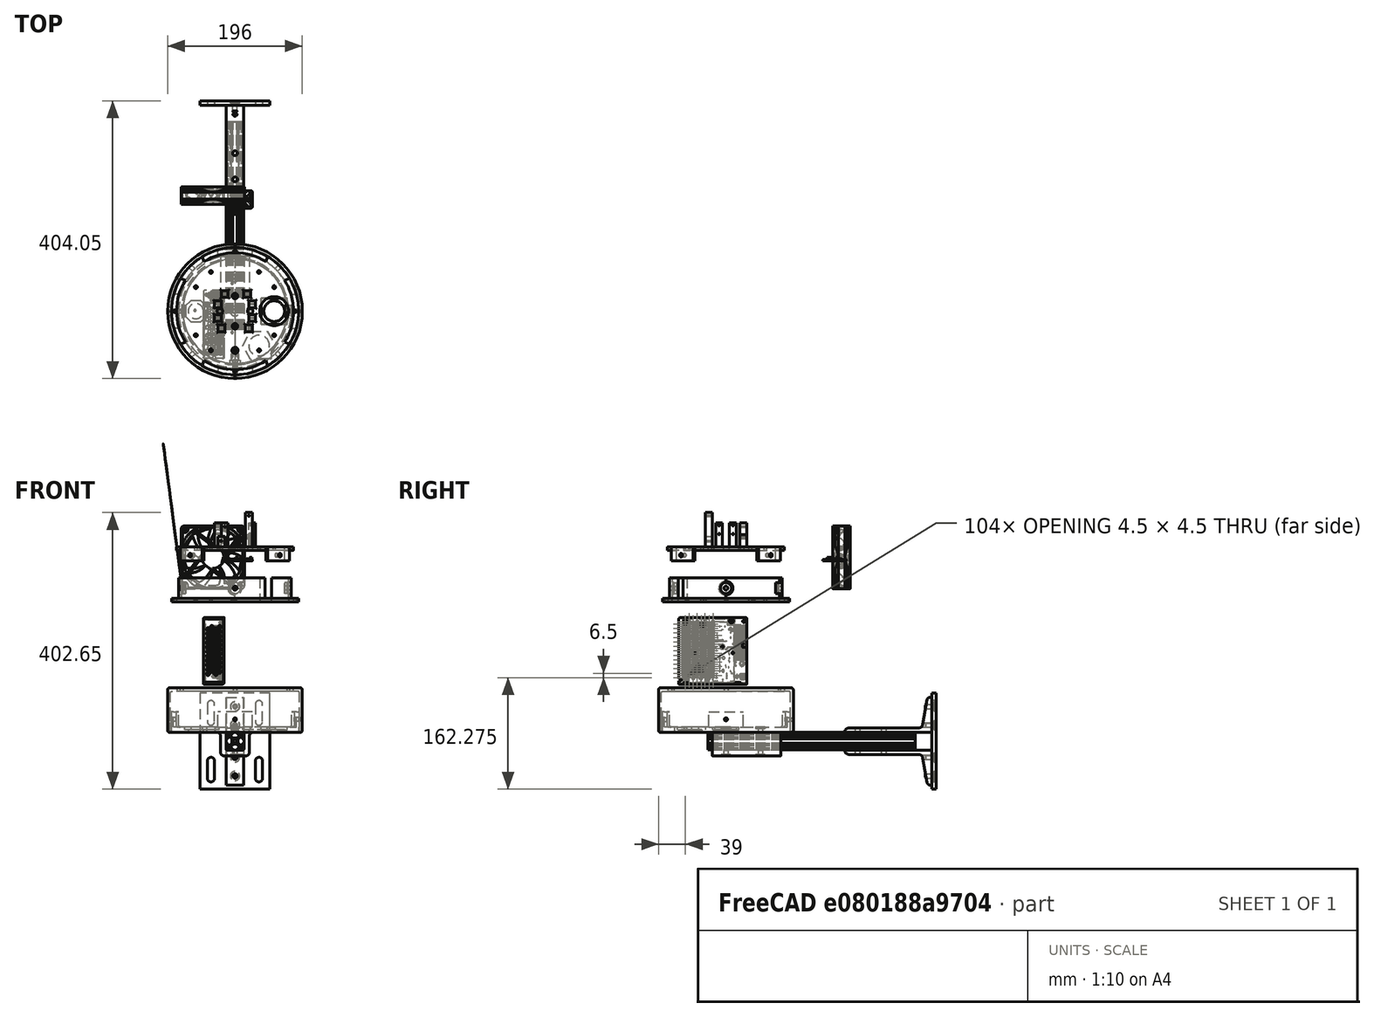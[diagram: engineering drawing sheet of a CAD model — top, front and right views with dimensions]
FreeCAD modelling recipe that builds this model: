
FCSTD DOCUMENT  (FreeCAD 0.20R29410 (Git))
Label: lightModuleV2_2023_11_27
License: All rights reserved
LicenseURL: http://en.wikipedia.org/wiki/All_rights_reserved
objects: Part::Cylinder×131, Sketcher::SketchObject×117, Part::Feature×117, Part::MultiFuse×107, Part::Cut×74, Part::Extrusion×53, Part::Loft×32, Part::Fillet×25, Part::Box×17, App::Part×14, Part::FeaturePython×10, Part::Sphere×4, Mesh::Feature×3, Part::Compound×1, Part::Cone×1, Part::Compound2×1, Part::MultiCommon×1
note: 690 computed .brp shape members not serialized (recipe doc carries the construction recipe); baked Part::Feature solids carry a one-line shape summary decoded from their .brp

FEATURE [Mesh::Feature] Odroid_H004  label="Odroid-H004"
  Placement = pos=(15,-110,-70) rot=(0.57735,-0.57735,0.57735;4.18879rad)
FEATURE [Sketcher::SketchObject] Sketch  label="top"
  FullyConstrained = true
  sketch-geometry (24):
    g0: Circle CenterX=0 CenterY=-150 CenterZ=0 NormalX=0 NormalY=0 NormalZ=1 AngleXU=0 Radius=98
    g1: Circle CenterX=-92 CenterY=-150 CenterZ=0 NormalX=0 NormalY=0 NormalZ=1 AngleXU=0 Radius=2
    g2: Circle CenterX=-57 CenterY=-115 CenterZ=0 NormalX=0 NormalY=0 NormalZ=1 AngleXU=0 Radius=2
    g3: Circle CenterX=-22 CenterY=-150 CenterZ=0 NormalX=0 NormalY=0 NormalZ=1 AngleXU=0 Radius=2
    g4: Circle CenterX=-57 CenterY=-185 CenterZ=0 NormalX=0 NormalY=0 NormalZ=1 AngleXU=0 Radius=2
    g5: Circle CenterX=0 CenterY=-172 CenterZ=0 NormalX=0 NormalY=0 NormalZ=1 AngleXU=0 Radius=2
    g6: Circle CenterX=0 CenterY=-242 CenterZ=0 NormalX=0 NormalY=0 NormalZ=1 AngleXU=0 Radius=2
    g7: Circle CenterX=-35 CenterY=-207 CenterZ=0 NormalX=0 NormalY=0 NormalZ=1 AngleXU=0 Radius=2
    g8: Circle CenterX=35 CenterY=-207 CenterZ=0 NormalX=0 NormalY=0 NormalZ=1 AngleXU=0 Radius=2
    g9: Circle CenterX=57 CenterY=-185 CenterZ=0 NormalX=0 NormalY=0 NormalZ=1 AngleXU=0 Radius=2
    g10: Circle CenterX=22 CenterY=-150 CenterZ=0 NormalX=0 NormalY=0 NormalZ=1 AngleXU=0 Radius=2
    g11: Circle CenterX=57 CenterY=-115 CenterZ=0 NormalX=0 NormalY=0 NormalZ=1 AngleXU=0 Radius=2
    g12: Circle CenterX=92 CenterY=-150 CenterZ=0 NormalX=0 NormalY=0 NormalZ=1 AngleXU=0 Radius=2
    g13: Circle CenterX=0 CenterY=-58 CenterZ=0 NormalX=0 NormalY=0 NormalZ=1 AngleXU=0 Radius=2
    g14: Circle CenterX=0 CenterY=-207 CenterZ=0 NormalX=0 NormalY=0 NormalZ=1 AngleXU=0 Radius=25
    g15: Circle CenterX=57 CenterY=-150 CenterZ=0 NormalX=0 NormalY=0 NormalZ=1 AngleXU=0 Radius=25
    g16: Circle CenterX=0 CenterY=-93 CenterZ=0 NormalX=0 NormalY=0 NormalZ=1 AngleXU=0 Radius=25
    g17: Circle CenterX=-35 CenterY=-93 CenterZ=0 NormalX=0 NormalY=0 NormalZ=1 AngleXU=0 Radius=2
    g18: Circle CenterX=35 CenterY=-93 CenterZ=0 NormalX=0 NormalY=0 NormalZ=1 AngleXU=0 Radius=2
    g19: Circle CenterX=0 CenterY=-128 CenterZ=0 NormalX=0 NormalY=0 NormalZ=1 AngleXU=0 Radius=2
    g20: LineSegment StartX=-75.25 StartY=-129.25 StartZ=0 EndX=-38.75 EndY=-129.25 EndZ=0
    g21: LineSegment StartX=-38.75 StartY=-129.25 StartZ=0 EndX=-38.75 EndY=-170.75 EndZ=0
    g22: LineSegment StartX=-38.75 StartY=-170.75 StartZ=0 EndX=-75.25 EndY=-170.75 EndZ=0
    g23: LineSegment StartX=-75.25 StartY=-170.75 StartZ=0 EndX=-75.25 EndY=-129.25 EndZ=0
  constraints (72):
    c: PointOnObject(g0,g-2)
    c: Radius(g0) = 98
    c: DistanceY(g0) = -150
    c: PointOnObject(g5,g-2)
    c: PointOnObject(g6,g-2)
    c: PointOnObject(g13,g-2)
    c: PointOnObject(g19,g-2)
    c: Equal(g6,g7)
    c: Equal(g6,g4)
    c: Equal(g6,g1)
    c: Equal(g6,g2)
    c: Equal(g6,g3)
    c: Equal(g6,g19)
    c: Equal(g6,g5)
    c: Equal(g6,g8)
    c: Equal(g6,g9)
    c: Equal(g6,g10)
    c: Equal(g6,g12)
    c: Equal(g6,g11)
    c: Equal(g6,g17)
    c: Equal(g6,g18)
    c: Equal(g6,g13)
    c: Radius(g6) = 2
    c: DistanceY(g12,g0) = 0
    c: DistanceY(g10,g0) = 0
    c: DistanceY(g0,g3) = 0
    c: DistanceY(g1,g3) = 0
    c: Equal(g15,g14)
    c: Equal(g15,g16)
    c: Radius(g15) = 25
    c: Coincident(g20,g21)
    c: Coincident(g21,g22)
    c: Coincident(g22,g23)
    c: Coincident(g23,g20)
    c: Horizontal(g20)
    c: Horizontal(g22)
    c: Vertical(g21)
    c: Vertical(g23)
    c: DistanceX(g20) = -38.75
    c: DistanceY(g0,g20) = 20.75
    c: DistanceY(g21,g0) = 20.75
    c: DistanceX(g22,g0) = 75.25
    c: DistanceX(g14,g0) = 0
    c: DistanceX(g0,g15) = 57
    c: DistanceY(g15,g0) = 0
    c: DistanceY(g0,g16) = 57
    c: DistanceX(g16,g0) = 0
    c: DistanceX(g0,g10) = 22
    c: DistanceX(g3,g0) = 22
    c: DistanceX(g1,g0) = 92
    c: DistanceX(g15,g12) = 35
    c: DistanceX(g16,g18) = 35
    c: DistanceX(g17,g16) = 35
    c: DistanceX(g7,g14) = 35
    c: DistanceX(g14,g8) = 35
    c: DistanceX(g9,g15) = 0
    c: DistanceX(g15,g11) = 0
    c: DistanceX(g2,g0) = 57
    c: DistanceY(g18,g16) = 0
    c: DistanceY(g16,g17) = 0
    c: DistanceY(g19,g16) = 35
    c: DistanceY(g16,g13) = 35
    c: DistanceY(g4,g0) = 35
    c: DistanceY(g0,g2) = 35
    c: DistanceY(g14,g5) = 35
    c: DistanceY(g6,g14) = 35
    c: DistanceY(g8,g14) = 0
    c: DistanceY(g14,g7) = 0
    c: DistanceY(g9,g15) = 35
    c: DistanceY(g15,g11) = 35
    c: DistanceX(g4,g2) = 0
    c: DistanceY(g14,g0) = 57
FEATURE [Part::Cylinder] Cylinder036
  Angle = 360
  AttacherType = Attacher::AttachEngine3D
  FirstAngle = 0
  Height = 10
  Placement = pos=(0,-21,0) rot=(0,0,1;0rad)
  Radius = 2
  SecondAngle = 0
FEATURE [Part::Cylinder] Cylinder037
  Angle = 360
  AttacherType = Attacher::AttachEngine3D
  FirstAngle = 0
  Height = 10
  Placement = pos=(20,-21,0) rot=(0,0,1;0rad)
  Radius = 2
  SecondAngle = 0
FEATURE [Part::Cylinder] Cylinder038
  Angle = 360
  AttacherType = Attacher::AttachEngine3D
  FirstAngle = 0
  Height = 10
  Placement = pos=(0,-21,0) rot=(0,0,1;0rad)
  Radius = 2
  SecondAngle = 0
FEATURE [Part::Cylinder] Cylinder039
  Angle = 360
  AttacherType = Attacher::AttachEngine3D
  FirstAngle = 0
  Height = 10
  Placement = pos=(20,-21,0) rot=(0,0,1;0rad)
  Radius = 2
  SecondAngle = 0
FEATURE [Part::Cylinder] Cylinder040  label="base002"
  Angle = 360
  AttacherType = Attacher::AttachEngine3D
  FirstAngle = 0
  Height = 5
  Placement = pos=(5,0,70) rot=(0,0,1;0rad)
  Radius = 40
  SecondAngle = 0
FEATURE [Part::Cylinder] Cylinder041  label="baseCut001"
  Angle = 360
  AttacherType = Attacher::AttachEngine3D
  FirstAngle = 0
  Height = 7
  Placement = pos=(5,0,74) rot=(0,0,1;0rad)
  Radius = 24
  SecondAngle = 0
FEATURE [Part::Cylinder] Cylinder042  label="wireCUt002"
  Angle = 360
  AttacherType = Attacher::AttachEngine3D
  FirstAngle = 0
  Height = 10
  Placement = pos=(-5,0,70) rot=(0,0,1;0rad)
  Radius = 2
  SecondAngle = 0
FEATURE [Part::Cylinder] Cylinder043  label="wireCUt003"
  Angle = 360
  AttacherType = Attacher::AttachEngine3D
  FirstAngle = 0
  Height = 10
  Placement = pos=(15,0,70) rot=(0,0,1;0rad)
  Radius = 2
  SecondAngle = 0
FEATURE [Part::Cylinder] Cylinder044  label="m3Cuts002"
  Angle = 360
  AttacherType = Attacher::AttachEngine3D
  FirstAngle = 0
  Height = 10
  Placement = pos=(5,-9,70) rot=(0,0,1;0rad)
  Radius = 1.75
  SecondAngle = 0
FEATURE [Part::Cylinder] Cylinder045  label="m3Cuts003"
  Angle = 360
  AttacherType = Attacher::AttachEngine3D
  FirstAngle = 0
  Height = 10
  Placement = pos=(5,9,70) rot=(0,0,1;0rad)
  Radius = 1.75
  SecondAngle = 0
FEATURE [Part::Cylinder] Cylinder046  label="m2HeatSetInsets004"
  Angle = 360
  AttacherType = Attacher::AttachEngine3D
  FirstAngle = 0
  Height = 10
  Placement = pos=(-30,0,65) rot=(0,0,1;0rad)
  Radius = 1.6
  SecondAngle = 0
FEATURE [Part::Cylinder] Cylinder047  label="m2HeatSetInsets005"
  Angle = 360
  AttacherType = Attacher::AttachEngine3D
  FirstAngle = 0
  Height = 10
  Placement = pos=(40,0,65) rot=(0,0,1;0rad)
  Radius = 1.6
  SecondAngle = 0
FEATURE [Part::Cylinder] Cylinder048  label="m2HeatSetInsets006"
  Angle = 360
  AttacherType = Attacher::AttachEngine3D
  FirstAngle = 0
  Height = 10
  Placement = pos=(5,35,65) rot=(0,0,1;0rad)
  Radius = 1.6
  SecondAngle = 0
FEATURE [Part::Cylinder] Cylinder049  label="m2HeatSetInsets007"
  Angle = 360
  AttacherType = Attacher::AttachEngine3D
  FirstAngle = 0
  Height = 10
  Placement = pos=(5,-35,65) rot=(0,0,1;0rad)
  Radius = 1.6
  SecondAngle = 0
FEATURE [Part::MultiFuse] Fusion014  label="m3HeatSetCuts003"
  Placement = pos=(-5,38.5,70) rot=(0,0,1;0rad)
  Shapes = -> [Cylinder037,Cylinder036]
FEATURE [Part::MultiFuse] Fusion015  label="m3HeatSetCuts004"
  Placement = pos=(-5,3.5,70) rot=(0,0,1;0rad)
  Shapes = -> [Cylinder039,Cylinder038]
FEATURE [Part::MultiFuse] Fusion016  label="m3HeatSetCuts005"
  Shapes = -> [Fusion015,Fusion014]
FEATURE [Part::MultiFuse] Fusion017  label="wireCuts001"
  Shapes = -> [Cylinder042,Cylinder043]
FEATURE [Part::MultiFuse] Fusion018  label="m3Cute001"
  Shapes = -> [Cylinder044,Cylinder045]
FEATURE [Part::MultiFuse] Fusion019  label="baseCUts001"
  Shapes = -> [Fusion016,Fusion017,Fusion018]
FEATURE [Part::MultiFuse] Fusion021
  Shapes = -> [Cylinder046,Cylinder047,Cylinder048,Cylinder049]
FEATURE [Part::Sphere] Sphere002  label="SphereBase001"
  Angle1 = 0
  Angle2 = 12
  Angle3 = 360
  AttacherType = Attacher::AttachEngine3D
  Placement = pos=(5,0,74) rot=(0,0,1;0rad)
  Radius = 29
FEATURE [Part::Cut] Cut006
  Base = -> Sphere002
  Tool = -> Cylinder041
FEATURE [Part::MultiFuse] Fusion020  label="base003"
  Shapes = -> [Cylinder040,Cut006]
FEATURE [Part::Cut] Cut007
  Base = -> Fusion020
  Tool = -> Fusion019
FEATURE [Part::Cut] Cut008  label="lightModule001"
  Base = -> Cut007
  Placement = pos=(-5,-207,0) rot=(0,1,0;0rad)
  Tool = -> Fusion021
FEATURE [Part::Box] Box005  label="as7265x"
  AttacherType = Attacher::AttachEngine3D
  Height = 2
  Length = 36
  Placement = pos=(-75,-170.5,110) rot=(0,0,1;0rad)
  Width = 41
FEATURE [Part::Cylinder] Cylinder050
  Angle = 360
  AttacherType = Attacher::AttachEngine3D
  FirstAngle = 0
  Height = 10
  Placement = pos=(0,-21,0) rot=(0,0,1;0rad)
  Radius = 2
  SecondAngle = 0
FEATURE [Part::Cylinder] Cylinder051
  Angle = 360
  AttacherType = Attacher::AttachEngine3D
  FirstAngle = 0
  Height = 10
  Placement = pos=(20,-21,0) rot=(0,0,1;0rad)
  Radius = 2
  SecondAngle = 0
FEATURE [Part::Cylinder] Cylinder052
  Angle = 360
  AttacherType = Attacher::AttachEngine3D
  FirstAngle = 0
  Height = 10
  Placement = pos=(0,-21,0) rot=(0,0,1;0rad)
  Radius = 2
  SecondAngle = 0
FEATURE [Part::Cylinder] Cylinder053
  Angle = 360
  AttacherType = Attacher::AttachEngine3D
  FirstAngle = 0
  Height = 10
  Placement = pos=(20,-21,0) rot=(0,0,1;0rad)
  Radius = 2
  SecondAngle = 0
FEATURE [Part::Cylinder] Cylinder054  label="base004"
  Angle = 360
  AttacherType = Attacher::AttachEngine3D
  FirstAngle = 0
  Height = 5
  Placement = pos=(5,0,70) rot=(0,0,1;0rad)
  Radius = 40
  SecondAngle = 0
FEATURE [Part::Cylinder] Cylinder055  label="baseCut002"
  Angle = 360
  AttacherType = Attacher::AttachEngine3D
  FirstAngle = 0
  Height = 7
  Placement = pos=(5,0,74) rot=(0,0,1;0rad)
  Radius = 24
  SecondAngle = 0
FEATURE [Part::Cylinder] Cylinder056  label="wireCUt004"
  Angle = 360
  AttacherType = Attacher::AttachEngine3D
  FirstAngle = 0
  Height = 10
  Placement = pos=(-5,0,70) rot=(0,0,1;0rad)
  Radius = 2
  SecondAngle = 0
FEATURE [Part::Cylinder] Cylinder057  label="wireCUt005"
  Angle = 360
  AttacherType = Attacher::AttachEngine3D
  FirstAngle = 0
  Height = 10
  Placement = pos=(15,0,70) rot=(0,0,1;0rad)
  Radius = 2
  SecondAngle = 0
FEATURE [Part::Cylinder] Cylinder058  label="m3Cuts004"
  Angle = 360
  AttacherType = Attacher::AttachEngine3D
  FirstAngle = 0
  Height = 10
  Placement = pos=(5,-9,70) rot=(0,0,1;0rad)
  Radius = 1.75
  SecondAngle = 0
FEATURE [Part::Cylinder] Cylinder059  label="m3Cuts005"
  Angle = 360
  AttacherType = Attacher::AttachEngine3D
  FirstAngle = 0
  Height = 10
  Placement = pos=(5,9,70) rot=(0,0,1;0rad)
  Radius = 1.75
  SecondAngle = 0
FEATURE [Part::Cylinder] Cylinder060  label="m2HeatSetInsets008"
  Angle = 360
  AttacherType = Attacher::AttachEngine3D
  FirstAngle = 0
  Height = 10
  Placement = pos=(-30,0,65) rot=(0,0,1;0rad)
  Radius = 1.6
  SecondAngle = 0
FEATURE [Part::Cylinder] Cylinder061  label="m2HeatSetInsets009"
  Angle = 360
  AttacherType = Attacher::AttachEngine3D
  FirstAngle = 0
  Height = 10
  Placement = pos=(40,0,65) rot=(0,0,1;0rad)
  Radius = 1.6
  SecondAngle = 0
FEATURE [Part::Cylinder] Cylinder062  label="m2HeatSetInsets010"
  Angle = 360
  AttacherType = Attacher::AttachEngine3D
  FirstAngle = 0
  Height = 10
  Placement = pos=(5,35,65) rot=(0,0,1;0rad)
  Radius = 1.6
  SecondAngle = 0
FEATURE [Part::Cylinder] Cylinder063  label="m2HeatSetInsets011"
  Angle = 360
  AttacherType = Attacher::AttachEngine3D
  FirstAngle = 0
  Height = 10
  Placement = pos=(5,-35,65) rot=(0,0,1;0rad)
  Radius = 1.6
  SecondAngle = 0
FEATURE [Part::MultiFuse] Fusion022  label="m3HeatSetCuts006"
  Placement = pos=(-5,38.5,70) rot=(0,0,1;0rad)
  Shapes = -> [Cylinder051,Cylinder050]
FEATURE [Part::MultiFuse] Fusion023  label="m3HeatSetCuts007"
  Placement = pos=(-5,3.5,70) rot=(0,0,1;0rad)
  Shapes = -> [Cylinder053,Cylinder052]
FEATURE [Part::MultiFuse] Fusion024  label="m3HeatSetCuts008"
  Shapes = -> [Fusion023,Fusion022]
FEATURE [Part::MultiFuse] Fusion025  label="wireCuts002"
  Shapes = -> [Cylinder056,Cylinder057]
FEATURE [Part::MultiFuse] Fusion026  label="m3Cute002"
  Shapes = -> [Cylinder058,Cylinder059]
FEATURE [Part::MultiFuse] Fusion027  label="baseCUts002"
  Shapes = -> [Fusion024,Fusion025,Fusion026]
FEATURE [Part::MultiFuse] Fusion029
  Shapes = -> [Cylinder060,Cylinder061,Cylinder062,Cylinder063]
FEATURE [Part::Sphere] Sphere003  label="SphereBase002"
  Angle1 = 0
  Angle2 = 12
  Angle3 = 360
  AttacherType = Attacher::AttachEngine3D
  Placement = pos=(5,0,74) rot=(0,0,1;0rad)
  Radius = 29
FEATURE [Part::Cut] Cut009
  Base = -> Sphere003
  Tool = -> Cylinder055
FEATURE [Part::MultiFuse] Fusion028  label="base005"
  Shapes = -> [Cylinder054,Cut009]
FEATURE [Part::Cut] Cut010
  Base = -> Fusion028
  Tool = -> Fusion027
FEATURE [Part::Cut] Cut011  label="lightModule002"
  Base = -> Cut010
  Placement = pos=(-62,-150,0) rot=(0,1,0;0rad)
  Tool = -> Fusion029
FEATURE [Part::Cylinder] Cylinder064
  Angle = 360
  AttacherType = Attacher::AttachEngine3D
  FirstAngle = 0
  Height = 10
  Placement = pos=(0,-21,0) rot=(0,0,1;0rad)
  Radius = 2
  SecondAngle = 0
FEATURE [Part::Cylinder] Cylinder065
  Angle = 360
  AttacherType = Attacher::AttachEngine3D
  FirstAngle = 0
  Height = 10
  Placement = pos=(20,-21,0) rot=(0,0,1;0rad)
  Radius = 2
  SecondAngle = 0
FEATURE [Part::Cylinder] Cylinder066
  Angle = 360
  AttacherType = Attacher::AttachEngine3D
  FirstAngle = 0
  Height = 10
  Placement = pos=(0,-21,0) rot=(0,0,1;0rad)
  Radius = 2
  SecondAngle = 0
FEATURE [Part::Cylinder] Cylinder067
  Angle = 360
  AttacherType = Attacher::AttachEngine3D
  FirstAngle = 0
  Height = 10
  Placement = pos=(20,-21,0) rot=(0,0,1;0rad)
  Radius = 2
  SecondAngle = 0
FEATURE [Part::Cylinder] Cylinder068  label="base006"
  Angle = 360
  AttacherType = Attacher::AttachEngine3D
  FirstAngle = 0
  Height = 5
  Placement = pos=(5,0,70) rot=(0,0,1;0rad)
  Radius = 40
  SecondAngle = 0
FEATURE [Part::Cylinder] Cylinder069  label="baseCut003"
  Angle = 360
  AttacherType = Attacher::AttachEngine3D
  FirstAngle = 0
  Height = 7
  Placement = pos=(5,0,74) rot=(0,0,1;0rad)
  Radius = 24
  SecondAngle = 0
FEATURE [Part::Cylinder] Cylinder070  label="wireCUt006"
  Angle = 360
  AttacherType = Attacher::AttachEngine3D
  FirstAngle = 0
  Height = 10
  Placement = pos=(-5,0,70) rot=(0,0,1;0rad)
  Radius = 2
  SecondAngle = 0
FEATURE [Part::Cylinder] Cylinder071  label="wireCUt007"
  Angle = 360
  AttacherType = Attacher::AttachEngine3D
  FirstAngle = 0
  Height = 10
  Placement = pos=(15,0,70) rot=(0,0,1;0rad)
  Radius = 2
  SecondAngle = 0
FEATURE [Part::Cylinder] Cylinder072  label="m3Cuts006"
  Angle = 360
  AttacherType = Attacher::AttachEngine3D
  FirstAngle = 0
  Height = 10
  Placement = pos=(5,-9,70) rot=(0,0,1;0rad)
  Radius = 1.75
  SecondAngle = 0
FEATURE [Part::Cylinder] Cylinder073  label="m3Cuts007"
  Angle = 360
  AttacherType = Attacher::AttachEngine3D
  FirstAngle = 0
  Height = 10
  Placement = pos=(5,9,70) rot=(0,0,1;0rad)
  Radius = 1.75
  SecondAngle = 0
FEATURE [Part::Cylinder] Cylinder074  label="m2HeatSetInsets012"
  Angle = 360
  AttacherType = Attacher::AttachEngine3D
  FirstAngle = 0
  Height = 10
  Placement = pos=(-30,0,65) rot=(0,0,1;0rad)
  Radius = 1.6
  SecondAngle = 0
FEATURE [Part::Cylinder] Cylinder075  label="m2HeatSetInsets013"
  Angle = 360
  AttacherType = Attacher::AttachEngine3D
  FirstAngle = 0
  Height = 10
  Placement = pos=(40,0,65) rot=(0,0,1;0rad)
  Radius = 1.6
  SecondAngle = 0
FEATURE [Part::Cylinder] Cylinder076  label="m2HeatSetInsets014"
  Angle = 360
  AttacherType = Attacher::AttachEngine3D
  FirstAngle = 0
  Height = 10
  Placement = pos=(5,35,65) rot=(0,0,1;0rad)
  Radius = 1.6
  SecondAngle = 0
FEATURE [Part::Cylinder] Cylinder077  label="m2HeatSetInsets015"
  Angle = 360
  AttacherType = Attacher::AttachEngine3D
  FirstAngle = 0
  Height = 10
  Placement = pos=(5,-35,65) rot=(0,0,1;0rad)
  Radius = 1.6
  SecondAngle = 0
FEATURE [Part::MultiFuse] Fusion030  label="m3HeatSetCuts009"
  Placement = pos=(-5,38.5,70) rot=(0,0,1;0rad)
  Shapes = -> [Cylinder065,Cylinder064]
FEATURE [Part::MultiFuse] Fusion031  label="m3HeatSetCuts010"
  Placement = pos=(-5,3.5,70) rot=(0,0,1;0rad)
  Shapes = -> [Cylinder067,Cylinder066]
FEATURE [Part::MultiFuse] Fusion032  label="m3HeatSetCuts011"
  Shapes = -> [Fusion031,Fusion030]
FEATURE [Part::MultiFuse] Fusion033  label="wireCuts003"
  Shapes = -> [Cylinder070,Cylinder071]
FEATURE [Part::MultiFuse] Fusion034  label="m3Cute003"
  Shapes = -> [Cylinder072,Cylinder073]
FEATURE [Part::MultiFuse] Fusion035  label="baseCUts003"
  Shapes = -> [Fusion032,Fusion033,Fusion034]
FEATURE [Part::MultiFuse] Fusion037
  Shapes = -> [Cylinder074,Cylinder075,Cylinder076,Cylinder077]
FEATURE [Part::Sphere] Sphere004  label="SphereBase003"
  Angle1 = 0
  Angle2 = 12
  Angle3 = 360
  AttacherType = Attacher::AttachEngine3D
  Placement = pos=(5,0,74) rot=(0,0,1;0rad)
  Radius = 29
FEATURE [Part::Cut] Cut012
  Base = -> Sphere004
  Tool = -> Cylinder069
FEATURE [Part::MultiFuse] Fusion036  label="base007"
  Shapes = -> [Cylinder068,Cut012]
FEATURE [Part::Cut] Cut013
  Base = -> Fusion036
  Tool = -> Fusion035
FEATURE [Part::Cut] Cut014  label="lightModule003"
  Base = -> Cut013
  Placement = pos=(52,-150,0) rot=(0,1,0;0rad)
  Tool = -> Fusion037
FEATURE [Part::Cylinder] Cylinder078
  Angle = 360
  AttacherType = Attacher::AttachEngine3D
  FirstAngle = 0
  Height = 10
  Placement = pos=(0,-21,0) rot=(0,0,1;0rad)
  Radius = 2
  SecondAngle = 0
FEATURE [Part::Cylinder] Cylinder079
  Angle = 360
  AttacherType = Attacher::AttachEngine3D
  FirstAngle = 0
  Height = 10
  Placement = pos=(20,-21,0) rot=(0,0,1;0rad)
  Radius = 2
  SecondAngle = 0
FEATURE [Part::Cylinder] Cylinder080
  Angle = 360
  AttacherType = Attacher::AttachEngine3D
  FirstAngle = 0
  Height = 10
  Placement = pos=(0,-21,0) rot=(0,0,1;0rad)
  Radius = 2
  SecondAngle = 0
FEATURE [Part::Cylinder] Cylinder081
  Angle = 360
  AttacherType = Attacher::AttachEngine3D
  FirstAngle = 0
  Height = 10
  Placement = pos=(20,-21,0) rot=(0,0,1;0rad)
  Radius = 2
  SecondAngle = 0
FEATURE [Part::Cylinder] Cylinder082  label="base008"
  Angle = 360
  AttacherType = Attacher::AttachEngine3D
  FirstAngle = 0
  Height = 5
  Placement = pos=(5,0,70) rot=(0,0,1;0rad)
  Radius = 40
  SecondAngle = 0
FEATURE [Part::Cylinder] Cylinder083  label="baseCut004"
  Angle = 360
  AttacherType = Attacher::AttachEngine3D
  FirstAngle = 0
  Height = 7
  Placement = pos=(5,0,74) rot=(0,0,1;0rad)
  Radius = 24
  SecondAngle = 0
FEATURE [Part::Cylinder] Cylinder084  label="wireCUt008"
  Angle = 360
  AttacherType = Attacher::AttachEngine3D
  FirstAngle = 0
  Height = 10
  Placement = pos=(-5,0,70) rot=(0,0,1;0rad)
  Radius = 2
  SecondAngle = 0
FEATURE [Part::Cylinder] Cylinder085  label="wireCUt009"
  Angle = 360
  AttacherType = Attacher::AttachEngine3D
  FirstAngle = 0
  Height = 10
  Placement = pos=(15,0,70) rot=(0,0,1;0rad)
  Radius = 2
  SecondAngle = 0
FEATURE [Part::Cylinder] Cylinder086  label="m3Cuts008"
  Angle = 360
  AttacherType = Attacher::AttachEngine3D
  FirstAngle = 0
  Height = 10
  Placement = pos=(5,-9,70) rot=(0,0,1;0rad)
  Radius = 1.75
  SecondAngle = 0
FEATURE [Part::Cylinder] Cylinder087  label="m3Cuts009"
  Angle = 360
  AttacherType = Attacher::AttachEngine3D
  FirstAngle = 0
  Height = 10
  Placement = pos=(5,9,70) rot=(0,0,1;0rad)
  Radius = 1.75
  SecondAngle = 0
FEATURE [Part::Cylinder] Cylinder088  label="m2HeatSetInsets016"
  Angle = 360
  AttacherType = Attacher::AttachEngine3D
  FirstAngle = 0
  Height = 10
  Placement = pos=(-30,0,65) rot=(0,0,1;0rad)
  Radius = 1.6
  SecondAngle = 0
FEATURE [Part::Cylinder] Cylinder089  label="m2HeatSetInsets017"
  Angle = 360
  AttacherType = Attacher::AttachEngine3D
  FirstAngle = 0
  Height = 10
  Placement = pos=(40,0,65) rot=(0,0,1;0rad)
  Radius = 1.6
  SecondAngle = 0
FEATURE [Part::Cylinder] Cylinder090  label="m2HeatSetInsets018"
  Angle = 360
  AttacherType = Attacher::AttachEngine3D
  FirstAngle = 0
  Height = 10
  Placement = pos=(5,35,65) rot=(0,0,1;0rad)
  Radius = 1.6
  SecondAngle = 0
FEATURE [Part::Cylinder] Cylinder091  label="m2HeatSetInsets019"
  Angle = 360
  AttacherType = Attacher::AttachEngine3D
  FirstAngle = 0
  Height = 10
  Placement = pos=(5,-35,65) rot=(0,0,1;0rad)
  Radius = 1.6
  SecondAngle = 0
FEATURE [Part::MultiFuse] Fusion038  label="m3HeatSetCuts012"
  Placement = pos=(-5,38.5,70) rot=(0,0,1;0rad)
  Shapes = -> [Cylinder079,Cylinder078]
FEATURE [Part::MultiFuse] Fusion039  label="m3HeatSetCuts013"
  Placement = pos=(-5,3.5,70) rot=(0,0,1;0rad)
  Shapes = -> [Cylinder081,Cylinder080]
FEATURE [Part::MultiFuse] Fusion040  label="m3HeatSetCuts014"
  Shapes = -> [Fusion039,Fusion038]
FEATURE [Part::MultiFuse] Fusion041  label="wireCuts004"
  Shapes = -> [Cylinder084,Cylinder085]
FEATURE [Part::MultiFuse] Fusion042  label="m3Cute004"
  Shapes = -> [Cylinder086,Cylinder087]
FEATURE [Part::MultiFuse] Fusion043  label="baseCUts004"
  Shapes = -> [Fusion040,Fusion041,Fusion042]
FEATURE [Part::MultiFuse] Fusion045
  Shapes = -> [Cylinder088,Cylinder089,Cylinder090,Cylinder091]
FEATURE [Part::Sphere] Sphere005  label="SphereBase004"
  Angle1 = 0
  Angle2 = 12
  Angle3 = 360
  AttacherType = Attacher::AttachEngine3D
  Placement = pos=(5,0,74) rot=(0,0,1;0rad)
  Radius = 29
FEATURE [Part::Cut] Cut015
  Base = -> Sphere005
  Tool = -> Cylinder083
FEATURE [Part::MultiFuse] Fusion044  label="base009"
  Shapes = -> [Cylinder082,Cut015]
FEATURE [Part::Cut] Cut016
  Base = -> Fusion044
  Tool = -> Fusion043
FEATURE [Part::Cut] Cut017  label="lightModule004"
  Base = -> Cut016
  Placement = pos=(-5,-93,0) rot=(0,1,0;0rad)
  Tool = -> Fusion045
FEATURE [Part::MultiFuse] Fusion  label="lightModules"
  Placement = pos=(0,0,30) rot=(0,0,1;0rad)
  Shapes = -> [Cut008,Cut011,Cut014,Cut017]
FEATURE [Part::Extrusion] Extrude  label="top001"
  Base = -> Sketch
  Dir = (0,0,1)
  DirMode = 2
  FaceMakerClass = Part::FaceMakerBullseye
  LengthFwd = 5
  LengthRev = 0
  Placement = pos=(0,0,100) rot=(0,0,1;0rad)
  Solid = true
  Symmetric = false
FEATURE [Part::Feature] Part__Feature  label="elpCamera"
  Placement = pos=(57,-150,90) rot=(0,0,1;0rad)
  shape: bbox 38 x 38 x 25.12 mm, 164 faces (baked)
FEATURE [Part::FeaturePython] Tube  label="tube001"  # WARN: FeaturePython — macro-defined, semantics opaque (R4)
  AttacherType = Attacher::AttachEngine3D
  Height = 20
  InnerRadius = 94
  OuterRadius = 98
  Placement = pos=(0,-150,80) rot=(0,0,1;0rad)
FEATURE [Part::Feature] Part__Feature010  label="veml6075_sensor"
  Placement = pos=(0,-92,105) rot=(0,0,1;0rad)
  shape: bbox 15.31 x 17.01 x 46.02 mm, 450 faces (baked)
FEATURE [Sketcher::SketchObject] Sketch001
  FullyConstrained = true
  Placement = pos=(0,0,105) rot=(0,0,1;0rad)
  sketch-geometry (14):
    g0: Circle CenterX=0 CenterY=-93 CenterZ=0 NormalX=0 NormalY=0 NormalZ=1 AngleXU=0 Radius=25
    g1: Circle CenterX=0 CenterY=-93 CenterZ=0 NormalX=0 NormalY=0 NormalZ=1 AngleXU=0 Radius=26.5
    g2: Circle CenterX=57 CenterY=-150 CenterZ=0 NormalX=0 NormalY=0 NormalZ=1 AngleXU=0 Radius=25
    g3: Circle CenterX=57 CenterY=-150 CenterZ=0 NormalX=0 NormalY=0 NormalZ=1 AngleXU=0 Radius=26.5
    g4: Circle CenterX=0 CenterY=-207 CenterZ=0 NormalX=0 NormalY=0 NormalZ=1 AngleXU=0 Radius=25
    g5: Circle CenterX=0 CenterY=-207 CenterZ=0 NormalX=0 NormalY=0 NormalZ=1 AngleXU=0 Radius=26.5
    g6: LineSegment StartX=-75.25 StartY=-129.25 StartZ=0 EndX=-38.75 EndY=-129.25 EndZ=0
    g7: LineSegment StartX=-38.75 StartY=-129.25 StartZ=0 EndX=-38.75 EndY=-170.75 EndZ=0
    g8: LineSegment StartX=-38.75 StartY=-170.75 StartZ=0 EndX=-75.25 EndY=-170.75 EndZ=0
    g9: LineSegment StartX=-75.25 StartY=-170.75 StartZ=0 EndX=-75.25 EndY=-129.25 EndZ=0
    g10: LineSegment StartX=-75.7 StartY=-128.8 StartZ=0 EndX=-38.3 EndY=-128.8 EndZ=0
    g11: LineSegment StartX=-38.3 StartY=-128.8 StartZ=0 EndX=-38.3 EndY=-171.2 EndZ=0
    g12: LineSegment StartX=-38.3 StartY=-171.2 StartZ=0 EndX=-75.7 EndY=-171.2 EndZ=0
    g13: LineSegment StartX=-75.7 StartY=-171.2 StartZ=0 EndX=-75.7 EndY=-128.8 EndZ=0
  constraints (39):
    c: PointOnObject(g0,g-2)
    c: Coincident(g1,g0)
    c: Coincident(g3,g2)
    c: PointOnObject(g4,g-2)
    c: Coincident(g5,g4)
    c: Coincident(g6,g7)
    c: Coincident(g7,g8)
    c: Coincident(g8,g9)
    c: Coincident(g9,g6)
    c: Horizontal(g6)
    c: Horizontal(g8)
    c: Vertical(g7)
    c: Vertical(g9)
    c: DistanceY(g0) = -93
    c: DistanceY(g2) = -150
    c: DistanceX(g2) = 57
    c: Equal(g0,g2)
    c: Equal(g0,g4)
    c: Radius(g0) = 25
    c: Equal(g3,g1)
    c: Equal(g3,g5)
    c: Radius(g3) = 26.5
    c: DistanceY(g4) = -207
    c: DistanceY(g7) = -170.75
    c: DistanceX(g7) = -38.75
    c: DistanceX(g6) = -75.25
    c: DistanceY(g6) = -129.25
    c: Coincident(g10,g11)
    c: Coincident(g11,g12)
    c: Coincident(g12,g13)
    c: Coincident(g13,g10)
    c: Horizontal(g10)
    c: Horizontal(g12)
    c: Vertical(g11)
    c: Vertical(g13)
    c: DistanceY(g11,g7) = 0.45
    c: DistanceX(g7,g11) = 0.45
    c: DistanceX(g10,g6) = 0.45
    c: DistanceY(g6,g10) = 0.45
FEATURE [Part::Extrusion] Extrude001
  Base = -> Sketch001
  Dir = (0,0,1)
  DirMode = 2
  FaceMakerClass = Part::FaceMakerBullseye
  LengthFwd = 1
  LengthRev = 0
  Solid = true
  Symmetric = false
FEATURE [Part::MultiFuse] Fusion046  label="top002"
  Shapes = -> [Extrude001,Extrude]
FEATURE [Part::Cylinder] Cylinder
  Angle = 360
  AttacherType = Attacher::AttachEngine3D
  FirstAngle = 0
  Height = 300
  Placement = pos=(0,0,90) rot=(1,0,0;1.5708rad)
  Radius = 2.2
  SecondAngle = 0
FEATURE [Part::Cylinder] Cylinder092
  Angle = 360
  AttacherType = Attacher::AttachEngine3D
  FirstAngle = 0
  Height = 300
  Placement = pos=(-150,-150,90) rot=(0.57735,0.57735,0.57735;2.0944rad)
  Radius = 2.2
  SecondAngle = 0
FEATURE [Part::MultiFuse] Fusion047  label="m4Cuts"
  Shapes = -> [Cylinder092,Cylinder]
FEATURE [Part::Fillet] Fillet  label="top003"
  Base = -> Fusion046
  Edges = 1 edges r=2: [Edge3]
FEATURE [Part::Fillet] Fillet001  label="tube"
  Base = -> Tube
  Edges = 1 edges r=2: [Edge5]
FEATURE [Part::MultiFuse] Fusion048  label="top004"
  Shapes = -> [Fillet,Fillet001]
FEATURE [Part::Cut] Cut  label="top005"
  Base = -> Fusion048
  Tool = -> Fusion047
FEATURE [Part::Cylinder] Cylinder094  label="refModules"
  Angle = 360
  AttacherType = Attacher::AttachEngine3D
  FirstAngle = 0
  Height = 75
  Placement = pos=(0,-207,37) rot=(0,0,1;0rad)
  Radius = 3.75
  SecondAngle = 0
FEATURE [Part::Cylinder] Cylinder095  label="refModulesCoverCut"
  Angle = 360
  AttacherType = Attacher::AttachEngine3D
  FirstAngle = 0
  Height = 60
  Placement = pos=(0,-207,37) rot=(0,0,1;0rad)
  Radius = 4.5
  SecondAngle = 0
FEATURE [Sketcher::SketchObject] Sketch002
  FullyConstrained = true
  sketch-geometry (16):
    g0: Circle CenterX=-67 CenterY=-167.5 CenterZ=0 NormalX=0 NormalY=0 NormalZ=1 AngleXU=0 Radius=1.625
    g1: Circle CenterX=-47 CenterY=-167.5 CenterZ=0 NormalX=0 NormalY=0 NormalZ=1 AngleXU=0 Radius=1.625
    g2: Circle CenterX=-67 CenterY=-132.5 CenterZ=0 NormalX=0 NormalY=0 NormalZ=1 AngleXU=0 Radius=1.625
    g3: Circle CenterX=-47 CenterY=-132.5 CenterZ=0 NormalX=0 NormalY=0 NormalZ=1 AngleXU=0 Radius=1.625
    g4: LineSegment StartX=-62 StartY=-129.75 StartZ=0 EndX=-72 EndY=-129.75 EndZ=0
    g5: LineSegment StartX=-52 StartY=-129.75 StartZ=0 EndX=-42 EndY=-129.75 EndZ=0
    g6: LineSegment StartX=-72 StartY=-129.75 StartZ=0 EndX=-72 EndY=-170.25 EndZ=0
    g7: LineSegment StartX=-72 StartY=-170.25 StartZ=0 EndX=-62 EndY=-170.25 EndZ=0
    g8: LineSegment StartX=-62 StartY=-170.25 StartZ=0 EndX=-62 EndY=-155 EndZ=0
    g9: LineSegment StartX=-52 StartY=-155 StartZ=0 EndX=-52 EndY=-170.25 EndZ=0
    g10: LineSegment StartX=-52 StartY=-170.25 StartZ=0 EndX=-42 EndY=-170.25 EndZ=0
    g11: LineSegment StartX=-42 StartY=-170.25 StartZ=0 EndX=-42 EndY=-129.75 EndZ=0
    g12: LineSegment StartX=-62 StartY=-155 StartZ=0 EndX=-52 EndY=-155 EndZ=0
    g13: LineSegment StartX=-62 StartY=-129.75 StartZ=0 EndX=-62 EndY=-145 EndZ=0
    g14: LineSegment StartX=-62 StartY=-145 StartZ=0 EndX=-52 EndY=-145 EndZ=0
    g15: LineSegment StartX=-52 StartY=-145 StartZ=0 EndX=-52 EndY=-129.75 EndZ=0
  constraints (48):
    c: DistanceY(g2,g3) = 0
    c: DistanceX(g0,g2) = 0
    c: DistanceX(g1,g3) = 0
    c: DistanceX(g1) = -47
    c: DistanceY(g1) = -167.5
    c: DistanceX(g0,g1) = 20
    c: Horizontal(g4)
    c: Horizontal(g5)
    c: Vertical(g6)
    c: Coincident(g7,g6)
    c: Horizontal(g7)
    c: Coincident(g8,g7)
    c: Vertical(g9)
    c: Coincident(g10,g9)
    c: Horizontal(g10)
    c: Coincident(g11,g10)
    c: Vertical(g8)
    c: DistanceX(g4,g4) = 10
    c: DistanceX(g5,g5) = 10
    c: DistanceX(g6,g7) = 10
    c: DistanceX(g9,g10) = 10
    c: Vertical(g11)
    c: DistanceY(g7,g9) = 0
    c: DistanceY(g4,g5) = 0
    c: DistanceX(g6,g0) = 5
    c: DistanceX(g9,g1) = 5
    c: DistanceY(g2,g4) = 2.75
    c: Coincident(g4,g6)
    c: Coincident(g12,g8)
    c: Horizontal(g12)
    c: Coincident(g9,g12)
    c: Coincident(g13,g4)
    c: Vertical(g13)
    c: Coincident(g14,g13)
    c: Horizontal(g14)
    c: Coincident(g15,g14)
    c: Coincident(g15,g5)
    c: Vertical(g15)
    c: Coincident(g5,g11)
    c: DistanceY(g8,g13) = 10
    c: DistanceY(g13) = -145
    c: DistanceY(g7,g0) = 2.75
    c: Equal(g1,g0)
    c: Equal(g1,g2)
    c: Equal(g1,g3)
    c: Diameter(g1) = 3.25
    c: DistanceY(g1,g0) = 0
    c: DistanceY(g2) = -132.5
FEATURE [Sketcher::SketchObject] Sketch003
  FullyConstrained = true
  sketch-geometry (6):
    g0: Circle CenterX=74 CenterY=-167 CenterZ=0 NormalX=0 NormalY=0 NormalZ=1 AngleXU=0 Radius=1.65
    g1: Circle CenterX=40 CenterY=-167 CenterZ=0 NormalX=0 NormalY=0 NormalZ=1 AngleXU=0 Radius=1.65
    g2: Circle CenterX=40 CenterY=-133 CenterZ=0 NormalX=0 NormalY=0 NormalZ=1 AngleXU=0 Radius=1.65
    g3: Circle CenterX=74 CenterY=-133 CenterZ=0 NormalX=0 NormalY=0 NormalZ=1 AngleXU=0 Radius=1.65
    g4: Circle CenterX=57 CenterY=-150 CenterZ=0 NormalX=0 NormalY=0 NormalZ=1 AngleXU=0 Radius=27.5
    g5: Circle CenterX=57 CenterY=-150 CenterZ=0 NormalX=0 NormalY=0 NormalZ=1 AngleXU=0 Radius=21
  constraints (17):
    c: Equal(g3,g0)
    c: Equal(g3,g1)
    c: Equal(g3,g2)
    c: Diameter(g3) = 3.3
    c: DistanceX(g1) = 40
    c: DistanceY(g1) = -167
    c: DistanceY(g1,g0) = 0
    c: DistanceX(g2,g1) = 0
    c: DistanceY(g1,g2) = 34
    c: DistanceY(g2,g3) = 0
    c: DistanceX(g2,g3) = 34
    c: DistanceX(g0,g3) = 0
    c: Coincident(g5,g4)
    c: DistanceX(g4) = 57
    c: DistanceY(g4) = -150
    c: Diameter(g5) = 42
    c: Diameter(g4) = 55
FEATURE [Part::Feature] Part__Feature105  label="Printed Circuit Board"
  shape: bbox 25.4 x 17.78 x 1.6 mm, 42 faces (baked)
FEATURE [Part::Feature] Part__Feature106  label="EAHC2835WD6"
  shape: bbox 3.513 x 2.813 x 0.7485 mm, 108 faces, 4 solids (baked)
FEATURE [Part::Feature] Part__Feature107  label="AS7341 v2"
  Placement = pos=(0,-0.339822,1.6) rot=(0,0,1;0rad)
  shape: bbox 2 x 3.1 x 1.1 mm, 267 faces, 26 solids (baked)
FEATURE [Part::Feature] Part__Feature108  label="CAPC-0805-T0.95-BN v1"
  Placement = pos=(-5.01759,-3.15294,1.6) rot=(0,0,1;0rad)
  shape: bbox 2.1 x 1.35 x 0.95 mm, 42 faces (baked)
FEATURE [Part::Feature] Part__Feature109  label="CAPC-0805-T0.95-BN v002"
  Placement = pos=(-5.48627,2.66154,1.6) rot=(0,0,-1;1.5708rad)
  shape: bbox 1.35 x 2.1 x 0.95 mm, 42 faces (baked)
FEATURE [Part::Feature] Part__Feature110  label="CAPC-0805-T0.95-BN v003"
  Placement = pos=(-3.43627,2.66154,1.6) rot=(0,0,-1;1.5708rad)
  shape: bbox 1.35 x 2.1 x 0.95 mm, 42 faces (baked)
FEATURE [Part::Feature] Part__Feature111  label="CAPC-0603-T0.9-BN v1"
  Placement = pos=(-1.69987,-3.28475,1.6) rot=(0,0,1;0rad)
  shape: bbox 1.7 x 0.9 x 0.9 mm, 42 faces (baked)
FEATURE [Part::Feature] Part__Feature112  label="BODY_MF06A"
  Placement = pos=(0,0,0.762) rot=(0.57735,-0.57735,-0.57735;2.0944rad)
  shape: bbox 1.601 x 2.921 x 1.016 mm, 42 faces (baked)
FEATURE [Part::Feature] Part__Feature113  label="LEAD_MF06A"
  Placement = pos=(-0.9652,-0.9525,0.1016) rot=(0.57735,-0.57735,-0.57735;2.0944rad)
  shape: bbox 0.6223 x 0.3749 x 0.8636 mm, 14 faces (baked)
FEATURE [Part::Feature] Part__Feature114  label="LEAD_MF06A001"
  Placement = pos=(-0.9652,0,0.1016) rot=(0.57735,-0.57735,-0.57735;2.0944rad)
  shape: bbox 0.6223 x 0.3749 x 0.8636 mm, 14 faces (baked)
FEATURE [Part::Feature] Part__Feature115  label="LEAD_MF06A002"
  Placement = pos=(-0.9652,0.9525,0.1016) rot=(0.57735,-0.57735,-0.57735;2.0944rad)
  shape: bbox 0.6223 x 0.3749 x 0.8636 mm, 14 faces (baked)
FEATURE [Part::Feature] Part__Feature116  label="LEAD_MF06A003"
  Placement = pos=(0.9652,-0.9525,0.1016) rot=(0.57735,0.57735,0.57735;2.0944rad)
  shape: bbox 0.6223 x 0.3749 x 0.8636 mm, 14 faces (baked)
FEATURE [Part::Feature] Part__Feature117  label="LEAD_MF06A004"
  Placement = pos=(0.9652,0,0.1016) rot=(0.57735,0.57735,0.57735;2.0944rad)
  shape: bbox 0.6223 x 0.3749 x 0.8636 mm, 14 faces (baked)
FEATURE [Part::Feature] Part__Feature118  label="LEAD_MF06A005"
  Placement = pos=(0.9652,0.9525,0.1016) rot=(0.57735,0.57735,0.57735;2.0944rad)
  shape: bbox 0.6223 x 0.3749 x 0.8636 mm, 14 faces (baked)
FEATURE [Part::Feature] Part__Feature119  label="SOT363 v2"
  Placement = pos=(4.97054,-0.645171,1.675) rot=(0,0,1;3.14159rad)
  shape: bbox 2.1 x 2 x 1.1 mm, 94 faces, 7 solids (baked)
FEATURE [Part::Feature] Part__Feature120  label="LED 0603 single color v1"
  Placement = pos=(-9.18406,3.72778,1.60762) rot=(0,0,1;1.5708rad)
  shape: bbox 1.961 x 0.7932 x 0.7145 mm, 63 faces, 5 solids (baked)
FEATURE [Part::Feature] Part__Feature121  label="RESC-0603 v1"
  Placement = pos=(4.83432,-3.67461,1.6) rot=(0,0,1;0rad)
  shape: bbox 1.7 x 0.9 x 0.55 mm, 52 faces, 3 solids (baked)
FEATURE [Part::Feature] Part__Feature122  label="RESC-0603 v002"
  Placement = pos=(-7.14949,3.61248,1.6) rot=(0,0,-1;1.5708rad)
  shape: bbox 0.9 x 1.7 x 0.55 mm, 52 faces, 3 solids (baked)
FEATURE [Part::Feature] Part__Feature123  label="YC164_RESPACK v1"
  Placement = pos=(2.99591,1.52916,1.6) rot=(0,0,1;0rad)
  shape: bbox 3.2 x 1.6 x 0.61 mm, 172 faces (baked)
FEATURE [Part::Feature] Part__Feature124  label="qwicc v2"
  Placement = pos=(-10.8364,0.0607456,1.65) rot=(0,0,-1;1.5708rad)
  shape: bbox 4.95 x 6 x 2.96 mm, 229 faces, 7 solids (baked)
FEATURE [Part::Feature] Part__Feature125  label="qwicc v003"
  Placement = pos=(10.8256,0.00556102,1.65) rot=(0,0,1;1.5708rad)
  shape: bbox 4.95 x 6 x 2.96 mm, 229 faces, 7 solids (baked)
FEATURE [App::Part] sot_23_6_v2  label="sot-23-6 v2"
  Group = -> [Part__Feature112,Part__Feature113,Part__Feature114,Part__Feature115,Part__Feature116,Part__Feature117,Part__Feature118]
  Origin = -> Origin008
  Placement = pos=(-4.47945,-0.603742,1.69152) rot=(0,0,1;0rad)
FEATURE [App::Part] Adafruit_AS7341_STEMMA_QT_v2  label="ltr390"
  Group = -> [Part__Feature105,Part__Feature106,Part__Feature107,Part__Feature108,Part__Feature109,Part__Feature110,Part__Feature111,sot_23_6_v2,Part__Feature119,Part__Feature120,Part__Feature121,Part__Feature122,Part__Feature123,Part__Feature124,Part__Feature125]
  Origin = -> Origin009
  Placement = pos=(0,-98,110) rot=(0,0,1;0rad)
FEATURE [Part::Box] Box  label="guva"
  AttacherType = Attacher::AttachEngine3D
  Height = 2
  Length = 19
  Placement = pos=(-9.5,-88,0) rot=(0,0,1;0rad)
  Width = 10
FEATURE [Part::Cylinder] Cylinder098
  Angle = 360
  AttacherType = Attacher::AttachEngine3D
  FirstAngle = 0
  Height = 10
  Placement = pos=(6.5,-83,0) rot=(0,0,1;0rad)
  Radius = 1.13
  SecondAngle = 0
FEATURE [Part::Cut] Cut018  label="guva001"
  Base = -> Box
  Placement = pos=(0,0,110) rot=(0,0,1;0rad)
  Tool = -> Cylinder098
FEATURE [Sketcher::SketchObject] Sketch004
  FullyConstrained = true
  sketch-geometry (11):
    g0: Circle CenterX=6.5 CenterY=-83 CenterZ=0 NormalX=0 NormalY=0 NormalZ=1 AngleXU=0 Radius=1.125
    g1: Circle CenterX=10.15 CenterY=-91.65 CenterZ=0 NormalX=0 NormalY=0 NormalZ=1 AngleXU=0 Radius=1.125
    g2: Circle CenterX=10.15 CenterY=-104.35 CenterZ=0 NormalX=0 NormalY=0 NormalZ=1 AngleXU=0 Radius=1.125
    g3: Circle CenterX=-10.15 CenterY=-104.35 CenterZ=0 NormalX=0 NormalY=0 NormalZ=1 AngleXU=0 Radius=1.125
    g4: Circle CenterX=-10.15 CenterY=-91.65 CenterZ=0 NormalX=0 NormalY=0 NormalZ=1 AngleXU=0 Radius=1.125
    g5: ArcOfCircle CenterX=-9.5 CenterY=-78 CenterZ=0 NormalX=0 NormalY=0 NormalZ=1 AngleXU=0 Radius=9.5 StartAngle=4.71239 EndAngle=6.28319
    g6: LineSegment StartX=-9.5 StartY=-87.5 StartZ=0 EndX=-15.15 EndY=-87.5 EndZ=0
    g7: LineSegment StartX=-15.15 StartY=-87.5 StartZ=0 EndX=-15.15 EndY=-109.35 EndZ=0
    g8: LineSegment StartX=-15.15 StartY=-109.35 StartZ=0 EndX=15.15 EndY=-109.35 EndZ=0
    g9: LineSegment StartX=15.15 StartY=-109.35 StartZ=0 EndX=15.15 EndY=-78 EndZ=0
    g10: LineSegment StartX=15.15 StartY=-78 StartZ=0 EndX=0 EndY=-78 EndZ=0
  constraints (34):
    c: DistanceX(g4,g3) = 0
    c: DistanceX(g2,g1) = 0
    c: Equal(g2,g3)
    c: Equal(g2,g4)
    c: Equal(g2,g1)
    c: Equal(g2,g0)
    c: Diameter(g2) = 2.25
    c: DistanceX(g2) = 10.15
    c: DistanceY(g2) = -104.35
    c: DistanceY(g2,g1) = 12.7
    c: DistanceY(g3,g2) = 0
    c: DistanceX(g3,g2) = 20.3
    c: DistanceY(g4,g1) = 0
    c: DistanceY(g0) = -83
    c: DistanceX(g0) = 6.5
    c: PointOnObject(g5,g-2)
    c: Coincident(g6,g5)
    c: Horizontal(g6)
    c: Coincident(g7,g6)
    c: Vertical(g7)
    c: Coincident(g8,g7)
    c: Horizontal(g8)
    c: Coincident(g9,g8)
    c: Vertical(g9)
    c: Coincident(g10,g9)
    c: Coincident(g10,g5)
    c: Horizontal(g10)
    c: DistanceY(g5) = -78
    c: DistanceY(g5,g5) = 0
    c: DistanceX(g5,g5) = 9.5
    c: DistanceX(g5,g5) = 0
    c: DistanceX(g1,g9) = 5
    c: DistanceX(g7,g3) = 5
    c: DistanceY(g7,g3) = 5
FEATURE [Part::Extrusion] Extrude002  label="as7265Holder"
  Base = -> Sketch002
  Dir = (0,0,1)
  DirMode = 2
  FaceMakerClass = Part::FaceMakerBullseye
  LengthFwd = 10
  LengthRev = 0
  Placement = pos=(0,0,100) rot=(0,0,1;0rad)
  Solid = true
  Symmetric = false
FEATURE [Part::Extrusion] Extrude003  label="cameraHolder"
  Base = -> Sketch003
  Dir = (0,0,1)
  DirMode = 2
  FaceMakerClass = Part::FaceMakerBullseye
  LengthFwd = 8.25
  LengthRev = 0
  Placement = pos=(0,0,80) rot=(0,0,1;0rad)
  Solid = true
  Symmetric = false
FEATURE [Part::Extrusion] Extrude004  label="uvHolder"
  Base = -> Sketch004
  Dir = (0,0,1)
  DirMode = 2
  FaceMakerClass = Part::FaceMakerBullseye
  LengthFwd = 10
  LengthRev = 0
  Placement = pos=(0,0,100) rot=(0,0,1;0rad)
  Solid = true
  Symmetric = false
FEATURE [Part::Feature] Part__Feature040  label="CeramicBody (1)"
  shape: bbox 1.8 x 1.23 x 1.23 mm, 10 faces (baked)
FEATURE [Part::Feature] Part__Feature104  label="ips7100"
  Placement = pos=(-24,0,222) rot=(0.999993,-0.003655,0;3.14159rad)
  shape: bbox 48.14 x 14.05 x 44.14 mm, 1935 faces (baked)
FEATURE [Part::Compound] Compound  label="ips7100s"
  Links = -> [Part__Feature104]
  Placement = pos=(24,-180,25) rot=(0,0,1;0.006109rad)
FEATURE [Part::Feature] Part__Feature126  label="scd30"
  Placement = pos=(-1e-15,-110,40) rot=(1,0,0;3.14159rad)
  shape: bbox 35.11 x 7.027 x 23.02 mm, 2292 faces, 25 solids (baked)
FEATURE [Part::Feature] Part__Feature127  label="Board"
  shape: bbox 25.4 x 25.4 x 1.57 mm, 211 faces (baked)
FEATURE [Part::Feature] Part__Feature128  label="QFN24_4MM"
  Placement = pos=(12.1412,14.4526,1.57) rot=(0,0,1;3.92699rad)
  shape: bbox 5.657 x 5.657 x 0.9 mm, 172 faces (baked)
FEATURE [Part::Feature] Part__Feature129  label="Part 5"
  shape: bbox 0.48 x 0.6603 x 0.6 mm, 14 faces (baked)
FEATURE [Part::Feature] Part__Feature130  label="Part 6"
  shape: bbox 0.48 x 0.6603 x 0.6 mm, 14 faces (baked)
FEATURE [Part::Feature] Part__Feature131  label="Part 4"
  shape: bbox 0.48 x 0.6603 x 0.6 mm, 14 faces (baked)
FEATURE [Part::Feature] Part__Feature132  label="Part 3"
  shape: bbox 0.48 x 0.6603 x 0.6 mm, 14 faces (baked)
FEATURE [Part::Feature] Part__Feature133  label="Part 010"
  shape: bbox 0.48 x 0.6603 x 0.6 mm, 14 faces (baked)
FEATURE [Part::Feature] Part__Feature134  label="Part 011"
  shape: bbox 3 x 1.4 x 1 mm, 10 faces (baked)
FEATURE [Part::Feature] Part__Feature135  label="Pin1"
  shape: bbox 0.6224 x 1.252 x 1.252 mm, 37 faces (baked)
FEATURE [Part::Feature] Part__Feature136  label="Pin2"
  shape: bbox 0.6224 x 1.252 x 1.252 mm, 37 faces (baked)
FEATURE [Part::Feature] Part__Feature137  label="CeramicBody"
  shape: bbox 1.8 x 1.23 x 1.23 mm, 10 faces (baked)
FEATURE [Part::Feature] Part__Feature138  label="0603-NO (1)"
  Placement = pos=(23.241,6.223,1.57) rot=(0,0,1;0rad)
  shape: bbox 1.7 x 0.9 x 0.55 mm, 52 faces, 3 solids (baked)
FEATURE [Part::Feature] Part__Feature139  label="0603-NO (2)"
  Placement = pos=(13.3858,8.4328,1.57) rot=(0,0,1;0rad)
  shape: bbox 1.7 x 0.9 x 0.55 mm, 52 faces, 3 solids (baked)
FEATURE [Part::Feature] Part__Feature140  label="0603-NO (3)"
  Placement = pos=(1.905,18.923,1.57) rot=(0,0,1;3.14159rad)
  shape: bbox 1.7 x 0.9 x 0.55 mm, 52 faces, 3 solids (baked)
FEATURE [Part::Feature] Part__Feature141  label="Pin1 (1)"
  shape: bbox 0.6224 x 1.252 x 1.252 mm, 37 faces (baked)
FEATURE [Part::Feature] Part__Feature142  label="Pin2 (1)"
  shape: bbox 0.6224 x 1.252 x 1.252 mm, 37 faces (baked)
FEATURE [Part::Feature] Part__Feature143  label="Pin1 (2)"
  shape: bbox 0.6224 x 1.252 x 1.252 mm, 37 faces (baked)
FEATURE [Part::Feature] Part__Feature144  label="Pin2 (2)"
  shape: bbox 0.6224 x 1.252 x 1.252 mm, 37 faces (baked)
FEATURE [Part::Feature] Part__Feature145  label="CeramicBody (2)"
  shape: bbox 1.8 x 1.23 x 1.23 mm, 10 faces (baked)
FEATURE [Part::Feature] Part__Feature146  label="CHIPLED_0603_NOOUTLINE"
  Placement = pos=(23.368,8.509,1.57) rot=(0,0,1;1.5708rad)
  shape: bbox 1.616 x 0.8 x 0.4 mm, 133 faces (baked)
FEATURE [Part::Feature] Part__Feature147  label="CHIPLED_0603_NOOUTLINE (1)"
  Placement = pos=(1.905,16.764,1.57) rot=(0,0,-1;1.5708rad)
  shape: bbox 1.616 x 0.8 x 0.4 mm, 133 faces (baked)
FEATURE [Part::Feature] Part__Feature148  label="JST_SH4"
  Placement = pos=(22.86,12.7,1.57) rot=(0,0,1;1.5708rad)
  shape: bbox 4.95 x 6 x 2.96 mm, 229 faces, 7 solids (baked)
FEATURE [Part::Feature] Part__Feature149  label="JST_SH4 (1)"
  Placement = pos=(2.54,12.7,1.57) rot=(0,0,-1;1.5708rad)
  shape: bbox 4.95 x 6 x 2.96 mm, 229 faces, 7 solids (baked)
FEATURE [Part::Feature] Part__Feature150  label="NEO3535_REVERSE"
  Placement = pos=(12.7,23.114,0) rot=(0,1,0;3.14159rad)
  shape: bbox 5.88 x 2.8 x 1.78 mm, 41 faces, 5 solids (baked)
FEATURE [Part::Feature] Part__Feature151  label="RESPACK_4X0603"
  Placement = pos=(22.86,18.415,1.57) rot=(0,0,1;3.14159rad)
  shape: bbox 3.2 x 1.6 x 0.61 mm, 172 faces (baked)
FEATURE [Part::Feature] Part__Feature152  label="SOT363"
  Placement = pos=(17.399,12.192,1.57) rot=(0,0,-1;1.5708rad)
  shape: bbox 2.208 x 2.208 x 1.121 mm, 178 faces, 4 solids (baked)
FEATURE [App::Part] _603_NO  label="0603-NO"
  Group = -> [Part__Feature135,Part__Feature136,Part__Feature137]
  Origin = -> Origin012
  Placement = pos=(16.51,8.382,1.57) rot=(0,0,1;0rad)
FEATURE [App::Part] _6700497  label="36700497"
  Group = -> [Part__Feature129,Part__Feature130,Part__Feature131,Part__Feature132,Part__Feature133,Part__Feature134]
  Origin = -> Origin010
  Placement = pos=(0,0,0) rot=(0,0,1;3.14159rad)
FEATURE [App::Part] SOT23_5  label="SOT23-5"
  Group = -> [_6700497]
  Origin = -> Origin011
  Placement = pos=(2.54,6.985,1.57) rot=(0,0,1;3.14159rad)
FEATURE [App::Part] _805_NO  label="0805-NO"
  Group = -> [Part__Feature141,Part__Feature142,Part__Feature040]
  Origin = -> Origin013
  Placement = pos=(7.874,13.589,1.57) rot=(0,0,1;1.5708rad)
FEATURE [App::Part] _805_NO__1_  label="0805-NO (1)"
  Group = -> [Part__Feature143,Part__Feature144,Part__Feature145]
  Origin = -> Origin014
  Placement = pos=(12.827,6.223,1.57) rot=(0,0,1;3.14159rad)
FEATURE [App::Part] Packages
  Group = -> [Part__Feature128,SOT23_5,_603_NO,Part__Feature138,Part__Feature139,Part__Feature140,_805_NO,_805_NO__1_,Part__Feature146,Part__Feature147,Part__Feature148,Part__Feature149,Part__Feature150,Part__Feature151,Part__Feature152]
  Origin = -> Origin015
FEATURE [App::Part] Adafruit_I2C_QT_Rotary_Encoder_v2  label="gps"
  Group = -> [Part__Feature127,Packages]
  Origin = -> Origin016
  Placement = pos=(-12.7,-163,95) rot=(0,0,1;0rad)
FEATURE [Sketcher::SketchObject] Sketch005  label="top007"
  FullyConstrained = true
  sketch-geometry (4):
    g0: Circle CenterX=0 CenterY=-150 CenterZ=0 NormalX=0 NormalY=0 NormalZ=1 AngleXU=0 Radius=85
    g1: Circle CenterX=-30 CenterY=-120 CenterZ=0 NormalX=0 NormalY=0 NormalZ=1 AngleXU=0 Radius=6.25
    g2: Circle CenterX=0 CenterY=-207 CenterZ=0 NormalX=0 NormalY=0 NormalZ=1 AngleXU=0 Radius=4.5
    g3: Circle CenterX=30 CenterY=-120 CenterZ=0 NormalX=0 NormalY=0 NormalZ=1 AngleXU=0 Radius=6.25
  constraints (12):
    c: Radius(g0) = 85
    c: DistanceY(g0) = -150
    c: DistanceY(g0,g1) = 30
    c: DistanceX(g2,g0) = 0
    c: DistanceX(g1,g0) = 30
    c: DistanceY(g2,g0) = 57
    c: Diameter(g2) = 9
    c: DistanceY(g0,g3) = 30
    c: DistanceX(g0) = 0
    c: DistanceX(g3) = 30
    c: Equal(g1,g3)
    c: Diameter(g1) = 12.5
FEATURE [Part::Extrusion] Extrude005  label="level1"
  Base = -> Sketch005
  Dir = (0,0,1)
  DirMode = 2
  FaceMakerClass = Part::FaceMakerBullseye
  LengthFwd = 5
  LengthRev = 0
  Placement = pos=(0,0,75) rot=(0,0,1;0rad)
  Solid = true
  Symmetric = false
FEATURE [Part::Box] Box007  label="Cube001"
  AttacherType = Attacher::AttachEngine3D
  Height = 20
  Length = 30
  Placement = pos=(-72,-155,80) rot=(0,0,1;0rad)
  Width = 10
FEATURE [Part::MultiFuse] Fusion049  label="as7265Holder001"
  Shapes = -> [Box007,Extrude002]
FEATURE [Sketcher::SketchObject] Sketch006
  FullyConstrained = true
  sketch-geometry (6):
    g0: Circle CenterX=0 CenterY=-150 CenterZ=0 NormalX=0 NormalY=0 NormalZ=1 AngleXU=0 Radius=17.5
    g1: Circle CenterX=-10.15 CenterY=-140.15 CenterZ=0 NormalX=0 NormalY=0 NormalZ=1 AngleXU=0 Radius=1.65
    g2: Circle CenterX=10.15 CenterY=-140.15 CenterZ=0 NormalX=0 NormalY=0 NormalZ=1 AngleXU=0 Radius=1.65
    g3: Circle CenterX=10.15 CenterY=-160.45 CenterZ=0 NormalX=0 NormalY=0 NormalZ=1 AngleXU=0 Radius=1.65
    g4: Circle CenterX=-10.15 CenterY=-160.45 CenterZ=0 NormalX=0 NormalY=0 NormalZ=1 AngleXU=0 Radius=1.65
    g5: Circle CenterX=0 CenterY=-150 CenterZ=0 NormalX=0 NormalY=0 NormalZ=1 AngleXU=0 Radius=11
  constraints (17):
    c: DistanceY(g0) = -150
    c: DistanceX(g0) = 0
    c: Radius(g0) = 17.5
    c: Equal(g4,g3)
    c: Equal(g4,g2)
    c: Equal(g4,g1)
    c: Diameter(g4) = 3.3
    c: DistanceX(g1,g4) = 0
    c: DistanceY(g2,g1) = 0
    c: DistanceY(g3,g4) = 0
    c: DistanceX(g2,g3) = 0
    c: DistanceY(g4,g0) = 10.45
    c: DistanceY(g0,g1) = 9.85
    c: DistanceX(g3) = 10.15
    c: DistanceX(g4) = -10.15
    c: Coincident(g5,g0)
    c: Diameter(g5) = 22
FEATURE [Part::Extrusion] Extrude006  label="gpsHolder"
  Base = -> Sketch006
  Dir = (0,0,1)
  DirMode = 2
  FaceMakerClass = Part::FaceMakerBullseye
  LengthFwd = 10
  LengthRev = 0
  Placement = pos=(0,0,80) rot=(0,0,1;0rad)
  Solid = true
  Symmetric = false
FEATURE [Part::Box] Box008  label="Cube"
  AttacherType = Attacher::AttachEngine3D
  Height = 25
  Length = 10
  Placement = pos=(-5,-109.35,75) rot=(0,0,1;0rad)
  Width = 20
FEATURE [Part::MultiFuse] Fusion050  label="uvHolder001"
  Shapes = -> [Box008,Extrude004]
FEATURE [Part::Cylinder] Cylinder099  label="refModuleHold001"
  Angle = 360
  AttacherType = Attacher::AttachEngine3D
  FirstAngle = 0
  Height = 32
  Placement = pos=(0,-207,80) rot=(0,0,1;0rad)
  Radius = 12
  SecondAngle = 0
FEATURE [Part::MultiFuse] Fusion051  label="refModule"
  Shapes = -> [Cylinder095,Cylinder094]
FEATURE [Part::Cylinder] Cylinder100  label="refModules001"
  Angle = 360
  AttacherType = Attacher::AttachEngine3D
  FirstAngle = 0
  Height = 75
  Placement = pos=(0,-207,37) rot=(0,0,1;0rad)
  Radius = 3.75
  SecondAngle = 0
FEATURE [Part::Cylinder] Cylinder101  label="refModulesCoverCut002"
  Angle = 360
  AttacherType = Attacher::AttachEngine3D
  FirstAngle = 0
  Height = 60
  Placement = pos=(0,-207,37) rot=(0,0,1;0rad)
  Radius = 4.5
  SecondAngle = 0
FEATURE [Part::MultiFuse] Fusion052  label="refModule001Cut"
  Shapes = -> [Cylinder101,Cylinder100]
FEATURE [Part::Cut] Cut019  label="refModuleHold002"
  Base = -> Cylinder099
  Tool = -> Fusion052
FEATURE [Sketcher::SketchObject] Sketch007
  FullyConstrained = true
  Placement = pos=(0,0,0) rot=(1,0,0;1.5708rad)
  sketch-geometry (1):
    g0: Circle CenterX=0 CenterY=102.5 CenterZ=0 NormalX=0 NormalY=0 NormalZ=1 AngleXU=0 Radius=2
  constraints (3):
    c: PointOnObject(g0,g-2)
    c: DistanceY(g0) = 102.5
    c: Diameter(g0) = 4
FEATURE [Part::Extrusion] Extrude007  label="m3HeatSetInsertCut"
  Base = -> Sketch007
  Dir = (0,-1,-3e-16)
  DirMode = 2
  FaceMakerClass = Part::FaceMakerBullseye
  LengthFwd = 50
  LengthRev = 0
  Placement = pos=(0,-183.25,0) rot=(0,0,1;0rad)
  Solid = true
  Symmetric = false
FEATURE [Part::Cut] Cut020  label="refSensorHoldLev1"
  Base = -> Cut019
  Tool = -> Extrude007
FEATURE [Part::MultiFuse] Fusion053  label="level1SensorHolds"
  Shapes = -> [Fusion050,Cut020,Extrude006,Fusion049,Extrude003]
FEATURE [Part::MultiFuse] Fusion054  label="level001x"
  Shapes = -> [Fusion053,Extrude005]
FEATURE [Part::Feature] Part__Feature153  label="Printed Circuit Board001"
  shape: bbox 25.4 x 17.78 x 1.6 mm, 42 faces (baked)
FEATURE [Part::Feature] Part__Feature154  label="EAHC2835WD007"
  shape: bbox 3.513 x 2.813 x 0.7485 mm, 108 faces, 4 solids (baked)
FEATURE [Part::Feature] Part__Feature155  label="AS7341 v003"
  Placement = pos=(0,-0.339822,1.6) rot=(0,0,1;0rad)
  shape: bbox 2 x 3.1 x 1.1 mm, 267 faces, 26 solids (baked)
FEATURE [Part::Feature] Part__Feature156  label="CAPC-0805-T0.95-BN v004"
  Placement = pos=(-5.01759,-3.15294,1.6) rot=(0,0,1;0rad)
  shape: bbox 2.1 x 1.35 x 0.95 mm, 42 faces (baked)
FEATURE [Part::Feature] Part__Feature157  label="CAPC-0805-T0.95-BN v005"
  Placement = pos=(-5.48627,2.66154,1.6) rot=(0,0,-1;1.5708rad)
  shape: bbox 1.35 x 2.1 x 0.95 mm, 42 faces (baked)
FEATURE [Part::Feature] Part__Feature158  label="CAPC-0805-T0.95-BN v006"
  Placement = pos=(-3.43627,2.66154,1.6) rot=(0,0,-1;1.5708rad)
  shape: bbox 1.35 x 2.1 x 0.95 mm, 42 faces (baked)
FEATURE [Part::Feature] Part__Feature159  label="CAPC-0603-T0.9-BN v002"
  Placement = pos=(-1.69987,-3.28475,1.6) rot=(0,0,1;0rad)
  shape: bbox 1.7 x 0.9 x 0.9 mm, 42 faces (baked)
FEATURE [Part::Feature] Part__Feature160  label="BODY_MF06A001"
  Placement = pos=(0,0,0.762) rot=(0.57735,-0.57735,-0.57735;2.0944rad)
  shape: bbox 1.601 x 2.921 x 1.016 mm, 42 faces (baked)
FEATURE [Part::Feature] Part__Feature161  label="LEAD_MF06A006"
  Placement = pos=(-0.9652,-0.9525,0.1016) rot=(0.57735,-0.57735,-0.57735;2.0944rad)
  shape: bbox 0.6223 x 0.3749 x 0.8636 mm, 14 faces (baked)
FEATURE [Part::Feature] Part__Feature162  label="LEAD_MF06A007"
  Placement = pos=(-0.9652,0,0.1016) rot=(0.57735,-0.57735,-0.57735;2.0944rad)
  shape: bbox 0.6223 x 0.3749 x 0.8636 mm, 14 faces (baked)
FEATURE [Part::Feature] Part__Feature163  label="LEAD_MF06A008"
  Placement = pos=(-0.9652,0.9525,0.1016) rot=(0.57735,-0.57735,-0.57735;2.0944rad)
  shape: bbox 0.6223 x 0.3749 x 0.8636 mm, 14 faces (baked)
FEATURE [Part::Feature] Part__Feature164  label="LEAD_MF06A009"
  Placement = pos=(0.9652,-0.9525,0.1016) rot=(0.57735,0.57735,0.57735;2.0944rad)
  shape: bbox 0.6223 x 0.3749 x 0.8636 mm, 14 faces (baked)
FEATURE [Part::Feature] Part__Feature165  label="LEAD_MF06A010"
  Placement = pos=(0.9652,0,0.1016) rot=(0.57735,0.57735,0.57735;2.0944rad)
  shape: bbox 0.6223 x 0.3749 x 0.8636 mm, 14 faces (baked)
FEATURE [Part::Feature] Part__Feature166  label="LEAD_MF06A011"
  Placement = pos=(0.9652,0.9525,0.1016) rot=(0.57735,0.57735,0.57735;2.0944rad)
  shape: bbox 0.6223 x 0.3749 x 0.8636 mm, 14 faces (baked)
FEATURE [Part::Feature] Part__Feature167  label="SOT363 v003"
  Placement = pos=(4.97054,-0.645171,1.675) rot=(0,0,1;3.14159rad)
  shape: bbox 2.1 x 2 x 1.1 mm, 94 faces, 7 solids (baked)
FEATURE [Part::Feature] Part__Feature168  label="LED 0603 single color v002"
  Placement = pos=(-9.18406,3.72778,1.60762) rot=(0,0,1;1.5708rad)
  shape: bbox 1.961 x 0.7932 x 0.7145 mm, 63 faces, 5 solids (baked)
FEATURE [Part::Feature] Part__Feature169  label="RESC-0603 v003"
  Placement = pos=(4.83432,-3.67461,1.6) rot=(0,0,1;0rad)
  shape: bbox 1.7 x 0.9 x 0.55 mm, 52 faces, 3 solids (baked)
FEATURE [Part::Feature] Part__Feature170  label="RESC-0603 v004"
  Placement = pos=(-7.14949,3.61248,1.6) rot=(0,0,-1;1.5708rad)
  shape: bbox 0.9 x 1.7 x 0.55 mm, 52 faces, 3 solids (baked)
FEATURE [Part::Feature] Part__Feature171  label="YC164_RESPACK v002"
  Placement = pos=(2.99591,1.52916,1.6) rot=(0,0,1;0rad)
  shape: bbox 3.2 x 1.6 x 0.61 mm, 172 faces (baked)
FEATURE [Part::Feature] Part__Feature172  label="qwicc v004"
  Placement = pos=(-10.8364,0.0607456,1.65) rot=(0,0,-1;1.5708rad)
  shape: bbox 4.95 x 6 x 2.96 mm, 229 faces, 7 solids (baked)
FEATURE [Part::Feature] Part__Feature173  label="qwicc v005"
  Placement = pos=(10.8256,0.00556102,1.65) rot=(0,0,1;1.5708rad)
  shape: bbox 4.95 x 6 x 2.96 mm, 229 faces, 7 solids (baked)
FEATURE [App::Part] sot_23_6_v003  label="sot-23-6 v003"
  Group = -> [Part__Feature160,Part__Feature161,Part__Feature162,Part__Feature163,Part__Feature164,Part__Feature165,Part__Feature166]
  Origin = -> Origin017
  Placement = pos=(-4.47945,-0.603742,1.69152) rot=(0,0,1;0rad)
FEATURE [App::Part] Adafruit_AS7341_STEMMA_QT_v003  label="bme280"
  Group = -> [Part__Feature153,Part__Feature154,Part__Feature155,Part__Feature156,Part__Feature157,Part__Feature158,Part__Feature159,sot_23_6_v003,Part__Feature167,Part__Feature168,Part__Feature169,Part__Feature170,Part__Feature171,Part__Feature172,Part__Feature173]
  Origin = -> Origin018
  Placement = pos=(30,-149.75,45) rot=(0.57735,-0.57735,0.57735;4.18879rad)
FEATURE [Part::Cone] Cone
  Angle = 360
  AttacherType = Attacher::AttachEngine3D
  Height = 1.5
  Placement = pos=(0,0,25.5) rot=(0,0,1;0rad)
  Radius1 = 4
  Radius2 = 3.5
FEATURE [Part::Cylinder] Cylinder020
  Angle = 360
  AttacherType = Attacher::AttachEngine3D
  FirstAngle = 0
  Height = 22
  Placement = pos=(0,0,5) rot=(0,0,1;0rad)
  Radius = 3.2
  SecondAngle = 0
FEATURE [Part::Cylinder] Cylinder021
  Angle = 360
  AttacherType = Attacher::AttachEngine3D
  FirstAngle = 0
  Height = 2
  Placement = pos=(0,0,5) rot=(0,0,1;0rad)
  Radius = 3.55
  SecondAngle = 0
FEATURE [Part::Cylinder] Cylinder022
  Angle = 360
  AttacherType = Attacher::AttachEngine3D
  FirstAngle = 0
  Height = 1
  Placement = pos=(0,0,11) rot=(0,0,1;0rad)
  Radius = 3.55
  SecondAngle = 0
FEATURE [Part::Cylinder] Cylinder023
  Angle = 360
  AttacherType = Attacher::AttachEngine3D
  FirstAngle = 0
  Height = 8
  Placement = pos=(0,0,12) rot=(0,0,1;0rad)
  Radius = 3.25
  SecondAngle = 0
FEATURE [Part::Cylinder] Cylinder024
  Angle = 360
  AttacherType = Attacher::AttachEngine3D
  FirstAngle = 0
  Height = 5.5
  Placement = pos=(0,0,20) rot=(0,0,1;0rad)
  Radius = 4
  SecondAngle = 0
FEATURE [Part::Cylinder] Cylinder025
  Angle = 360
  AttacherType = Attacher::AttachEngine3D
  FirstAngle = 0
  Height = 2
  Placement = pos=(0,0,3) rot=(0,0,1;0rad)
  Radius = 1
  SecondAngle = 0
FEATURE [Part::MultiFuse] Fusion002
  Shapes = -> [Cone,Cylinder020,Cylinder021,Cylinder022,Cylinder023,Cylinder024]
FEATURE [Part::MultiFuse] Fusion055  label="mic"
  Placement = pos=(0,-212,-239.2) rot=(0,1,0;3.14159rad)
  Shapes = -> [Cylinder025,Fusion002]
FEATURE [Part::Feature] Part__Feature174  label="Printed Circuit Board002"
  shape: bbox 25.4 x 17.78 x 1.6 mm, 42 faces (baked)
FEATURE [Part::Feature] Part__Feature175  label="EAHC2835WD008"
  shape: bbox 3.513 x 2.813 x 0.7485 mm, 108 faces, 4 solids (baked)
FEATURE [Part::Feature] Part__Feature176  label="AS7341 v004"
  Placement = pos=(0,-0.339822,1.6) rot=(0,0,1;0rad)
  shape: bbox 2 x 3.1 x 1.1 mm, 267 faces, 26 solids (baked)
FEATURE [Part::Feature] Part__Feature177  label="CAPC-0805-T0.95-BN v007"
  Placement = pos=(-5.01759,-3.15294,1.6) rot=(0,0,1;0rad)
  shape: bbox 2.1 x 1.35 x 0.95 mm, 42 faces (baked)
FEATURE [Part::Feature] Part__Feature178  label="CAPC-0805-T0.95-BN v008"
  Placement = pos=(-5.48627,2.66154,1.6) rot=(0,0,-1;1.5708rad)
  shape: bbox 1.35 x 2.1 x 0.95 mm, 42 faces (baked)
FEATURE [Part::Feature] Part__Feature179  label="CAPC-0805-T0.95-BN v009"
  Placement = pos=(-3.43627,2.66154,1.6) rot=(0,0,-1;1.5708rad)
  shape: bbox 1.35 x 2.1 x 0.95 mm, 42 faces (baked)
FEATURE [Part::Feature] Part__Feature180  label="CAPC-0603-T0.9-BN v003"
  Placement = pos=(-1.69987,-3.28475,1.6) rot=(0,0,1;0rad)
  shape: bbox 1.7 x 0.9 x 0.9 mm, 42 faces (baked)
FEATURE [Part::Feature] Part__Feature181  label="BODY_MF06A002"
  Placement = pos=(0,0,0.762) rot=(0.57735,-0.57735,-0.57735;2.0944rad)
  shape: bbox 1.601 x 2.921 x 1.016 mm, 42 faces (baked)
FEATURE [Part::Feature] Part__Feature182  label="LEAD_MF06A012"
  Placement = pos=(-0.9652,-0.9525,0.1016) rot=(0.57735,-0.57735,-0.57735;2.0944rad)
  shape: bbox 0.6223 x 0.3749 x 0.8636 mm, 14 faces (baked)
FEATURE [Part::Feature] Part__Feature183  label="LEAD_MF06A013"
  Placement = pos=(-0.9652,0,0.1016) rot=(0.57735,-0.57735,-0.57735;2.0944rad)
  shape: bbox 0.6223 x 0.3749 x 0.8636 mm, 14 faces (baked)
FEATURE [Part::Feature] Part__Feature184  label="LEAD_MF06A014"
  Placement = pos=(-0.9652,0.9525,0.1016) rot=(0.57735,-0.57735,-0.57735;2.0944rad)
  shape: bbox 0.6223 x 0.3749 x 0.8636 mm, 14 faces (baked)
FEATURE [Part::Feature] Part__Feature185  label="LEAD_MF06A015"
  Placement = pos=(0.9652,-0.9525,0.1016) rot=(0.57735,0.57735,0.57735;2.0944rad)
  shape: bbox 0.6223 x 0.3749 x 0.8636 mm, 14 faces (baked)
FEATURE [Part::Feature] Part__Feature186  label="LEAD_MF06A016"
  Placement = pos=(0.9652,0,0.1016) rot=(0.57735,0.57735,0.57735;2.0944rad)
  shape: bbox 0.6223 x 0.3749 x 0.8636 mm, 14 faces (baked)
FEATURE [Part::Feature] Part__Feature187  label="LEAD_MF06A017"
  Placement = pos=(0.9652,0.9525,0.1016) rot=(0.57735,0.57735,0.57735;2.0944rad)
  shape: bbox 0.6223 x 0.3749 x 0.8636 mm, 14 faces (baked)
FEATURE [Part::Feature] Part__Feature188  label="SOT363 v004"
  Placement = pos=(4.97054,-0.645171,1.675) rot=(0,0,1;3.14159rad)
  shape: bbox 2.1 x 2 x 1.1 mm, 94 faces, 7 solids (baked)
FEATURE [Part::Feature] Part__Feature189  label="LED 0603 single color v003"
  Placement = pos=(-9.18406,3.72778,1.60762) rot=(0,0,1;1.5708rad)
  shape: bbox 1.961 x 0.7932 x 0.7145 mm, 63 faces, 5 solids (baked)
FEATURE [Part::Feature] Part__Feature190  label="RESC-0603 v005"
  Placement = pos=(4.83432,-3.67461,1.6) rot=(0,0,1;0rad)
  shape: bbox 1.7 x 0.9 x 0.55 mm, 52 faces, 3 solids (baked)
FEATURE [Part::Feature] Part__Feature191  label="RESC-0603 v006"
  Placement = pos=(-7.14949,3.61248,1.6) rot=(0,0,-1;1.5708rad)
  shape: bbox 0.9 x 1.7 x 0.55 mm, 52 faces, 3 solids (baked)
FEATURE [Part::Feature] Part__Feature192  label="YC164_RESPACK v003"
  Placement = pos=(2.99591,1.52916,1.6) rot=(0,0,1;0rad)
  shape: bbox 3.2 x 1.6 x 0.61 mm, 172 faces (baked)
FEATURE [Part::Feature] Part__Feature193  label="qwicc v006"
  Placement = pos=(-10.8364,0.0607456,1.65) rot=(0,0,-1;1.5708rad)
  shape: bbox 4.95 x 6 x 2.96 mm, 229 faces, 7 solids (baked)
FEATURE [Part::Feature] Part__Feature194  label="qwicc v007"
  Placement = pos=(10.8256,0.00556102,1.65) rot=(0,0,1;1.5708rad)
  shape: bbox 4.95 x 6 x 2.96 mm, 229 faces, 7 solids (baked)
FEATURE [App::Part] sot_23_6_v004  label="sot-23-6 v004"
  Group = -> [Part__Feature181,Part__Feature182,Part__Feature183,Part__Feature184,Part__Feature185,Part__Feature186,Part__Feature187]
  Origin = -> Origin019
  Placement = pos=(-4.47945,-0.603742,1.69152) rot=(0,0,1;0rad)
FEATURE [App::Part] Adafruit_AS7341_STEMMA_QT_v004  label="bme281"
  Group = -> [Part__Feature174,Part__Feature175,Part__Feature176,Part__Feature177,Part__Feature178,Part__Feature179,Part__Feature180,sot_23_6_v004,Part__Feature188,Part__Feature189,Part__Feature190,Part__Feature191,Part__Feature192,Part__Feature193,Part__Feature194]
  Origin = -> Origin020
  Placement = pos=(-30,-149.75,45) rot=(-0.57735,-0.57735,0.57735;2.0944rad)
FEATURE [Sketcher::SketchObject] Sketch008  label="top008"
  FullyConstrained = true
  sketch-geometry (15):
    g0: Circle CenterX=0 CenterY=-150 CenterZ=0 NormalX=0 NormalY=0 NormalZ=1 AngleXU=0 Radius=85
    g1: Circle CenterX=-57 CenterY=-115 CenterZ=0 NormalX=0 NormalY=0 NormalZ=1 AngleXU=0 Radius=2.125
    g2: Circle CenterX=-22 CenterY=-150 CenterZ=0 NormalX=0 NormalY=0 NormalZ=1 AngleXU=0 Radius=4
    g3: Circle CenterX=-57 CenterY=-185 CenterZ=0 NormalX=0 NormalY=0 NormalZ=1 AngleXU=0 Radius=2.125
    g4: Circle CenterX=0 CenterY=-172 CenterZ=0 NormalX=0 NormalY=0 NormalZ=1 AngleXU=0 Radius=4
    g5: Circle CenterX=-35 CenterY=-207 CenterZ=0 NormalX=0 NormalY=0 NormalZ=1 AngleXU=0 Radius=2.125
    g6: Circle CenterX=35 CenterY=-207 CenterZ=0 NormalX=0 NormalY=0 NormalZ=1 AngleXU=0 Radius=2.125
    g7: Circle CenterX=57 CenterY=-185 CenterZ=0 NormalX=0 NormalY=0 NormalZ=1 AngleXU=0 Radius=2.125
    g8: Circle CenterX=22 CenterY=-150 CenterZ=0 NormalX=0 NormalY=0 NormalZ=1 AngleXU=0 Radius=4
    g9: Circle CenterX=57 CenterY=-115 CenterZ=0 NormalX=0 NormalY=0 NormalZ=1 AngleXU=0 Radius=2.125
    g10: Circle CenterX=0 CenterY=-207 CenterZ=0 NormalX=0 NormalY=0 NormalZ=1 AngleXU=0 Radius=4.5
    g11: Circle CenterX=57 CenterY=-150 CenterZ=0 NormalX=0 NormalY=0 NormalZ=1 AngleXU=0 Radius=21
    g12: Circle CenterX=-35 CenterY=-93 CenterZ=0 NormalX=0 NormalY=0 NormalZ=1 AngleXU=0 Radius=2.125
    g13: Circle CenterX=35 CenterY=-93 CenterZ=0 NormalX=0 NormalY=0 NormalZ=1 AngleXU=0 Radius=2.125
    g14: Circle CenterX=0 CenterY=-128 CenterZ=0 NormalX=0 NormalY=0 NormalZ=1 AngleXU=0 Radius=4
  constraints (45):
    c: PointOnObject(g0,g-2)
    c: Radius(g0) = 85
    c: DistanceY(g0) = -150
    c: PointOnObject(g4,g-2)
    c: PointOnObject(g14,g-2)
    c: DistanceY(g8,g0) = 0
    c: DistanceY(g0,g2) = 0
    c: Radius(g11) = 21
    c: DistanceX(g10,g0) = 0
    c: DistanceX(g0,g11) = 57
    c: DistanceY(g11,g0) = 0
    c: DistanceX(g0,g8) = 22
    c: DistanceX(g2,g0) = 22
    c: DistanceX(g5,g10) = 35
    c: DistanceX(g10,g6) = 35
    c: DistanceX(g7,g11) = 0
    c: DistanceX(g11,g9) = 0
    c: DistanceX(g1,g0) = 57
    c: DistanceY(g3,g0) = 35
    c: DistanceY(g0,g1) = 35
    c: DistanceY(g10,g4) = 35
    c: DistanceY(g6,g10) = 0
    c: DistanceY(g10,g5) = 0
    c: DistanceY(g7,g11) = 35
    c: DistanceY(g11,g9) = 35
    c: DistanceX(g3,g1) = 0
    c: DistanceY(g10,g0) = 57
    c: Diameter(g10) = 9
    c: DistanceX(g12,g0) = 35
    c: DistanceY(g0,g13) = 57
    c: DistanceX(g0,g13) = 35
    c: Equal(g1,g12)
    c: Equal(g1,g13)
    c: Equal(g1,g9)
    c: Equal(g1,g7)
    c: Equal(g1,g6)
    c: Equal(g1,g5)
    c: Equal(g1,g3)
    c: Diameter(g1) = 4.25
    c: Equal(g4,g8)
    c: Equal(g4,g14)
    c: Equal(g4,g2)
    c: Diameter(g4) = 8
    c: DistanceY(g0,g14) = 22
    c: DistanceY(g0,g12) = 57
FEATURE [Part::Extrusion] Extrude008  label="level002"
  Base = -> Sketch008
  Dir = (0,0,1)
  DirMode = 2
  FaceMakerClass = Part::FaceMakerBullseye
  LengthFwd = 5
  LengthRev = 0
  Placement = pos=(0,0,15) rot=(0,0,1;0rad)
  Solid = true
  Symmetric = false
FEATURE [Part::Box] Box009  label="Cube002"
  AttacherType = Attacher::AttachEngine3D
  Height = 15
  Length = 10
  Placement = pos=(-25,-180,20) rot=(0,0,1;0rad)
  Width = 10
FEATURE [Part::Box] Box010  label="Cube003"
  AttacherType = Attacher::AttachEngine3D
  Height = 50
  Length = 10
  Placement = pos=(15,-180,20) rot=(0,0,1;0rad)
  Width = 10
FEATURE [Part::Box] Box011  label="Cube004"
  AttacherType = Attacher::AttachEngine3D
  Height = 35
  Length = 10
  Placement = pos=(20,-165,20) rot=(0,0,1;0rad)
  Width = 10
FEATURE [Part::Box] Box012  label="Cube005"
  AttacherType = Attacher::AttachEngine3D
  Height = 35
  Length = 10
  Placement = pos=(-30,-165,20) rot=(0,0,1;0rad)
  Width = 10
FEATURE [Part::Box] Box013  label="Cube006"
  AttacherType = Attacher::AttachEngine3D
  Height = 35
  Length = 10
  Placement = pos=(-30,-145,20) rot=(0,0,1;0rad)
  Width = 10
FEATURE [Part::Box] Box014  label="Cube007"
  AttacherType = Attacher::AttachEngine3D
  Height = 35
  Length = 10
  Placement = pos=(20,-145,20) rot=(0,0,1;0rad)
  Width = 10
FEATURE [Part::Box] Box015  label="Cube008"
  AttacherType = Attacher::AttachEngine3D
  Height = 35
  Length = 10
  Placement = pos=(-20,-130,20) rot=(0,0,1;0rad)
  Width = 10
FEATURE [Part::Box] Box016  label="Cube009"
  AttacherType = Attacher::AttachEngine3D
  Height = 17.5
  Length = 10
  Placement = pos=(12.5,-130,20) rot=(0,0,1;0rad)
  Width = 10
FEATURE [Part::MultiFuse] Fusion056  label="airSensorHolds"
  Shapes = -> [Box016,Box009,Box010,Box011,Box012,Box013,Box014,Box015]
FEATURE [Part::Cylinder] Cylinder102  label="m2Cuts"
  Angle = 360
  AttacherType = Attacher::AttachEngine3D
  FirstAngle = 0
  Height = 10
  Placement = pos=(-20.4,-170,28.6) rot=(1,0,0;1.5708rad)
  Radius = 1.13
  SecondAngle = 0
FEATURE [Part::Cylinder] Cylinder103  label="m2Cuts001"
  Angle = 360
  AttacherType = Attacher::AttachEngine3D
  FirstAngle = 0
  Height = 10
  Placement = pos=(20.4,-170,65.4) rot=(1,0,0;1.5708rad)
  Radius = 1.13
  SecondAngle = 0
FEATURE [Part::Cylinder] Cylinder104  label="m2Cuts002"
  Angle = 360
  AttacherType = Attacher::AttachEngine3D
  FirstAngle = 0
  Height = 10
  Placement = pos=(17.45,-120,33.2) rot=(1,0,0;1.5708rad)
  Radius = 1.13
  SecondAngle = 0
FEATURE [Part::Cylinder] Cylinder105  label="m2Cuts003"
  Angle = 360
  AttacherType = Attacher::AttachEngine3D
  FirstAngle = 0
  Height = 10
  Placement = pos=(-14.55,-120,49.4) rot=(1,0,0;1.5708rad)
  Radius = 1.1
  SecondAngle = 0
FEATURE [Part::Cylinder] Cylinder106  label="m2Cuts004"
  Angle = 360
  AttacherType = Attacher::AttachEngine3D
  FirstAngle = 0
  Height = 60
  Placement = pos=(-30,-159.9,38.65) rot=(0.57735,0.57735,0.57735;2.0944rad)
  Radius = 1.13
  SecondAngle = 0
FEATURE [Part::Cylinder] Cylinder107  label="m2Cuts005"
  Angle = 360
  AttacherType = Attacher::AttachEngine3D
  FirstAngle = 0
  Height = 60
  Placement = pos=(-30,-139.6,38.65) rot=(0.57735,0.57735,0.57735;2.0944rad)
  Radius = 1.13
  SecondAngle = 0
FEATURE [Part::Cylinder] Cylinder108  label="m2Cuts006"
  Angle = 360
  AttacherType = Attacher::AttachEngine3D
  FirstAngle = 0
  Height = 60
  Placement = pos=(-30,-159.9,51.35) rot=(0.57735,0.57735,0.57735;2.0944rad)
  Radius = 1.13
  SecondAngle = 0
FEATURE [Part::Cylinder] Cylinder109  label="m2Cuts007"
  Angle = 360
  AttacherType = Attacher::AttachEngine3D
  FirstAngle = 0
  Height = 60
  Placement = pos=(-30,-139.6,51.35) rot=(0.57735,0.57735,0.57735;2.0944rad)
  Radius = 1.13
  SecondAngle = 0
FEATURE [Part::MultiFuse] Fusion057  label="m2Cuts008"
  Shapes = -> [Cylinder109,Cylinder102,Cylinder103,Cylinder104,Cylinder105,Cylinder106,Cylinder107,Cylinder108]
FEATURE [Part::Cut] Cut021  label="airSesnorHolds"
  Base = -> Fusion056
  Tool = -> Fusion057
FEATURE [Sketcher::SketchObject] Sketch028
  FullyConstrained = true
  sketch-geometry (2):
    g0: Circle CenterX=0 CenterY=-150 CenterZ=0 NormalX=0 NormalY=0 NormalZ=1 AngleXU=0 Radius=79
    g1: Circle CenterX=0 CenterY=-150 CenterZ=0 NormalX=0 NormalY=0 NormalZ=1 AngleXU=0 Radius=85
  constraints (5):
    c: Diameter(g0) = 158
    c: Diameter(g1) = 170
    c: DistanceX(g0) = 0
    c: DistanceY(g1) = -150
    c: Coincident(g0,g1)
FEATURE [Part::Extrusion] Extrude010  label="srsHolds"
  Base = -> Sketch028
  Dir = (0,0,1)
  DirMode = 2
  FaceMakerClass = Part::FaceMakerBullseye
  LengthFwd = 24
  LengthRev = 0
  Placement = pos=(0,0,75) rot=(0,0,1;0rad)
  Solid = true
  Symmetric = false
FEATURE [Part::MultiFuse] Fusion063  label="level2"
  Shapes = -> [Cut021,Extrude008]
FEATURE [Sketcher::SketchObject] Sketch030  label="top011"
  FullyConstrained = true
  sketch-geometry (10):
    g0: Circle CenterX=-57 CenterY=-115 CenterZ=0 NormalX=0 NormalY=0 NormalZ=1 AngleXU=0 Radius=2.125
    g1: Circle CenterX=-57 CenterY=-185 CenterZ=0 NormalX=0 NormalY=0 NormalZ=1 AngleXU=0 Radius=2.125
    g2: Circle CenterX=-35 CenterY=-207 CenterZ=0 NormalX=0 NormalY=0 NormalZ=1 AngleXU=0 Radius=2.125
    g3: Circle CenterX=-35 CenterY=-93 CenterZ=0 NormalX=0 NormalY=0 NormalZ=1 AngleXU=0 Radius=2.125
    g4: Circle CenterX=-4.2 CenterY=-109.55 CenterZ=0 NormalX=0 NormalY=0 NormalZ=1 AngleXU=0 Radius=1.5
    g5: Circle CenterX=-58.33 CenterY=-148.9 CenterZ=0 NormalX=0 NormalY=0 NormalZ=1 AngleXU=0 Radius=1.5
    g6: Circle CenterX=-4.2 CenterY=-180.9 CenterZ=0 NormalX=0 NormalY=0 NormalZ=1 AngleXU=0 Radius=1.5
    g7: Circle CenterX=0 CenterY=-150 CenterZ=0 NormalX=0 NormalY=0 NormalZ=1 AngleXU=0 Radius=92.5
    g8: ArcOfCircle CenterX=0 CenterY=-150 CenterZ=0 NormalX=0 NormalY=0 NormalZ=1 AngleXU=0 Radius=78 StartAngle=4.71239 EndAngle=7.85398
    g9: LineSegment StartX=2.39e-14 StartY=-72 StartZ=0 EndX=-1.43e-14 EndY=-228 EndZ=0
  constraints (30):
    c: DistanceX(g1,g0) = 0
    c: Equal(g0,g3)
    c: Equal(g0,g2)
    c: Equal(g0,g1)
    c: Diameter(g0) = 4.25
    c: DistanceY(g6) = -180.9
    c: DistanceX(g4,g6) = 0
    c: DistanceY(g6,g4) = 71.35
    c: DistanceX(g5,g6) = 54.13
    c: DistanceY(g6,g5) = 32
    c: Equal(g5,g6)
    c: Equal(g5,g4)
    c: Diameter(g5) = 3
    c: PointOnObject(g7,g-2)
    c: Diameter(g7) = 185
    c: DistanceY(g7) = -150
    c: DistanceX(g1,g7) = 57
    c: DistanceY(g1,g7) = 35
    c: DistanceY(g7,g0) = 35
    c: DistanceX(g3,g7) = 35
    c: DistanceY(g7,g3) = 57
    c: DistanceX(g4) = -4.2
    c: Coincident(g8,g7)
    c: PointOnObject(g8,g-2)
    c: DistanceX(g7,g8) = 0
    c: Coincident(g9,g8)
    c: Coincident(g9,g8)
    c: Diameter(g8) = 156
    c: DistanceX(g2) = -35
    c: DistanceY(g2,g7) = 57
FEATURE [Part::Extrusion] Extrude012  label="level003"
  Base = -> Sketch030
  Dir = (0,0,1)
  DirMode = 2
  FaceMakerClass = Part::FaceMakerBullseye
  LengthFwd = 5
  LengthRev = 0
  Placement = pos=(0,0,-60) rot=(0,0,1;0rad)
  Solid = true
  Symmetric = false
FEATURE [Part::Feature] Part__Feature195  label="srsRefLightModuke"
  Placement = pos=(-15,-170,-30) rot=(0.57735,-0.57735,0.57735;4.18879rad)
  shape: bbox 63.5 x 88.9 x 31.45 mm, 876 faces (baked)
FEATURE [Part::Cylinder] Cylinder114
  Angle = 270
  AttacherType = Attacher::AttachEngine3D
  FirstAngle = 0
  Height = 30
  Placement = pos=(0,-150,0) rot=(0,0,1;1.5708rad)
  Radius = 82
  SecondAngle = 0
FEATURE [Part::Cylinder] Cylinder115
  Angle = 270
  AttacherType = Attacher::AttachEngine3D
  FirstAngle = 0
  Height = 30
  Placement = pos=(0,-150,0) rot=(0,0,1;1.5708rad)
  Radius = 78
  SecondAngle = 0
FEATURE [Part::Cut] Cut028
  Base = -> Cylinder114
  Placement = pos=(0,0,-55) rot=(0,0,1;0rad)
  Tool = -> Cylinder115
FEATURE [Part::FeaturePython] Tube002  label="tube3to2"  # WARN: FeaturePython — macro-defined, semantics opaque (R4)
  AttacherType = Attacher::AttachEngine3D
  Height = 80
  InnerRadius = 94
  OuterRadius = 98
  Placement = pos=(0,-150,-60) rot=(0,0,1;0rad)
FEATURE [Part::MultiFuse] Fusion067  label="level3"
  Shapes = -> [Extrude012,Cut028]
FEATURE [Part::Cylinder] Cylinder121
  Angle = 360
  AttacherType = Attacher::AttachEngine3D
  FirstAngle = 0
  Height = 300
  Placement = pos=(0,0,90) rot=(1,0,0;1.5708rad)
  Radius = 2.8
  SecondAngle = 0
FEATURE [Part::Cylinder] Cylinder122
  Angle = 360
  AttacherType = Attacher::AttachEngine3D
  FirstAngle = 0
  Height = 300
  Placement = pos=(-150,-150,90) rot=(0.57735,0.57735,0.57735;2.0944rad)
  Radius = 2.8
  SecondAngle = 0
FEATURE [Part::MultiFuse] Fusion068  label="m4Cuts002"
  Shapes = -> [Cylinder122,Cylinder121]
FEATURE [Part::Cut] Cut032  label="srsHold"
  Base = -> Extrude010
  Tool = -> Fusion068
FEATURE [Part::MultiFuse] Fusion069  label="level001"
  Shapes = -> [Cut032,Fusion054]
FEATURE [Sketcher::SketchObject] Sketch032
  FullyConstrained = true
  sketch-geometry (16):
    g0: ArcOfCircle CenterX=0 CenterY=-150 CenterZ=0 NormalX=0 NormalY=0 NormalZ=1 AngleXU=0 Radius=92.5 StartAngle=3.68087 EndAngle=4.17311
    g1: ArcOfCircle CenterX=0 CenterY=-150 CenterZ=0 NormalX=0 NormalY=0 NormalZ=1 AngleXU=0 Radius=92.5 StartAngle=2.11007 EndAngle=2.60232
    g2: ArcOfCircle CenterX=0 CenterY=-150 CenterZ=0 NormalX=0 NormalY=0 NormalZ=1 AngleXU=0 Radius=92.5 StartAngle=0.539274 EndAngle=1.03152
    g3: ArcOfCircle CenterX=0 CenterY=-150 CenterZ=0 NormalX=0 NormalY=0 NormalZ=1 AngleXU=0 Radius=92.5 StartAngle=5.25166 EndAngle=5.74391
    g4: ArcOfCircle CenterX=0 CenterY=-150 CenterZ=0 NormalX=0 NormalY=0 NormalZ=1 AngleXU=0 Radius=85 StartAngle=2.1287 EndAngle=2.58369
    g5: ArcOfCircle CenterX=0 CenterY=-150 CenterZ=0 NormalX=0 NormalY=0 NormalZ=1 AngleXU=0 Radius=85 StartAngle=0.557907 EndAngle=1.01289
    g6: ArcOfCircle CenterX=0 CenterY=-150 CenterZ=0 NormalX=0 NormalY=0 NormalZ=1 AngleXU=0 Radius=85 StartAngle=3.6995 EndAngle=4.15448
    g7: ArcOfCircle CenterX=0 CenterY=-150 CenterZ=0 NormalX=0 NormalY=0 NormalZ=1 AngleXU=0 Radius=85 StartAngle=5.2703 EndAngle=5.72528
    g8: LineSegment StartX=-47.5 StartY=-70.6275 StartZ=0 EndX=-45 EndY=-77.889 EndZ=0
    g9: LineSegment StartX=-79.3725 StartY=-102.5 StartZ=0 EndX=-72.111 EndY=-105 EndZ=0
    g10: LineSegment StartX=-79.3725 StartY=-197.5 StartZ=0 EndX=-72.111 EndY=-195 EndZ=0
    g11: LineSegment StartX=-47.5 StartY=-229.373 StartZ=0 EndX=-45 EndY=-222.111 EndZ=0
    g12: LineSegment StartX=47.5 StartY=-229.373 StartZ=0 EndX=45 EndY=-222.111 EndZ=0
    g13: LineSegment StartX=79.3725 StartY=-102.5 StartZ=0 EndX=72.111 EndY=-105 EndZ=0
    g14: LineSegment StartX=47.5 StartY=-70.6275 StartZ=0 EndX=45 EndY=-77.889 EndZ=0
    g15: LineSegment StartX=72.111 StartY=-195 StartZ=0 EndX=79.3725 EndY=-197.5 EndZ=0
  constraints (49):
    c: Coincident(g1,g0)
    c: Coincident(g2,g0)
    c: DistanceY(g0) = -150
    c: Coincident(g4,g0)
    c: Coincident(g5,g0)
    c: Coincident(g6,g0)
    c: Coincident(g8,g1)
    c: Coincident(g8,g4)
    c: Coincident(g9,g1)
    c: Coincident(g10,g0)
    c: Coincident(g10,g6)
    c: Coincident(g11,g0)
    c: Coincident(g11,g6)
    c: Coincident(g12,g7)
    c: Coincident(g13,g2)
    c: Coincident(g13,g5)
    c: Coincident(g14,g2)
    c: Coincident(g14,g5)
    c: Coincident(g3,g12)
    c: Coincident(g9,g4)
    c: Coincident(g3,g15)
    c: Coincident(g15,g7)
    c: Coincident(g3,g0)
    c: Coincident(g7,g0)
    c: Equal(g7,g6)
    c: Equal(g7,g4)
    c: Equal(g7,g5)
    c: Diameter(g7) = 170
    c: DistanceX(g0) = 0
    c: Equal(g3,g0)
    c: Equal(g3,g2)
    c: Equal(g3,g1)
    c: Diameter(g3) = 185
    c: DistanceY(g0,g4) = 45
    c: DistanceX(g4,g0) = 45
    c: DistanceX(g4,g6) = 0
    c: DistanceX(g6,g4) = 0
    c: DistanceY(g5,g4) = 0
    c: DistanceY(g5,g4) = 0
    c: DistanceX(g7,g5) = 0
    c: DistanceY(g6,g7) = 0
    c: DistanceY(g5,g2) = 2.5
    c: DistanceX(g5,g2) = 2.5
    c: DistanceY(g1,g2) = 0
    c: DistanceY(g2,g1) = 0
    c: DistanceX(g1,g0) = 0
    c: DistanceX(g0,g1) = 0
    c: DistanceX(g2,g3) = 0
    c: DistanceY(g3,g0) = 0
FEATURE [Part::Extrusion] Extrude014
  Base = -> Sketch032
  Dir = (0,0,1)
  DirMode = 2
  FaceMakerClass = Part::FaceMakerBullseye
  LengthFwd = 20
  LengthRev = 0
  Solid = true
  Symmetric = false
FEATURE [Part::MultiFuse] Fusion070  label="level02"
  Shapes = -> [Fusion063,Extrude014]
FEATURE [Part::Cylinder] Cylinder127
  Angle = 360
  AttacherType = Attacher::AttachEngine3D
  FirstAngle = 0
  Height = 300
  Placement = pos=(0,0,90) rot=(1,0,0;1.5708rad)
  Radius = 2.8
  SecondAngle = 0
FEATURE [Part::Cylinder] Cylinder128
  Angle = 360
  AttacherType = Attacher::AttachEngine3D
  FirstAngle = 0
  Height = 300
  Placement = pos=(-150,-150,90) rot=(0.57735,0.57735,0.57735;2.0944rad)
  Radius = 2.8
  SecondAngle = 0
FEATURE [Part::Cylinder] Cylinder129
  Angle = 360
  AttacherType = Attacher::AttachEngine3D
  FirstAngle = 0
  Height = 300
  Placement = pos=(106.066,-43.934,90) rot=(0.862856,-0.357407,-0.357407;1.71777rad)
  Radius = 2.8
  SecondAngle = 0
FEATURE [Part::Cylinder] Cylinder130
  Angle = 360
  AttacherType = Attacher::AttachEngine3D
  FirstAngle = 0
  Height = 300
  Placement = pos=(-106.066,-43.934,90) rot=(0.862856,0.357407,0.357407;1.71777rad)
  Radius = 2.8
  SecondAngle = 0
FEATURE [Part::MultiFuse] Fusion074  label="m4Cuts006"
  Placement = pos=(0,0,-82) rot=(0,0,1;0rad)
  Shapes = -> [Cylinder128,Cylinder127]
FEATURE [Part::MultiFuse] Fusion075  label="m4Cuts007"
  Placement = pos=(0,0,-82) rot=(0,0,1;0rad)
  Shapes = -> [Cylinder129,Cylinder130]
FEATURE [Part::MultiFuse] Fusion076  label="m4Cuts008"
  Shapes = -> [Fusion074,Fusion075]
FEATURE [Part::Cut] Cut034  label="level002s"
  Base = -> Fusion070
  Tool = -> Fusion076
FEATURE [Part::Feature] Part__Feature197  label="CUI_VGS-75C-15"
  Placement = pos=(-32,-169,-130) rot=(0.57735,-0.57735,-0.57735;4.18879rad)
  shape: bbox 30.06 x 99.03 x 97.03 mm, 2447 faces, 17 solids (baked)
FEATURE [Part::Feature] Part__Feature198  label="F9 body"
  Placement = pos=(-78.1983,5.70939,50.7544) rot=(0,0,1;0rad)
  shape: bbox 118.8 x 26.53 x 118.8 mm, 173 faces (baked)
FEATURE [Part::Feature] Part__Feature199  label="F9 fan"
  Placement = pos=(-74.2115,10.4094,-44.9134) rot=(0,-1,0;1.65409rad)
  shape: bbox 98.04 x 20 x 97.21 mm, 60 faces (baked)
FEATURE [App::Part] F9  label="fan"
  Group = -> [Part__Feature198,Part__Feature199]
  Origin = -> Origin
  Placement = pos=(32.25,-101,-138.5) rot=(0,0,1;0rad)
FEATURE [Sketcher::SketchObject] Sketch033  label="top012"
  FullyConstrained = true
  sketch-geometry (6):
    g0: Circle CenterX=0 CenterY=-150 CenterZ=0 NormalX=0 NormalY=0 NormalZ=1 AngleXU=0 Radius=93
    g1: Circle CenterX=-57 CenterY=-150 CenterZ=0 NormalX=0 NormalY=0 NormalZ=1 AngleXU=0 Radius=21
    g2: Circle CenterX=-41.75 CenterY=-126 CenterZ=0 NormalX=0 NormalY=0 NormalZ=1 AngleXU=0 Radius=2
    g3: Circle CenterX=-30.75 CenterY=-129.1 CenterZ=0 NormalX=0 NormalY=0 NormalZ=1 AngleXU=0 Radius=1.625
    g4: Circle CenterX=-30.75 CenterY=-203.5 CenterZ=0 NormalX=0 NormalY=0 NormalZ=1 AngleXU=0 Radius=1.625
    g5: Circle CenterX=57 CenterY=-150 CenterZ=0 NormalX=0 NormalY=0 NormalZ=1 AngleXU=0 Radius=21
  constraints (18):
    c: PointOnObject(g0,g-2)
    c: Radius(g0) = 93
    c: DistanceY(g0) = -150
    c: Radius(g1) = 21
    c: DistanceX(g0,g1) = -57
    c: DistanceY(g1,g0) = 0
    c: DistanceY(g1,g5) = 0
    c: DistanceX(g0,g5) = 57
    c: Radius(g5) = 21
    c: DistanceY(g4,g0) = 53.5
    c: Equal(g3,g4)
    c: Radius(g3) = 1.625
    c: DistanceX(g2,g4) = 11
    c: DistanceY(g4,g2) = 77.5
    c: Radius(g2) = 2
    c: DistanceX(g4,g0) = 30.75
    c: DistanceX(g4,g3) = 0
    c: DistanceY(g4,g3) = 74.4
FEATURE [Sketcher::SketchObject] Sketch034
  FullyConstrained = true
  Placement = pos=(0,0,0) rot=(1,0,0;1.5708rad)
  sketch-geometry (12):
    g0: LineSegment StartX=-51 StartY=-85 StartZ=0 EndX=-31 EndY=-85 EndZ=0
    g1: LineSegment StartX=-31 StartY=-85 StartZ=0 EndX=-31 EndY=-180 EndZ=0
    g2: LineSegment StartX=-31 StartY=-180 StartZ=0 EndX=-51 EndY=-180 EndZ=0
    g3: LineSegment StartX=-51 StartY=-180 StartZ=0 EndX=-51 EndY=-85 EndZ=0
    g4: LineSegment StartX=31 StartY=-180 StartZ=0 EndX=51 EndY=-180 EndZ=0
    g5: LineSegment StartX=51 StartY=-180 StartZ=0 EndX=51 EndY=-85 EndZ=0
    g6: LineSegment StartX=51 StartY=-85 StartZ=0 EndX=31 EndY=-85 EndZ=0
    g7: LineSegment StartX=31 StartY=-85 StartZ=0 EndX=31 EndY=-180 EndZ=0
    g8: Circle CenterX=-41 CenterY=-92.75 CenterZ=0 NormalX=0 NormalY=0 NormalZ=1 AngleXU=0 Radius=2.8
    g9: Circle CenterX=41 CenterY=-92.75 CenterZ=0 NormalX=0 NormalY=0 NormalZ=1 AngleXU=0 Radius=2.8
    g10: Circle CenterX=41 CenterY=-174.75 CenterZ=0 NormalX=0 NormalY=0 NormalZ=1 AngleXU=0 Radius=2.8
    g11: Circle CenterX=-41 CenterY=-174.75 CenterZ=0 NormalX=0 NormalY=0 NormalZ=1 AngleXU=0 Radius=2.8
  constraints (36):
    c: Coincident(g0,g1)
    c: Coincident(g1,g2)
    c: Coincident(g2,g3)
    c: Coincident(g3,g0)
    c: Horizontal(g0)
    c: Horizontal(g2)
    c: Vertical(g1)
    c: Vertical(g3)
    c: DistanceX(g2,g1) = 20
    c: DistanceY(g2) = -180
    c: DistanceX(g1) = -31
    c: DistanceY(g2,g0) = 95
    c: Coincident(g4,g5)
    c: Coincident(g5,g6)
    c: Coincident(g6,g7)
    c: Coincident(g7,g4)
    c: Horizontal(g4)
    c: Horizontal(g6)
    c: Vertical(g5)
    c: Vertical(g7)
    c: DistanceY(g4,g1) = 0
    c: DistanceX(g4) = 31
    c: DistanceX(g4,g4) = 20
    c: DistanceY(g6,g0) = 0
    c: Equal(g9,g8)
    c: Equal(g9,g11)
    c: Equal(g9,g10)
    c: Radius(g9) = 2.8
    c: DistanceY(g11) = -174.75
    c: DistanceY(g10,g11) = 0
    c: DistanceX(g11) = -41
    c: DistanceX(g10) = 41
    c: DistanceX(g8,g11) = 0
    c: DistanceX(g9,g10) = 0
    c: DistanceY(g11,g8) = 82
    c: DistanceY(g9,g8) = 0
FEATURE [Part::Extrusion] Extrude015  label="level4"
  Base = -> Sketch033
  Dir = (0,0,1)
  DirMode = 2
  FaceMakerClass = Part::FaceMakerBullseye
  LengthFwd = 5
  LengthRev = 0
  Placement = pos=(0,0,-185) rot=(0,0,1;0rad)
  Solid = true
  Symmetric = false
FEATURE [Part::Extrusion] Extrude016  label="fanHolder"
  Base = -> Sketch034
  Dir = (0,-1,-3e-16)
  DirMode = 2
  FaceMakerClass = Part::FaceMakerBullseye
  LengthFwd = 10
  LengthRev = 0
  Placement = pos=(0,-98,0) rot=(0,0,1;0rad)
  Solid = true
  Symmetric = false
FEATURE [Sketcher::SketchObject] Sketch035
  FullyConstrained = true
  Placement = pos=(0,0,0) rot=(0.57735,0.57735,0.57735;2.0944rad)
  sketch-geometry (15):
    g0: LineSegment StartX=-222 StartY=-80 StartZ=0 EndX=-210 EndY=-80 EndZ=0
    g1: LineSegment StartX=-108 StartY=-180 StartZ=0 EndX=-222 EndY=-180 EndZ=0
    g2: LineSegment StartX=-222 StartY=-180 StartZ=0 EndX=-222 EndY=-80 EndZ=0
    g3: LineSegment StartX=-120 StartY=-80 StartZ=0 EndX=-108 EndY=-80 EndZ=0
    g4: LineSegment StartX=-108 StartY=-80 StartZ=0 EndX=-108 EndY=-180 EndZ=0
    g5: Circle CenterX=-216 CenterY=-94.75 CenterZ=0 NormalX=0 NormalY=0 NormalZ=1 AngleXU=0 Radius=2
    g6: Circle CenterX=-113.8 CenterY=-87.8 CenterZ=0 NormalX=0 NormalY=0 NormalZ=1 AngleXU=0 Radius=2
    g7: Circle CenterX=-113.8 CenterY=-176.2 CenterZ=0 NormalX=0 NormalY=0 NormalZ=1 AngleXU=0 Radius=2
    g8: Circle CenterX=-216 CenterY=-176.2 CenterZ=0 NormalX=0 NormalY=0 NormalZ=1 AngleXU=0 Radius=2
    g9: LineSegment StartX=-210 StartY=-80 StartZ=0 EndX=-210 EndY=-120 EndZ=0
    g10: LineSegment StartX=-210 StartY=-120 StartZ=0 EndX=-120 EndY=-120 EndZ=0
    g11: LineSegment StartX=-120 StartY=-120 StartZ=0 EndX=-120 EndY=-80 EndZ=0
    g12: Circle CenterX=-155.2 CenterY=-125.25 CenterZ=0 NormalX=0 NormalY=0 NormalZ=1 AngleXU=0 Radius=1.625
    g13: Circle CenterX=-140 CenterY=-134.25 CenterZ=0 NormalX=0 NormalY=0 NormalZ=1 AngleXU=0 Radius=1.625
    g14: Circle CenterX=-195 CenterY=-134.25 CenterZ=0 NormalX=0 NormalY=0 NormalZ=1 AngleXU=0 Radius=1.625
  constraints (45):
    c: Coincident(g1,g2)
    c: Coincident(g2,g0)
    c: Horizontal(g0)
    c: Horizontal(g1)
    c: Vertical(g2)
    c: Coincident(g3,g4)
    c: Horizontal(g3)
    c: Vertical(g4)
    c: DistanceY(g1) = -180
    c: DistanceY(g1,g0) = 100
    c: Coincident(g9,g0)
    c: Vertical(g9)
    c: Coincident(g10,g9)
    c: Horizontal(g10)
    c: Coincident(g11,g10)
    c: Coincident(g11,g3)
    c: DistanceX(g1) = -222
    c: DistanceX(g1,g4) = 114
    c: DistanceY(g1,g8) = 3.8
    c: DistanceY(g7,g8) = 0
    c: Vertical(g11)
    c: DistanceX(g0,g0) = 12
    c: DistanceX(g3,g3) = 12
    c: DistanceY(g0,g3) = 0
    c: DistanceY(g4,g10) = 60
    c: DistanceY(g1,g14) = 45.75
    c: DistanceY(g13,g14) = 0
    c: DistanceX(g14,g13) = 55
    c: DistanceY(g13,g12) = 9
    c: DistanceX(g12,g13) = 15.2
    c: Equal(g13,g12)
    c: Equal(g13,g14)
    c: Radius(g13) = 1.625
    c: DistanceX(g13) = -140
    c: Equal(g6,g7)
    c: Equal(g6,g8)
    c: Equal(g6,g5)
    c: Radius(g6) = 2
    c: DistanceX(g1,g8) = 6
    c: DistanceX(g8,g7) = 102.2
    c: DistanceX(g6,g7) = 0
    c: DistanceX(g5,g8) = 0
    c: DistanceY(g8,g5) = 81.45
    c: DistanceY(g7,g6) = 88.4
    c: Coincident(g1,g4)
FEATURE [Part::Extrusion] Extrude017  label="powerSBCHolder"
  Base = -> Sketch035
  Dir = (1,0,0)
  DirMode = 2
  FaceMakerClass = Part::FaceMakerBullseye
  LengthFwd = 10
  LengthRev = 0
  Placement = pos=(-15,0,0) rot=(0,0,1;0rad)
  Solid = true
  Symmetric = false
FEATURE [Part::MultiFuse] Fusion077  label="level004"
  Shapes = -> [Extrude015,Extrude016,Extrude017]
FEATURE [Part::Feature] Part__Feature028  label="DCP-RJ6ST-F"
  Placement = pos=(57,-150,-239.5) rot=(0,1,0;3.14159rad)
  shape: bbox 40.26 x 40.33 x 38.85 mm, 485 faces, 2 solids (baked)
FEATURE [Part::Feature] Part__Feature027  label="DCC-RJ6ST-310"
  Placement = pos=(57,-150,-259) rot=(0,0,1;0rad)
  shape: bbox 40.36 x 68.07 x 51.72 mm, 441 faces (baked)
FEATURE [Part::Feature] Part__Feature022  label="3136N138_T-Slotted Framing"
  Placement = pos=(0,200.3,0) rot=(0,0,1;0rad)
  shape: bbox 101.6 x 133.4 x 139.7 mm, 136 faces (baked)
FEATURE [Part::Feature] Part__Feature023  label="47065T801_T-Slotted Framing"
  Placement = pos=(0,300.5,0) rot=(-1,0,0;1.5708rad)
  shape: bbox 25.4 x 152.4 x 25.4 mm, 108 faces (baked)
FEATURE [Part::Feature] Part__Feature024  label="47065T801_T-Slotted Framing001"
  Placement = pos=(0,450,0) rot=(-1,0,0;1.5708rad)
  shape: bbox 25.4 x 152.4 x 25.4 mm, 108 faces (baked)
FEATURE [Part::MultiFuse] Fusion079  label="framingSupport"
  Placement = pos=(0,350,-262.8) rot=(0,0,1;3.14159rad)
  Shapes = -> [Part__Feature024,Part__Feature022,Part__Feature023]
FEATURE [Sketcher::SketchObject] Sketch037  label="top013"
  FullyConstrained = true
  sketch-geometry (9):
    g0: Circle CenterX=0 CenterY=-150 CenterZ=0 NormalX=0 NormalY=0 NormalZ=1 AngleXU=0 Radius=93
    g1: Circle CenterX=-57 CenterY=-150 CenterZ=0 NormalX=0 NormalY=0 NormalZ=1 AngleXU=0 Radius=11
    g2: Circle CenterX=57 CenterY=-150 CenterZ=0 NormalX=0 NormalY=0 NormalZ=1 AngleXU=0 Radius=15.1
    g3: Circle CenterX=35 CenterY=-200 CenterZ=0 NormalX=0 NormalY=0 NormalZ=1 AngleXU=0 Radius=15.1
    g4: Circle CenterX=-35 CenterY=-200 CenterZ=0 NormalX=0 NormalY=0 NormalZ=1 AngleXU=0 Radius=6.4
    g5: ArcOfCircle CenterX=0 CenterY=-220 CenterZ=0 NormalX=0 NormalY=0 NormalZ=1 AngleXU=0 Radius=5 StartAngle=2.26529 EndAngle=7.15948
    g6: ArcOfCircle CenterX=0 CenterY=-212.5 CenterZ=0 NormalX=0 NormalY=0 NormalZ=1 AngleXU=0 Radius=3.2 StartAngle=3e-15 EndAngle=3.14159
    g7: LineSegment StartX=-3.2 StartY=-212.5 StartZ=0 EndX=-3.2 EndY=-216.158 EndZ=0
    g8: LineSegment StartX=3.2 StartY=-216.158 StartZ=0 EndX=3.2 EndY=-212.5 EndZ=0
  constraints (29):
    c: PointOnObject(g0,g-2)
    c: Radius(g0) = 93
    c: DistanceY(g0) = -150
    c: Radius(g1) = 11
    c: DistanceX(g0,g1) = -57
    c: DistanceY(g1,g0) = 0
    c: DistanceY(g1,g2) = 0
    c: DistanceX(g0,g2) = 57
    c: DistanceX(g3) = 35
    c: DistanceY(g3,g0) = 50
    c: DistanceY(g3,g4) = 0
    c: DistanceX(g4,g0) = 35
    c: Radius(g4) = 6.4
    c: Equal(g2,g3)
    c: Radius(g2) = 15.1
    c: PointOnObject(g5,g-2)
    c: PointOnObject(g6,g-2)
    c: DistanceY(g5,g0) = 70
    c: DistanceX(g5,g6) = 0
    c: DistanceX(g6,g5) = 0
    c: Coincident(g7,g6)
    c: Coincident(g7,g5)
    c: Coincident(g8,g5)
    c: Coincident(g8,g6)
    c: DistanceX(g5,g5) = 6.4
    c: DistanceY(g5,g6) = 7.5
    c: DistanceY(g6,g6) = 0
    c: DistanceY(g6,g6) = 0
    c: Radius(g5) = 5
FEATURE [Part::Extrusion] Extrude019  label="level005"
  Base = -> Sketch037
  Dir = (0,0,1)
  DirMode = 2
  FaceMakerClass = Part::FaceMakerBullseye
  LengthFwd = 8
  LengthRev = 0
  Placement = pos=(0,0,-250) rot=(0,0,1;0rad)
  Solid = true
  Symmetric = false
FEATURE [Part::Feature] Feature001  label="PG7"
  Placement = pos=(-35,-200,-248) rot=(0,0,1;0rad)
  shape: bbox 21.32 x 20.97 x 29.79 mm, 246 faces, 3 solids (baked)
FEATURE [Part::Feature] Shell029
  shape: bbox 36.98 x 21.68 x 36.68 mm, 152 faces, 0 solids (baked)
FEATURE [Part::Feature] Shell030
  shape: bbox 22.66 x 11.43 x 22.66 mm, 6 faces, 0 solids (baked)
FEATURE [Part::Feature] Shell031
  shape: bbox 0.3612 x 0.889 x 0.6255 mm, 1 faces, 0 solids (baked)
FEATURE [Part::Feature] Shell032
  shape: bbox 35.58 x 29.16 x 35.58 mm, 49 faces, 0 solids (baked)
FEATURE [Part::Feature] Shell033
  shape: bbox 24.46 x 14.2 x 24.46 mm, 102 faces, 0 solids (baked)
FEATURE [Part::Feature] Shell034
  shape: bbox 0.3892 x 1.194 x 0.6742 mm, 1 faces, 0 solids (baked)
FEATURE [Part::Feature] Shell035
  shape: bbox 0.2703 x 0.381 x 0.4682 mm, 1 faces, 0 solids (baked)
FEATURE [Part::Feature] Shell036
  shape: bbox 0.2577 x 0.3048 x 0.4459 mm, 1 faces, 0 solids (baked)
FEATURE [Part::Feature] Shell037
  shape: bbox 36.98 x 18.12 x 36.6 mm, 205 faces, 0 solids (baked)
FEATURE [Part::Compound2] Compound003  label="M3222GBH_SW0002"
  Links = -> [Shell037,Shell029,Shell030,Shell033,Shell032,Shell036,Shell034,Shell031,Shell035]
  Placement = pos=(35,-200,-250) rot=(1,0,0;4.71239rad)
FEATURE [Part::Feature] Part__Feature200  label="powerInsert"
  Placement = pos=(-57,-150,-267) rot=(1,0,0;1.5708rad)
  shape: bbox 29.63 x 29.64 x 35.77 mm, 59 faces (baked)
FEATURE [Sketcher::SketchObject] Sketch038
  FullyConstrained = true
  sketch-geometry (4):
    g0: ArcOfCircle CenterX=0 CenterY=-220 CenterZ=0 NormalX=0 NormalY=0 NormalZ=1 AngleXU=0 Radius=5 StartAngle=3.14159 EndAngle=6.28319
    g1: ArcOfCircle CenterX=-1.2e-15 CenterY=-212.5 CenterZ=0 NormalX=0 NormalY=0 NormalZ=1 AngleXU=0 Radius=5 StartAngle=1.419e-13 EndAngle=3.14159
    g2: LineSegment StartX=5 StartY=-220 StartZ=0 EndX=5 EndY=-212.5 EndZ=0
    g3: LineSegment StartX=-5 StartY=-212.5 StartZ=0 EndX=-5 EndY=-220 EndZ=0
  constraints (10):
    c: Tangent(g0,g2) = -1.5708
    c: Tangent(g2,g1) = -1.5708
    c: Tangent(g1,g3) = -1.5708
    c: Tangent(g3,g0) = -1.5708
    c: Equal(g0,g1)
    c: Vertical(g2)
    c: DistanceX(g0) = 0
    c: DistanceY(g0) = -220
    c: Radius(g0) = 5
    c: DistanceY(g0,g1) = 7.5
FEATURE [Part::Extrusion] Extrude020  label="micCutLevel5"
  Base = -> Sketch038
  Dir = (0,0,1)
  DirMode = 2
  FaceMakerClass = Part::FaceMakerBullseye
  LengthFwd = 10
  LengthRev = 0
  Placement = pos=(0,0,-246.5) rot=(0,0,1;0rad)
  Solid = true
  Symmetric = false
FEATURE [Sketcher::SketchObject] Sketch039
  FullyConstrained = true
  sketch-geometry (16):
    g0: ArcOfCircle CenterX=0 CenterY=-150 CenterZ=0 NormalX=0 NormalY=0 NormalZ=1 AngleXU=0 Radius=93 StartAngle=2.86943 EndAngle=3.41376
    g1: ArcOfCircle CenterX=0 CenterY=-150 CenterZ=0 NormalX=0 NormalY=0 NormalZ=1 AngleXU=0 Radius=93 StartAngle=1.29863 EndAngle=1.84296
    g2: ArcOfCircle CenterX=0 CenterY=-150 CenterZ=0 NormalX=0 NormalY=0 NormalZ=1 AngleXU=0 Radius=93 StartAngle=6.01102 EndAngle=6.55535
    g3: ArcOfCircle CenterX=0 CenterY=-150 CenterZ=0 NormalX=0 NormalY=0 NormalZ=1 AngleXU=0 Radius=93 StartAngle=4.44022 EndAngle=4.98455
    g4: ArcOfCircle CenterX=0 CenterY=-150 CenterZ=0 NormalX=0 NormalY=0 NormalZ=1 AngleXU=0 Radius=86 StartAngle=1.27584 EndAngle=1.86575
    g5: ArcOfCircle CenterX=0 CenterY=-150 CenterZ=0 NormalX=0 NormalY=0 NormalZ=1 AngleXU=0 Radius=86 StartAngle=5.98823 EndAngle=6.57814
    g6: ArcOfCircle CenterX=0 CenterY=-150 CenterZ=0 NormalX=0 NormalY=0 NormalZ=1 AngleXU=0 Radius=86 StartAngle=2.84664 EndAngle=3.43655
    g7: ArcOfCircle CenterX=0 CenterY=-150 CenterZ=0 NormalX=0 NormalY=0 NormalZ=1 AngleXU=0 Radius=86 StartAngle=4.41743 EndAngle=5.00734
    g8: LineSegment StartX=25 StartY=-60.4232 StartZ=0 EndX=25 EndY=-67.7139 EndZ=0
    g9: LineSegment StartX=-25 StartY=-60.4232 StartZ=0 EndX=-25 EndY=-67.7139 EndZ=0
    g10: LineSegment StartX=-89.5768 StartY=-125 StartZ=0 EndX=-82.2861 EndY=-125 EndZ=0
    g11: LineSegment StartX=-89.5768 StartY=-175 StartZ=0 EndX=-82.2861 EndY=-175 EndZ=0
    g12: LineSegment StartX=-25 StartY=-239.577 StartZ=0 EndX=-25 EndY=-232.286 EndZ=0
    g13: LineSegment StartX=25 StartY=-239.577 StartZ=0 EndX=25 EndY=-232.286 EndZ=0
    g14: LineSegment StartX=89.5768 StartY=-175 StartZ=0 EndX=82.2861 EndY=-175 EndZ=0
    g15: LineSegment StartX=89.5768 StartY=-125 StartZ=0 EndX=82.2861 EndY=-125 EndZ=0
  constraints (49):
    c: PointOnObject(g0,g-2)
    c: Coincident(g1,g0)
    c: Coincident(g2,g0)
    c: Coincident(g3,g0)
    c: DistanceY(g0) = -150
    c: Coincident(g4,g0)
    c: Coincident(g5,g0)
    c: Coincident(g6,g0)
    c: Coincident(g7,g0)
    c: DistanceX(g4,g0) = 25
    c: DistanceX(g1,g4) = 0
    c: DistanceX(g0,g4) = 25
    c: DistanceX(g4,g1) = 0
    c: DistanceY(g0,g5) = 25
    c: DistanceY(g5,g2) = 0
    c: DistanceY(g2,g0) = 25
    c: DistanceY(g2,g5) = 0
    c: DistanceY(g6,g0) = 25
    c: DistanceY(g0,g6) = 0
    c: DistanceY(g0,g6) = 25
    c: DistanceY(g6,g0) = 0
    c: Equal(g1,g2)
    c: Equal(g1,g3)
    c: Equal(g1,g0)
    c: Radius(g1) = 93
    c: Equal(g6,g4)
    c: Equal(g6,g5)
    c: Equal(g6,g7)
    c: Radius(g6) = 86
    c: DistanceX(g0,g7) = 25
    c: DistanceX(g7,g3) = 0
    c: DistanceX(g3) = -25
    c: DistanceX(g3,g7) = 0
    c: Coincident(g8,g1)
    c: Coincident(g8,g4)
    c: Coincident(g9,g1)
    c: Coincident(g9,g4)
    c: Coincident(g10,g0)
    c: Coincident(g10,g6)
    c: Coincident(g11,g0)
    c: Coincident(g11,g6)
    c: Coincident(g12,g3)
    c: Coincident(g12,g7)
    c: Coincident(g13,g3)
    c: Coincident(g13,g7)
    c: Coincident(g14,g2)
    c: Coincident(g14,g5)
    c: Coincident(g15,g2)
    c: Coincident(g15,g5)
FEATURE [Part::Extrusion] Extrude021  label="srsHolds002"
  Base = -> Sketch039
  Dir = (0,0,1)
  DirMode = 2
  FaceMakerClass = Part::FaceMakerBullseye
  LengthFwd = 30
  LengthRev = 0
  Placement = pos=(0,0,-185) rot=(0,0,1;0rad)
  Solid = true
  Symmetric = false
FEATURE [Part::FeaturePython] Tube003  # WARN: FeaturePython — macro-defined, semantics opaque (R4)
  AttacherType = Attacher::AttachEngine3D
  Height = 125
  InnerRadius = 94
  OuterRadius = 98
  Placement = pos=(0,-150,-185) rot=(0,0,1;0rad)
FEATURE [Sketcher::SketchObject] Sketch040  label="top014"
  FullyConstrained = true
  sketch-geometry (2):
    g0: Circle CenterX=0 CenterY=-150 CenterZ=0 NormalX=0 NormalY=0 NormalZ=1 AngleXU=0 Radius=98
    g1: Circle CenterX=0 CenterY=-150 CenterZ=0 NormalX=0 NormalY=0 NormalZ=1 AngleXU=0 Radius=78
  constraints (5):
    c: PointOnObject(g0,g-2)
    c: Diameter(g0) = 196
    c: DistanceY(g0) = -150
    c: Coincident(g1,g0)
    c: Radius(g1) = 78
FEATURE [Part::Extrusion] Extrude022  label="TupeConnectLevel3"
  Base = -> Sketch040
  Dir = (0,0,1)
  DirMode = 2
  FaceMakerClass = Part::FaceMakerBullseye
  LengthFwd = 5
  LengthRev = 0
  Placement = pos=(0,0,-65) rot=(0,0,1;0rad)
  Solid = true
  Symmetric = false
FEATURE [Part::MultiFuse] Fusion080  label="tube4to3"
  Shapes = -> [Extrude022,Tube003]
FEATURE [Part::MultiFuse] Fusion081  label="level04"
  Shapes = -> [Fusion077,Extrude021]
FEATURE [Sketcher::SketchObject] Sketch041
  FullyConstrained = true
  sketch-geometry (16):
    g0: ArcOfCircle CenterX=0 CenterY=-150 CenterZ=0 NormalX=0 NormalY=0 NormalZ=1 AngleXU=0 Radius=93 StartAngle=2.86943 EndAngle=3.41376
    g1: ArcOfCircle CenterX=0 CenterY=-150 CenterZ=0 NormalX=0 NormalY=0 NormalZ=1 AngleXU=0 Radius=93 StartAngle=1.29863 EndAngle=1.84296
    g2: ArcOfCircle CenterX=0 CenterY=-150 CenterZ=0 NormalX=0 NormalY=0 NormalZ=1 AngleXU=0 Radius=93 StartAngle=6.01102 EndAngle=6.55535
    g3: ArcOfCircle CenterX=0 CenterY=-150 CenterZ=0 NormalX=0 NormalY=0 NormalZ=1 AngleXU=0 Radius=93 StartAngle=4.44022 EndAngle=4.98455
    g4: ArcOfCircle CenterX=0 CenterY=-150 CenterZ=0 NormalX=0 NormalY=0 NormalZ=1 AngleXU=0 Radius=86 StartAngle=1.27584 EndAngle=1.86575
    g5: ArcOfCircle CenterX=0 CenterY=-150 CenterZ=0 NormalX=0 NormalY=0 NormalZ=1 AngleXU=0 Radius=86 StartAngle=5.98823 EndAngle=6.57814
    g6: ArcOfCircle CenterX=0 CenterY=-150 CenterZ=0 NormalX=0 NormalY=0 NormalZ=1 AngleXU=0 Radius=86 StartAngle=2.84664 EndAngle=3.43655
    g7: ArcOfCircle CenterX=0 CenterY=-150 CenterZ=0 NormalX=0 NormalY=0 NormalZ=1 AngleXU=0 Radius=86 StartAngle=4.41743 EndAngle=5.00734
    g8: LineSegment StartX=25 StartY=-60.4232 StartZ=0 EndX=25 EndY=-67.7139 EndZ=0
    g9: LineSegment StartX=-25 StartY=-60.4232 StartZ=0 EndX=-25 EndY=-67.7139 EndZ=0
    g10: LineSegment StartX=-89.5768 StartY=-125 StartZ=0 EndX=-82.2861 EndY=-125 EndZ=0
    g11: LineSegment StartX=-89.5768 StartY=-175 StartZ=0 EndX=-82.2861 EndY=-175 EndZ=0
    g12: LineSegment StartX=-25 StartY=-239.577 StartZ=0 EndX=-25 EndY=-232.286 EndZ=0
    g13: LineSegment StartX=25 StartY=-239.577 StartZ=0 EndX=25 EndY=-232.286 EndZ=0
    g14: LineSegment StartX=89.5768 StartY=-175 StartZ=0 EndX=82.2861 EndY=-175 EndZ=0
    g15: LineSegment StartX=89.5768 StartY=-125 StartZ=0 EndX=82.2861 EndY=-125 EndZ=0
  constraints (49):
    c: PointOnObject(g0,g-2)
    c: Coincident(g1,g0)
    c: Coincident(g2,g0)
    c: Coincident(g3,g0)
    c: DistanceY(g0) = -150
    c: Coincident(g4,g0)
    c: Coincident(g5,g0)
    c: Coincident(g6,g0)
    c: Coincident(g7,g0)
    c: DistanceX(g4,g0) = 25
    c: DistanceX(g1,g4) = 0
    c: DistanceX(g0,g4) = 25
    c: DistanceX(g4,g1) = 0
    c: DistanceY(g0,g5) = 25
    c: DistanceY(g5,g2) = 0
    c: DistanceY(g2,g0) = 25
    c: DistanceY(g2,g5) = 0
    c: DistanceY(g6,g0) = 25
    c: DistanceY(g0,g6) = 0
    c: DistanceY(g0,g6) = 25
    c: DistanceY(g6,g0) = 0
    c: Equal(g1,g2)
    c: Equal(g1,g3)
    c: Equal(g1,g0)
    c: Radius(g1) = 93
    c: Equal(g6,g4)
    c: Equal(g6,g5)
    c: Equal(g6,g7)
    c: Radius(g6) = 86
    c: DistanceX(g0,g7) = 25
    c: DistanceX(g7,g3) = 0
    c: DistanceX(g3) = -25
    c: DistanceX(g3,g7) = 0
    c: Coincident(g8,g1)
    c: Coincident(g8,g4)
    c: Coincident(g9,g1)
    c: Coincident(g9,g4)
    c: Coincident(g10,g0)
    c: Coincident(g10,g6)
    c: Coincident(g11,g0)
    c: Coincident(g11,g6)
    c: Coincident(g12,g3)
    c: Coincident(g12,g7)
    c: Coincident(g13,g3)
    c: Coincident(g13,g7)
    c: Coincident(g14,g2)
    c: Coincident(g14,g5)
    c: Coincident(g15,g2)
    c: Coincident(g15,g5)
FEATURE [Part::Extrusion] Extrude023  label="srsHoldsLevel5"
  Base = -> Sketch041
  Dir = (0,0,1)
  DirMode = 2
  FaceMakerClass = Part::FaceMakerBullseye
  LengthFwd = 30
  LengthRev = 0
  Placement = pos=(0,0,-250) rot=(0,0,1;0rad)
  Solid = true
  Symmetric = false
FEATURE [Sketcher::SketchObject] Sketch042  label="top015"
  FullyConstrained = true
  sketch-geometry (2):
    g0: Circle CenterX=0 CenterY=-150 CenterZ=0 NormalX=0 NormalY=0 NormalZ=1 AngleXU=0 Radius=98
    g1: Circle CenterX=0 CenterY=-150 CenterZ=0 NormalX=0 NormalY=0 NormalZ=1 AngleXU=0 Radius=76
  constraints (5):
    c: PointOnObject(g0,g-2)
    c: Diameter(g0) = 196
    c: DistanceY(g0) = -150
    c: Coincident(g1,g0)
    c: Radius(g1) = 76
FEATURE [Part::Extrusion] Extrude024  label="TupeConnectLevel004"
  Base = -> Sketch042
  Dir = (0,0,1)
  DirMode = 2
  FaceMakerClass = Part::FaceMakerBullseye
  LengthFwd = 5
  LengthRev = 0
  Placement = pos=(0,0,-65) rot=(0,0,1;0rad)
  Solid = true
  Symmetric = false
FEATURE [Part::FeaturePython] Tube004  # WARN: FeaturePython — macro-defined, semantics opaque (R4)
  AttacherType = Attacher::AttachEngine3D
  Height = 65
  InnerRadius = 94
  OuterRadius = 98
  Placement = pos=(0,-150,-125) rot=(0,0,1;0rad)
FEATURE [Part::MultiFuse] Fusion082  label="tube5to004"
  Placement = pos=(0,0,-125) rot=(0,0,1;0rad)
  Shapes = -> [Extrude024,Tube004]
FEATURE [Part::MultiFuse] Fusion083  label="level5"
  Shapes = -> [Extrude019,Extrude023]
FEATURE [Part::Cylinder] Cylinder131
  Angle = 360
  AttacherType = Attacher::AttachEngine3D
  FirstAngle = 0
  Height = 300
  Placement = pos=(0,0,90) rot=(1,0,0;1.5708rad)
  Radius = 2.13
  SecondAngle = 0
FEATURE [Part::Cylinder] Cylinder132
  Angle = 360
  AttacherType = Attacher::AttachEngine3D
  FirstAngle = 0
  Height = 300
  Placement = pos=(-150,-150,90) rot=(0.57735,0.57735,0.57735;2.0944rad)
  Radius = 2.13
  SecondAngle = 0
FEATURE [Part::MultiFuse] Fusion084  label="m4Cuts009"
  Placement = pos=(0,0,-321) rot=(0,0,1;0rad)
  Shapes = -> [Cylinder132,Cylinder131]
FEATURE [Part::Cylinder] Cylinder133
  Angle = 360
  AttacherType = Attacher::AttachEngine3D
  FirstAngle = 0
  Height = 300
  Placement = pos=(0,0,90) rot=(1,0,0;1.5708rad)
  Radius = 2.8
  SecondAngle = 0
FEATURE [Part::Cylinder] Cylinder134
  Angle = 360
  AttacherType = Attacher::AttachEngine3D
  FirstAngle = 0
  Height = 300
  Placement = pos=(-150,-150,90) rot=(0.57735,0.57735,0.57735;2.0944rad)
  Radius = 2.8
  SecondAngle = 0
FEATURE [Part::MultiFuse] Fusion085  label="m4HeatSetCuts001"
  Placement = pos=(0,0,-321) rot=(0,0,1;0rad)
  Shapes = -> [Cylinder134,Cylinder133]
FEATURE [Sketcher::SketchObject] Sketch043
  FullyConstrained = true
  sketch-geometry (4):
    g0: Circle CenterX=0 CenterY=-68 CenterZ=0 NormalX=0 NormalY=0 NormalZ=1 AngleXU=0 Radius=2.125
    g1: Circle CenterX=82 CenterY=-150 CenterZ=0 NormalX=0 NormalY=0 NormalZ=1 AngleXU=0 Radius=2.125
    g2: Circle CenterX=0 CenterY=-232 CenterZ=0 NormalX=0 NormalY=0 NormalZ=1 AngleXU=0 Radius=2.125
    g3: Circle CenterX=-82 CenterY=-150 CenterZ=0 NormalX=0 NormalY=0 NormalZ=1 AngleXU=0 Radius=2.125
  constraints (12):
    c: PointOnObject(g0,g-2)
    c: DistanceY(g1) = -150
    c: DistanceY(g1,g3) = 0
    c: DistanceX(g2) = 0
    c: DistanceX(g1) = 82
    c: Equal(g1,g0)
    c: Equal(g1,g3)
    c: Equal(g1,g2)
    c: Diameter(g1) = 4.25
    c: DistanceX(g3) = -82
    c: DistanceY(g3,g0) = 82
    c: DistanceY(g2,g3) = 82
FEATURE [Part::Extrusion] Extrude025  label="m4VerCuts"
  Base = -> Sketch043
  Dir = (0,0,1)
  DirMode = 2
  FaceMakerClass = Part::FaceMakerBullseye
  LengthFwd = 20
  LengthRev = 0
  Placement = pos=(0,0,-194.5) rot=(0,0,1;0rad)
  Solid = true
  Symmetric = false
FEATURE [Sketcher::SketchObject] Sketch044
  FullyConstrained = true
  sketch-geometry (4):
    g0: Circle CenterX=0 CenterY=-68 CenterZ=0 NormalX=0 NormalY=0 NormalZ=1 AngleXU=0 Radius=2.8
    g1: Circle CenterX=82 CenterY=-150 CenterZ=0 NormalX=0 NormalY=0 NormalZ=1 AngleXU=0 Radius=2.8
    g2: Circle CenterX=0 CenterY=-232 CenterZ=0 NormalX=0 NormalY=0 NormalZ=1 AngleXU=0 Radius=2.8
    g3: Circle CenterX=-82 CenterY=-150 CenterZ=0 NormalX=0 NormalY=0 NormalZ=1 AngleXU=0 Radius=2.8
  constraints (12):
    c: PointOnObject(g0,g-2)
    c: DistanceY(g1) = -150
    c: DistanceY(g1,g3) = 0
    c: DistanceX(g2) = 0
    c: DistanceX(g1) = 82
    c: Equal(g1,g0)
    c: Equal(g1,g3)
    c: Equal(g1,g2)
    c: Diameter(g1) = 5.6
    c: DistanceX(g3) = -82
    c: DistanceY(g3,g0) = 82
    c: DistanceY(g2,g3) = 82
FEATURE [Part::Extrusion] Extrude026  label="m4HeatSetVerCuts001"
  Base = -> Sketch044
  Dir = (0,0,1)
  DirMode = 2
  FaceMakerClass = Part::FaceMakerBullseye
  LengthFwd = 20
  LengthRev = 0
  Placement = pos=(0,0,-193) rot=(0,0,1;0rad)
  Solid = true
  Symmetric = false
FEATURE [Part::Cut] Cut035  label="level05s"
  Base = -> Fusion083
  Tool = -> Fusion085
FEATURE [Part::Cut] Cut036  label="tube4to5"
  Base = -> Fusion082
  Tool = -> Fusion084
FEATURE [Part::Cut] Cut037  label="level4s"
  Base = -> Fusion081
  Tool = -> Extrude025
FEATURE [Part::Cut] Cut038  label="tube4to5s"
  Base = -> Cut036
  Tool = -> Extrude026
FEATURE [Part::Cylinder] Cylinder135
  Angle = 360
  AttacherType = Attacher::AttachEngine3D
  FirstAngle = 0
  Height = 300
  Placement = pos=(0,0,90) rot=(1,0,0;1.5708rad)
  Radius = 2.8
  SecondAngle = 0
FEATURE [Part::Cylinder] Cylinder136
  Angle = 360
  AttacherType = Attacher::AttachEngine3D
  FirstAngle = 0
  Height = 300
  Placement = pos=(-150,-150,90) rot=(0.57735,0.57735,0.57735;2.0944rad)
  Radius = 2.8
  SecondAngle = 0
FEATURE [Part::MultiFuse] Fusion086  label="m4HeatSetCuts002"
  Placement = pos=(0,0,-257) rot=(0,0,1;0rad)
  Shapes = -> [Cylinder136,Cylinder135]
FEATURE [Part::Cut] Cut039  label="level4s001"
  Base = -> Cut037
  Tool = -> Fusion086
FEATURE [Part::Cylinder] Cylinder137
  Angle = 360
  AttacherType = Attacher::AttachEngine3D
  FirstAngle = 0
  Height = 300
  Placement = pos=(0,0,90) rot=(1,0,0;1.5708rad)
  Radius = 2.13
  SecondAngle = 0
FEATURE [Part::Cylinder] Cylinder138
  Angle = 360
  AttacherType = Attacher::AttachEngine3D
  FirstAngle = 0
  Height = 300
  Placement = pos=(-150,-150,90) rot=(0.57735,0.57735,0.57735;2.0944rad)
  Radius = 2.13
  SecondAngle = 0
FEATURE [Part::MultiFuse] Fusion087  label="m4Cuts010"
  Placement = pos=(0,0,-257) rot=(0,0,1;0rad)
  Shapes = -> [Cylinder138,Cylinder137]
FEATURE [Part::Cut] Cut040  label="level3to4Tube"
  Base = -> Fusion080
  Tool = -> Fusion087
FEATURE [Part::Cut] Cut041  label="level5s"
  Base = -> Cut035
  Tool = -> Extrude020
FEATURE [Sketcher::SketchObject] Sketch046
  FullyConstrained = true
  sketch-geometry (4):
    g0: Circle CenterX=0 CenterY=-63 CenterZ=0 NormalX=0 NormalY=0 NormalZ=1 AngleXU=0 Radius=2.8
    g1: Circle CenterX=87 CenterY=-150 CenterZ=0 NormalX=0 NormalY=0 NormalZ=1 AngleXU=0 Radius=2.8
    g2: Circle CenterX=0 CenterY=-237 CenterZ=0 NormalX=0 NormalY=0 NormalZ=1 AngleXU=0 Radius=2.8
    g3: Circle CenterX=-87 CenterY=-150 CenterZ=0 NormalX=0 NormalY=0 NormalZ=1 AngleXU=0 Radius=2.8
  constraints (12):
    c: PointOnObject(g0,g-2)
    c: DistanceY(g1) = -150
    c: DistanceY(g1,g3) = 0
    c: DistanceX(g2) = 0
    c: DistanceX(g1) = 87
    c: Equal(g1,g0)
    c: Equal(g1,g3)
    c: Equal(g1,g2)
    c: Diameter(g1) = 5.6
    c: DistanceX(g3) = -87
    c: DistanceY(g3,g0) = 87
    c: DistanceY(g2,g3) = 87
FEATURE [Part::Extrusion] Extrude028  label="m4HeatSetVerCuts003"
  Base = -> Sketch046
  Dir = (0,0,1)
  DirMode = 2
  FaceMakerClass = Part::FaceMakerBullseye
  LengthFwd = 20
  LengthRev = 0
  Placement = pos=(0,0,-69.5) rot=(0,0,1;0rad)
  Solid = true
  Symmetric = false
FEATURE [Sketcher::SketchObject] Sketch047
  FullyConstrained = true
  sketch-geometry (4):
    g0: Circle CenterX=0 CenterY=-63 CenterZ=0 NormalX=0 NormalY=0 NormalZ=1 AngleXU=0 Radius=2.125
    g1: Circle CenterX=87 CenterY=-150 CenterZ=0 NormalX=0 NormalY=0 NormalZ=1 AngleXU=0 Radius=2.125
    g2: Circle CenterX=0 CenterY=-237 CenterZ=0 NormalX=0 NormalY=0 NormalZ=1 AngleXU=0 Radius=2.125
    g3: Circle CenterX=-87 CenterY=-150 CenterZ=0 NormalX=0 NormalY=0 NormalZ=1 AngleXU=0 Radius=2.125
  constraints (12):
    c: PointOnObject(g0,g-2)
    c: DistanceY(g1) = -150
    c: DistanceY(g1,g3) = 0
    c: DistanceX(g2) = 0
    c: DistanceX(g1) = 87
    c: Equal(g1,g0)
    c: Equal(g1,g3)
    c: Equal(g1,g2)
    c: Diameter(g1) = 4.25
    c: DistanceX(g3) = -87
    c: DistanceY(g3,g0) = 87
    c: DistanceY(g2,g3) = 87
FEATURE [Part::Extrusion] Extrude029  label="m4VerCuts001"
  Base = -> Sketch047
  Dir = (0,0,1)
  DirMode = 2
  FaceMakerClass = Part::FaceMakerBullseye
  LengthFwd = 20
  LengthRev = 0
  Placement = pos=(0,0,-65.5) rot=(0,0,1;0rad)
  Solid = true
  Symmetric = false
FEATURE [Part::Cut] Cut042  label="tube3to4s"
  Base = -> Cut040
  Tool = -> Extrude028
FEATURE [Part::Cut] Cut043  label="level03"
  Base = -> Fusion067
  Tool = -> Extrude029
FEATURE [Part::Cylinder] Cylinder139
  Angle = 360
  AttacherType = Attacher::AttachEngine3D
  FirstAngle = 0
  Height = 300
  Placement = pos=(0,0,90) rot=(1,0,0;1.5708rad)
  Radius = 2.13
  SecondAngle = 0
FEATURE [Part::Cylinder] Cylinder140
  Angle = 360
  AttacherType = Attacher::AttachEngine3D
  FirstAngle = 0
  Height = 300
  Placement = pos=(-150,-150,90) rot=(0.57735,0.57735,0.57735;2.0944rad)
  Radius = 2.13
  SecondAngle = 0
FEATURE [Part::MultiFuse] Fusion088  label="m4Cuts011"
  Placement = pos=(0,0,-130) rot=(0,0,1;0rad)
  Shapes = -> [Cylinder140,Cylinder139]
FEATURE [Part::Cut] Cut044  label="tube3to2s"
  Base = -> Tube002
  Tool = -> Fusion088
FEATURE [Part::Cylinder] Cylinder141
  Angle = 360
  AttacherType = Attacher::AttachEngine3D
  FirstAngle = 0
  Height = 300
  Placement = pos=(0,0,90) rot=(1,0,0;1.5708rad)
  Radius = 2.8
  SecondAngle = 0
FEATURE [Part::Cylinder] Cylinder142
  Angle = 360
  AttacherType = Attacher::AttachEngine3D
  FirstAngle = 0
  Height = 300
  Placement = pos=(-150,-150,90) rot=(0.57735,0.57735,0.57735;2.0944rad)
  Radius = 2.8
  SecondAngle = 0
FEATURE [Part::MultiFuse] Fusion089  label="m4HeatSetCuts003"
  Placement = pos=(0,0,-130) rot=(0,0,1;0rad)
  Shapes = -> [Cylinder142,Cylinder141]
FEATURE [Part::Cylinder] Cylinder143  label="heatSetHolds"
  Angle = 360
  AttacherType = Attacher::AttachEngine3D
  FirstAngle = 0
  Height = 10
  Placement = pos=(0,-78,-40) rot=(-1,0,0;1.5708rad)
  Radius = 8
  SecondAngle = 0
FEATURE [Part::Cylinder] Cylinder144  label="heatSetHolds001"
  Angle = 360
  AttacherType = Attacher::AttachEngine3D
  FirstAngle = 0
  Height = 10
  Placement = pos=(0,-221,-40) rot=(0,0.707107,-0.707107;3.14159rad)
  Radius = 8
  SecondAngle = 0
FEATURE [Part::Cylinder] Cylinder145  label="heatSetHolds002"
  Angle = 360
  AttacherType = Attacher::AttachEngine3D
  FirstAngle = 0
  Height = 10
  Placement = pos=(72,-150,-40) rot=(0.57735,-0.57735,0.57735;4.18879rad)
  Radius = 8
  SecondAngle = 0
FEATURE [Part::Cylinder] Cylinder146  label="heatSetHolds003"
  Angle = 360
  AttacherType = Attacher::AttachEngine3D
  FirstAngle = 0
  Height = 10
  Placement = pos=(-72,-150,-40) rot=(0.57735,0.57735,-0.57735;4.18879rad)
  Radius = 8
  SecondAngle = 0
FEATURE [Part::MultiFuse] Fusion090  label="m4HeatSetHolds"
  Shapes = -> [Cylinder143,Cylinder144,Cylinder145,Cylinder146]
FEATURE [Part::MultiFuse] Fusion091  label="level003s"
  Shapes = -> [Cut043,Fusion090]
FEATURE [Part::Cut] Cut045  label="level3s"
  Base = -> Fusion091
  Tool = -> Fusion089
FEATURE [Part::Cylinder] Cylinder147
  Angle = 360
  AttacherType = Attacher::AttachEngine3D
  FirstAngle = 0
  Height = 300
  Placement = pos=(0,0,90) rot=(1,0,0;1.5708rad)
  Radius = 2.13
  SecondAngle = 0
FEATURE [Part::Cylinder] Cylinder148
  Angle = 360
  AttacherType = Attacher::AttachEngine3D
  FirstAngle = 0
  Height = 300
  Placement = pos=(-150,-150,90) rot=(0.57735,0.57735,0.57735;2.0944rad)
  Radius = 2.13
  SecondAngle = 0
FEATURE [Part::Cylinder] Cylinder149
  Angle = 360
  AttacherType = Attacher::AttachEngine3D
  FirstAngle = 0
  Height = 300
  Placement = pos=(106.066,-43.934,90) rot=(0.862856,-0.357407,-0.357407;1.71777rad)
  Radius = 2.13
  SecondAngle = 0
FEATURE [Part::Cylinder] Cylinder150
  Angle = 360
  AttacherType = Attacher::AttachEngine3D
  FirstAngle = 0
  Height = 300
  Placement = pos=(-106.066,-43.934,90) rot=(0.862856,0.357407,0.357407;1.71777rad)
  Radius = 2.13
  SecondAngle = 0
FEATURE [Part::MultiFuse] Fusion092  label="m4Cuts012"
  Placement = pos=(0,0,-82) rot=(0,0,1;0rad)
  Shapes = -> [Cylinder148,Cylinder147]
FEATURE [Part::MultiFuse] Fusion093  label="m4Cuts013"
  Placement = pos=(0,0,-82) rot=(0,0,1;0rad)
  Shapes = -> [Cylinder149,Cylinder150]
FEATURE [Part::MultiFuse] Fusion094  label="m4Cuts014"
  Shapes = -> [Fusion092,Fusion093]
FEATURE [Part::Cut] Cut046  label="tubeLevel3to2s"
  Base = -> Cut044
  Tool = -> Fusion094
FEATURE [Part::Fillet] Fillet002  label="level4to5s"
  Base = -> Cut038
  Edges = 3 edges r=3: [Edge3,Edge7,Edge32]
FEATURE [Part::FeaturePython] Tube005  # WARN: FeaturePython — macro-defined, semantics opaque (R4)
  AttacherType = Attacher::AttachEngine3D
  Height = 3
  InnerRadius = 95
  OuterRadius = 98
  Placement = pos=(0,-150,-188) rot=(0,0,1;0rad)
FEATURE [Part::Cylinder] Cylinder151
  Angle = 360
  AttacherType = Attacher::AttachEngine3D
  FirstAngle = 0
  Height = 300
  Placement = pos=(0,0,90) rot=(1,0,0;1.5708rad)
  Radius = 2.13
  SecondAngle = 0
FEATURE [Part::Cylinder] Cylinder152
  Angle = 360
  AttacherType = Attacher::AttachEngine3D
  FirstAngle = 0
  Height = 300
  Placement = pos=(-150,-150,90) rot=(0.57735,0.57735,0.57735;2.0944rad)
  Radius = 2.13
  SecondAngle = 0
FEATURE [Part::MultiFuse] Fusion096  label="m4Cuts015"
  Placement = pos=(0,0,-321) rot=(0,0,1;0rad)
  Shapes = -> [Cylinder152,Cylinder151]
FEATURE [Sketcher::SketchObject] Sketch048  label="top016"
  FullyConstrained = true
  sketch-geometry (2):
    g0: Circle CenterX=0 CenterY=-150 CenterZ=0 NormalX=0 NormalY=0 NormalZ=1 AngleXU=0 Radius=98
    g1: Circle CenterX=0 CenterY=-150 CenterZ=0 NormalX=0 NormalY=0 NormalZ=1 AngleXU=0 Radius=76
  constraints (5):
    c: PointOnObject(g0,g-2)
    c: Diameter(g0) = 196
    c: DistanceY(g0) = -150
    c: Coincident(g1,g0)
    c: Radius(g1) = 76
FEATURE [Part::Extrusion] Extrude030  label="TupeConnectLevel005"
  Base = -> Sketch048
  Dir = (0,0,1)
  DirMode = 2
  FaceMakerClass = Part::FaceMakerBullseye
  LengthFwd = 5
  LengthRev = 0
  Placement = pos=(0,0,-65) rot=(0,0,1;0rad)
  Solid = true
  Symmetric = false
FEATURE [Sketcher::SketchObject] Sketch049
  FullyConstrained = true
  sketch-geometry (4):
    g0: Circle CenterX=0 CenterY=-68 CenterZ=0 NormalX=0 NormalY=0 NormalZ=1 AngleXU=0 Radius=2.8
    g1: Circle CenterX=82 CenterY=-150 CenterZ=0 NormalX=0 NormalY=0 NormalZ=1 AngleXU=0 Radius=2.8
    g2: Circle CenterX=0 CenterY=-232 CenterZ=0 NormalX=0 NormalY=0 NormalZ=1 AngleXU=0 Radius=2.8
    g3: Circle CenterX=-82 CenterY=-150 CenterZ=0 NormalX=0 NormalY=0 NormalZ=1 AngleXU=0 Radius=2.8
  constraints (12):
    c: PointOnObject(g0,g-2)
    c: DistanceY(g1) = -150
    c: DistanceY(g1,g3) = 0
    c: DistanceX(g2) = 0
    c: DistanceX(g1) = 82
    c: Equal(g1,g0)
    c: Equal(g1,g3)
    c: Equal(g1,g2)
    c: Diameter(g1) = 5.6
    c: DistanceX(g3) = -82
    c: DistanceY(g3,g0) = 82
    c: DistanceY(g2,g3) = 82
FEATURE [Part::Extrusion] Extrude031  label="m4HeatSetVerCuts004"
  Base = -> Sketch049
  Dir = (0,0,1)
  DirMode = 2
  FaceMakerClass = Part::FaceMakerBullseye
  LengthFwd = 20
  LengthRev = 0
  Placement = pos=(0,0,-193) rot=(0,0,1;0rad)
  Solid = true
  Symmetric = false
FEATURE [Part::FeaturePython] Tube006  # WARN: FeaturePython — macro-defined, semantics opaque (R4)
  AttacherType = Attacher::AttachEngine3D
  Height = 65
  InnerRadius = 94
  OuterRadius = 98
  Placement = pos=(0,-150,-125) rot=(0,0,1;0rad)
FEATURE [Part::MultiFuse] Fusion095  label="tube5to005"
  Placement = pos=(0,0,-125) rot=(0,0,1;0rad)
  Shapes = -> [Extrude030,Tube006]
FEATURE [Part::Cut] Cut047  label="tube4to006"
  Base = -> Fusion095
  Tool = -> Fusion096
FEATURE [Part::Cut] Cut048  label="tube4to5s001"
  Base = -> Cut047
  Tool = -> Extrude031
FEATURE [Part::Fillet] Fillet003  label="level5s002"
  Base = -> Cut048
  Edges = 3 edges r=3: [Edge3,Edge7,Edge32]
FEATURE [Part::Cut] Cut049  label="cutAddOn"
  Base = -> Tube005
  Placement = pos=(0,0,0.25) rot=(0,0,1;0rad)
  Tool = -> Fillet003
FEATURE [Part::MultiFuse] Fusion097  label="tube4to3S"
  Shapes = -> [Cut042,Cut049]
FEATURE [Part::Fillet] Fillet004  label="tube4to3s"
  Base = -> Fusion097
  Edges = 1 edges r=3: [Edge3]
FEATURE [Part::Cylinder] Cylinder153
  Angle = 360
  AttacherType = Attacher::AttachEngine3D
  FirstAngle = 0
  Height = 300
  Placement = pos=(0,0,90) rot=(1,0,0;1.5708rad)
  Radius = 2.13
  SecondAngle = 0
FEATURE [Part::Cylinder] Cylinder154
  Angle = 360
  AttacherType = Attacher::AttachEngine3D
  FirstAngle = 0
  Height = 300
  Placement = pos=(-150,-150,90) rot=(0.57735,0.57735,0.57735;2.0944rad)
  Radius = 2.13
  SecondAngle = 0
FEATURE [Part::MultiFuse] Fusion099  label="m4Cuts016"
  Placement = pos=(0,0,-321) rot=(0,0,1;0rad)
  Shapes = -> [Cylinder154,Cylinder153]
FEATURE [Sketcher::SketchObject] Sketch050  label="top017"
  FullyConstrained = true
  sketch-geometry (2):
    g0: Circle CenterX=0 CenterY=-150 CenterZ=0 NormalX=0 NormalY=0 NormalZ=1 AngleXU=0 Radius=98
    g1: Circle CenterX=0 CenterY=-150 CenterZ=0 NormalX=0 NormalY=0 NormalZ=1 AngleXU=0 Radius=76
  constraints (5):
    c: PointOnObject(g0,g-2)
    c: Diameter(g0) = 196
    c: DistanceY(g0) = -150
    c: Coincident(g1,g0)
    c: Radius(g1) = 76
FEATURE [Part::Extrusion] Extrude032  label="TupeConnectLevel006"
  Base = -> Sketch050
  Dir = (0,0,1)
  DirMode = 2
  FaceMakerClass = Part::FaceMakerBullseye
  LengthFwd = 5
  LengthRev = 0
  Placement = pos=(0,0,-65) rot=(0,0,1;0rad)
  Solid = true
  Symmetric = false
FEATURE [Sketcher::SketchObject] Sketch051
  FullyConstrained = true
  sketch-geometry (4):
    g0: Circle CenterX=0 CenterY=-68 CenterZ=0 NormalX=0 NormalY=0 NormalZ=1 AngleXU=0 Radius=2.8
    g1: Circle CenterX=82 CenterY=-150 CenterZ=0 NormalX=0 NormalY=0 NormalZ=1 AngleXU=0 Radius=2.8
    g2: Circle CenterX=0 CenterY=-232 CenterZ=0 NormalX=0 NormalY=0 NormalZ=1 AngleXU=0 Radius=2.8
    g3: Circle CenterX=-82 CenterY=-150 CenterZ=0 NormalX=0 NormalY=0 NormalZ=1 AngleXU=0 Radius=2.8
  constraints (12):
    c: PointOnObject(g0,g-2)
    c: DistanceY(g1) = -150
    c: DistanceY(g1,g3) = 0
    c: DistanceX(g2) = 0
    c: DistanceX(g1) = 82
    c: Equal(g1,g0)
    c: Equal(g1,g3)
    c: Equal(g1,g2)
    c: Diameter(g1) = 5.6
    c: DistanceX(g3) = -82
    c: DistanceY(g3,g0) = 82
    c: DistanceY(g2,g3) = 82
FEATURE [Part::Extrusion] Extrude033  label="m4HeatSetVerCuts005"
  Base = -> Sketch051
  Dir = (0,0,1)
  DirMode = 2
  FaceMakerClass = Part::FaceMakerBullseye
  LengthFwd = 20
  LengthRev = 0
  Placement = pos=(0,0,-193) rot=(0,0,1;0rad)
  Solid = true
  Symmetric = false
FEATURE [Part::FeaturePython] Tube007  # WARN: FeaturePython — macro-defined, semantics opaque (R4)
  AttacherType = Attacher::AttachEngine3D
  Height = 3
  InnerRadius = 95
  OuterRadius = 98
  Placement = pos=(0,-150,-188) rot=(0,0,1;0rad)
FEATURE [Part::FeaturePython] Tube008  # WARN: FeaturePython — macro-defined, semantics opaque (R4)
  AttacherType = Attacher::AttachEngine3D
  Height = 65
  InnerRadius = 94
  OuterRadius = 98
  Placement = pos=(0,-150,-125) rot=(0,0,1;0rad)
FEATURE [Part::MultiFuse] Fusion098  label="tube5to006"
  Placement = pos=(0,0,-125) rot=(0,0,1;0rad)
  Shapes = -> [Extrude032,Tube008]
FEATURE [Part::Cut] Cut050  label="tube4to007"
  Base = -> Fusion098
  Tool = -> Fusion099
FEATURE [Part::Cut] Cut051  label="tube4to5s002"
  Base = -> Cut050
  Tool = -> Extrude033
FEATURE [Part::Fillet] Fillet005  label="level5s003"
  Base = -> Cut051
  Edges = 3 edges r=3: [Edge3,Edge7,Edge32]
FEATURE [Part::Cut] Cut052  label="cutAddOn001"
  Base = -> Tube007
  Placement = pos=(0,0,125.25) rot=(0,0,1;0rad)
  Tool = -> Fillet005
FEATURE [Part::MultiFuse] Fusion100  label="level3to2"
  Shapes = -> [Cut046,Cut052]
FEATURE [Part::Fillet] Fillet006  label="level003to2s"
  Base = -> Fusion100
  Edges = 1 edges r=3: [Edge5]
FEATURE [Sketcher::SketchObject] Sketch054
  FullyConstrained = true
  Placement = pos=(0,0,0) rot=(1,0,0;1.5708rad)
  expr: Constraints[16] = -13
  sketch-geometry (8):
    g0: LineSegment StartX=-21 StartY=-250 StartZ=0 EndX=-13 EndY=-250 EndZ=0
    g1: LineSegment StartX=-13 StartY=-250 StartZ=0 EndX=-13 EndY=-276 EndZ=0
    g2: LineSegment StartX=-13 StartY=-276 StartZ=0 EndX=13 EndY=-276 EndZ=0
    g3: LineSegment StartX=13 StartY=-276 StartZ=0 EndX=13 EndY=-250 EndZ=0
    g4: LineSegment StartX=13 StartY=-250 StartZ=0 EndX=21 EndY=-250 EndZ=0
    g5: LineSegment StartX=21 StartY=-250 StartZ=0 EndX=21 EndY=-284 EndZ=0
    g6: LineSegment StartX=21 StartY=-284 StartZ=0 EndX=-21 EndY=-284 EndZ=0
    g7: LineSegment StartX=-21 StartY=-284 StartZ=0 EndX=-21 EndY=-250 EndZ=0
  constraints (24):
    c: Horizontal(g0)
    c: Vertical(g1)
    c: Coincident(g2,g1)
    c: Horizontal(g2)
    c: Vertical(g3)
    c: Coincident(g4,g3)
    c: Horizontal(g4)
    c: Coincident(g5,g4)
    c: Vertical(g5)
    c: Coincident(g6,g5)
    c: Horizontal(g6)
    c: Coincident(g7,g6)
    c: Coincident(g7,g0)
    c: Vertical(g7)
    c: Coincident(g0,g1)
    c: DistanceY(g0) = -250
    c: DistanceX(g0) = -13
    c: DistanceX(g3) = 13
    c: Coincident(g3,g2)
    c: DistanceY(g3,g0) = 0
    c: DistanceX(g0,g0) = 8
    c: DistanceX(g3,g4) = 8
    c: DistanceY(g5,g2) = 8
    c: DistanceY(g2,g3) = 26
FEATURE [Part::Extrusion] Extrude036  label="level5s012"
  Base = -> Sketch054
  Dir = (0,-1,2e-16)
  DirMode = 2
  FaceMakerClass = Part::FaceMakerBullseye
  LengthFwd = 100
  LengthRev = 0
  Placement = pos=(0,-70,0) rot=(0,0,1;0rad)
  Solid = true
  Symmetric = false
FEATURE [Mesh::Feature] tinker
  Placement = pos=(3,-245,-135) rot=(1,0,0;1.5708rad)
FEATURE [Sketcher::SketchObject] Sketch055
  FullyConstrained = false
  Placement = pos=(0,0,0) rot=(1,0,0;1.5708rad)
  sketch-geometry (884):
    g0: LineSegment StartX=35.7189 StartY=14.4677 StartZ=0 EndX=35.5415 EndY=14.2824 EndZ=0
    g1: LineSegment StartX=35.5415 StartY=14.2079 StartZ=0 EndX=35.4533 EndY=14.1342 EndZ=0
    g2: LineSegment StartX=35.4533 StartY=14.1342 StartZ=0 EndX=35.4583 EndY=14.0618 EndZ=0
    g3: LineSegment StartX=35.4583 StartY=14.0618 StartZ=0 EndX=35.3195 EndY=13.9216 EndZ=0
    g4: LineSegment StartX=35.3195 StartY=13.9216 StartZ=0 EndX=35.3195 EndY=13.853 EndZ=0
    g5: LineSegment StartX=35.3195 StartY=13.853 StartZ=0 EndX=35.248 EndY=13.7975 EndZ=0
    g6: LineSegment StartX=35.248 StartY=13.7975 StartZ=0 EndX=35.248 EndY=13.6573 EndZ=0
    g7: LineSegment StartX=35.248 StartY=13.6573 StartZ=0 EndX=35.1825 EndY=13.5912 EndZ=0
    g8: LineSegment StartX=35.1825 StartY=13.5912 StartZ=0 EndX=35.1825 EndY=13.2647 EndZ=0
    g9: LineSegment StartX=35.1825 StartY=13.2647 StartZ=0 EndX=35.0994 EndY=13.159 EndZ=0
    g10: LineSegment StartX=35.0994 StartY=13.159 StartZ=0 EndX=35.0994 EndY=13.0459 EndZ=0
    g11: LineSegment StartX=35.0994 StartY=13.0459 StartZ=0 EndX=35.0336 EndY=12.9565 EndZ=0
    g12: LineSegment StartX=35.0336 StartY=12.9565 StartZ=0 EndX=35.0336 EndY=12.3489 EndZ=0
    g13: LineSegment StartX=35.0336 StartY=12.3489 StartZ=0 EndX=35.1008 EndY=12.3489 EndZ=0
    g14: LineSegment StartX=35.1008 StartY=12.3489 StartZ=0 EndX=35.1008 EndY=12.2102 EndZ=0
    g15: LineSegment StartX=35.1008 StartY=12.2102 StartZ=0 EndX=35.1709 EndY=12.2072 EndZ=0
    g16: LineSegment StartX=35.1709 StartY=12.2072 StartZ=0 EndX=35.1709 EndY=11.9948 EndZ=0
    g17: LineSegment StartX=35.1709 StartY=11.9948 StartZ=0 EndX=35.2359 EndY=11.9948 EndZ=0
    g18: LineSegment StartX=35.2359 StartY=11.9948 StartZ=0 EndX=35.2359 EndY=11.9181 EndZ=0
    g19: LineSegment StartX=35.2359 StartY=11.9181 StartZ=0 EndX=35.3001 EndY=11.9181 EndZ=0
    g20: LineSegment StartX=35.3001 StartY=11.9181 StartZ=0 EndX=35.3001 EndY=11.8402 EndZ=0
    g21: LineSegment StartX=35.3001 StartY=11.8402 StartZ=0 EndX=35.3675 EndY=11.8402 EndZ=0
    g22: LineSegment StartX=35.3675 StartY=11.8402 StartZ=0 EndX=35.3675 EndY=11.2433 EndZ=0
    g23: LineSegment StartX=35.3675 StartY=11.2433 StartZ=0 EndX=35.435 EndY=11.2433 EndZ=0
    g24: LineSegment StartX=35.435 StartY=11.2433 StartZ=0 EndX=35.435 EndY=11.1727 EndZ=0
    g25: LineSegment StartX=35.435 StartY=11.1727 StartZ=0 EndX=35.5098 EndY=11.1727 EndZ=0
    g26: LineSegment StartX=35.5098 StartY=11.1727 StartZ=0 EndX=35.5098 EndY=11.1026 EndZ=0
    g27: LineSegment StartX=35.5098 StartY=11.1026 StartZ=0 EndX=35.6558 EndY=11.1026 EndZ=0
    g28: LineSegment StartX=35.6558 StartY=11.1026 StartZ=0 EndX=35.6558 EndY=11.0252 EndZ=0
    g29: LineSegment StartX=35.6558 StartY=11.0252 StartZ=0 EndX=35.7128 EndY=11.0252 EndZ=0
    g30: LineSegment StartX=35.7128 StartY=11.0252 StartZ=0 EndX=35.7128 EndY=10.7682 EndZ=0
    g31: LineSegment StartX=35.7128 StartY=10.7682 StartZ=0 EndX=35.7756 EndY=10.7681 EndZ=0
    g32: LineSegment StartX=35.7756 StartY=10.7681 StartZ=0 EndX=35.7756 EndY=10.5644 EndZ=0
    g33: LineSegment StartX=35.7756 StartY=10.5644 StartZ=0 EndX=35.846 EndY=10.5644 EndZ=0
    g34: LineSegment StartX=35.846 StartY=10.5644 StartZ=0 EndX=35.846 EndY=10.4767 EndZ=0
    g35: LineSegment StartX=35.846 StartY=10.4767 StartZ=0 EndX=35.988 EndY=10.4767 EndZ=0
    g36: LineSegment StartX=35.988 StartY=10.4767 StartZ=0 EndX=35.988 EndY=10.4228 EndZ=0
    g37: LineSegment StartX=35.988 StartY=10.4228 StartZ=0 EndX=36.1201 EndY=10.4228 EndZ=0
    g38: LineSegment StartX=36.1201 StartY=10.4228 StartZ=0 EndX=36.1201 EndY=10.2907 EndZ=0
    g39: LineSegment StartX=36.1201 StartY=10.2907 StartZ=0 EndX=36.1926 EndY=10.2907 EndZ=0
    g40: LineSegment StartX=36.1926 StartY=10.2907 StartZ=0 EndX=36.1926 EndY=10.1585 EndZ=0
    g41: LineSegment StartX=36.1926 StartY=10.1585 StartZ=0 EndX=36.2533 EndY=10.1585 EndZ=0
    g42: LineSegment StartX=36.2533 StartY=10.1585 StartZ=0 EndX=36.2533 EndY=10.0897 EndZ=0
    g43: LineSegment StartX=36.2533 StartY=10.0897 StartZ=0 EndX=36.3179 EndY=10.0897 EndZ=0
    g44: LineSegment StartX=36.3179 StartY=10.0897 StartZ=0 EndX=36.3179 EndY=9.8871 EndZ=0
    g45: LineSegment StartX=36.3179 StartY=9.8871 StartZ=0 EndX=36.3888 EndY=9.8871 EndZ=0
    g46: LineSegment StartX=36.3888 StartY=9.8871 StartZ=0 EndX=36.3888 EndY=9.73503 EndZ=0
    g47: LineSegment StartX=36.3888 StartY=9.73503 StartZ=0 EndX=36.4516 EndY=9.73503 EndZ=0
    g48: LineSegment StartX=36.4516 StartY=9.73503 StartZ=0 EndX=36.4516 EndY=9.65617 EndZ=0
    g49: LineSegment StartX=36.4516 StartY=9.65617 StartZ=0 EndX=36.6707 EndY=9.65617 EndZ=0
    g50: LineSegment StartX=36.6707 StartY=9.65617 StartZ=0 EndX=36.6707 EndY=9.58899 EndZ=0
    g51: LineSegment StartX=36.6707 StartY=9.58899 StartZ=0 EndX=36.7335 EndY=9.58899 EndZ=0
    g52: LineSegment StartX=36.7335 StartY=9.58899 StartZ=0 EndX=36.7335 EndY=9.51158 EndZ=0
    g53: LineSegment StartX=36.7335 StartY=9.51158 StartZ=0 EndX=36.7948 EndY=9.51158 EndZ=0
    g54: LineSegment StartX=36.7948 StartY=9.51158 StartZ=0 EndX=36.7948 EndY=9.40351 EndZ=0
    g55: LineSegment StartX=36.7948 StartY=9.40351 StartZ=0 EndX=36.8664 EndY=9.40351 EndZ=0
    g56: LineSegment StartX=36.8664 StartY=9.40351 StartZ=0 EndX=36.8664 EndY=9.2487 EndZ=0
    g57: LineSegment StartX=36.8664 StartY=9.2487 StartZ=0 EndX=36.9292 EndY=9.2487 EndZ=0
    g58: LineSegment StartX=36.9292 StartY=9.2487 StartZ=0 EndX=36.9292 EndY=9.18298 EndZ=0
    g59: LineSegment StartX=36.9292 StartY=9.18298 StartZ=0 EndX=37.0036 EndY=9.18298 EndZ=0
    g60: LineSegment StartX=37.0036 StartY=9.18298 StartZ=0 EndX=37.0036 EndY=9.12121 EndZ=0
    g61: LineSegment StartX=37.0036 StartY=9.12121 StartZ=0 EndX=37.066 EndY=9.12121 EndZ=0
    g62: LineSegment StartX=37.066 StartY=9.12121 StartZ=0 EndX=37.066 EndY=8.98122 EndZ=0
    g63: LineSegment StartX=37.066 StartY=8.98122 StartZ=0 EndX=37.1365 EndY=8.98122 EndZ=0
    g64: LineSegment StartX=37.1365 StartY=8.98122 StartZ=0 EndX=37.1365 EndY=8.85617 EndZ=0
    g65: LineSegment StartX=37.1365 StartY=8.85617 StartZ=0 EndX=37.2117 EndY=8.85617 EndZ=0
    g66: LineSegment StartX=37.2117 StartY=8.85617 StartZ=0 EndX=37.2117 EndY=8.77808 EndZ=0
    g67: LineSegment StartX=37.2117 StartY=8.77808 StartZ=0 EndX=37.276 EndY=8.7779 EndZ=0
    g68: LineSegment StartX=37.276 StartY=8.7779 StartZ=0 EndX=37.276 EndY=8.70839 EndZ=0
    g69: LineSegment StartX=37.276 StartY=8.70839 StartZ=0 EndX=37.3475 EndY=8.70839 EndZ=0
    g70: LineSegment StartX=37.3475 StartY=8.70839 StartZ=0 EndX=37.3475 EndY=8.58602 EndZ=0
    g71: LineSegment StartX=37.3475 StartY=8.58602 StartZ=0 EndX=37.4111 EndY=8.58602 EndZ=0
    g72: LineSegment StartX=37.4111 StartY=8.58602 StartZ=0 EndX=37.4111 EndY=8.50272 EndZ=0
    g73: LineSegment StartX=37.4111 StartY=8.50272 StartZ=0 EndX=37.4778 EndY=8.50272 EndZ=0
    g74: LineSegment StartX=37.4778 StartY=8.50272 StartZ=0 EndX=37.4778 EndY=8.37852 EndZ=0
    g75: LineSegment StartX=37.4778 StartY=8.37852 StartZ=0 EndX=37.55 EndY=8.37852 EndZ=0
    g76: LineSegment StartX=37.55 StartY=8.37852 StartZ=0 EndX=37.55 EndY=8.29594 EndZ=0
    g77: LineSegment StartX=37.55 StartY=8.29594 StartZ=0 EndX=37.6238 EndY=8.29594 EndZ=0
    g78: LineSegment StartX=37.6238 StartY=8.29594 StartZ=0 EndX=37.6238 EndY=8.20831 EndZ=0
    g79: LineSegment StartX=37.6238 StartY=8.20831 StartZ=0 EndX=37.6953 EndY=8.21123 EndZ=0
    g80: LineSegment StartX=37.6953 StartY=8.21123 StartZ=0 EndX=37.6953 EndY=8.14022 EndZ=0
    g81: LineSegment StartX=37.6953 StartY=8.14022 StartZ=0 EndX=37.7536 EndY=8.14414 EndZ=0
    g82: LineSegment StartX=37.7536 StartY=8.14414 StartZ=0 EndX=37.7574 EndY=8.06459 EndZ=0
    g83: LineSegment StartX=37.7574 StartY=8.06459 StartZ=0 EndX=37.8181 EndY=8.06459 EndZ=0
    g84: LineSegment StartX=37.8181 StartY=8.06459 StartZ=0 EndX=37.8216 EndY=7.98967 EndZ=0
    g85: LineSegment StartX=37.8216 StartY=7.98967 StartZ=0 EndX=38.1025 EndY=7.98967 EndZ=0
    g86: LineSegment StartX=38.1025 StartY=7.98967 StartZ=0 EndX=38.1917 EndY=8.08042 EndZ=0
    g87: LineSegment StartX=38.1917 StartY=8.08042 StartZ=0 EndX=38.2417 EndY=8.08577 EndZ=0
    g88: LineSegment StartX=38.2417 StartY=8.08577 StartZ=0 EndX=38.4557 EndY=8.32302 EndZ=0
    g89: LineSegment StartX=38.4557 StartY=8.32302 StartZ=0 EndX=38.5235 EndY=8.32302 EndZ=0
    g90: LineSegment StartX=38.5235 StartY=8.32302 StartZ=0 EndX=38.5887 EndY=8.40314 EndZ=0
    g91: LineSegment StartX=38.5887 StartY=8.40314 StartZ=0 EndX=38.6773 EndY=8.40314 EndZ=0
    g92: LineSegment StartX=38.6773 StartY=8.40314 StartZ=0 EndX=39.0643 EndY=8.80818 EndZ=0
    g93: LineSegment StartX=39.0643 StartY=8.80818 StartZ=0 EndX=39.152 EndY=8.80818 EndZ=0
    g94: LineSegment StartX=39.152 StartY=8.80818 StartZ=0 EndX=39.5355 EndY=9.19803 EndZ=0
    g95: LineSegment StartX=39.5355 StartY=9.19803 StartZ=0 EndX=39.6318 EndY=9.19803 EndZ=0
    g96: LineSegment StartX=39.6318 StartY=9.19803 StartZ=0 EndX=39.792 EndY=9.38195 EndZ=0
    g97: LineSegment StartX=39.792 StartY=9.38195 StartZ=0 EndX=39.7884 EndY=9.45608 EndZ=0
    g98: LineSegment StartX=39.7884 StartY=9.45608 StartZ=0 EndX=39.9772 EndY=9.63446 EndZ=0
    g99: LineSegment StartX=39.9772 StartY=9.63446 StartZ=0 EndX=39.9772 EndY=9.72533 EndZ=0
    g100: LineSegment StartX=39.9772 StartY=9.72533 StartZ=0 EndX=40.1697 EndY=9.91904 EndZ=0
    g101: LineSegment StartX=40.1697 StartY=9.91904 StartZ=0 EndX=40.1746 EndY=9.99558 EndZ=0
    g102: LineSegment StartX=40.1746 StartY=9.99558 StartZ=0 EndX=40.2388 EndY=10.0603 EndZ=0
    g103: LineSegment StartX=40.2388 StartY=10.0603 StartZ=0 EndX=40.2423 EndY=10.1261 EndZ=0
    g104: LineSegment StartX=40.2423 StartY=10.1261 StartZ=0 EndX=40.5948 EndY=10.4793 EndZ=0
    g105: LineSegment StartX=40.5948 StartY=10.4793 StartZ=0 EndX=40.5948 EndY=10.5499 EndZ=0
    g106: LineSegment StartX=40.5948 StartY=10.5499 StartZ=0 EndX=40.6701 EndY=10.618 EndZ=0
    g107: LineSegment StartX=40.6701 StartY=10.618 StartZ=0 EndX=40.6581 EndY=10.6527 EndZ=0
    g108: LineSegment StartX=40.6581 StartY=10.6527 StartZ=0 EndX=40.6988 EndY=10.6527 EndZ=0
    g109: LineSegment StartX=40.6988 StartY=10.6527 StartZ=0 EndX=40.9317 EndY=10.8877 EndZ=0
    g110: LineSegment StartX=40.9317 StartY=10.8877 StartZ=0 EndX=40.9317 EndY=10.9592 EndZ=0
    g111: LineSegment StartX=40.9317 StartY=10.9592 StartZ=0 EndX=41.0136 EndY=11.0405 EndZ=0
    g112: LineSegment StartX=41.0136 StartY=11.0405 StartZ=0 EndX=41.0068 EndY=11.1648 EndZ=0
    g113: LineSegment StartX=41.0068 StartY=11.1648 StartZ=0 EndX=41.0763 EndY=11.2275 EndZ=0
    g114: LineSegment StartX=41.0763 StartY=11.2275 StartZ=0 EndX=41.0723 EndY=11.2979 EndZ=0
    g115: LineSegment StartX=41.0723 StartY=11.2979 StartZ=0 EndX=41.15 EndY=11.3821 EndZ=0
    g116: LineSegment StartX=41.15 StartY=11.3821 StartZ=0 EndX=41.15 EndY=11.5724 EndZ=0
    g117: LineSegment StartX=41.15 StartY=11.5724 StartZ=0 EndX=41.2317 EndY=11.6351 EndZ=0
    g118: LineSegment StartX=41.2317 StartY=11.6351 StartZ=0 EndX=41.2155 EndY=11.7717 EndZ=0
    g119: LineSegment StartX=41.2155 StartY=11.7717 StartZ=0 EndX=41.2837 EndY=11.8432 EndZ=0
    g120: LineSegment StartX=41.2837 StartY=11.8432 StartZ=0 EndX=41.2786 EndY=11.8698 EndZ=0
    g121: LineSegment StartX=41.2786 StartY=11.8698 StartZ=0 EndX=41.3138 EndY=11.8698 EndZ=0
    g122: LineSegment StartX=41.3138 StartY=11.8698 StartZ=0 EndX=41.5455 EndY=12.1045 EndZ=0
    g123: LineSegment StartX=41.5455 StartY=12.1045 StartZ=0 EndX=41.5618 EndY=12.4305 EndZ=0
    g124: LineSegment StartX=41.5618 StartY=12.4305 StartZ=0 EndX=41.6277 EndY=12.505 EndZ=0
    g125: LineSegment StartX=41.6277 StartY=12.505 StartZ=0 EndX=41.6277 EndY=12.6108 EndZ=0
    g126: LineSegment StartX=41.6277 StartY=12.6108 StartZ=0 EndX=41.692 EndY=12.5393 EndZ=0
    g127: LineSegment StartX=41.692 StartY=12.5393 StartZ=0 EndX=41.7679 EndY=12.5393 EndZ=0
    g128: LineSegment StartX=41.7679 StartY=12.5393 StartZ=0 EndX=41.7679 EndY=12.4516 EndZ=0
    g129: LineSegment StartX=41.7679 StartY=12.4516 StartZ=0 EndX=41.8336 EndY=12.4546 EndZ=0
    g130: LineSegment StartX=41.8336 StartY=12.4546 StartZ=0 EndX=41.8336 EndY=12.3903 EndZ=0
    g131: LineSegment StartX=41.8336 StartY=12.3903 StartZ=0 EndX=41.8935 EndY=12.3903 EndZ=0
    g132: LineSegment StartX=41.8935 StartY=12.3903 StartZ=0 EndX=41.8935 EndY=12.3173 EndZ=0
    g133: LineSegment StartX=41.8935 StartY=12.3173 StartZ=0 EndX=41.9592 EndY=12.3217 EndZ=0
    g134: LineSegment StartX=41.9592 StartY=12.3217 StartZ=0 EndX=41.9651 EndY=12.2501 EndZ=0
    g135: LineSegment StartX=41.9651 StartY=12.2501 StartZ=0 EndX=42.0235 EndY=12.2559 EndZ=0
    g136: LineSegment StartX=42.0235 StartY=12.2559 StartZ=0 EndX=42.0264 EndY=12.1829 EndZ=0
    g137: LineSegment StartX=42.0264 StartY=12.1829 StartZ=0 EndX=42.1067 EndY=12.1888 EndZ=0
    g138: LineSegment StartX=42.1067 StartY=12.1888 StartZ=0 EndX=42.1067 EndY=12.1143 EndZ=0
    g139: LineSegment StartX=42.1067 StartY=12.1143 StartZ=0 EndX=42.2426 EndY=12.1216 EndZ=0
    g140: LineSegment StartX=42.2426 StartY=12.1216 StartZ=0 EndX=42.2426 EndY=12.0413 EndZ=0
    g141: LineSegment StartX=42.2426 StartY=12.0413 StartZ=0 EndX=42.4427 EndY=12.0413 EndZ=0
    g142: LineSegment StartX=42.4427 StartY=12.0413 StartZ=0 EndX=42.45 EndY=11.9566 EndZ=0
    g143: LineSegment StartX=42.45 StartY=11.9566 StartZ=0 EndX=42.523 EndY=11.9639 EndZ=0
    g144: LineSegment StartX=42.523 StartY=11.9639 StartZ=0 EndX=42.5274 EndY=11.8952 EndZ=0
    g145: LineSegment StartX=42.5274 StartY=11.8952 StartZ=0 EndX=42.5931 EndY=11.9011 EndZ=0
    g146: LineSegment StartX=42.5931 StartY=11.9011 StartZ=0 EndX=42.5931 EndY=11.847 EndZ=0
    g147: LineSegment StartX=42.5931 StartY=11.847 StartZ=0 EndX=42.6457 EndY=11.8499 EndZ=0
    g148: LineSegment StartX=42.6457 StartY=11.8499 StartZ=0 EndX=42.6457 EndY=11.7886 EndZ=0
    g149: LineSegment StartX=42.6457 StartY=11.7886 StartZ=0 EndX=42.7844 EndY=11.7886 EndZ=0
    g150: LineSegment StartX=42.7844 StartY=11.7886 StartZ=0 EndX=42.7844 EndY=11.7131 EndZ=0
    g151: LineSegment StartX=42.7844 StartY=11.7131 StartZ=0 EndX=43.0642 EndY=11.7131 EndZ=0
    g152: LineSegment StartX=43.0642 StartY=11.7131 StartZ=0 EndX=43.0642 EndY=11.6357 EndZ=0
    g153: LineSegment StartX=43.0642 StartY=11.6357 StartZ=0 EndX=43.1985 EndY=11.6357 EndZ=0
    g154: LineSegment StartX=43.1985 StartY=11.6357 StartZ=0 EndX=43.1985 EndY=11.5714 EndZ=0
    g155: LineSegment StartX=43.1985 StartY=11.5714 StartZ=0 EndX=43.2613 EndY=11.5714 EndZ=0
    g156: LineSegment StartX=43.2613 StartY=11.5714 StartZ=0 EndX=43.2613 EndY=11.5086 EndZ=0
    g157: LineSegment StartX=43.2613 StartY=11.5086 StartZ=0 EndX=43.3285 EndY=11.5086 EndZ=0
    g158: LineSegment StartX=43.3285 StartY=11.5086 StartZ=0 EndX=43.3285 EndY=11.4327 EndZ=0
    g159: LineSegment StartX=43.3285 StartY=11.4327 StartZ=0 EndX=43.3913 EndY=11.4371 EndZ=0
    g160: LineSegment StartX=43.3913 StartY=11.4371 StartZ=0 EndX=43.3932 EndY=11.3717 EndZ=0
    g161: LineSegment StartX=43.3932 StartY=11.3717 StartZ=0 EndX=43.7436 EndY=11.3717 EndZ=0
    g162: LineSegment StartX=43.7436 StartY=11.3717 StartZ=0 EndX=43.7436 EndY=11.3021 EndZ=0
    g163: LineSegment StartX=43.7436 StartY=11.3021 StartZ=0 EndX=43.8098 EndY=11.3021 EndZ=0
    g164: LineSegment StartX=43.8098 StartY=11.3021 StartZ=0 EndX=43.8134 EndY=11.2285 EndZ=0
    g165: LineSegment StartX=43.8134 StartY=11.2285 StartZ=0 EndX=44.0238 EndY=11.2285 EndZ=0
    g166: LineSegment StartX=44.0238 StartY=11.2285 StartZ=0 EndX=44.0238 EndY=11.1603 EndZ=0
    g167: LineSegment StartX=44.0238 StartY=11.1603 StartZ=0 EndX=44.1542 EndY=11.1603 EndZ=0
    g168: LineSegment StartX=44.1542 StartY=11.1603 StartZ=0 EndX=44.1506 EndY=11.0922 EndZ=0
    g169: LineSegment StartX=44.1506 StartY=11.0922 StartZ=0 EndX=44.2845 EndY=11.1005 EndZ=0
    g170: LineSegment StartX=44.2845 StartY=11.1005 StartZ=0 EndX=44.2845 EndY=11.0276 EndZ=0
    g171: LineSegment StartX=44.2845 StartY=11.0276 StartZ=0 EndX=44.3538 EndY=11.0312 EndZ=0
    g172: LineSegment StartX=44.3538 StartY=11.0312 StartZ=0 EndX=44.3538 EndY=10.9534 EndZ=0
    g173: LineSegment StartX=44.3538 StartY=10.9534 StartZ=0 EndX=44.4925 EndY=10.9534 EndZ=0
    g174: LineSegment StartX=44.4925 StartY=10.9534 StartZ=0 EndX=44.4925 EndY=10.9066 EndZ=0
    g175: LineSegment StartX=44.4925 StartY=10.9066 StartZ=0 EndX=44.8405 EndY=10.9066 EndZ=0
    g176: LineSegment StartX=44.8405 StartY=10.9066 StartZ=0 EndX=44.8405 EndY=10.8227 EndZ=0
    g177: LineSegment StartX=44.8405 StartY=10.8227 StartZ=0 EndX=44.9671 EndY=10.8245 EndZ=0
    g178: LineSegment StartX=44.9671 StartY=10.8245 StartZ=0 EndX=44.9671 EndY=10.7496 EndZ=0
    g179: LineSegment StartX=44.9671 StartY=10.7496 StartZ=0 EndX=45.2382 EndY=10.7496 EndZ=0
    g180: LineSegment StartX=45.2382 StartY=10.7496 StartZ=0 EndX=45.2382 EndY=10.6783 EndZ=0
    g181: LineSegment StartX=45.2382 StartY=10.6783 StartZ=0 EndX=45.438 EndY=10.6783 EndZ=0
    g182: LineSegment StartX=45.438 StartY=10.6783 StartZ=0 EndX=45.438 EndY=10.6176 EndZ=0
    g183: LineSegment StartX=45.438 StartY=10.6176 StartZ=0 EndX=45.8572 EndY=10.6176 EndZ=0
    g184: LineSegment StartX=45.8572 StartY=10.6176 StartZ=0 EndX=45.8572 EndY=10.548 EndZ=0
    g185: LineSegment StartX=45.8572 StartY=10.548 StartZ=0 EndX=46.2711 EndY=10.548 EndZ=0
    g186: LineSegment StartX=46.2711 StartY=10.548 StartZ=0 EndX=46.5712 EndY=10.876 EndZ=0
    g187: LineSegment StartX=46.5712 StartY=10.876 StartZ=0 EndX=46.568 EndY=10.9537 EndZ=0
    g188: LineSegment StartX=46.568 StartY=10.9537 StartZ=0 EndX=46.6513 EndY=11.0387 EndZ=0
    g189: LineSegment StartX=46.6513 StartY=11.0387 StartZ=0 EndX=46.6513 EndY=11.2162 EndZ=0
    g190: LineSegment StartX=46.6513 StartY=11.2162 StartZ=0 EndX=46.7535 EndY=11.317 EndZ=0
    g191: LineSegment StartX=46.7535 StartY=11.317 StartZ=0 EndX=46.7462 EndY=11.4353 EndZ=0
    g192: LineSegment StartX=46.7462 StartY=11.4353 StartZ=0 EndX=46.8178 EndY=11.5141 EndZ=0
    g193: LineSegment StartX=46.8178 StartY=11.5141 StartZ=0 EndX=46.8081 EndY=11.636 EndZ=0
    g194: LineSegment StartX=46.8081 StartY=11.636 StartZ=0 EndX=46.8919 EndY=11.7287 EndZ=0
    g195: LineSegment StartX=46.8919 StartY=11.7287 StartZ=0 EndX=46.8919 EndY=11.9142 EndZ=0
    g196: LineSegment StartX=46.8919 StartY=11.9142 StartZ=0 EndX=46.9704 EndY=12.0106 EndZ=0
    g197: LineSegment StartX=46.9704 StartY=12.0106 StartZ=0 EndX=46.9704 EndY=13.0147 EndZ=0
    g198: LineSegment StartX=46.9704 StartY=13.0147 StartZ=0 EndX=47.1435 EndY=13.1957 EndZ=0
    g199: LineSegment StartX=47.1435 StartY=13.1957 StartZ=0 EndX=47.1435 EndY=13.5812 EndZ=0
    g200: LineSegment StartX=47.1435 StartY=13.5812 StartZ=0 EndX=47.0232 EndY=13.5812 EndZ=0
    g201: LineSegment StartX=47.0232 StartY=13.5812 StartZ=0 EndX=47.0232 EndY=13.968 EndZ=0
    g202: LineSegment StartX=47.0232 StartY=13.968 StartZ=0 EndX=46.9387 EndY=13.981 EndZ=0
    g203: LineSegment StartX=46.9387 StartY=13.981 StartZ=0 EndX=46.9387 EndY=14.1923 EndZ=0
    g204: LineSegment StartX=46.9387 StartY=14.1923 StartZ=0 EndX=46.8607 EndY=14.189 EndZ=0
    g205: LineSegment StartX=46.8607 StartY=14.189 StartZ=0 EndX=46.8607 EndY=14.2768 EndZ=0
    g206: LineSegment StartX=46.8607 StartY=14.2768 StartZ=0 EndX=46.9745 EndY=14.4003 EndZ=0
    g207: LineSegment StartX=46.9745 StartY=14.4003 StartZ=0 EndX=46.9842 EndY=14.6473 EndZ=0
    g208: LineSegment StartX=46.9842 StartY=14.6473 StartZ=0 EndX=46.8672 EndY=14.6603 EndZ=0
    g209: LineSegment StartX=46.8672 StartY=14.6603 StartZ=0 EndX=46.8672 EndY=14.8066 EndZ=0
    g210: LineSegment StartX=46.8672 StartY=14.8066 StartZ=0 EndX=46.799 EndY=14.8131 EndZ=0
    g211: LineSegment StartX=46.799 StartY=14.8131 StartZ=0 EndX=46.7957 EndY=14.8846 EndZ=0
    g212: LineSegment StartX=46.7957 StartY=14.8846 StartZ=0 EndX=46.7372 EndY=14.8911 EndZ=0
    g213: LineSegment StartX=46.7372 StartY=14.8911 StartZ=0 EndX=46.7502 EndY=15.0699 EndZ=0
    g214: LineSegment StartX=46.7502 StartY=15.0699 StartZ=0 EndX=46.6592 EndY=15.0764 EndZ=0
    g215: LineSegment StartX=46.6592 StartY=15.0764 StartZ=0 EndX=46.6592 EndY=15.2096 EndZ=0
    g216: LineSegment StartX=46.6592 StartY=15.2096 StartZ=0 EndX=46.7535 EndY=15.2811 EndZ=0
    g217: LineSegment StartX=46.7535 StartY=15.2811 StartZ=0 EndX=47.5498 EndY=15.2811 EndZ=0
    g218: LineSegment StartX=47.5498 StartY=15.2811 StartZ=0 EndX=47.5498 EndY=15.2015 EndZ=0
    g219: LineSegment StartX=47.5498 StartY=15.2015 StartZ=0 EndX=48.1326 EndY=15.2015 EndZ=0
    g220: LineSegment StartX=48.1326 StartY=15.2015 StartZ=0 EndX=48.1915 EndY=15.2887 EndZ=0
    g221: LineSegment StartX=48.1915 StartY=15.2887 StartZ=0 EndX=48.2811 EndY=15.2887 EndZ=0
    g222: LineSegment StartX=48.2811 StartY=15.2887 StartZ=0 EndX=48.4046 EndY=15.4194 EndZ=0
    g223: LineSegment StartX=48.4046 StartY=15.4194 StartZ=0 EndX=48.6512 EndY=15.4194 EndZ=0
    g224: LineSegment StartX=48.6512 StartY=15.4194 StartZ=0 EndX=48.6512 EndY=15.3322 EndZ=0
    g225: LineSegment StartX=48.6512 StartY=15.3322 StartZ=0 EndX=48.9084 EndY=15.3322 EndZ=0
    g226: LineSegment StartX=48.9084 StartY=15.3322 StartZ=0 EndX=48.9084 EndY=15.2647 EndZ=0
    g227: LineSegment StartX=48.9084 StartY=15.2647 StartZ=0 EndX=49.1131 EndY=15.2647 EndZ=0
    g228: LineSegment StartX=49.1131 StartY=15.2647 StartZ=0 EndX=49.1131 EndY=15.171 EndZ=0
    g229: LineSegment StartX=49.1131 StartY=15.171 StartZ=0 EndX=49.344 EndY=15.171 EndZ=0
    g230: LineSegment StartX=49.344 StartY=15.171 StartZ=0 EndX=49.4317 EndY=15.2779 EndZ=0
    g231: LineSegment StartX=49.4317 StartY=15.2779 StartZ=0 EndX=49.513 EndY=15.2714 EndZ=0
    g232: LineSegment StartX=49.513 StartY=15.2714 StartZ=0 EndX=49.6365 EndY=15.4177 EndZ=0
    g233: LineSegment StartX=49.6365 StartY=15.4177 StartZ=0 EndX=51.1609 EndY=15.4177 EndZ=0
    g234: LineSegment StartX=51.1609 StartY=15.4177 StartZ=0 EndX=51.2713 EndY=15.4747 EndZ=0
    g235: LineSegment StartX=51.2713 StartY=15.4747 StartZ=0 EndX=51.8707 EndY=15.4747 EndZ=0
    g236: LineSegment StartX=51.8707 StartY=15.4747 StartZ=0 EndX=51.9501 EndY=15.5501 EndZ=0
    g237: LineSegment StartX=51.9501 StartY=15.5501 StartZ=0 EndX=52.0613 EndY=15.5501 EndZ=0
    g238: LineSegment StartX=52.0613 StartY=15.5501 StartZ=0 EndX=52.1566 EndY=15.6335 EndZ=0
    g239: LineSegment StartX=52.1566 StartY=15.6335 StartZ=0 EndX=53.0776 EndY=15.6335 EndZ=0
    g240: LineSegment StartX=53.0776 StartY=15.6335 StartZ=0 EndX=53.2557 EndY=15.8082 EndZ=0
    g241: LineSegment StartX=53.2557 StartY=15.8082 StartZ=0 EndX=53.2557 EndY=16.103 EndZ=0
    g242: LineSegment StartX=53.2557 StartY=16.103 StartZ=0 EndX=53.1958 EndY=16.103 EndZ=0
    g243: LineSegment StartX=53.1958 StartY=16.103 StartZ=0 EndX=53.1958 EndY=16.3046 EndZ=0
    g244: LineSegment StartX=53.1958 StartY=16.3046 StartZ=0 EndX=53.1301 EndY=16.3017 EndZ=0
    g245: LineSegment StartX=53.1301 StartY=16.3017 StartZ=0 EndX=53.1301 EndY=16.4404 EndZ=0
    g246: LineSegment StartX=53.1301 StartY=16.4404 StartZ=0 EndX=53.0594 EndY=16.4404 EndZ=0
    g247: LineSegment StartX=53.0594 StartY=16.4404 StartZ=0 EndX=53.0558 EndY=16.5171 EndZ=0
    g248: LineSegment StartX=53.0558 StartY=16.5171 StartZ=0 EndX=52.9773 EndY=16.5171 EndZ=0
    g249: LineSegment StartX=52.9773 StartY=16.5171 StartZ=0 EndX=52.9773 EndY=16.6455 EndZ=0
    g250: LineSegment StartX=52.9773 StartY=16.6455 StartZ=0 EndX=52.9219 EndY=16.6452 EndZ=0
    g251: LineSegment StartX=52.9219 StartY=16.6452 StartZ=0 EndX=52.9219 EndY=16.7146 EndZ=0
    g252: LineSegment StartX=52.9219 StartY=16.7146 StartZ=0 EndX=52.8549 EndY=16.7146 EndZ=0
    g253: LineSegment StartX=52.8549 StartY=16.7146 StartZ=0 EndX=52.8535 EndY=16.7863 EndZ=0
    g254: LineSegment StartX=52.8535 StartY=16.7863 StartZ=0 EndX=52.7868 EndY=16.7863 EndZ=0
    g255: LineSegment StartX=52.7868 StartY=16.7863 StartZ=0 EndX=52.7868 EndY=16.9211 EndZ=0
    g256: LineSegment StartX=52.7868 StartY=16.9211 StartZ=0 EndX=52.715 EndY=16.9211 EndZ=0
    g257: LineSegment StartX=52.715 StartY=16.9211 StartZ=0 EndX=52.715 EndY=16.98 EndZ=0
    g258: LineSegment StartX=52.715 StartY=16.98 StartZ=0 EndX=52.6457 EndY=16.98 EndZ=0
    g259: LineSegment StartX=52.6457 StartY=16.98 StartZ=0 EndX=52.6457 EndY=17.0366 EndZ=0
    g260: LineSegment StartX=52.6457 StartY=17.0366 StartZ=0 EndX=52.5763 EndY=17.0366 EndZ=0
    g261: LineSegment StartX=52.5763 StartY=17.0366 StartZ=0 EndX=52.5763 EndY=17.128 EndZ=0
    g262: LineSegment StartX=52.5763 StartY=17.128 StartZ=0 EndX=52.5147 EndY=17.128 EndZ=0
    g263: LineSegment StartX=52.5147 StartY=17.128 StartZ=0 EndX=52.5147 EndY=17.2695 EndZ=0
    g264: LineSegment StartX=52.5147 StartY=17.2695 StartZ=0 EndX=52.4502 EndY=17.2647 EndZ=0
    g265: LineSegment StartX=52.4502 StartY=17.2647 StartZ=0 EndX=52.4454 EndY=17.336 EndZ=0
    g266: LineSegment StartX=52.4454 StartY=17.336 StartZ=0 EndX=52.3797 EndY=17.3384 EndZ=0
    g267: LineSegment StartX=52.3797 StartY=17.3384 StartZ=0 EndX=52.3829 EndY=17.4058 EndZ=0
    g268: LineSegment StartX=52.3829 StartY=17.4058 StartZ=0 EndX=52.318 EndY=17.4026 EndZ=0
    g269: LineSegment StartX=52.318 StartY=17.4026 StartZ=0 EndX=52.318 EndY=17.4715 EndZ=0
    g270: LineSegment StartX=52.318 StartY=17.4715 StartZ=0 EndX=52.2451 EndY=17.4715 EndZ=0
    g271: LineSegment StartX=52.2451 StartY=17.4715 StartZ=0 EndX=52.2451 EndY=17.5364 EndZ=0
    g272: LineSegment StartX=52.2451 StartY=17.5364 StartZ=0 EndX=52.1833 EndY=17.5388 EndZ=0
    g273: LineSegment StartX=52.1833 StartY=17.5388 StartZ=0 EndX=52.1833 EndY=17.6077 EndZ=0
    g274: LineSegment StartX=52.1833 StartY=17.6077 StartZ=0 EndX=52.1144 EndY=17.6077 EndZ=0
    g275: LineSegment StartX=52.1144 StartY=17.6077 StartZ=0 EndX=52.1144 EndY=17.6741 EndZ=0
    g276: LineSegment StartX=52.1144 StartY=17.6741 StartZ=0 EndX=52.0495 EndY=17.6741 EndZ=0
    g277: LineSegment StartX=52.0495 StartY=17.6741 StartZ=0 EndX=52.0495 EndY=17.7495 EndZ=0
    g278: LineSegment StartX=52.0495 StartY=17.7495 StartZ=0 EndX=51.9017 EndY=17.7495 EndZ=0
    g279: LineSegment StartX=51.9017 StartY=17.7495 StartZ=0 EndX=51.9017 EndY=17.8092 EndZ=0
    g280: LineSegment StartX=51.9017 StartY=17.8092 StartZ=0 EndX=51.8351 EndY=17.8092 EndZ=0
    g281: LineSegment StartX=51.8351 StartY=17.8092 StartZ=0 EndX=51.8351 EndY=17.8911 EndZ=0
    g282: LineSegment StartX=51.8351 StartY=17.8911 StartZ=0 EndX=51.7639 EndY=17.8911 EndZ=0
    g283: LineSegment StartX=51.7639 StartY=17.8911 StartZ=0 EndX=51.7639 EndY=17.9626 EndZ=0
    g284: LineSegment StartX=51.7639 StartY=17.9626 StartZ=0 EndX=51.6325 EndY=17.9626 EndZ=0
    g285: LineSegment StartX=51.6325 StartY=17.9626 StartZ=0 EndX=51.6325 EndY=18.0284 EndZ=0
    g286: LineSegment StartX=51.6325 StartY=18.0284 StartZ=0 EndX=51.485 EndY=18.0284 EndZ=0
    g287: LineSegment StartX=51.485 StartY=18.0284 StartZ=0 EndX=51.485 EndY=18.0711 EndZ=0
    g288: LineSegment StartX=51.485 StartY=18.0711 StartZ=0 EndX=51.4163 EndY=18.0711 EndZ=0
    g289: LineSegment StartX=51.4163 StartY=18.0711 StartZ=0 EndX=51.4163 EndY=18.1587 EndZ=0
    g290: LineSegment StartX=51.4163 StartY=18.1587 StartZ=0 EndX=51.2878 EndY=18.1587 EndZ=0
    g291: LineSegment StartX=51.2878 StartY=18.1587 StartZ=0 EndX=51.2878 EndY=18.2275 EndZ=0
    g292: LineSegment StartX=51.2878 StartY=18.2275 StartZ=0 EndX=51.2232 EndY=18.2275 EndZ=0
    g293: LineSegment StartX=51.2232 StartY=18.2275 StartZ=0 EndX=51.2267 EndY=18.2921 EndZ=0
    g294: LineSegment StartX=51.2267 StartY=18.2921 StartZ=0 EndX=51.1526 EndY=18.2921 EndZ=0
    g295: LineSegment StartX=51.1526 StartY=18.2921 StartZ=0 EndX=51.1526 EndY=18.3662 EndZ=0
    g296: LineSegment StartX=51.1526 StartY=18.3662 StartZ=0 EndX=51.0845 EndY=18.3602 EndZ=0
    g297: LineSegment StartX=51.0845 StartY=18.3602 StartZ=0 EndX=51.0845 EndY=18.4424 EndZ=0
    g298: LineSegment StartX=51.0845 StartY=18.4424 StartZ=0 EndX=51.0222 EndY=18.4424 EndZ=0
    g299: LineSegment StartX=51.0222 StartY=18.4424 StartZ=0 EndX=51.0222 EndY=18.5138 EndZ=0
    g300: LineSegment StartX=51.0222 StartY=18.5138 StartZ=0 EndX=50.8169 EndY=18.5138 EndZ=0
    g301: LineSegment StartX=50.8169 StartY=18.5138 StartZ=0 EndX=50.7878 EndY=18.6026 EndZ=0
    g302: LineSegment StartX=50.7878 StartY=18.6026 StartZ=0 EndX=50.7494 EndY=18.6113 EndZ=0
    g303: LineSegment StartX=50.7494 StartY=18.6113 StartZ=0 EndX=50.7397 EndY=18.6731 EndZ=0
    g304: LineSegment StartX=50.7397 StartY=18.6731 StartZ=0 EndX=50.5414 EndY=18.6536 EndZ=0
    g305: LineSegment StartX=50.5414 StartY=18.6536 StartZ=0 EndX=50.5381 EndY=18.7381 EndZ=0
    g306: LineSegment StartX=50.5381 StartY=18.7381 StartZ=0 EndX=50.4114 EndY=18.7218 EndZ=0
    g307: LineSegment StartX=50.4114 StartY=18.7218 StartZ=0 EndX=50.3951 EndY=18.7934 EndZ=0
    g308: LineSegment StartX=50.3951 StartY=18.7934 StartZ=0 EndX=50.3334 EndY=18.7934 EndZ=0
    g309: LineSegment StartX=50.3334 StartY=18.7934 StartZ=0 EndX=50.3366 EndY=18.8389 EndZ=0
    g310: LineSegment StartX=50.3366 StartY=18.8389 StartZ=0 EndX=50.2066 EndY=18.8389 EndZ=0
    g311: LineSegment StartX=50.2066 StartY=18.8389 StartZ=0 EndX=50.2099 EndY=18.9201 EndZ=0
    g312: LineSegment StartX=50.2099 StartY=18.9201 StartZ=0 EndX=50.1254 EndY=18.9266 EndZ=0
    g313: LineSegment StartX=50.1254 StartY=18.9266 StartZ=0 EndX=50.1156 EndY=19.0046 EndZ=0
    g314: LineSegment StartX=50.1156 StartY=19.0046 StartZ=0 EndX=49.9986 EndY=18.9949 EndZ=0
    g315: LineSegment StartX=49.9986 StartY=18.9949 StartZ=0 EndX=49.9921 EndY=19.0859 EndZ=0
    g316: LineSegment StartX=49.9921 StartY=19.0859 StartZ=0 EndX=49.9368 EndY=19.0501 EndZ=0
    g317: LineSegment StartX=49.9368 StartY=19.0501 StartZ=0 EndX=49.9206 EndY=19.1509 EndZ=0
    g318: LineSegment StartX=49.9206 StartY=19.1509 StartZ=0 EndX=49.7971 EndY=19.1281 EndZ=0
    g319: LineSegment StartX=49.7971 StartY=19.1281 StartZ=0 EndX=49.8068 EndY=19.2029 EndZ=0
    g320: LineSegment StartX=49.8068 StartY=19.2029 StartZ=0 EndX=49.7288 EndY=19.1899 EndZ=0
    g321: LineSegment StartX=49.7288 StartY=19.1899 StartZ=0 EndX=49.7191 EndY=19.2582 EndZ=0
    g322: LineSegment StartX=49.7191 StartY=19.2582 StartZ=0 EndX=49.6606 EndY=19.2647 EndZ=0
    g323: LineSegment StartX=49.6606 StartY=19.2647 StartZ=0 EndX=49.6541 EndY=19.3329 EndZ=0
    g324: LineSegment StartX=49.6541 StartY=19.3329 StartZ=0 EndX=49.6021 EndY=19.3329 EndZ=0
    g325: LineSegment StartX=49.6021 StartY=19.3329 StartZ=0 EndX=49.5988 EndY=19.4077 EndZ=0
    g326: LineSegment StartX=49.5988 StartY=19.4077 StartZ=0 EndX=49.4623 EndY=19.3947 EndZ=0
    g327: LineSegment StartX=49.4623 StartY=19.3947 StartZ=0 EndX=49.4623 EndY=19.4727 EndZ=0
    g328: LineSegment StartX=49.4623 StartY=19.4727 StartZ=0 EndX=49.2543 EndY=19.4532 EndZ=0
    g329: LineSegment StartX=49.2543 StartY=19.4532 StartZ=0 EndX=49.2543 EndY=19.5279 EndZ=0
    g330: LineSegment StartX=49.2543 StartY=19.5279 StartZ=0 EndX=49.199 EndY=19.5279 EndZ=0
    g331: LineSegment StartX=49.199 StartY=19.5279 StartZ=0 EndX=49.199 EndY=19.6189 EndZ=0
    g332: LineSegment StartX=49.199 StartY=19.6189 StartZ=0 EndX=49.0658 EndY=19.6059 EndZ=0
    g333: LineSegment StartX=49.0658 StartY=19.6059 StartZ=0 EndX=49.0495 EndY=19.6612 EndZ=0
    g334: LineSegment StartX=49.0495 StartY=19.6612 StartZ=0 EndX=48.991 EndY=19.6547 EndZ=0
    g335: LineSegment StartX=48.991 StartY=19.6547 StartZ=0 EndX=48.9845 EndY=19.7359 EndZ=0
    g336: LineSegment StartX=48.9845 StartY=19.7359 StartZ=0 EndX=48.8577 EndY=19.7262 EndZ=0
    g337: LineSegment StartX=48.8577 StartY=19.7262 StartZ=0 EndX=48.8577 EndY=19.8149 EndZ=0
    g338: LineSegment StartX=48.8577 StartY=19.8149 StartZ=0 EndX=48.7743 EndY=19.8069 EndZ=0
    g339: LineSegment StartX=48.7743 StartY=19.8069 StartZ=0 EndX=48.7743 EndY=19.8894 EndZ=0
    g340: LineSegment StartX=48.7743 StartY=19.8894 StartZ=0 EndX=48.5854 EndY=19.8894 EndZ=0
    g341: LineSegment StartX=48.5854 StartY=19.8894 StartZ=0 EndX=48.5854 EndY=19.9533 EndZ=0
    g342: LineSegment StartX=48.5854 StartY=19.9533 StartZ=0 EndX=48.4417 EndY=19.9533 EndZ=0
    g343: LineSegment StartX=48.4417 StartY=19.9533 StartZ=0 EndX=48.4417 EndY=20.0118 EndZ=0
    g344: LineSegment StartX=48.4417 StartY=20.0118 StartZ=0 EndX=48.3751 EndY=20.0118 EndZ=0
    g345: LineSegment StartX=48.3751 StartY=20.0118 StartZ=0 EndX=48.3751 EndY=20.089 EndZ=0
    g346: LineSegment StartX=48.3751 StartY=20.089 StartZ=0 EndX=48.3033 EndY=20.089 EndZ=0
    g347: LineSegment StartX=48.3033 StartY=20.089 StartZ=0 EndX=48.3033 EndY=20.1524 EndZ=0
    g348: LineSegment StartX=48.3033 StartY=20.1524 StartZ=0 EndX=48.0916 EndY=20.1524 EndZ=0
    g349: LineSegment StartX=48.0916 StartY=20.1524 StartZ=0 EndX=48.0916 EndY=20.2331 EndZ=0
    g350: LineSegment StartX=48.0916 StartY=20.2331 StartZ=0 EndX=47.8912 EndY=20.2331 EndZ=0
    g351: LineSegment StartX=47.8912 StartY=20.2331 StartZ=0 EndX=47.8912 EndY=20.2962 EndZ=0
    g352: LineSegment StartX=47.8912 StartY=20.2962 StartZ=0 EndX=47.6864 EndY=20.2962 EndZ=0
    g353: LineSegment StartX=47.6864 StartY=20.2962 StartZ=0 EndX=47.6864 EndY=20.3681 EndZ=0
    g354: LineSegment StartX=47.6864 StartY=20.3681 StartZ=0 EndX=47.2898 EndY=20.3681 EndZ=0
    g355: LineSegment StartX=47.2898 StartY=20.3681 StartZ=0 EndX=47.2898 EndY=20.4313 EndZ=0
    g356: LineSegment StartX=47.2898 StartY=20.4313 StartZ=0 EndX=47.0094 EndY=20.4313 EndZ=0
    g357: LineSegment StartX=47.0094 StartY=20.4313 StartZ=0 EndX=47.0094 EndY=20.5033 EndZ=0
    g358: LineSegment StartX=47.0094 StartY=20.5033 StartZ=0 EndX=46.7265 EndY=20.5033 EndZ=0
    g359: LineSegment StartX=46.7265 StartY=20.5033 StartZ=0 EndX=46.7265 EndY=20.5623 EndZ=0
    g360: LineSegment StartX=46.7265 StartY=20.5623 StartZ=0 EndX=46.3195 EndY=20.5623 EndZ=0
    g361: LineSegment StartX=46.3195 StartY=20.5623 StartZ=0 EndX=46.2304 EndY=20.478 EndZ=0
    g362: LineSegment StartX=46.2304 StartY=20.478 StartZ=0 EndX=45.8403 EndY=20.478 EndZ=0
    g363: LineSegment StartX=45.8403 StartY=20.478 StartZ=0 EndX=45.7581 EndY=20.3987 EndZ=0
    g364: LineSegment StartX=45.7581 StartY=20.3987 StartZ=0 EndX=45.6847 EndY=20.3987 EndZ=0
    g365: LineSegment StartX=45.6847 StartY=20.3987 StartZ=0 EndX=45.6847 EndY=20.4757 EndZ=0
    g366: LineSegment StartX=45.6847 StartY=20.4757 StartZ=0 EndX=45.2353 EndY=20.4757 EndZ=0
    g367: LineSegment StartX=45.2353 StartY=20.4757 StartZ=0 EndX=45.1511 EndY=20.3964 EndZ=0
    g368: LineSegment StartX=45.1511 StartY=20.3964 StartZ=0 EndX=45.039 EndY=20.3905 EndZ=0
    g369: LineSegment StartX=45.1271 StartY=20.498 StartZ=0 EndX=45.039 EndY=20.3905 EndZ=0
    g370: LineSegment StartX=45.1271 StartY=20.498 StartZ=0 EndX=45.1672 EndY=20.498 EndZ=0
    g371: LineSegment StartX=45.1672 StartY=20.498 StartZ=0 EndX=45.2586 EndY=20.5605 EndZ=0
    g372: LineSegment StartX=45.2586 StartY=20.5605 StartZ=0 EndX=45.3242 EndY=20.5605 EndZ=0
    g373: LineSegment StartX=45.3242 StartY=20.5605 StartZ=0 EndX=45.4009 EndY=20.6461 EndZ=0
    g374: LineSegment StartX=45.4009 StartY=20.6461 StartZ=0 EndX=45.5221 EndY=20.6461 EndZ=0
    g375: LineSegment StartX=45.5221 StartY=20.6461 StartZ=0 EndX=45.6149 EndY=20.705 EndZ=0
    g376: LineSegment StartX=45.6149 StartY=20.705 StartZ=0 EndX=45.8042 EndY=20.705 EndZ=0
    g377: LineSegment StartX=45.8042 StartY=20.705 StartZ=0 EndX=45.9915 EndY=20.8898 EndZ=0
    g378: LineSegment StartX=45.9915 StartY=20.8898 StartZ=0 EndX=45.9915 EndY=20.959 EndZ=0
    g379: LineSegment StartX=45.9915 StartY=20.959 StartZ=0 EndX=46.0581 EndY=21.0202 EndZ=0
    g380: LineSegment StartX=46.0581 StartY=21.0202 StartZ=0 EndX=46.0527 EndY=21.0894 EndZ=0
    g381: LineSegment StartX=46.0527 StartY=21.0894 StartZ=0 EndX=46.2124 EndY=21.2464 EndZ=0
    g382: LineSegment StartX=46.2124 StartY=21.2464 StartZ=0 EndX=46.2763 EndY=21.2277 EndZ=0
    g383: LineSegment StartX=46.2763 StartY=21.2277 StartZ=0 EndX=46.5051 EndY=21.4486 EndZ=0
    g384: LineSegment StartX=46.5051 StartY=21.4486 StartZ=0 EndX=46.585 EndY=21.4539 EndZ=0
    g385: LineSegment StartX=46.585 StartY=21.4539 StartZ=0 EndX=46.6994 EndY=21.603 EndZ=0
    g386: LineSegment StartX=46.6994 StartY=21.603 StartZ=0 EndX=46.8245 EndY=21.5843 EndZ=0
    g387: LineSegment StartX=46.8245 StartY=21.5843 StartZ=0 EndX=46.9016 EndY=21.6855 EndZ=0
    g388: LineSegment StartX=46.9016 StartY=21.6855 StartZ=0 EndX=46.9655 EndY=21.6562 EndZ=0
    g389: LineSegment StartX=46.9655 StartY=21.6562 StartZ=0 EndX=47.205 EndY=21.8754 EndZ=0
    g390: LineSegment StartX=47.205 StartY=21.8754 StartZ=0 EndX=47.205 EndY=22.0711 EndZ=0
    g391: LineSegment StartX=47.205 StartY=22.0711 StartZ=0 EndX=47.2634 EndY=22.0711 EndZ=0
    g392: LineSegment StartX=47.2634 StartY=22.0711 StartZ=0 EndX=47.6208 EndY=22.4458 EndZ=0
    g393: LineSegment StartX=47.6208 StartY=22.4458 StartZ=0 EndX=47.6208 EndY=22.5177 EndZ=0
    g394: LineSegment StartX=47.6208 StartY=22.5177 StartZ=0 EndX=47.8212 EndY=22.7182 EndZ=0
    g395: LineSegment StartX=47.8212 StartY=22.7182 StartZ=0 EndX=47.8343 EndY=22.7944 EndZ=0
    g396: LineSegment StartX=47.8343 StartY=22.7944 StartZ=0 EndX=48.0478 EndY=22.997 EndZ=0
    g397: LineSegment StartX=48.0478 StartY=22.997 StartZ=0 EndX=48.0478 EndY=23.1365 EndZ=0
    g398: LineSegment StartX=48.0478 StartY=23.1365 StartZ=0 EndX=48.0998 EndY=23.2173 EndZ=0
    g399: LineSegment StartX=48.0998 StartY=23.2173 StartZ=0 EndX=48.0998 EndY=23.2802 EndZ=0
    ... +484 more geometry lines
  constraints (1492):
    c: Coincident(g3,g2)
    c: Vertical(g4)
    c: Vertical(g6)
    c: Coincident(g8,g7)
    c: Vertical(g8)
    c: Coincident(g8,g9)
    c: Coincident(g9,g10)
    c: Vertical(g10)
    c: Coincident(g10,g11)
    c: Coincident(g11,g12)
    c: Vertical(g12)
    c: Coincident(g13,g12)
    c: Horizontal(g13)
    c: Vertical(g14)
    c: Coincident(g16,g15)
    c: Vertical(g16)
    c: Horizontal(g17)
    c: Coincident(g18,g17)
    c: Vertical(g18)
    c: Horizontal(g19)
    c: Coincident(g20,g19)
    c: Vertical(g20)
    c: Horizontal(g21)
    c: Vertical(g22)
    c: Horizontal(g23)
    c: Coincident(g24,g23)
    c: Vertical(g24)
    c: Horizontal(g25)
    c: Coincident(g27,g26)
    c: Horizontal(g27)
    c: Vertical(g28)
    c: Coincident(g30,g29)
    c: Vertical(g30)
    c: Coincident(g31,g32)
    c: Vertical(g32)
    c: Coincident(g32,g33)
    c: Horizontal(g33)
    c: Coincident(g34,g33)
    c: Vertical(g34)
    c: Coincident(g35,g34)
    c: Horizontal(g35)
    c: Coincident(g36,g35)
    c: Vertical(g36)
    c: Coincident(g37,g36)
    c: Horizontal(g37)
    c: Vertical(g38)
    c: Horizontal(g39)
    c: Vertical(g40)
    c: Horizontal(g41)
    c: Coincident(g42,g41)
    c: Vertical(g42)
    c: Horizontal(g43)
    c: Coincident(g44,g43)
    c: Vertical(g44)
    c: Coincident(g45,g44)
    c: Horizontal(g45)
    c: Coincident(g46,g45)
    c: Vertical(g46)
    c: Coincident(g47,g46)
    c: Horizontal(g47)
    c: Coincident(g48,g47)
    c: Vertical(g48)
    c: Horizontal(g49)
    c: Vertical(g50)
    c: Coincident(g51,g50)
    c: Horizontal(g51)
    c: Vertical(g52)
    c: Coincident(g53,g52)
    c: Horizontal(g53)
    c: Coincident(g54,g53)
    c: Vertical(g54)
    c: Coincident(g55,g54)
    c: Horizontal(g55)
    c: Coincident(g56,g55)
    c: Vertical(g56)
    c: Coincident(g57,g56)
    c: Horizontal(g57)
    c: Coincident(g58,g57)
    c: Vertical(g58)
    c: Coincident(g60,g59)
    c: Vertical(g60)
    c: Coincident(g61,g60)
    c: Horizontal(g61)
    c: Vertical(g62)
    c: Horizontal(g63)
    c: Coincident(g64,g63)
    c: Vertical(g64)
    c: Horizontal(g65)
    c: Vertical(g66)
    c: Coincident(g68,g67)
    c: Vertical(g68)
    c: Horizontal(g69)
    c: Coincident(g70,g69)
    c: Vertical(g70)
    c: Horizontal(g71)
    c: Coincident(g72,g71)
    c: Vertical(g72)
    c: Horizontal(g73)
    c: Coincident(g74,g73)
    c: Vertical(g74)
    c: Horizontal(g75)
    c: Coincident(g76,g75)
    c: Vertical(g76)
    c: Horizontal(g77)
    c: Vertical(g78)
    c: Coincident(g79,g78)
    c: Coincident(g80,g79)
    c: Vertical(g80)
    c: Coincident(g81,g80)
    c: Coincident(g82,g81)
    c: Horizontal(g83)
    c: Coincident(g85,g84)
    c: Horizontal(g85)
    c: Coincident(g86,g85)
    c: Coincident(g89,g88)
    c: Horizontal(g89)
    c: Coincident(g90,g89)
    c: Coincident(g91,g90)
    c: Horizontal(g91)
    c: Coincident(g92,g91)
    c: Horizontal(g93)
    c: Coincident(g94,g93)
    c: Horizontal(g95)
    c: Coincident(g96,g95)
    c: Coincident(g97,g98)
    c: Coincident(g98,g99)
    c: Vertical(g99)
    c: Coincident(g99,g100)
    c: Coincident(g100,g101)
    c: Coincident(g101,g102)
    c: Coincident(g102,g103)
    c: Coincident(g103,g104)
    c: Coincident(g104,g105)
    c: Vertical(g105)
    c: Coincident(g105,g106)
    c: Coincident(g106,g107)
    c: Coincident(g107,g108)
    c: Horizontal(g108)
    c: Coincident(g108,g109)
    c: Coincident(g109,g110)
    c: Vertical(g110)
    c: Coincident(g110,g111)
    c: Coincident(g111,g112)
    c: Coincident(g112,g113)
    c: Coincident(g113,g114)
    c: Coincident(g114,g115)
    c: Coincident(g115,g116)
    c: Vertical(g116)
    c: Coincident(g116,g117)
    c: Coincident(g117,g118)
    c: Coincident(g118,g119)
    c: Coincident(g119,g120)
    c: Coincident(g120,g121)
    c: Horizontal(g121)
    c: Coincident(g121,g122)
    c: Coincident(g122,g123)
    c: Coincident(g123,g124)
    c: Coincident(g124,g125)
    c: Vertical(g125)
    c: Coincident(g125,g126)
    c: Coincident(g126,g127)
    c: Horizontal(g127)
    c: Coincident(g127,g128)
    c: Vertical(g128)
    c: Coincident(g128,g129)
    c: Coincident(g129,g130)
    c: Vertical(g130)
    c: Coincident(g130,g131)
    c: Horizontal(g131)
    c: Coincident(g131,g132)
    c: Vertical(g132)
    c: Coincident(g132,g133)
    c: Coincident(g133,g134)
    c: Coincident(g134,g135)
    c: Coincident(g135,g136)
    c: Coincident(g136,g137)
    c: Coincident(g137,g138)
    c: Vertical(g138)
    c: Coincident(g138,g139)
    c: Coincident(g139,g140)
    c: Vertical(g140)
    c: Coincident(g140,g141)
    c: Horizontal(g141)
    c: Coincident(g141,g142)
    c: Coincident(g142,g143)
    c: Coincident(g143,g144)
    c: Coincident(g144,g145)
    c: Coincident(g145,g146)
    c: Vertical(g146)
    c: Coincident(g146,g147)
    c: Coincident(g147,g148)
    c: Vertical(g148)
    c: Coincident(g148,g149)
    c: Horizontal(g149)
    c: Coincident(g149,g150)
    c: Vertical(g150)
    c: Coincident(g150,g151)
    c: Horizontal(g151)
    c: Coincident(g151,g152)
    c: Vertical(g152)
    c: Coincident(g152,g153)
    c: Horizontal(g153)
    c: Coincident(g153,g154)
    c: Vertical(g154)
    c: Coincident(g154,g155)
    c: Horizontal(g155)
    c: Coincident(g155,g156)
    c: Vertical(g156)
    c: Coincident(g156,g157)
    c: Horizontal(g157)
    c: Coincident(g157,g158)
    c: Vertical(g158)
    c: Coincident(g158,g159)
    c: Coincident(g159,g160)
    c: Coincident(g160,g161)
    c: Horizontal(g161)
    c: Coincident(g161,g162)
    c: Vertical(g162)
    c: Coincident(g162,g163)
    c: Horizontal(g163)
    c: Coincident(g163,g164)
    c: Coincident(g164,g165)
    c: Horizontal(g165)
    c: Coincident(g165,g166)
    c: Vertical(g166)
    c: Coincident(g166,g167)
    c: Horizontal(g167)
    c: Coincident(g167,g168)
    c: Coincident(g168,g169)
    c: Coincident(g169,g170)
    c: Vertical(g170)
    c: Coincident(g170,g171)
    c: Coincident(g171,g172)
    c: Vertical(g172)
    c: Coincident(g172,g173)
    c: Horizontal(g173)
    c: Coincident(g173,g174)
    c: Vertical(g174)
    c: Coincident(g174,g175)
    c: Horizontal(g175)
    c: Coincident(g175,g176)
    c: Vertical(g176)
    c: Coincident(g176,g177)
    c: Coincident(g177,g178)
    c: Vertical(g178)
    c: Coincident(g178,g179)
    c: Horizontal(g179)
    c: Coincident(g179,g180)
    c: Vertical(g180)
    c: Coincident(g180,g181)
    c: Horizontal(g181)
    c: Coincident(g181,g182)
    c: Vertical(g182)
    c: Coincident(g182,g183)
    c: Horizontal(g183)
    c: Coincident(g183,g184)
    c: Vertical(g184)
    c: Coincident(g184,g185)
    c: Horizontal(g185)
    c: Coincident(g185,g186)
    c: Coincident(g186,g187)
    c: Coincident(g187,g188)
    c: Coincident(g188,g189)
    c: Vertical(g189)
    c: Coincident(g189,g190)
    c: Coincident(g190,g191)
    c: Coincident(g191,g192)
    c: Coincident(g192,g193)
    c: Coincident(g193,g194)
    c: Coincident(g194,g195)
    c: Vertical(g195)
    c: Coincident(g195,g196)
    c: Coincident(g196,g197)
    c: Vertical(g197)
    c: Coincident(g197,g198)
    c: Coincident(g198,g199)
    c: Vertical(g199)
    c: Coincident(g199,g200)
    c: Coincident(g200,g201)
    c: Vertical(g201)
    c: Coincident(g201,g202)
    c: Coincident(g202,g203)
    c: Vertical(g203)
    c: Coincident(g203,g204)
    c: Coincident(g204,g205)
    c: Vertical(g205)
    c: Coincident(g205,g206)
    c: Coincident(g206,g207)
    c: Coincident(g207,g208)
    c: Coincident(g208,g209)
    c: Vertical(g209)
    c: Coincident(g209,g210)
    c: Coincident(g210,g211)
    c: Coincident(g211,g212)
    c: Coincident(g212,g213)
    c: Coincident(g213,g214)
    c: Coincident(g214,g215)
    c: Vertical(g215)
    c: Coincident(g215,g216)
    c: Coincident(g216,g217)
    c: Horizontal(g217)
    c: Coincident(g217,g218)
    c: Vertical(g218)
    c: Coincident(g218,g219)
    c: Horizontal(g219)
    c: Coincident(g219,g220)
    c: Coincident(g220,g221)
    c: Horizontal(g221)
    c: Coincident(g221,g222)
    c: Coincident(g222,g223)
    c: Horizontal(g223)
    c: Coincident(g223,g224)
    c: Coincident(g224,g225)
    c: Horizontal(g225)
    c: Coincident(g225,g226)
    c: Vertical(g226)
    c: Coincident(g226,g227)
    c: Horizontal(g227)
    c: Coincident(g227,g228)
    c: Vertical(g228)
    c: Coincident(g228,g229)
    c: Horizontal(g229)
    c: Coincident(g229,g230)
    c: Coincident(g230,g231)
    c: Coincident(g231,g232)
    c: Coincident(g232,g233)
    c: Horizontal(g233)
    c: Coincident(g233,g234)
    c: Coincident(g234,g235)
    c: Horizontal(g235)
    c: Coincident(g235,g236)
    c: Coincident(g236,g237)
    c: Horizontal(g237)
    c: Coincident(g237,g238)
    c: Coincident(g238,g239)
    c: Horizontal(g239)
    c: Coincident(g239,g240)
    c: Coincident(g240,g241)
    c: Vertical(g241)
    c: Coincident(g241,g242)
    c: Horizontal(g242)
    c: Coincident(g242,g243)
    c: Vertical(g243)
    c: Coincident(g243,g244)
    c: Coincident(g244,g245)
    c: Vertical(g245)
    c: Coincident(g245,g246)
    c: Horizontal(g246)
    c: Coincident(g246,g247)
    c: Coincident(g247,g248)
    c: Horizontal(g248)
    c: Coincident(g248,g249)
    c: Vertical(g249)
    c: Coincident(g249,g250)
    c: Coincident(g250,g251)
    c: Coincident(g251,g252)
    c: Horizontal(g252)
    c: Coincident(g252,g253)
    c: Coincident(g253,g254)
    c: Horizontal(g254)
    c: Coincident(g254,g255)
    c: Vertical(g255)
    c: Coincident(g255,g256)
    c: Coincident(g256,g257)
    c: Coincident(g257,g258)
    c: Coincident(g258,g259)
    c: Coincident(g259,g260)
    c: Coincident(g260,g261)
    c: Vertical(g257)
    c: Horizontal(g258)
    c: Horizontal(g256)
    c: Vertical(g259)
    c: Horizontal(g260)
    c: Vertical(g261)
    c: Coincident(g261,g262)
    c: Horizontal(g262)
    c: Coincident(g262,g263)
    c: Vertical(g263)
    c: Coincident(g263,g264)
    c: Coincident(g264,g265)
    c: Coincident(g265,g266)
    c: Coincident(g266,g267)
    c: Coincident(g267,g268)
    c: Coincident(g268,g269)
    c: Vertical(g269)
    c: Coincident(g269,g270)
    c: Horizontal(g270)
    c: Coincident(g270,g271)
    c: Vertical(g271)
    c: Coincident(g271,g272)
    c: Coincident(g272,g273)
    c: Vertical(g273)
    c: Coincident(g273,g274)
    c: Horizontal(g274)
    c: Coincident(g274,g275)
    c: Vertical(g275)
    c: Coincident(g275,g276)
    c: Horizontal(g276)
    c: Coincident(g276,g277)
    c: Coincident(g277,g278)
    c: Horizontal(g278)
    c: Coincident(g278,g279)
    c: Coincident(g279,g280)
    c: Coincident(g280,g281)
    c: Vertical(g281)
    c: Coincident(g281,g282)
    c: Coincident(g282,g283)
    c: Coincident(g283,g284)
    c: Horizontal(g284)
    c: Coincident(g284,g285)
    c: Coincident(g285,g286)
    c: Coincident(g286,g287)
    c: Coincident(g287,g288)
    c: Coincident(g288,g289)
    c: Coincident(g289,g290)
    c: Coincident(g290,g291)
    c: Vertical(g291)
    c: Coincident(g291,g292)
    c: Horizontal(g292)
    c: Coincident(g292,g293)
    c: Coincident(g293,g294)
    c: Horizontal(g294)
    c: Coincident(g294,g295)
    c: Vertical(g295)
    c: Coincident(g295,g296)
    c: Coincident(g296,g297)
    c: Vertical(g297)
    c: Coincident(g297,g298)
    c: Horizontal(g298)
    c: Coincident(g298,g299)
    c: Vertical(g299)
    c: Coincident(g299,g300)
    c: Horizontal(g300)
    c: Coincident(g300,g301)
    c: Coincident(g301,g302)
    c: Coincident(g302,g303)
    c: Coincident(g303,g304)
    c: Coincident(g304,g305)
    c: Coincident(g305,g306)
    c: Coincident(g306,g307)
    c: Coincident(g307,g308)
    c: Horizontal(g308)
    c: Coincident(g308,g309)
    c: Coincident(g309,g310)
    c: Horizontal(g310)
    c: Coincident(g310,g311)
    c: Coincident(g311,g312)
    c: Coincident(g312,g313)
    c: Coincident(g313,g314)
    c: Coincident(g314,g315)
    c: Coincident(g315,g316)
    c: Coincident(g316,g317)
    c: Coincident(g317,g318)
    c: Coincident(g318,g319)
    c: Coincident(g319,g320)
    c: Coincident(g320,g321)
    c: Coincident(g321,g322)
    c: Coincident(g322,g323)
    c: Coincident(g323,g324)
    c: Horizontal(g324)
    c: Coincident(g324,g325)
    c: Coincident(g325,g326)
    c: Coincident(g326,g327)
    c: Vertical(g327)
    c: Coincident(g327,g328)
    c: Coincident(g328,g329)
    c: Coincident(g329,g330)
    c: Coincident(g330,g331)
    c: Vertical(g331)
    c: Coincident(g331,g332)
    c: Coincident(g332,g333)
    c: Coincident(g333,g334)
    c: Coincident(g334,g335)
    c: Coincident(g335,g336)
    c: Coincident(g336,g337)
    c: Vertical(g337)
    c: Coincident(g337,g338)
    c: Coincident(g338,g339)
    c: Coincident(g339,g340)
    c: Coincident(g340,g341)
    c: Coincident(g341,g342)
    c: Coincident(g342,g343)
    c: Coincident(g343,g344)
    c: Coincident(g344,g345)
    c: Coincident(g345,g346)
    c: Coincident(g346,g347)
    c: Coincident(g347,g348)
    c: Coincident(g348,g349)
    c: Coincident(g349,g350)
    c: Coincident(g350,g351)
    c: Coincident(g351,g352)
    c: Coincident(g352,g353)
    c: Coincident(g353,g354)
    c: Coincident(g354,g355)
    c: Coincident(g355,g356)
    c: Coincident(g356,g357)
    c: Vertical(g357)
    c: Coincident(g357,g358)
    c: Horizontal(g358)
    c: Coincident(g358,g359)
    c: Coincident(g359,g360)
    c: Coincident(g360,g361)
    c: Coincident(g361,g362)
    c: Horizontal(g362)
    c: Coincident(g362,g363)
    c: Coincident(g363,g364)
    c: Coincident(g364,g365)
    c: Coincident(g365,g366)
    c: Coincident(g366,g367)
    c: Horizontal(g290)
    c: Vertical(g287)
    c: Vertical(g285)
    c: Vertical(g283)
    c: Vertical(g279)
    c: Vertical(g277)
    c: Horizontal(g286)
    c: Horizontal(g288)
    c: Vertical(g289)
    c: Horizontal(g280)
    c: Horizontal(g282)
    c: Vertical(g329)
    c: Horizontal(g330)
    c: Horizontal(g340)
    c: Horizontal(g342)
    c: Horizontal(g344)
    c: Horizontal(g346)
    c: Horizontal(g348)
    c: Horizontal(g350)
    c: Vertical(g339)
    c: Vertical(g341)
    c: Vertical(g343)
    c: Vertical(g345)
    c: Vertical(g347)
    c: Vertical(g349)
    c: Vertical(g351)
    c: Vertical(g353)
    c: Vertical(g355)
    c: Horizontal(g352)
    c: Horizontal(g354)
    c: Horizontal(g356)
    c: Vertical(g359)
    c: Horizontal(g360)
    c: Horizontal(g364)
    c: Vertical(g365)
    c: Horizontal(g366)
    c: Coincident(g368,g367)
    c: Coincident(g369,g368)
    c: Coincident(g369,g370)
    c: Coincident(g370,g371)
    c: Coincident(g371,g372)
    c: Horizontal(g372)
    c: Coincident(g372,g373)
    c: Coincident(g373,g374)
    c: Coincident(g374,g375)
    c: Coincident(g375,g376)
    c: Coincident(g376,g377)
    c: Coincident(g377,g378)
    c: Vertical(g378)
    c: Coincident(g378,g379)
    c: Coincident(g379,g380)
    c: Coincident(g380,g381)
    c: Coincident(g381,g382)
    c: Coincident(g382,g383)
    c: Coincident(g383,g384)
    c: Coincident(g384,g385)
    c: Coincident(g385,g386)
    c: Coincident(g386,g387)
    c: Coincident(g387,g388)
    c: Coincident(g388,g389)
    c: Coincident(g389,g390)
    c: Coincident(g390,g391)
    c: Horizontal(g391)
    c: Coincident(g391,g392)
    c: Coincident(g392,g393)
    c: Coincident(g393,g394)
    c: Coincident(g394,g395)
    c: Coincident(g395,g396)
    c: Coincident(g396,g397)
    c: Coincident(g397,g398)
    c: Coincident(g398,g399)
    c: Coincident(g399,g400)
    c: Coincident(g400,g401)
    c: Coincident(g401,g402)
    c: Coincident(g402,g403)
    c: Coincident(g403,g404)
    c: Coincident(g404,g405)
    c: Coincident(g405,g406)
    c: Coincident(g406,g407)
    c: Coincident(g407,g408)
    c: Coincident(g408,g409)
    c: Vertical(g409)
    c: Coincident(g409,g410)
    c: Coincident(g410,g411)
    c: Vertical(g411)
    c: Coincident(g411,g412)
    c: Horizontal(g412)
    c: Coincident(g412,g413)
    c: Coincident(g413,g414)
    c: Horizontal(g414)
    c: Coincident(g414,g415)
    c: Coincident(g415,g416)
    c: Coincident(g416,g417)
    c: Coincident(g417,g418)
    c: Coincident(g418,g419)
    c: Coincident(g419,g420)
    c: Coincident(g420,g421)
    c: Coincident(g421,g422)
    c: Coincident(g422,g423)
    c: Coincident(g423,g424)
    c: Coincident(g424,g425)
    c: Coincident(g425,g426)
    c: Horizontal(g426)
    c: Coincident(g426,g427)
    c: Coincident(g427,g428)
    c: Horizontal(g428)
    c: Coincident(g428,g429)
    c: Coincident(g429,g430)
    c: Coincident(g430,g431)
    c: Coincident(g431,g432)
    c: Horizontal(g432)
    c: Coincident(g432,g433)
    c: Coincident(g433,g434)
    c: Horizontal(g434)
    c: Coincident(g434,g435)
    c: Coincident(g435,g436)
    c: Coincident(g436,g437)
    c: Coincident(g437,g438)
    c: Coincident(g439,g440)
    c: Coincident(g440,g441)
    c: Coincident(g441,g442)
    c: Coincident(g442,g443)
    c: Coincident(g443,g444)
    c: Coincident(g444,g445)
    c: Coincident(g445,g446)
    c: Coincident(g446,g447)
    c: Coincident(g447,g448)
    c: Coincident(g448,g449)
    c: Coincident(g449,g450)
    c: Coincident(g450,g451)
    c: Coincident(g451,g452)
    c: Coincident(g452,g453)
    c: Coincident(g453,g454)
    c: Coincident(g454,g455)
    c: Coincident(g455,g456)
    c: Coincident(g456,g457)
    c: Coincident(g457,g458)
    c: Coincident(g458,g459)
    c: Coincident(g459,g460)
    c: Coincident(g460,g461)
    c: Coincident(g461,g462)
    c: Coincident(g462,g463)
    c: Coincident(g463,g464)
    c: Coincident(g464,g465)
    c: Coincident(g465,g466)
    c: Coincident(g466,g467)
    c: Coincident(g467,g468)
    c: Coincident(g468,g469)
    c: Coincident(g469,g470)
    c: Coincident(g470,g471)
    c: Coincident(g471,g472)
    c: Horizontal(g472)
    c: Coincident(g472,g473)
    c: Coincident(g473,g474)
    c: Coincident(g474,g475)
    c: Coincident(g475,g476)
    c: Coincident(g476,g477)
    c: Coincident(g477,g478)
    c: Coincident(g478,g479)
    c: Coincident(g479,g480)
    c: Coincident(g480,g481)
    c: Coincident(g481,g482)
    c: Coincident(g482,g483)
    c: Coincident(g483,g484)
    c: Coincident(g484,g485)
    c: Coincident(g485,g486)
    c: Coincident(g486,g487)
    c: Coincident(g487,g488)
    c: Vertical(g488)
    c: Coincident(g488,g489)
    c: Coincident(g489,g490)
    c: Vertical(g490)
    c: Coincident(g490,g491)
    c: Coincident(g491,g492)
    c: Coincident(g492,g493)
    c: Coincident(g493,g494)
    c: Coincident(g494,g495)
    c: Coincident(g495,g496)
    c: Coincident(g496,g497)
    c: Coincident(g497,g498)
    c: Coincident(g498,g499)
    c: Coincident(g499,g500)
    c: Coincident(g500,g501)
    c: Coincident(g501,g502)
    c: Coincident(g502,g503)
    c: Coincident(g503,g504)
    c: Horizontal(g370)
    c: Horizontal(g374)
    c: Horizontal(g376)
    c: Vertical(g390)
    c: Vertical(g397)
    c: Vertical(g399)
    c: Vertical(g401)
    c: Vertical(g403)
    c: Vertical(g407)
    c: Horizontal(g410)
    c: Vertical(g413)
    c: Vertical(g415)
    c: Horizontal(g416)
    c: Vertical(g417)
    c: Horizontal(g418)
    c: Vertical(g419)
    c: Vertical(g421)
    c: Vertical(g423)
    c: Vertical(g425)
    c: Vertical(g427)
    c: Vertical(g429)
    c: Horizontal(g420)
    c: Horizontal(g422)
    c: Horizontal(g424)
    c: Vertical(g431)
    c: Vertical(g433)
    c: Vertical(g435)
    c: Horizontal(g436)
    c: Horizontal(g438)
    c: Vertical(g437)
    c: Coincident(g439,g505)
    c: Horizontal(g505)
    c: Coincident(g505,g506)
    c: Coincident(g506,g438)
    c: Vertical(g506)
    c: Horizontal(g464)
    c: Horizontal(g462)
    c: Horizontal(g460)
    c: Horizontal(g458)
    c: Horizontal(g456)
    c: Horizontal(g454)
    c: Horizontal(g452)
    c: Horizontal(g450)
    c: Horizontal(g448)
    c: Horizontal(g446)
    c: Horizontal(g444)
    c: Horizontal(g442)
    c: Horizontal(g440)
    c: Horizontal(g468)
    c: Horizontal(g470)
    c: Horizontal(g474)
    c: Horizontal(g476)
    c: Horizontal(g478)
    c: Vertical(g465)
    c: Horizontal(g466)
    c: Vertical(g475)
    c: Vertical(g477)
    c: Horizontal(g491)
    c: Horizontal(g496)
    c: Horizontal(g494)
    c: Horizontal(g498)
    c: Vertical(g499)
    c: Vertical(g497)
    c: Vertical(g495)
    c: Vertical(g493)
    c: Horizontal(g500)
    c: Horizontal(g502)
    c: Horizontal(g504)
    c: Vertical(g501)
    c: Vertical(g503)
    c: Coincident(g504,g507)
    c: Vertical(g507)
    c: Coincident(g507,g508)
    c: Coincident(g508,g509)
    c: Coincident(g509,g510)
    c: Coincident(g510,g511)
    c: Vertical(g511)
    c: Coincident(g511,g512)
    c: Horizontal(g512)
    c: Coincident(g512,g513)
    c: Vertical(g513)
    c: Coincident(g513,g514)
    c: Coincident(g514,g515)
    c: Vertical(g515)
    c: Coincident(g515,g516)
    c: Horizontal(g516)
    c: Coincident(g516,g517)
    c: Coincident(g517,g518)
    c: Horizontal(g518)
    c: Coincident(g518,g519)
    c: Coincident(g519,g520)
    c: Coincident(g521,g522)
    c: Coincident(g522,g523)
    c: Coincident(g523,g524)
    c: Coincident(g524,g525)
    c: Coincident(g525,g526)
    c: Coincident(g526,g527)
    c: Coincident(g527,g528)
    c: Coincident(g528,g529)
    c: Coincident(g529,g530)
    c: Coincident(g531,g532)
    c: Coincident(g532,g533)
    c: Coincident(g533,g534)
    c: Coincident(g534,g535)
    c: Coincident(g535,g536)
    c: Coincident(g536,g537)
    c: Coincident(g537,g538)
    c: Coincident(g538,g539)
    c: Coincident(g539,g540)
    c: Coincident(g540,g541)
    c: Coincident(g541,g542)
    c: Coincident(g542,g543)
    c: Coincident(g543,g544)
    c: Coincident(g544,g545)
    c: Coincident(g545,g546)
    c: Coincident(g546,g547)
    c: Coincident(g547,g548)
    c: Coincident(g548,g549)
    c: Coincident(g549,g550)
    c: Horizontal(g550)
    c: Coincident(g550,g551)
    c: Coincident(g551,g552)
    c: Coincident(g552,g553)
    c: Coincident(g553,g554)
    c: Horizontal(g554)
    c: Coincident(g554,g555)
    c: Coincident(g555,g556)
    c: Coincident(g556,g557)
    c: Coincident(g557,g558)
    c: Horizontal(g558)
    c: Coincident(g558,g559)
    c: Coincident(g559,g560)
    c: Coincident(g560,g561)
    c: Coincident(g562,g563)
    c: Horizontal(g563)
    c: Coincident(g563,g564)
    c: Coincident(g564,g565)
    c: Coincident(g565,g566)
    c: Coincident(g566,g567)
    c: Horizontal(g567)
    c: Coincident(g567,g568)
    c: Coincident(g568,g569)
    c: Coincident(g569,g570)
    c: Coincident(g570,g571)
    c: Coincident(g571,g572)
    c: Coincident(g572,g573)
    c: Coincident(g573,g574)
    c: Coincident(g574,g575)
    c: Coincident(g575,g576)
    c: Coincident(g576,g577)
    c: Coincident(g577,g578)
    c: Coincident(g578,g579)
    c: Coincident(g579,g580)
    c: Vertical(g580)
    c: Coincident(g580,g581)
    c: Coincident(g581,g582)
    c: Coincident(g582,g583)
    c: Coincident(g583,g584)
    c: Coincident(g584,g585)
    c: Horizontal(g585)
    c: Coincident(g585,g586)
    c: Coincident(g586,g587)
    c: Coincident(g587,g588)
    c: Vertical(g588)
    c: Coincident(g588,g589)
    c: Coincident(g589,g590)
    c: Coincident(g590,g591)
    c: Coincident(g592,g593)
    c: Horizontal(g593)
    c: Coincident(g593,g594)
    c: Coincident(g594,g595)
    c: Coincident(g595,g596)
    c: Vertical(g596)
    c: Coincident(g596,g597)
    c: Horizontal(g597)
    c: Coincident(g597,g598)
    c: Vertical(g598)
    c: Coincident(g598,g599)
    c: Coincident(g599,g600)
    c: Coincident(g600,g601)
    c: Horizontal(g601)
    c: Coincident(g601,g602)
    c: Coincident(g602,g603)
    c: Coincident(g603,g604)
    c: Coincident(g604,g605)
    c: Coincident(g605,g606)
    c: Coincident(g606,g607)
    c: Coincident(g607,g608)
    c: Coincident(g608,g609)
    c: Horizontal(g609)
    c: Coincident(g609,g610)
    c: Coincident(g610,g611)
    c: Coincident(g611,g612)
    c: Coincident(g612,g613)
    c: Vertical(g613)
    c: Coincident(g613,g614)
    c: Coincident(g614,g615)
    c: Vertical(g615)
    c: Coincident(g615,g616)
    c: Coincident(g616,g617)
    c: Vertical(g617)
    c: Coincident(g618,g619)
    c: Vertical(g619)
    c: Coincident(g619,g620)
    c: Coincident(g620,g621)
    c: Coincident(g621,g622)
    c: Coincident(g622,g623)
    c: Coincident(g623,g624)
    c: Coincident(g624,g625)
    c: Coincident(g625,g626)
    c: Coincident(g626,g627)
    c: Vertical(g627)
    c: Coincident(g627,g628)
    c: Coincident(g628,g629)
    c: Coincident(g629,g630)
    c: Coincident(g630,g631)
    c: Coincident(g631,g632)
    c: Coincident(g632,g633)
    c: Vertical(g633)
    c: Coincident(g633,g634)
    c: Coincident(g634,g635)
    c: Vertical(g635)
    c: Coincident(g635,g636)
    c: Coincident(g636,g637)
    c: Coincident(g637,g638)
    c: Coincident(g638,g639)
    c: Coincident(g639,g640)
    c: Horizontal(g640)
    c: Coincident(g640,g641)
    c: Coincident(g641,g642)
    c: Vertical(g642)
    c: Coincident(g642,g643)
    c: Coincident(g643,g644)
    c: Vertical(g644)
    c: Coincident(g644,g645)
    c: Coincident(g645,g646)
    c: Coincident(g646,g647)
    c: Coincident(g647,g648)
    c: Coincident(g648,g649)
    c: Coincident(g649,g650)
    c: Coincident(g650,g651)
    c: Coincident(g651,g652)
    c: Vertical(g652)
    c: Coincident(g652,g653)
    c: Coincident(g653,g654)
    c: Coincident(g654,g655)
    c: Coincident(g655,g656)
    c: Coincident(g656,g657)
    c: Coincident(g657,g658)
    c: Vertical(g658)
    c: Coincident(g658,g659)
    c: Coincident(g659,g660)
    c: Vertical(g660)
    c: Coincident(g660,g661)
    c: Coincident(g661,g662)
    c: Coincident(g662,g663)
    c: Coincident(g663,g664)
    c: Coincident(g664,g665)
    c: Coincident(g665,g666)
    c: Coincident(g666,g667)
    c: Coincident(g667,g668)
    c: Coincident(g668,g669)
    c: Coincident(g669,g670)
    c: Coincident(g670,g671)
    c: Coincident(g671,g672)
    c: Coincident(g672,g673)
    c: Horizontal(g673)
    c: Coincident(g673,g674)
    c: Coincident(g674,g675)
    c: Coincident(g675,g676)
    c: Coincident(g676,g677)
    c: Coincident(g677,g678)
    c: Vertical(g678)
    c: Coincident(g678,g679)
    c: Coincident(g680,g681)
    c: Vertical(g681)
    c: Coincident(g681,g682)
    c: Horizontal(g682)
    c: Coincident(g682,g683)
    c: Coincident(g683,g684)
    c: Coincident(g684,g685)
    c: Coincident(g685,g686)
    c: Coincident(g686,g687)
    c: Vertical(g687)
    c: Coincident(g687,g688)
    c: Coincident(g688,g689)
    c: Coincident(g689,g690)
    c: Coincident(g690,g691)
    c: Coincident(g691,g692)
    c: Coincident(g692,g693)
    c: Coincident(g693,g694)
    c: Horizontal(g694)
    c: Coincident(g694,g695)
    c: Horizontal(g508)
    c: Vertical(g509)
    c: Horizontal(g510)
    c: Vertical(g519)
    c: Vertical(g517)
    c: Horizontal(g520)
    c: Coincident(g520,g696)
    c: Coincident(g696,g697)
    c: Horizontal(g697)
    c: Coincident(g697,g698)
    c: Coincident(g698,g521)
    c: Vertical(g698)
    c: Vertical(g522)
    c: Vertical(g524)
    c: Vertical(g526)
    c: Horizontal(g523)
    c: Horizontal(g525)
    c: Horizontal(g527)
    c: Horizontal(g529)
    c: Horizontal(g532)
    c: Horizontal(g521)
    c: Vertical(g528)
    c: Vertical(g530)
    c: Coincident(g530,g699)
    c: Coincident(g699,g700)
    c: Coincident(g700,g701)
    c: Coincident(g701,g531)
    c: Vertical(g700)
    c: Vertical(g531)
    c: Vertical(g533)
    c: Vertical(g535)
    c: Vertical(g537)
    c: Vertical(g539)
    c: Vertical(g541)
    c: Horizontal(g534)
    c: Horizontal(g536)
    c: Horizontal(g538)
    c: Horizontal(g540)
    c: Horizontal(g542)
    c: Horizontal(g544)
    c: Horizontal(g546)
    c: Horizontal(g699)
    c: Horizontal(g701)
    c: Vertical(g543)
    c: Vertical(g545)
    c: Vertical(g547)
    c: Vertical(g549)
    c: Horizontal(g548)
    c: Vertical(g555)
    c: Vertical(g553)
    c: Vertical(g551)
    c: Horizontal(g552)
    c: Horizontal(g556)
    c: Horizontal(g560)
    c: Vertical(g557)
    c: Vertical(g559)
    c: Vertical(g561)
    c: Coincident(g702,g562)
    c: Coincident(g702,g561)
    c: Horizontal(g565)
    c: Horizontal(g569)
    c: Horizontal(g571)
    c: Horizontal(g573)
    c: Horizontal(g575)
    c: Horizontal(g702)
    c: Vertical(g566)
    c: Vertical(g568)
    c: Vertical(g570)
    c: Vertical(g572)
    c: Vertical(g574)
    c: Vertical(g576)
    c: Vertical(g578)
    c: Vertical(g582)
    c: Vertical(g584)
    c: Horizontal(g577)
    c: Horizontal(g579)
    c: Horizontal(g581)
    c: Horizontal(g583)
    c: Horizontal(g587)
    c: Horizontal(g589)
    c: Horizontal(g591)
    c: Coincident(g591,g592)
    c: Vertical(g590)
    c: Vertical(g592)
    c: Vertical(g594)
    c: Vertical(g602)
    c: Vertical(g604)
    c: Horizontal(g595)
    c: Horizontal(g599)
    c: Horizontal(g605)
    c: Horizontal(g607)
    c: Vertical(g608)
    c: Vertical(g611)
    c: Horizontal(g612)
    c: Horizontal(g614)
    c: Horizontal(g620)
    c: Horizontal(g622)
    c: Vertical(g621)
    c: Vertical(g623)
    c: Coincident(g618,g703)
    c: Vertical(g703)
    c: Coincident(g703,g704)
    c: Horizontal(g704)
    c: Coincident(g704,g617)
    c: Horizontal(g624)
    c: Vertical(g625)
    c: Horizontal(g643)
    c: Horizontal(g645)
    c: Horizontal(g647)
    c: Horizontal(g649)
    c: Horizontal(g651)
    c: Horizontal(g653)
    c: Horizontal(g655)
    c: Horizontal(g657)
    c: Horizontal(g659)
    c: Vertical(g656)
    c: Vertical(g654)
    c: Vertical(g650)
    c: Vertical(g648)
    c: Vertical(g646)
    c: Vertical(g637)
    c: Vertical(g639)
    c: Horizontal(g661)
    c: Horizontal(g663)
    c: Horizontal(g665)
    c: Horizontal(g667)
    c: Horizontal(g669)
    c: Horizontal(g671)
    c: Horizontal(g675)
    c: Vertical(g662)
    c: Vertical(g664)
    c: Vertical(g666)
    c: Vertical(g668)
    c: Vertical(g670)
    c: Vertical(g672)
    c: Vertical(g674)
    c: Vertical(g676)
    c: Horizontal(g677)
    c: Horizontal(g679)
    c: Coincident(g679,g705)
    c: Vertical(g705)
    c: Coincident(g705,g706)
    c: Horizontal(g706)
    c: Coincident(g706,g707)
    c: Coincident(g680,g707)
    c: Horizontal(g680)
    c: Vertical(g707)
    c: Vertical(g691)
    c: Vertical(g693)
    c: Vertical(g689)
    c: Vertical(g685)
    c: Vertical(g683)
    c: Horizontal(g686)
    c: Horizontal(g688)
    c: Horizontal(g690)
    c: Horizontal(g692)
    c: Horizontal(g684)
    c: Vertical(g695)
    c: Coincident(g695,g708)
    c: Coincident(g708,g709)
    c: Coincident(g709,g710)
    c: Coincident(g710,g711)
    c: Coincident(g711,g712)
    c: Coincident(g712,g713)
    c: Horizontal(g713)
    c: Coincident(g713,g714)
    c: Coincident(g714,g715)
    c: Coincident(g715,g716)
    c: Coincident(g716,g717)
    c: Coincident(g718,g719)
    c: Horizontal(g720)
    c: Coincident(g721,g722)
    c: Coincident(g722,g723)
    c: Coincident(g723,g724)
    c: Horizontal(g724)
    c: Coincident(g724,g725)
    c: Horizontal(g726)
    c: Coincident(g726,g727)
    c: Coincident(g727,g728)
    c: Horizontal(g728)
    c: Coincident(g728,g729)
    c: Coincident(g729,g730)
    c: Coincident(g730,g731)
    c: Coincident(g731,g732)
    c: Coincident(g732,g733)
    c: Coincident(g733,g734)
    c: Coincident(g734,g735)
    c: Coincident(g735,g736)
    c: Coincident(g736,g737)
    c: Coincident(g737,g738)
    c: Coincident(g738,g739)
    c: Coincident(g739,g740)
    c: Coincident(g740,g741)
    c: Coincident(g741,g742)
    c: Coincident(g742,g743)
    c: Coincident(g743,g744)
    c: Coincident(g744,g745)
    c: Coincident(g745,g746)
    c: Coincident(g746,g747)
    c: Coincident(g747,g748)
    c: Coincident(g748,g749)
    c: Coincident(g749,g750)
    c: Coincident(g750,g751)
    c: Coincident(g751,g752)
    c: Coincident(g752,g753)
    c: Coincident(g753,g754)
    c: Coincident(g754,g755)
    c: Coincident(g755,g756)
    c: Coincident(g756,g757)
    c: Coincident(g757,g758)
    c: Coincident(g760,g761)
    c: Coincident(g761,g762)
    c: Coincident(g762,g763)
    c: Coincident(g763,g764)
    c: Coincident(g765,g766)
    c: Coincident(g766,g767)
    c: Coincident(g767,g768)
    c: Coincident(g769,g770)
    c: Coincident(g770,g771)
    c: Coincident(g772,g773)
    c: Coincident(g773,g774)
    c: Coincident(g774,g775)
    c: Coincident(g775,g776)
    c: Coincident(g776,g777)
    c: Coincident(g777,g778)
    c: Coincident(g778,g779)
    c: Coincident(g779,g780)
    c: Coincident(g780,g781)
    c: Coincident(g781,g782)
    c: Coincident(g782,g783)
    c: Coincident(g783,g784)
    c: Coincident(g784,g785)
    c: Coincident(g785,g786)
    c: Horizontal(g787)
    c: Coincident(g787,g788)
    c: Coincident(g788,g789)
    c: Coincident(g789,g790)
    c: Coincident(g790,g791)
    c: Horizontal(g791)
    c: Coincident(g791,g792)
    c: Coincident(g792,g793)
    c: Horizontal(g793)
    c: Coincident(g793,g794)
    c: Coincident(g794,g795)
    c: Coincident(g795,g796)
    c: Vertical(g796)
    c: Coincident(g796,g797)
    c: Horizontal(g797)
    c: Coincident(g797,g798)
    c: Coincident(g798,g799)
    c: Horizontal(g799)
    c: Coincident(g799,g800)
    c: Coincident(g800,g801)
    c: Coincident(g801,g802)
    c: Coincident(g802,g803)
    c: Horizontal(g803)
    c: Vertical(g804)
    c: Coincident(g804,g805)
    c: Coincident(g805,g806)
    c: Coincident(g806,g807)
    c: Coincident(g807,g808)
    c: Coincident(g808,g809)
    c: Coincident(g809,g810)
    c: Vertical(g810)
    c: Coincident(g810,g811)
    c: Coincident(g811,g812)
    c: Coincident(g812,g813)
    c: Coincident(g813,g814)
    c: Coincident(g814,g815)
    c: Horizontal(g815)
    c: Coincident(g815,g816)
    c: Coincident(g816,g817)
    c: Coincident(g817,g818)
    c: Coincident(g818,g819)
    c: Coincident(g819,g820)
    c: Coincident(g820,g821)
    c: Horizontal(g821)
    c: Coincident(g821,g822)
    c: Vertical(g822)
    c: Coincident(g822,g823)
    c: Coincident(g823,g824)
    c: Coincident(g824,g825)
    c: Horizontal(g825)
    c: Coincident(g825,g826)
    c: Coincident(g826,g827)
    c: Coincident(g827,g828)
    c: Coincident(g828,g829)
    c: Horizontal(g829)
    c: Coincident(g829,g830)
    c: Coincident(g830,g831)
    c: Coincident(g831,g832)
    c: Coincident(g832,g833)
    c: Horizontal(g834)
    c: Coincident(g834,g835)
    c: Coincident(g835,g836)
    c: Horizontal(g836)
    c: Coincident(g836,g837)
    c: Coincident(g837,g838)
    c: Horizontal(g838)
    c: Coincident(g838,g839)
    c: Coincident(g839,g840)
    c: Coincident(g840,g841)
    c: Coincident(g841,g842)
    c: Coincident(g842,g843)
    c: Coincident(g843,g844)
    c: Coincident(g844,g845)
    c: Coincident(g845,g846)
    c: Coincident(g846,g847)
    c: Coincident(g847,g848)
    c: Horizontal(g848)
    c: Coincident(g848,g849)
    c: Coincident(g849,g850)
    c: Coincident(g850,g851)
    c: Coincident(g851,g852)
    c: Coincident(g852,g853)
    c: Coincident(g853,g854)
    c: Coincident(g854,g855)
    c: Coincident(g855,g856)
    c: Coincident(g856,g857)
    c: Coincident(g857,g858)
    c: Horizontal(g858)
    c: Coincident(g858,g859)
    c: Coincident(g859,g860)
    c: Coincident(g860,g861)
    c: Coincident(g861,g862)
    c: Coincident(g862,g863)
    c: Coincident(g863,g864)
    c: Coincident(g786,g865)
    c: Coincident(g865,g866)
    c: Coincident(g866,g787)
    c: Vertical(g866)
    c: Horizontal(g709)
    c: Horizontal(g711)
    c: Horizontal(g715)
    c: Horizontal(g717)
    c: Horizontal(g719)
    c: Horizontal(g722)
    c: Coincident(g718,g867)
    c: Horizontal(g867)
    c: Coincident(g867,g868)
    c: Coincident(g868,g717)
    c: Coincident(g721,g869)
    c: Coincident(g869,g870)
    c: Coincident(g720,g870)
    c: Coincident(g871,g720)
    c: Coincident(g871,g719)
    c: Vertical(g871)
    c: Vertical(g870)
    c: Vertical(g723)
    c: Horizontal(g869)
    c: Coincident(g872,g726)
    c: Coincident(g873,g872)
    c: Coincident(g725,g873)
    c: Horizontal(g873)
    c: Horizontal(g736)
    c: Horizontal(g734)
    c: Horizontal(g732)
    c: Horizontal(g730)
    c: Horizontal(g738)
    c: Horizontal(g740)
    c: Horizontal(g742)
    c: Horizontal(g744)
    c: Horizontal(g746)
    c: Horizontal(g748)
    c: Horizontal(g750)
    c: Horizontal(g752)
    c: Horizontal(g754)
    c: Coincident(g758,g759)
    c: Horizontal(g756)
    c: Horizontal(g758)
    c: Coincident(g874,g759)
    c: Horizontal(g874)
    c: Coincident(g875,g760)
    c: Coincident(g875,g874)
    c: Horizontal(g760)
    c: Vertical(g762)
    c: Coincident(g765,g764)
    c: Vertical(g764)
    c: Vertical(g766)
    c: Vertical(g768)
    c: Coincident(g769,g768)
    c: Vertical(g770)
    c: Coincident(g876,g771)
    c: Coincident(g877,g772)
    c: Coincident(g877,g876)
    c: Vertical(g772)
    c: Vertical(g774)
    c: Vertical(g776)
    c: Vertical(g778)
    c: Vertical(g780)
    c: Vertical(g782)
    c: Vertical(g876)
    c: Horizontal(g773)
    c: Horizontal(g775)
    c: Horizontal(g777)
    c: Horizontal(g779)
    c: Horizontal(g781)
    c: Horizontal(g783)
    c: Horizontal(g785)
    c: Horizontal(g865)
    c: Vertical(g784)
    c: Vertical(g786)
    c: Vertical(g788)
    c: Vertical(g790)
    c: Horizontal(g789)
    c: Vertical(g792)
    c: Vertical(g794)
    c: Horizontal(g795)
    c: Vertical(g798)
    c: Vertical(g800)
    c: Vertical(g802)
    c: Horizontal(g801)
    c: Coincident(g804,g803)
    c: Horizontal(g805)
    c: Horizontal(g807)
    c: Horizontal(g809)
    c: Vertical(g806)
    c: Vertical(g808)
    c: Vertical(g812)
    c: Vertical(g816)
    c: Vertical(g814)
    c: Vertical(g818)
    c: Vertical(g820)
    c: Vertical(g824)
    c: Vertical(g826)
    c: Vertical(g828)
    c: Vertical(g830)
    c: Vertical(g832)
    c: Horizontal(g827)
    c: Horizontal(g823)
    c: Horizontal(g819)
    c: Horizontal(g817)
    c: Horizontal(g831)
    c: Horizontal(g833)
    c: Coincident(g878,g833)
    c: Coincident(g878,g834)
    c: Vertical(g837)
    c: Horizontal(g840)
    c: Horizontal(g842)
    c: Horizontal(g846)
    c: Horizontal(g850)
    c: Horizontal(g852)
    c: Horizontal(g854)
    c: Horizontal(g856)
    c: Horizontal(g860)
    c: Horizontal(g862)
    c: Horizontal(g864)
    c: Horizontal(g844)
    c: Coincident(g864,g879)
    c: Coincident(g879,g880)
    c: Coincident(g880,g881)
    c: Coincident(g881,g882)
    c: Horizontal(g882)
    c: Coincident(g883,g1)
    c: Coincident(g883,g0)
    c: Vertical(g883)
    c: Coincident(g0,g882)
    c: Coincident(g1,g2)
    c: Coincident(g3,g4)
    c: Coincident(g4,g5)
    c: Coincident(g5,g6)
    c: Coincident(g6,g7)
    c: Coincident(g13,g14)
    c: Coincident(g14,g15)
    c: Coincident(g16,g17)
    c: Coincident(g18,g19)
    c: Coincident(g22,g23)
    c: Coincident(g24,g25)
    c: Coincident(g27,g28)
    c: Vertical(g26)
    c: Coincident(g28,g29)
    c: Coincident(g30,g31)
    c: Horizontal(g29)
    c: Coincident(g37,g38)
    c: Coincident(g38,g39)
    c: Coincident(g39,g40)
    c: Coincident(g40,g41)
    c: Coincident(g42,g43)
    c: Coincident(g20,g21)
    c: Coincident(g21,g22)
    c: Coincident(g25,g26)
    c: Coincident(g48,g49)
    c: Coincident(g49,g50)
    c: Coincident(g58,g59)
    c: Horizontal(g59)
    c: Coincident(g61,g62)
    c: Coincident(g64,g65)
    c: Coincident(g65,g66)
    c: Coincident(g66,g67)
    c: Coincident(g68,g69)
    c: Coincident(g70,g71)
    c: Coincident(g72,g73)
    c: Coincident(g74,g75)
    c: Coincident(g86,g87)
    c: Coincident(g87,g88)
    c: Coincident(g92,g93)
    c: Coincident(g94,g95)
    c: Coincident(g96,g97)
    c: Coincident(g51,g52)
    c: Coincident(g62,g63)
    c: Coincident(g76,g77)
    c: Coincident(g77,g78)
    c: Coincident(g82,g83)
    c: Coincident(g83,g84)
FEATURE [Part::Extrusion] Extrude037  label="logoCut"
  Base = -> Sketch055
  Dir = (0,1,0)
  DirMode = 0
  FaceMakerClass = Part::FaceMakerBullseye
  LengthFwd = 10
  LengthRev = 0
  Placement = pos=(-39,-248,-155) rot=(0,0,1;0rad)
  Solid = true
  Symmetric = false
FEATURE [Part::Cut] Cut056  label="level4to3"
  Base = -> Fillet004
  Tool = -> Extrude037
FEATURE [Sketcher::SketchObject] Sketch056
  FullyConstrained = true
  sketch-geometry (4):
    g0: ArcOfCircle CenterX=0 CenterY=-150 CenterZ=0 NormalX=0 NormalY=0 NormalZ=1 AngleXU=0 Radius=93.5 StartAngle=4.49682 EndAngle=4.92796
    g1: LineSegment StartX=-20 StartY=-241.336 StartZ=0 EndX=-20 EndY=-237.336 EndZ=0
    g2: LineSegment StartX=-20 StartY=-237.336 StartZ=0 EndX=20 EndY=-237.336 EndZ=0
    g3: LineSegment StartX=20 StartY=-237.336 StartZ=0 EndX=20 EndY=-241.336 EndZ=0
  constraints (13):
    c: PointOnObject(g0,g-2)
    c: DistanceY(g0) = -150
    c: DistanceX(g0,g0) = 20
    c: DistanceX(g0,g0) = 20
    c: Diameter(g0) = 187
    c: Coincident(g1,g0)
    c: Horizontal(g2)
    c: Coincident(g3,g2)
    c: Coincident(g3,g0)
    c: Vertical(g3)
    c: Vertical(g1)
    c: Coincident(g1,g2)
    c: DistanceY(g0,g2) = 4
FEATURE [Part::Extrusion] Extrude038  label="logoAttach"
  Base = -> Sketch056
  Dir = (0,0,1)
  DirMode = 2
  FaceMakerClass = Part::FaceMakerBullseye
  LengthFwd = 28
  LengthRev = 0
  Placement = pos=(0,0,-160) rot=(0,0,1;0rad)
  Solid = true
  Symmetric = false
FEATURE [Part::Cylinder] Cylinder157
  Angle = 360
  AttacherType = Attacher::AttachEngine3D
  FirstAngle = 0
  Height = 10
  Placement = pos=(0,-238,-147.25) rot=(1,0,0;1.5708rad)
  Radius = 2
  SecondAngle = 0
FEATURE [Part::MultiFuse] Fusion105  label="logoAttach001"
  Placement = pos=(0,0,10) rot=(0,0,1;0rad)
  Shapes = -> [Extrude038,Cylinder157]
FEATURE [Part::Cylinder] Cylinder160
  Angle = 360
  AttacherType = Attacher::AttachEngine3D
  FirstAngle = 0
  Height = 10
  Placement = pos=(0,-150,75) rot=(0,0,1;0rad)
  Radius = 98
  SecondAngle = 0
FEATURE [Part::Cylinder] Cylinder161
  Angle = 360
  AttacherType = Attacher::AttachEngine3D
  FirstAngle = 0
  Height = 5
  Placement = pos=(0,-150,70) rot=(0,0,1;0rad)
  Radius = 86
  SecondAngle = 0
FEATURE [Part::Cylinder] Cylinder162
  Angle = 360
  AttacherType = Attacher::AttachEngine3D
  FirstAngle = 0
  Height = 300
  Placement = pos=(0,0,90) rot=(1,0,0;1.5708rad)
  Radius = 2.8
  SecondAngle = 0
FEATURE [Part::Cylinder] Cylinder163
  Angle = 360
  AttacherType = Attacher::AttachEngine3D
  FirstAngle = 0
  Height = 300
  Placement = pos=(-150,-150,90) rot=(0.57735,0.57735,0.57735;2.0944rad)
  Radius = 2.8
  SecondAngle = 0
FEATURE [Part::Cylinder] Cylinder164  label="srsCut002"
  Angle = 360
  AttacherType = Attacher::AttachEngine3D
  FirstAngle = 0
  Height = 100
  Placement = pos=(0,-150,0) rot=(0,0,1;0rad)
  Radius = 80
  SecondAngle = 0
FEATURE [Part::Cylinder] Cylinder165
  Angle = 360
  AttacherType = Attacher::AttachEngine3D
  FirstAngle = 0
  Height = 300
  Placement = pos=(0,0,90) rot=(1,0,0;1.5708rad)
  Radius = 2.8
  SecondAngle = 0
FEATURE [Part::Cylinder] Cylinder166
  Angle = 360
  AttacherType = Attacher::AttachEngine3D
  FirstAngle = 0
  Height = 300
  Placement = pos=(-150,-150,90) rot=(0.57735,0.57735,0.57735;2.0944rad)
  Radius = 2.8
  SecondAngle = 0
FEATURE [Part::Cylinder] Cylinder167
  Angle = 360
  AttacherType = Attacher::AttachEngine3D
  FirstAngle = 0
  Height = 300
  Placement = pos=(106.066,-43.934,90) rot=(0.862856,-0.357407,-0.357407;1.71777rad)
  Radius = 2.8
  SecondAngle = 0
FEATURE [Part::Cylinder] Cylinder168
  Angle = 360
  AttacherType = Attacher::AttachEngine3D
  FirstAngle = 0
  Height = 300
  Placement = pos=(-106.066,-43.934,90) rot=(0.862856,0.357407,0.357407;1.71777rad)
  Radius = 2.8
  SecondAngle = 0
FEATURE [Part::Cylinder] Cylinder169
  Angle = 360
  AttacherType = Attacher::AttachEngine3D
  FirstAngle = 0
  Height = 300
  Placement = pos=(0,0,90) rot=(1,0,0;1.5708rad)
  Radius = 2.13
  SecondAngle = 0
FEATURE [Part::Cylinder] Cylinder170
  Angle = 360
  AttacherType = Attacher::AttachEngine3D
  FirstAngle = 0
  Height = 300
  Placement = pos=(-150,-150,90) rot=(0.57735,0.57735,0.57735;2.0944rad)
  Radius = 2.13
  SecondAngle = 0
FEATURE [Part::MultiFuse] Fusion110  label="m4Cuts018"
  Shapes = -> [Cylinder163,Cylinder162]
FEATURE [Part::MultiFuse] Fusion112  label="srsCut003"
  Shapes = -> [Cylinder164,Fusion110]
FEATURE [Part::MultiFuse] Fusion113  label="m4Cuts019"
  Placement = pos=(0,0,-82) rot=(0,0,1;0rad)
  Shapes = -> [Cylinder166,Cylinder165]
FEATURE [Part::MultiFuse] Fusion114  label="m4Cuts020"
  Placement = pos=(0,0,-82) rot=(0,0,1;0rad)
  Shapes = -> [Cylinder167,Cylinder168]
FEATURE [Part::MultiFuse] Fusion115  label="m4Cuts021"
  Shapes = -> [Fusion113,Fusion114]
FEATURE [Part::MultiFuse] Fusion117  label="m4Cuts022"
  Placement = pos=(0,0,-321) rot=(0,0,1;0rad)
  Shapes = -> [Cylinder170,Cylinder169]
FEATURE [Sketcher::SketchObject] Sketch075
  FullyConstrained = true
  Placement = pos=(0,0,65) rot=(0,0,1;0rad)
  sketch-geometry (1):
    g0: Circle CenterX=0 CenterY=-150 CenterZ=0 NormalX=0 NormalY=0 NormalZ=1 AngleXU=0 Radius=98
  constraints (3):
    c: PointOnObject(g0,g-2)
    c: DistanceY(g0) = -150
    c: Radius(g0) = 98
FEATURE [Sketcher::SketchObject] Sketch076
  FullyConstrained = true
  Placement = pos=(0,0,80) rot=(0,0,1;0rad)
  sketch-geometry (1):
    g0: Circle CenterX=0 CenterY=-150 CenterZ=0 NormalX=0 NormalY=0 NormalZ=1 AngleXU=0 Radius=80
  constraints (3):
    c: PointOnObject(g0,g-2)
    c: DistanceY(g0) = -150
    c: Radius(g0) = 80
FEATURE [Part::Loft] Loft017  label="Loft029"
  Closed = false
  MaxDegree = 5
  Placement = pos=(0,0,-15) rot=(0,0,1;0rad)
  Ruled = false
  Sections = -> [Sketch076,Sketch075]
  Solid = true
FEATURE [Sketcher::SketchObject] Sketch077
  FullyConstrained = true
  Placement = pos=(0,0,65) rot=(0,0,1;0rad)
  sketch-geometry (1):
    g0: Circle CenterX=0 CenterY=-150 CenterZ=0 NormalX=0 NormalY=0 NormalZ=1 AngleXU=0 Radius=98
  constraints (3):
    c: PointOnObject(g0,g-2)
    c: DistanceY(g0) = -150
    c: Radius(g0) = 98
FEATURE [Sketcher::SketchObject] Sketch078
  FullyConstrained = true
  Placement = pos=(0,0,80) rot=(0,0,1;0rad)
  sketch-geometry (1):
    g0: Circle CenterX=0 CenterY=-150 CenterZ=0 NormalX=0 NormalY=0 NormalZ=1 AngleXU=0 Radius=80
  constraints (3):
    c: PointOnObject(g0,g-2)
    c: DistanceY(g0) = -150
    c: Radius(g0) = 80
FEATURE [Part::Loft] Loft018  label="Loft030"
  Closed = false
  MaxDegree = 5
  Placement = pos=(0,0,-20) rot=(0,0,1;0rad)
  Ruled = false
  Sections = -> [Sketch078,Sketch077]
  Solid = true
FEATURE [Part::Cut] Cut062  label="Loft025"
  Base = -> Loft017
  Tool = -> Loft018
FEATURE [Sketcher::SketchObject] Sketch079
  FullyConstrained = true
  Placement = pos=(0,0,65) rot=(0,0,1;0rad)
  sketch-geometry (1):
    g0: Circle CenterX=0 CenterY=-150 CenterZ=0 NormalX=0 NormalY=0 NormalZ=1 AngleXU=0 Radius=98
  constraints (3):
    c: PointOnObject(g0,g-2)
    c: DistanceY(g0) = -150
    c: Radius(g0) = 98
FEATURE [Sketcher::SketchObject] Sketch080
  FullyConstrained = true
  Placement = pos=(0,0,80) rot=(0,0,1;0rad)
  sketch-geometry (1):
    g0: Circle CenterX=0 CenterY=-150 CenterZ=0 NormalX=0 NormalY=0 NormalZ=1 AngleXU=0 Radius=80
  constraints (3):
    c: PointOnObject(g0,g-2)
    c: DistanceY(g0) = -150
    c: Radius(g0) = 80
FEATURE [Part::Loft] Loft019  label="Loft031"
  Closed = false
  MaxDegree = 5
  Placement = pos=(0,0,-15) rot=(0,0,1;0rad)
  Ruled = false
  Sections = -> [Sketch080,Sketch079]
  Solid = true
FEATURE [Sketcher::SketchObject] Sketch081
  FullyConstrained = true
  Placement = pos=(0,0,65) rot=(0,0,1;0rad)
  sketch-geometry (1):
    g0: Circle CenterX=0 CenterY=-150 CenterZ=0 NormalX=0 NormalY=0 NormalZ=1 AngleXU=0 Radius=98
  constraints (3):
    c: PointOnObject(g0,g-2)
    c: DistanceY(g0) = -150
    c: Radius(g0) = 98
FEATURE [Sketcher::SketchObject] Sketch082
  FullyConstrained = true
  Placement = pos=(0,0,80) rot=(0,0,1;0rad)
  sketch-geometry (1):
    g0: Circle CenterX=0 CenterY=-150 CenterZ=0 NormalX=0 NormalY=0 NormalZ=1 AngleXU=0 Radius=80
  constraints (3):
    c: PointOnObject(g0,g-2)
    c: DistanceY(g0) = -150
    c: Radius(g0) = 80
FEATURE [Part::Loft] Loft020  label="Loft032"
  Closed = false
  MaxDegree = 5
  Placement = pos=(0,0,-20) rot=(0,0,1;0rad)
  Ruled = false
  Sections = -> [Sketch082,Sketch081]
  Solid = true
FEATURE [Part::Cut] Cut063  label="Loft026"
  Base = -> Loft019
  Placement = pos=(0,0,-15) rot=(0,0,1;0rad)
  Tool = -> Loft020
FEATURE [Sketcher::SketchObject] Sketch083
  FullyConstrained = true
  Placement = pos=(0,0,65) rot=(0,0,1;0rad)
  sketch-geometry (1):
    g0: Circle CenterX=0 CenterY=-150 CenterZ=0 NormalX=0 NormalY=0 NormalZ=1 AngleXU=0 Radius=98
  constraints (3):
    c: PointOnObject(g0,g-2)
    c: DistanceY(g0) = -150
    c: Radius(g0) = 98
FEATURE [Sketcher::SketchObject] Sketch084
  FullyConstrained = true
  Placement = pos=(0,0,80) rot=(0,0,1;0rad)
  sketch-geometry (1):
    g0: Circle CenterX=0 CenterY=-150 CenterZ=0 NormalX=0 NormalY=0 NormalZ=1 AngleXU=0 Radius=80
  constraints (3):
    c: PointOnObject(g0,g-2)
    c: DistanceY(g0) = -150
    c: Radius(g0) = 80
FEATURE [Part::Loft] Loft021  label="Loft033"
  Closed = false
  MaxDegree = 5
  Placement = pos=(0,0,-15) rot=(0,0,1;0rad)
  Ruled = false
  Sections = -> [Sketch084,Sketch083]
  Solid = true
FEATURE [Sketcher::SketchObject] Sketch085
  FullyConstrained = true
  Placement = pos=(0,0,65) rot=(0,0,1;0rad)
  sketch-geometry (1):
    g0: Circle CenterX=0 CenterY=-150 CenterZ=0 NormalX=0 NormalY=0 NormalZ=1 AngleXU=0 Radius=98
  constraints (3):
    c: PointOnObject(g0,g-2)
    c: DistanceY(g0) = -150
    c: Radius(g0) = 98
FEATURE [Sketcher::SketchObject] Sketch086
  FullyConstrained = true
  Placement = pos=(0,0,80) rot=(0,0,1;0rad)
  sketch-geometry (1):
    g0: Circle CenterX=0 CenterY=-150 CenterZ=0 NormalX=0 NormalY=0 NormalZ=1 AngleXU=0 Radius=80
  constraints (3):
    c: PointOnObject(g0,g-2)
    c: DistanceY(g0) = -150
    c: Radius(g0) = 80
FEATURE [Part::Loft] Loft022  label="Loft034"
  Closed = false
  MaxDegree = 5
  Placement = pos=(0,0,-20) rot=(0,0,1;0rad)
  Ruled = false
  Sections = -> [Sketch086,Sketch085]
  Solid = true
FEATURE [Part::Cut] Cut064  label="Loft027"
  Base = -> Loft021
  Placement = pos=(0,0,-30) rot=(0,0,1;0rad)
  Tool = -> Loft022
FEATURE [Sketcher::SketchObject] Sketch087
  FullyConstrained = true
  Placement = pos=(0,0,65) rot=(0,0,1;0rad)
  sketch-geometry (1):
    g0: Circle CenterX=0 CenterY=-150 CenterZ=0 NormalX=0 NormalY=0 NormalZ=1 AngleXU=0 Radius=98
  constraints (3):
    c: PointOnObject(g0,g-2)
    c: DistanceY(g0) = -150
    c: Radius(g0) = 98
FEATURE [Sketcher::SketchObject] Sketch088
  FullyConstrained = true
  Placement = pos=(0,0,80) rot=(0,0,1;0rad)
  sketch-geometry (1):
    g0: Circle CenterX=0 CenterY=-150 CenterZ=0 NormalX=0 NormalY=0 NormalZ=1 AngleXU=0 Radius=80
  constraints (3):
    c: PointOnObject(g0,g-2)
    c: DistanceY(g0) = -150
    c: Radius(g0) = 80
FEATURE [Part::Loft] Loft023  label="Loft035"
  Closed = false
  MaxDegree = 5
  Placement = pos=(0,0,-15) rot=(0,0,1;0rad)
  Ruled = false
  Sections = -> [Sketch088,Sketch087]
  Solid = true
FEATURE [Sketcher::SketchObject] Sketch089
  FullyConstrained = true
  Placement = pos=(0,0,65) rot=(0,0,1;0rad)
  sketch-geometry (1):
    g0: Circle CenterX=0 CenterY=-150 CenterZ=0 NormalX=0 NormalY=0 NormalZ=1 AngleXU=0 Radius=98
  constraints (3):
    c: PointOnObject(g0,g-2)
    c: DistanceY(g0) = -150
    c: Radius(g0) = 98
FEATURE [Sketcher::SketchObject] Sketch090
  FullyConstrained = true
  Placement = pos=(0,0,80) rot=(0,0,1;0rad)
  sketch-geometry (1):
    g0: Circle CenterX=0 CenterY=-150 CenterZ=0 NormalX=0 NormalY=0 NormalZ=1 AngleXU=0 Radius=80
  constraints (3):
    c: PointOnObject(g0,g-2)
    c: DistanceY(g0) = -150
    c: Radius(g0) = 80
FEATURE [Part::Loft] Loft024  label="Loft036"
  Closed = false
  MaxDegree = 5
  Placement = pos=(0,0,-20) rot=(0,0,1;0rad)
  Ruled = false
  Sections = -> [Sketch090,Sketch089]
  Solid = true
FEATURE [Part::Cut] Cut065  label="Loft028"
  Base = -> Loft023
  Placement = pos=(0,0,15) rot=(0,0,1;0rad)
  Tool = -> Loft024
FEATURE [Part::Cut] Cut066  label="top021"
  Base = -> Cut065
  Tool = -> Cylinder160
FEATURE [Part::MultiFuse] Fusion108  label="top022"
  Shapes = -> [Cut066,Cylinder161]
FEATURE [Part::MultiFuse] Fusion109  label="solarRadiationShield002"
  Shapes = -> [Fusion108,Cut062,Cut063,Cut064]
FEATURE [Sketcher::SketchObject] Sketch091
  FullyConstrained = true
  sketch-geometry (16):
    g0: ArcOfCircle CenterX=0 CenterY=-150 CenterZ=0 NormalX=0 NormalY=0 NormalZ=1 AngleXU=0 Radius=93 StartAngle=2.86943 EndAngle=3.41376
    g1: ArcOfCircle CenterX=0 CenterY=-150 CenterZ=0 NormalX=0 NormalY=0 NormalZ=1 AngleXU=0 Radius=93 StartAngle=1.29863 EndAngle=1.84296
    g2: ArcOfCircle CenterX=0 CenterY=-150 CenterZ=0 NormalX=0 NormalY=0 NormalZ=1 AngleXU=0 Radius=93 StartAngle=6.01102 EndAngle=6.55535
    g3: ArcOfCircle CenterX=0 CenterY=-150 CenterZ=0 NormalX=0 NormalY=0 NormalZ=1 AngleXU=0 Radius=93 StartAngle=4.44022 EndAngle=4.98455
    g4: ArcOfCircle CenterX=0 CenterY=-150 CenterZ=0 NormalX=0 NormalY=0 NormalZ=1 AngleXU=0 Radius=86 StartAngle=1.27584 EndAngle=1.86575
    g5: ArcOfCircle CenterX=0 CenterY=-150 CenterZ=0 NormalX=0 NormalY=0 NormalZ=1 AngleXU=0 Radius=86 StartAngle=5.98823 EndAngle=6.57814
    g6: ArcOfCircle CenterX=0 CenterY=-150 CenterZ=0 NormalX=0 NormalY=0 NormalZ=1 AngleXU=0 Radius=86 StartAngle=2.84664 EndAngle=3.43655
    g7: ArcOfCircle CenterX=0 CenterY=-150 CenterZ=0 NormalX=0 NormalY=0 NormalZ=1 AngleXU=0 Radius=86 StartAngle=4.41743 EndAngle=5.00734
    g8: LineSegment StartX=25 StartY=-60.4232 StartZ=0 EndX=25 EndY=-67.7139 EndZ=0
    g9: LineSegment StartX=-25 StartY=-60.4232 StartZ=0 EndX=-25 EndY=-67.7139 EndZ=0
    g10: LineSegment StartX=-89.5768 StartY=-125 StartZ=0 EndX=-82.2861 EndY=-125 EndZ=0
    g11: LineSegment StartX=-89.5768 StartY=-175 StartZ=0 EndX=-82.2861 EndY=-175 EndZ=0
    g12: LineSegment StartX=-25 StartY=-239.577 StartZ=0 EndX=-25 EndY=-232.286 EndZ=0
    g13: LineSegment StartX=25 StartY=-239.577 StartZ=0 EndX=25 EndY=-232.286 EndZ=0
    g14: LineSegment StartX=89.5768 StartY=-175 StartZ=0 EndX=82.2861 EndY=-175 EndZ=0
    g15: LineSegment StartX=89.5768 StartY=-125 StartZ=0 EndX=82.2861 EndY=-125 EndZ=0
  constraints (49):
    c: PointOnObject(g0,g-2)
    c: Coincident(g1,g0)
    c: Coincident(g2,g0)
    c: Coincident(g3,g0)
    c: DistanceY(g0) = -150
    c: Coincident(g4,g0)
    c: Coincident(g5,g0)
    c: Coincident(g6,g0)
    c: Coincident(g7,g0)
    c: DistanceX(g4,g0) = 25
    c: DistanceX(g1,g4) = 0
    c: DistanceX(g0,g4) = 25
    c: DistanceX(g4,g1) = 0
    c: DistanceY(g0,g5) = 25
    c: DistanceY(g5,g2) = 0
    c: DistanceY(g2,g0) = 25
    c: DistanceY(g2,g5) = 0
    c: DistanceY(g6,g0) = 25
    c: DistanceY(g0,g6) = 0
    c: DistanceY(g0,g6) = 25
    c: DistanceY(g6,g0) = 0
    c: Equal(g1,g2)
    c: Equal(g1,g3)
    c: Equal(g1,g0)
    c: Radius(g1) = 93
    c: Equal(g6,g4)
    c: Equal(g6,g5)
    c: Equal(g6,g7)
    c: Radius(g6) = 86
    c: DistanceX(g0,g7) = 25
    c: DistanceX(g7,g3) = 0
    c: DistanceX(g3) = -25
    c: DistanceX(g3,g7) = 0
    c: Coincident(g8,g1)
    c: Coincident(g8,g4)
    c: Coincident(g9,g1)
    c: Coincident(g9,g4)
    c: Coincident(g10,g0)
    c: Coincident(g10,g6)
    c: Coincident(g11,g0)
    c: Coincident(g11,g6)
    c: Coincident(g12,g3)
    c: Coincident(g12,g7)
    c: Coincident(g13,g3)
    c: Coincident(g13,g7)
    c: Coincident(g14,g2)
    c: Coincident(g14,g5)
    c: Coincident(g15,g2)
    c: Coincident(g15,g5)
FEATURE [Part::Extrusion] Extrude040  label="srsHolds003"
  Base = -> Sketch091
  Dir = (0,0,1)
  DirMode = 2
  FaceMakerClass = Part::FaceMakerBullseye
  LengthFwd = 95.5
  LengthRev = 0
  Solid = true
  Symmetric = false
FEATURE [Part::MultiFuse] Fusion111  label="srs006"
  Shapes = -> [Fusion109,Extrude040]
FEATURE [Part::Cut] Cut067  label="srs004"
  Base = -> Fusion111
  Tool = -> Fusion112
FEATURE [Part::Cut] Cut068  label="srs005"
  Base = -> Cut067
  Tool = -> Fusion115
FEATURE [Sketcher::SketchObject] Sketch092  label="top023"
  FullyConstrained = true
  sketch-geometry (2):
    g0: Circle CenterX=0 CenterY=-150 CenterZ=0 NormalX=0 NormalY=0 NormalZ=1 AngleXU=0 Radius=98
    g1: Circle CenterX=0 CenterY=-150 CenterZ=0 NormalX=0 NormalY=0 NormalZ=1 AngleXU=0 Radius=76
  constraints (5):
    c: PointOnObject(g0,g-2)
    c: Diameter(g0) = 196
    c: DistanceY(g0) = -150
    c: Coincident(g1,g0)
    c: Radius(g1) = 76
FEATURE [Part::Extrusion] Extrude041  label="TupeConnectLevel008"
  Base = -> Sketch092
  Dir = (0,0,1)
  DirMode = 2
  FaceMakerClass = Part::FaceMakerBullseye
  LengthFwd = 5
  LengthRev = 0
  Placement = pos=(0,0,-65) rot=(0,0,1;0rad)
  Solid = true
  Symmetric = false
FEATURE [Sketcher::SketchObject] Sketch093
  FullyConstrained = true
  sketch-geometry (4):
    g0: Circle CenterX=0 CenterY=-68 CenterZ=0 NormalX=0 NormalY=0 NormalZ=1 AngleXU=0 Radius=2.8
    g1: Circle CenterX=82 CenterY=-150 CenterZ=0 NormalX=0 NormalY=0 NormalZ=1 AngleXU=0 Radius=2.8
    g2: Circle CenterX=0 CenterY=-232 CenterZ=0 NormalX=0 NormalY=0 NormalZ=1 AngleXU=0 Radius=2.8
    g3: Circle CenterX=-82 CenterY=-150 CenterZ=0 NormalX=0 NormalY=0 NormalZ=1 AngleXU=0 Radius=2.8
  constraints (12):
    c: PointOnObject(g0,g-2)
    c: DistanceY(g1) = -150
    c: DistanceY(g1,g3) = 0
    c: DistanceX(g2) = 0
    c: DistanceX(g1) = 82
    c: Equal(g1,g0)
    c: Equal(g1,g3)
    c: Equal(g1,g2)
    c: Diameter(g1) = 5.6
    c: DistanceX(g3) = -82
    c: DistanceY(g3,g0) = 82
    c: DistanceY(g2,g3) = 82
FEATURE [Part::Extrusion] Extrude042  label="m4HeatSetVerCuts007"
  Base = -> Sketch093
  Dir = (0,0,1)
  DirMode = 2
  FaceMakerClass = Part::FaceMakerBullseye
  LengthFwd = 20
  LengthRev = 0
  Placement = pos=(0,0,-193) rot=(0,0,1;0rad)
  Solid = true
  Symmetric = false
FEATURE [Part::FeaturePython] Tube011  # WARN: FeaturePython — macro-defined, semantics opaque (R4)
  AttacherType = Attacher::AttachEngine3D
  Height = 3
  InnerRadius = 95
  OuterRadius = 98
  Placement = pos=(0,-150,-188) rot=(0,0,1;0rad)
FEATURE [Part::FeaturePython] Tube012  # WARN: FeaturePython — macro-defined, semantics opaque (R4)
  AttacherType = Attacher::AttachEngine3D
  Height = 65
  InnerRadius = 94
  OuterRadius = 98
  Placement = pos=(0,-150,-125) rot=(0,0,1;0rad)
FEATURE [Part::MultiFuse] Fusion116  label="tube5to008"
  Placement = pos=(0,0,-125) rot=(0,0,1;0rad)
  Shapes = -> [Extrude041,Tube012]
FEATURE [Part::Cut] Cut069  label="tube4to009"
  Base = -> Fusion116
  Tool = -> Fusion117
FEATURE [Part::Cut] Cut070  label="tube4to5s004"
  Base = -> Cut069
  Tool = -> Extrude042
FEATURE [Part::Fillet] Fillet011  label="level5s006"
  Base = -> Cut070
  Edges = 3 edges r=3: [Edge3,Edge7,Edge32]
FEATURE [Part::Cut] Cut071  label="cutAddOn003"
  Base = -> Tube011
  Placement = pos=(0,0,205.25) rot=(0,0,1;0rad)
  Tool = -> Fillet011
FEATURE [Part::MultiFuse] Fusion118  label="srs007"
  Shapes = -> [Cut071,Cut068]
FEATURE [Sketcher::SketchObject] Sketch094
  FullyConstrained = true
  Placement = pos=(0,0,65) rot=(0,0,1;0rad)
  sketch-geometry (1):
    g0: Circle CenterX=0 CenterY=-150 CenterZ=0 NormalX=0 NormalY=0 NormalZ=1 AngleXU=0 Radius=100
  constraints (3):
    c: PointOnObject(g0,g-2)
    c: DistanceY(g0) = -150
    c: Radius(g0) = 100
FEATURE [Sketcher::SketchObject] Sketch095
  FullyConstrained = true
  Placement = pos=(0,0,80) rot=(0,0,1;0rad)
  sketch-geometry (1):
    g0: Circle CenterX=0 CenterY=-150 CenterZ=0 NormalX=0 NormalY=0 NormalZ=1 AngleXU=0 Radius=92
  constraints (3):
    c: PointOnObject(g0,g-2)
    c: DistanceY(g0) = -150
    c: Radius(g0) = 92
FEATURE [Part::Loft] Loft025  label="Loft037"
  Closed = false
  MaxDegree = 5
  Placement = pos=(0,0,-193.5) rot=(0,0,1;0rad)
  Ruled = false
  Sections = -> [Sketch095,Sketch094]
  Solid = true
FEATURE [Sketcher::SketchObject] Sketch096
  FullyConstrained = true
  Placement = pos=(0,0,65) rot=(0,0,1;0rad)
  sketch-geometry (1):
    g0: Circle CenterX=0 CenterY=-150 CenterZ=0 NormalX=0 NormalY=0 NormalZ=1 AngleXU=0 Radius=100
  constraints (3):
    c: PointOnObject(g0,g-2)
    c: DistanceY(g0) = -150
    c: Radius(g0) = 100
FEATURE [Sketcher::SketchObject] Sketch097
  FullyConstrained = true
  Placement = pos=(0,0,80) rot=(0,0,1;0rad)
  sketch-geometry (1):
    g0: Circle CenterX=0 CenterY=-150 CenterZ=0 NormalX=0 NormalY=0 NormalZ=1 AngleXU=0 Radius=92
  constraints (3):
    c: PointOnObject(g0,g-2)
    c: DistanceY(g0) = -150
    c: Radius(g0) = 92
FEATURE [Part::Loft] Loft026  label="Loft038"
  Closed = false
  MaxDegree = 5
  Placement = pos=(0,0,-191.5) rot=(0,0,1;0rad)
  Ruled = false
  Sections = -> [Sketch097,Sketch096]
  Solid = true
FEATURE [Part::Cut] Cut072
  Base = -> Loft026
  Tool = -> Loft025
FEATURE [Sketcher::SketchObject] Sketch098
  FullyConstrained = true
  Placement = pos=(0,0,65) rot=(0,0,1;0rad)
  sketch-geometry (1):
    g0: Circle CenterX=0 CenterY=-150 CenterZ=0 NormalX=0 NormalY=0 NormalZ=1 AngleXU=0 Radius=100
  constraints (3):
    c: PointOnObject(g0,g-2)
    c: DistanceY(g0) = -150
    c: Radius(g0) = 100
FEATURE [Sketcher::SketchObject] Sketch099
  FullyConstrained = true
  Placement = pos=(0,0,80) rot=(0,0,1;0rad)
  sketch-geometry (1):
    g0: Circle CenterX=0 CenterY=-150 CenterZ=0 NormalX=0 NormalY=0 NormalZ=1 AngleXU=0 Radius=92
  constraints (3):
    c: PointOnObject(g0,g-2)
    c: DistanceY(g0) = -150
    c: Radius(g0) = 92
FEATURE [Part::Loft] Loft027  label="Loft039"
  Closed = false
  MaxDegree = 5
  Placement = pos=(0,0,-193.5) rot=(0,0,1;0rad)
  Ruled = false
  Sections = -> [Sketch099,Sketch098]
  Solid = true
FEATURE [Sketcher::SketchObject] Sketch100
  FullyConstrained = true
  Placement = pos=(0,0,65) rot=(0,0,1;0rad)
  sketch-geometry (1):
    g0: Circle CenterX=0 CenterY=-150 CenterZ=0 NormalX=0 NormalY=0 NormalZ=1 AngleXU=0 Radius=100
  constraints (3):
    c: PointOnObject(g0,g-2)
    c: DistanceY(g0) = -150
    c: Radius(g0) = 100
FEATURE [Sketcher::SketchObject] Sketch101
  FullyConstrained = true
  Placement = pos=(0,0,80) rot=(0,0,1;0rad)
  sketch-geometry (1):
    g0: Circle CenterX=0 CenterY=-150 CenterZ=0 NormalX=0 NormalY=0 NormalZ=1 AngleXU=0 Radius=92
  constraints (3):
    c: PointOnObject(g0,g-2)
    c: DistanceY(g0) = -150
    c: Radius(g0) = 92
FEATURE [Part::Loft] Loft028  label="Loft040"
  Closed = false
  MaxDegree = 5
  Placement = pos=(0,0,-191.5) rot=(0,0,1;0rad)
  Ruled = false
  Sections = -> [Sketch101,Sketch100]
  Solid = true
FEATURE [Part::Cut] Cut073
  Base = -> Loft028
  Placement = pos=(0,0,8) rot=(0,0,1;0rad)
  Tool = -> Loft027
FEATURE [Sketcher::SketchObject] Sketch102
  FullyConstrained = true
  Placement = pos=(0,0,65) rot=(0,0,1;0rad)
  sketch-geometry (1):
    g0: Circle CenterX=0 CenterY=-150 CenterZ=0 NormalX=0 NormalY=0 NormalZ=1 AngleXU=0 Radius=100
  constraints (3):
    c: PointOnObject(g0,g-2)
    c: DistanceY(g0) = -150
    c: Radius(g0) = 100
FEATURE [Sketcher::SketchObject] Sketch103
  FullyConstrained = true
  Placement = pos=(0,0,80) rot=(0,0,1;0rad)
  sketch-geometry (1):
    g0: Circle CenterX=0 CenterY=-150 CenterZ=0 NormalX=0 NormalY=0 NormalZ=1 AngleXU=0 Radius=92
  constraints (3):
    c: PointOnObject(g0,g-2)
    c: DistanceY(g0) = -150
    c: Radius(g0) = 92
FEATURE [Part::Loft] Loft029  label="Loft041"
  Closed = false
  MaxDegree = 5
  Placement = pos=(0,0,-193.5) rot=(0,0,1;0rad)
  Ruled = false
  Sections = -> [Sketch103,Sketch102]
  Solid = true
FEATURE [Sketcher::SketchObject] Sketch104
  FullyConstrained = true
  Placement = pos=(0,0,65) rot=(0,0,1;0rad)
  sketch-geometry (1):
    g0: Circle CenterX=0 CenterY=-150 CenterZ=0 NormalX=0 NormalY=0 NormalZ=1 AngleXU=0 Radius=100
  constraints (3):
    c: PointOnObject(g0,g-2)
    c: DistanceY(g0) = -150
    c: Radius(g0) = 100
FEATURE [Sketcher::SketchObject] Sketch105
  FullyConstrained = true
  Placement = pos=(0,0,80) rot=(0,0,1;0rad)
  sketch-geometry (1):
    g0: Circle CenterX=0 CenterY=-150 CenterZ=0 NormalX=0 NormalY=0 NormalZ=1 AngleXU=0 Radius=92
  constraints (3):
    c: PointOnObject(g0,g-2)
    c: DistanceY(g0) = -150
    c: Radius(g0) = 92
FEATURE [Part::Loft] Loft030  label="Loft042"
  Closed = false
  MaxDegree = 5
  Placement = pos=(0,0,-191.5) rot=(0,0,1;0rad)
  Ruled = false
  Sections = -> [Sketch105,Sketch104]
  Solid = true
FEATURE [Part::Cut] Cut074
  Base = -> Loft030
  Placement = pos=(0,0,16) rot=(0,0,1;0rad)
  Tool = -> Loft029
FEATURE [Sketcher::SketchObject] Sketch106
  FullyConstrained = true
  Placement = pos=(0,0,65) rot=(0,0,1;0rad)
  sketch-geometry (1):
    g0: Circle CenterX=0 CenterY=-150 CenterZ=0 NormalX=0 NormalY=0 NormalZ=1 AngleXU=0 Radius=100
  constraints (3):
    c: PointOnObject(g0,g-2)
    c: DistanceY(g0) = -150
    c: Radius(g0) = 100
FEATURE [Sketcher::SketchObject] Sketch107
  FullyConstrained = true
  Placement = pos=(0,0,80) rot=(0,0,1;0rad)
  sketch-geometry (1):
    g0: Circle CenterX=0 CenterY=-150 CenterZ=0 NormalX=0 NormalY=0 NormalZ=1 AngleXU=0 Radius=92
  constraints (3):
    c: PointOnObject(g0,g-2)
    c: DistanceY(g0) = -150
    c: Radius(g0) = 92
FEATURE [Part::Loft] Loft031  label="Loft043"
  Closed = false
  MaxDegree = 5
  Placement = pos=(0,0,-193.5) rot=(0,0,1;0rad)
  Ruled = false
  Sections = -> [Sketch107,Sketch106]
  Solid = true
FEATURE [Sketcher::SketchObject] Sketch108
  FullyConstrained = true
  Placement = pos=(0,0,65) rot=(0,0,1;0rad)
  sketch-geometry (1):
    g0: Circle CenterX=0 CenterY=-150 CenterZ=0 NormalX=0 NormalY=0 NormalZ=1 AngleXU=0 Radius=100
  constraints (3):
    c: PointOnObject(g0,g-2)
    c: DistanceY(g0) = -150
    c: Radius(g0) = 100
FEATURE [Sketcher::SketchObject] Sketch109
  FullyConstrained = true
  Placement = pos=(0,0,80) rot=(0,0,1;0rad)
  sketch-geometry (1):
    g0: Circle CenterX=0 CenterY=-150 CenterZ=0 NormalX=0 NormalY=0 NormalZ=1 AngleXU=0 Radius=92
  constraints (3):
    c: PointOnObject(g0,g-2)
    c: DistanceY(g0) = -150
    c: Radius(g0) = 92
FEATURE [Part::Loft] Loft032  label="Loft044"
  Closed = false
  MaxDegree = 5
  Placement = pos=(0,0,-191.5) rot=(0,0,1;0rad)
  Ruled = false
  Sections = -> [Sketch109,Sketch108]
  Solid = true
FEATURE [Part::Cut] Cut075
  Base = -> Loft032
  Placement = pos=(0,0,24) rot=(0,0,1;0rad)
  Tool = -> Loft031
FEATURE [Sketcher::SketchObject] Sketch110
  FullyConstrained = true
  Placement = pos=(0,0,65) rot=(0,0,1;0rad)
  sketch-geometry (1):
    g0: Circle CenterX=0 CenterY=-150 CenterZ=0 NormalX=0 NormalY=0 NormalZ=1 AngleXU=0 Radius=100
  constraints (3):
    c: PointOnObject(g0,g-2)
    c: DistanceY(g0) = -150
    c: Radius(g0) = 100
FEATURE [Sketcher::SketchObject] Sketch111
  FullyConstrained = true
  Placement = pos=(0,0,80) rot=(0,0,1;0rad)
  sketch-geometry (1):
    g0: Circle CenterX=0 CenterY=-150 CenterZ=0 NormalX=0 NormalY=0 NormalZ=1 AngleXU=0 Radius=92
  constraints (3):
    c: PointOnObject(g0,g-2)
    c: DistanceY(g0) = -150
    c: Radius(g0) = 92
FEATURE [Part::Loft] Loft033  label="Loft045"
  Closed = false
  MaxDegree = 5
  Placement = pos=(0,0,-193.5) rot=(0,0,1;0rad)
  Ruled = false
  Sections = -> [Sketch111,Sketch110]
  Solid = true
FEATURE [Sketcher::SketchObject] Sketch112
  FullyConstrained = true
  Placement = pos=(0,0,65) rot=(0,0,1;0rad)
  sketch-geometry (1):
    g0: Circle CenterX=0 CenterY=-150 CenterZ=0 NormalX=0 NormalY=0 NormalZ=1 AngleXU=0 Radius=100
  constraints (3):
    c: PointOnObject(g0,g-2)
    c: DistanceY(g0) = -150
    c: Radius(g0) = 100
FEATURE [Sketcher::SketchObject] Sketch113
  FullyConstrained = true
  Placement = pos=(0,0,80) rot=(0,0,1;0rad)
  sketch-geometry (1):
    g0: Circle CenterX=0 CenterY=-150 CenterZ=0 NormalX=0 NormalY=0 NormalZ=1 AngleXU=0 Radius=92
  constraints (3):
    c: PointOnObject(g0,g-2)
    c: DistanceY(g0) = -150
    c: Radius(g0) = 92
FEATURE [Part::Loft] Loft034  label="Loft046"
  Closed = false
  MaxDegree = 5
  Placement = pos=(0,0,-191.5) rot=(0,0,1;0rad)
  Ruled = false
  Sections = -> [Sketch113,Sketch112]
  Solid = true
FEATURE [Part::Cut] Cut076
  Base = -> Loft034
  Placement = pos=(0,0,32) rot=(0,0,1;0rad)
  Tool = -> Loft033
FEATURE [Sketcher::SketchObject] Sketch114
  FullyConstrained = true
  Placement = pos=(0,0,65) rot=(0,0,1;0rad)
  sketch-geometry (1):
    g0: Circle CenterX=0 CenterY=-150 CenterZ=0 NormalX=0 NormalY=0 NormalZ=1 AngleXU=0 Radius=100
  constraints (3):
    c: PointOnObject(g0,g-2)
    c: DistanceY(g0) = -150
    c: Radius(g0) = 100
FEATURE [Sketcher::SketchObject] Sketch115
  FullyConstrained = true
  Placement = pos=(0,0,80) rot=(0,0,1;0rad)
  sketch-geometry (1):
    g0: Circle CenterX=0 CenterY=-150 CenterZ=0 NormalX=0 NormalY=0 NormalZ=1 AngleXU=0 Radius=92
  constraints (3):
    c: PointOnObject(g0,g-2)
    c: DistanceY(g0) = -150
    c: Radius(g0) = 92
FEATURE [Part::Loft] Loft035  label="Loft047"
  Closed = false
  MaxDegree = 5
  Placement = pos=(0,0,-193.5) rot=(0,0,1;0rad)
  Ruled = false
  Sections = -> [Sketch115,Sketch114]
  Solid = true
FEATURE [Sketcher::SketchObject] Sketch116
  FullyConstrained = true
  Placement = pos=(0,0,65) rot=(0,0,1;0rad)
  sketch-geometry (1):
    g0: Circle CenterX=0 CenterY=-150 CenterZ=0 NormalX=0 NormalY=0 NormalZ=1 AngleXU=0 Radius=100
  constraints (3):
    c: PointOnObject(g0,g-2)
    c: DistanceY(g0) = -150
    c: Radius(g0) = 100
FEATURE [Sketcher::SketchObject] Sketch117
  FullyConstrained = true
  Placement = pos=(0,0,80) rot=(0,0,1;0rad)
  sketch-geometry (1):
    g0: Circle CenterX=0 CenterY=-150 CenterZ=0 NormalX=0 NormalY=0 NormalZ=1 AngleXU=0 Radius=92
  constraints (3):
    c: PointOnObject(g0,g-2)
    c: DistanceY(g0) = -150
    c: Radius(g0) = 92
FEATURE [Part::Loft] Loft036  label="Loft048"
  Closed = false
  MaxDegree = 5
  Placement = pos=(0,0,-191.5) rot=(0,0,1;0rad)
  Ruled = false
  Sections = -> [Sketch117,Sketch116]
  Solid = true
FEATURE [Part::Cut] Cut077
  Base = -> Loft036
  Placement = pos=(0,0,40) rot=(0,0,1;0rad)
  Tool = -> Loft035
FEATURE [Part::MultiFuse] Fusion119  label="fanCuts"
  Shapes = -> [Cut072,Cut073,Cut074,Cut075,Cut076,Cut077]
FEATURE [Sketcher::SketchObject] Sketch118
  FullyConstrained = true
  sketch-geometry (4):
    g0: LineSegment StartX=35 StartY=-45 StartZ=0 EndX=-35 EndY=-45 EndZ=0
    g1: LineSegment StartX=-35 StartY=-45 StartZ=0 EndX=-35 EndY=-265 EndZ=0
    g2: LineSegment StartX=-35 StartY=-265 StartZ=0 EndX=35 EndY=-265 EndZ=0
    g3: LineSegment StartX=35 StartY=-265 StartZ=0 EndX=35 EndY=-45 EndZ=0
  constraints (12):
    c: Coincident(g0,g1)
    c: Coincident(g1,g2)
    c: Coincident(g2,g3)
    c: Coincident(g3,g0)
    c: Horizontal(g0)
    c: Horizontal(g2)
    c: Vertical(g1)
    c: Vertical(g3)
    c: DistanceX(g2) = 35
    c: DistanceX(g1) = -35
    c: DistanceY(g1,g1) = 220
    c: DistanceY(g0) = -45
FEATURE [Part::Extrusion] Extrude043
  Base = -> Sketch118
  Dir = (0,0,1)
  DirMode = 2
  FaceMakerClass = Part::FaceMakerBullseye
  LengthFwd = 90
  LengthRev = 0
  Placement = pos=(0,0,-160) rot=(0,0,1;0rad)
  Solid = true
  Symmetric = false
FEATURE [Sketcher::SketchObject] Sketch119
  FullyConstrained = true
  Placement = pos=(0,0,65) rot=(0,0,1;0rad)
  sketch-geometry (1):
    g0: Circle CenterX=0 CenterY=-150 CenterZ=0 NormalX=0 NormalY=0 NormalZ=1 AngleXU=0 Radius=100
  constraints (3):
    c: PointOnObject(g0,g-2)
    c: DistanceY(g0) = -150
    c: Radius(g0) = 100
FEATURE [Sketcher::SketchObject] Sketch120
  FullyConstrained = true
  Placement = pos=(0,0,80) rot=(0,0,1;0rad)
  sketch-geometry (1):
    g0: Circle CenterX=0 CenterY=-150 CenterZ=0 NormalX=0 NormalY=0 NormalZ=1 AngleXU=0 Radius=92
  constraints (3):
    c: PointOnObject(g0,g-2)
    c: DistanceY(g0) = -150
    c: Radius(g0) = 92
FEATURE [Part::Loft] Loft037  label="Loft049"
  Closed = false
  MaxDegree = 5
  Placement = pos=(0,0,-193.5) rot=(0,0,1;0rad)
  Ruled = false
  Sections = -> [Sketch120,Sketch119]
  Solid = true
FEATURE [Sketcher::SketchObject] Sketch121
  FullyConstrained = true
  Placement = pos=(0,0,65) rot=(0,0,1;0rad)
  sketch-geometry (1):
    g0: Circle CenterX=0 CenterY=-150 CenterZ=0 NormalX=0 NormalY=0 NormalZ=1 AngleXU=0 Radius=100
  constraints (3):
    c: PointOnObject(g0,g-2)
    c: DistanceY(g0) = -150
    c: Radius(g0) = 100
FEATURE [Sketcher::SketchObject] Sketch122
  FullyConstrained = true
  Placement = pos=(0,0,80) rot=(0,0,1;0rad)
  sketch-geometry (1):
    g0: Circle CenterX=0 CenterY=-150 CenterZ=0 NormalX=0 NormalY=0 NormalZ=1 AngleXU=0 Radius=92
  constraints (3):
    c: PointOnObject(g0,g-2)
    c: DistanceY(g0) = -150
    c: Radius(g0) = 92
FEATURE [Part::Loft] Loft038  label="Loft050"
  Closed = false
  MaxDegree = 5
  Placement = pos=(0,0,-191.5) rot=(0,0,1;0rad)
  Ruled = false
  Sections = -> [Sketch122,Sketch121]
  Solid = true
FEATURE [Part::Cut] Cut078
  Base = -> Loft038
  Tool = -> Loft037
FEATURE [Sketcher::SketchObject] Sketch123
  FullyConstrained = true
  Placement = pos=(0,0,65) rot=(0,0,1;0rad)
  sketch-geometry (1):
    g0: Circle CenterX=0 CenterY=-150 CenterZ=0 NormalX=0 NormalY=0 NormalZ=1 AngleXU=0 Radius=100
  constraints (3):
    c: PointOnObject(g0,g-2)
    c: DistanceY(g0) = -150
    c: Radius(g0) = 100
FEATURE [Sketcher::SketchObject] Sketch124
  FullyConstrained = true
  Placement = pos=(0,0,80) rot=(0,0,1;0rad)
  sketch-geometry (1):
    g0: Circle CenterX=0 CenterY=-150 CenterZ=0 NormalX=0 NormalY=0 NormalZ=1 AngleXU=0 Radius=92
  constraints (3):
    c: PointOnObject(g0,g-2)
    c: DistanceY(g0) = -150
    c: Radius(g0) = 92
FEATURE [Part::Loft] Loft039  label="Loft051"
  Closed = false
  MaxDegree = 5
  Placement = pos=(0,0,-193.5) rot=(0,0,1;0rad)
  Ruled = false
  Sections = -> [Sketch124,Sketch123]
  Solid = true
FEATURE [Sketcher::SketchObject] Sketch125
  FullyConstrained = true
  Placement = pos=(0,0,65) rot=(0,0,1;0rad)
  sketch-geometry (1):
    g0: Circle CenterX=0 CenterY=-150 CenterZ=0 NormalX=0 NormalY=0 NormalZ=1 AngleXU=0 Radius=100
  constraints (3):
    c: PointOnObject(g0,g-2)
    c: DistanceY(g0) = -150
    c: Radius(g0) = 100
FEATURE [Sketcher::SketchObject] Sketch126
  FullyConstrained = true
  Placement = pos=(0,0,80) rot=(0,0,1;0rad)
  sketch-geometry (1):
    g0: Circle CenterX=0 CenterY=-150 CenterZ=0 NormalX=0 NormalY=0 NormalZ=1 AngleXU=0 Radius=92
  constraints (3):
    c: PointOnObject(g0,g-2)
    c: DistanceY(g0) = -150
    c: Radius(g0) = 92
FEATURE [Part::Loft] Loft040  label="Loft052"
  Closed = false
  MaxDegree = 5
  Placement = pos=(0,0,-191.5) rot=(0,0,1;0rad)
  Ruled = false
  Sections = -> [Sketch126,Sketch125]
  Solid = true
FEATURE [Part::Cut] Cut079
  Base = -> Loft040
  Placement = pos=(0,0,8) rot=(0,0,1;0rad)
  Tool = -> Loft039
FEATURE [Sketcher::SketchObject] Sketch127
  FullyConstrained = true
  Placement = pos=(0,0,65) rot=(0,0,1;0rad)
  sketch-geometry (1):
    g0: Circle CenterX=0 CenterY=-150 CenterZ=0 NormalX=0 NormalY=0 NormalZ=1 AngleXU=0 Radius=100
  constraints (3):
    c: PointOnObject(g0,g-2)
    c: DistanceY(g0) = -150
    c: Radius(g0) = 100
FEATURE [Sketcher::SketchObject] Sketch128
  FullyConstrained = true
  Placement = pos=(0,0,80) rot=(0,0,1;0rad)
  sketch-geometry (1):
    g0: Circle CenterX=0 CenterY=-150 CenterZ=0 NormalX=0 NormalY=0 NormalZ=1 AngleXU=0 Radius=92
  constraints (3):
    c: PointOnObject(g0,g-2)
    c: DistanceY(g0) = -150
    c: Radius(g0) = 92
FEATURE [Part::Loft] Loft041  label="Loft053"
  Closed = false
  MaxDegree = 5
  Placement = pos=(0,0,-193.5) rot=(0,0,1;0rad)
  Ruled = false
  Sections = -> [Sketch128,Sketch127]
  Solid = true
FEATURE [Sketcher::SketchObject] Sketch129
  FullyConstrained = true
  Placement = pos=(0,0,65) rot=(0,0,1;0rad)
  sketch-geometry (1):
    g0: Circle CenterX=0 CenterY=-150 CenterZ=0 NormalX=0 NormalY=0 NormalZ=1 AngleXU=0 Radius=100
  constraints (3):
    c: PointOnObject(g0,g-2)
    c: DistanceY(g0) = -150
    c: Radius(g0) = 100
FEATURE [Sketcher::SketchObject] Sketch130
  FullyConstrained = true
  Placement = pos=(0,0,80) rot=(0,0,1;0rad)
  sketch-geometry (1):
    g0: Circle CenterX=0 CenterY=-150 CenterZ=0 NormalX=0 NormalY=0 NormalZ=1 AngleXU=0 Radius=92
  constraints (3):
    c: PointOnObject(g0,g-2)
    c: DistanceY(g0) = -150
    c: Radius(g0) = 92
FEATURE [Part::Loft] Loft042  label="Loft054"
  Closed = false
  MaxDegree = 5
  Placement = pos=(0,0,-191.5) rot=(0,0,1;0rad)
  Ruled = false
  Sections = -> [Sketch130,Sketch129]
  Solid = true
FEATURE [Part::Cut] Cut080
  Base = -> Loft042
  Placement = pos=(0,0,16) rot=(0,0,1;0rad)
  Tool = -> Loft041
FEATURE [Sketcher::SketchObject] Sketch131
  FullyConstrained = true
  Placement = pos=(0,0,65) rot=(0,0,1;0rad)
  sketch-geometry (1):
    g0: Circle CenterX=0 CenterY=-150 CenterZ=0 NormalX=0 NormalY=0 NormalZ=1 AngleXU=0 Radius=100
  constraints (3):
    c: PointOnObject(g0,g-2)
    c: DistanceY(g0) = -150
    c: Radius(g0) = 100
FEATURE [Sketcher::SketchObject] Sketch132
  FullyConstrained = true
  Placement = pos=(0,0,80) rot=(0,0,1;0rad)
  sketch-geometry (1):
    g0: Circle CenterX=0 CenterY=-150 CenterZ=0 NormalX=0 NormalY=0 NormalZ=1 AngleXU=0 Radius=92
  constraints (3):
    c: PointOnObject(g0,g-2)
    c: DistanceY(g0) = -150
    c: Radius(g0) = 92
FEATURE [Part::Loft] Loft043  label="Loft055"
  Closed = false
  MaxDegree = 5
  Placement = pos=(0,0,-193.5) rot=(0,0,1;0rad)
  Ruled = false
  Sections = -> [Sketch132,Sketch131]
  Solid = true
FEATURE [Sketcher::SketchObject] Sketch133
  FullyConstrained = true
  Placement = pos=(0,0,65) rot=(0,0,1;0rad)
  sketch-geometry (1):
    g0: Circle CenterX=0 CenterY=-150 CenterZ=0 NormalX=0 NormalY=0 NormalZ=1 AngleXU=0 Radius=100
  constraints (3):
    c: PointOnObject(g0,g-2)
    c: DistanceY(g0) = -150
    c: Radius(g0) = 100
FEATURE [Sketcher::SketchObject] Sketch134
  FullyConstrained = true
  Placement = pos=(0,0,80) rot=(0,0,1;0rad)
  sketch-geometry (1):
    g0: Circle CenterX=0 CenterY=-150 CenterZ=0 NormalX=0 NormalY=0 NormalZ=1 AngleXU=0 Radius=92
  constraints (3):
    c: PointOnObject(g0,g-2)
    c: DistanceY(g0) = -150
    c: Radius(g0) = 92
FEATURE [Part::Loft] Loft044  label="Loft056"
  Closed = false
  MaxDegree = 5
  Placement = pos=(0,0,-191.5) rot=(0,0,1;0rad)
  Ruled = false
  Sections = -> [Sketch134,Sketch133]
  Solid = true
FEATURE [Part::Cut] Cut081
  Base = -> Loft044
  Placement = pos=(0,0,24) rot=(0,0,1;0rad)
  Tool = -> Loft043
FEATURE [Sketcher::SketchObject] Sketch135
  FullyConstrained = true
  Placement = pos=(0,0,65) rot=(0,0,1;0rad)
  sketch-geometry (1):
    g0: Circle CenterX=0 CenterY=-150 CenterZ=0 NormalX=0 NormalY=0 NormalZ=1 AngleXU=0 Radius=100
  constraints (3):
    c: PointOnObject(g0,g-2)
    c: DistanceY(g0) = -150
    c: Radius(g0) = 100
FEATURE [Sketcher::SketchObject] Sketch136
  FullyConstrained = true
  Placement = pos=(0,0,80) rot=(0,0,1;0rad)
  sketch-geometry (1):
    g0: Circle CenterX=0 CenterY=-150 CenterZ=0 NormalX=0 NormalY=0 NormalZ=1 AngleXU=0 Radius=92
  constraints (3):
    c: PointOnObject(g0,g-2)
    c: DistanceY(g0) = -150
    c: Radius(g0) = 92
FEATURE [Part::Loft] Loft045  label="Loft057"
  Closed = false
  MaxDegree = 5
  Placement = pos=(0,0,-193.5) rot=(0,0,1;0rad)
  Ruled = false
  Sections = -> [Sketch136,Sketch135]
  Solid = true
FEATURE [Sketcher::SketchObject] Sketch137
  FullyConstrained = true
  Placement = pos=(0,0,65) rot=(0,0,1;0rad)
  sketch-geometry (1):
    g0: Circle CenterX=0 CenterY=-150 CenterZ=0 NormalX=0 NormalY=0 NormalZ=1 AngleXU=0 Radius=100
  constraints (3):
    c: PointOnObject(g0,g-2)
    c: DistanceY(g0) = -150
    c: Radius(g0) = 100
FEATURE [Sketcher::SketchObject] Sketch138
  FullyConstrained = true
  Placement = pos=(0,0,80) rot=(0,0,1;0rad)
  sketch-geometry (1):
    g0: Circle CenterX=0 CenterY=-150 CenterZ=0 NormalX=0 NormalY=0 NormalZ=1 AngleXU=0 Radius=92
  constraints (3):
    c: PointOnObject(g0,g-2)
    c: DistanceY(g0) = -150
    c: Radius(g0) = 92
FEATURE [Part::Loft] Loft046  label="Loft058"
  Closed = false
  MaxDegree = 5
  Placement = pos=(0,0,-191.5) rot=(0,0,1;0rad)
  Ruled = false
  Sections = -> [Sketch138,Sketch137]
  Solid = true
FEATURE [Part::Cut] Cut082
  Base = -> Loft046
  Placement = pos=(0,0,32) rot=(0,0,1;0rad)
  Tool = -> Loft045
FEATURE [Sketcher::SketchObject] Sketch139
  FullyConstrained = true
  Placement = pos=(0,0,65) rot=(0,0,1;0rad)
  sketch-geometry (1):
    g0: Circle CenterX=0 CenterY=-150 CenterZ=0 NormalX=0 NormalY=0 NormalZ=1 AngleXU=0 Radius=100
  constraints (3):
    c: PointOnObject(g0,g-2)
    c: DistanceY(g0) = -150
    c: Radius(g0) = 100
FEATURE [Sketcher::SketchObject] Sketch140
  FullyConstrained = true
  Placement = pos=(0,0,80) rot=(0,0,1;0rad)
  sketch-geometry (1):
    g0: Circle CenterX=0 CenterY=-150 CenterZ=0 NormalX=0 NormalY=0 NormalZ=1 AngleXU=0 Radius=92
  constraints (3):
    c: PointOnObject(g0,g-2)
    c: DistanceY(g0) = -150
    c: Radius(g0) = 92
FEATURE [Part::Loft] Loft047  label="Loft059"
  Closed = false
  MaxDegree = 5
  Placement = pos=(0,0,-193.5) rot=(0,0,1;0rad)
  Ruled = false
  Sections = -> [Sketch140,Sketch139]
  Solid = true
FEATURE [Sketcher::SketchObject] Sketch141
  FullyConstrained = true
  Placement = pos=(0,0,65) rot=(0,0,1;0rad)
  sketch-geometry (1):
    g0: Circle CenterX=0 CenterY=-150 CenterZ=0 NormalX=0 NormalY=0 NormalZ=1 AngleXU=0 Radius=100
  constraints (3):
    c: PointOnObject(g0,g-2)
    c: DistanceY(g0) = -150
    c: Radius(g0) = 100
FEATURE [Sketcher::SketchObject] Sketch142
  FullyConstrained = true
  Placement = pos=(0,0,80) rot=(0,0,1;0rad)
  sketch-geometry (1):
    g0: Circle CenterX=0 CenterY=-150 CenterZ=0 NormalX=0 NormalY=0 NormalZ=1 AngleXU=0 Radius=92
  constraints (3):
    c: PointOnObject(g0,g-2)
    c: DistanceY(g0) = -150
    c: Radius(g0) = 92
FEATURE [Part::Loft] Loft048  label="Loft060"
  Closed = false
  MaxDegree = 5
  Placement = pos=(0,0,-191.5) rot=(0,0,1;0rad)
  Ruled = false
  Sections = -> [Sketch142,Sketch141]
  Solid = true
FEATURE [Part::Cut] Cut083
  Base = -> Loft048
  Placement = pos=(0,0,40) rot=(0,0,1;0rad)
  Tool = -> Loft047
FEATURE [Part::MultiFuse] Fusion120  label="fanCuts001"
  Placement = pos=(0,0,-32) rot=(0,0,1;0rad)
  Shapes = -> [Cut078,Cut079,Cut080,Cut081,Cut082,Cut083]
FEATURE [Part::MultiFuse] Fusion121
  Shapes = -> [Fusion120,Fusion119]
FEATURE [Part::Box] Box017  label="Cube010"
  AttacherType = Attacher::AttachEngine3D
  Height = 30
  Length = 42
  Placement = pos=(-21,-265,-152) rot=(0,0,1;0rad)
  Width = 100
FEATURE [Mesh::Feature] logoLightModule
  Placement = pos=(0.15,-236.25,-151) rot=(0,0,1;0rad)
FEATURE [Part::Cut] Cut084  label="fanCut"
  Base = -> Extrude043
  Tool = -> Box017
FEATURE [Part::MultiCommon] Common
  Shapes = -> [Fusion121,Cut084]
FEATURE [Part::Cut] Cut085  label="level3to4"
  Base = -> Cut056
  Tool = -> Common
FEATURE [Sketcher::SketchObject] Sketch143
  FullyConstrained = true
  sketch-geometry (2):
    g0: Circle CenterX=0 CenterY=-150 CenterZ=0 NormalX=0 NormalY=0 NormalZ=1 AngleXU=0 Radius=3.2
    g1: Circle CenterX=0 CenterY=-100 CenterZ=0 NormalX=0 NormalY=0 NormalZ=1 AngleXU=0 Radius=3.2
  constraints (6):
    c: PointOnObject(g0,g-2)
    c: PointOnObject(g1,g-2)
    c: DistanceY(g0) = -150
    c: DistanceY(g1) = -100
    c: Equal(g1,g0)
    c: Diameter(g1) = 6.4
FEATURE [Part::Extrusion] Extrude044
  Base = -> Sketch143
  Dir = (0,0,1)
  DirMode = 2
  FaceMakerClass = Part::FaceMakerBullseye
  LengthFwd = 50
  LengthRev = 0
  Placement = pos=(0,0,-290) rot=(0,0,1;0rad)
  Solid = true
  Symmetric = false
FEATURE [Part::Fillet] Fillet013  label="level4s002"
  Base = -> Cut039
  Edges = 10 edges r=2: [Edge45,Edge49,Edge52,Edge57,Edge60,Edge63,Edge69,Edge72,Edge77,Edge196]
FEATURE [Part::Box] Box018  label="tubeCut"
  AttacherType = Attacher::AttachEngine3D
  Height = 10
  Length = 108
  Placement = pos=(-54,-222,-65) rot=(0,0,1;0rad)
  Width = 145
FEATURE [Part::Cut] Cut087  label="level3to4s"
  Base = -> Cut085
  Tool = -> Box018
FEATURE [Part::Fillet] Fillet014
  Base = -> Cut045
  Edges = 1 edges r=2: [Edge22]
FEATURE [Part::Fillet] Fillet015  label="level3s001"
  Base = -> Fillet014
  Edges = 4 edges r=2: [Edge49,Edge55,Edge57,Edge58]
FEATURE [Part::Box] Box019  label="Cube011"
  AttacherType = Attacher::AttachEngine3D
  Height = 40
  Length = 40
  Placement = pos=(13.25,-219.25,-65) rot=(0,0,1;0rad)
  Width = 21
FEATURE [Part::Cut] Cut088  label="level3s002"
  Base = -> Fillet015
  Tool = -> Box019
FEATURE [Part::Fillet] Fillet016  label="level3s003"
  Base = -> Cut088
  Edges = 1 edges r=2: [Edge47]
FEATURE [Part::Fillet] Fillet017  label="level2s"
  Base = -> Cut034
  Edges = 32 edges r=1.5: [Edge42,Edge43,Edge44,Edge45,Edge46,Edge47,Edge48,Edge49,Edge53,Edge54,Edge55,Edge56,Edge57,Edge58,Edge59,Edge60,Edge61,Edge62,Edge63,Edge64,Edge66,Edge67,Edge68,Edge69,Edge74,Edge75,Edge76,Edge77,Edge78,Edge79,Edge80,Edge81]
FEATURE [Part::Box] Box020  label="Cube012"
  AttacherType = Attacher::AttachEngine3D
  Height = 20
  Length = 30
  Placement = pos=(-72,-155,80) rot=(0,0,1;0rad)
  Width = 10
FEATURE [Part::Box] Box021  label="Cube013"
  AttacherType = Attacher::AttachEngine3D
  Height = 25
  Length = 10
  Placement = pos=(-5,-109.35,75) rot=(0,0,1;0rad)
  Width = 20
FEATURE [Part::Cylinder] Cylinder172  label="refModuleHold004"
  Angle = 360
  AttacherType = Attacher::AttachEngine3D
  FirstAngle = 0
  Height = 32
  Placement = pos=(0,-207,80) rot=(0,0,1;0rad)
  Radius = 12
  SecondAngle = 0
FEATURE [Part::Cylinder] Cylinder173  label="refModules002"
  Angle = 360
  AttacherType = Attacher::AttachEngine3D
  FirstAngle = 0
  Height = 75
  Placement = pos=(0,-207,37) rot=(0,0,1;0rad)
  Radius = 3.75
  SecondAngle = 0
FEATURE [Part::Cylinder] Cylinder174  label="refModulesCoverCut003"
  Angle = 360
  AttacherType = Attacher::AttachEngine3D
  FirstAngle = 0
  Height = 60
  Placement = pos=(0,-207,37) rot=(0,0,1;0rad)
  Radius = 4.5
  SecondAngle = 0
FEATURE [Part::Cylinder] Cylinder175
  Angle = 360
  AttacherType = Attacher::AttachEngine3D
  FirstAngle = 0
  Height = 300
  Placement = pos=(0,0,90) rot=(1,0,0;1.5708rad)
  Radius = 2.8
  SecondAngle = 0
FEATURE [Part::Cylinder] Cylinder176
  Angle = 360
  AttacherType = Attacher::AttachEngine3D
  FirstAngle = 0
  Height = 300
  Placement = pos=(-150,-150,90) rot=(0.57735,0.57735,0.57735;2.0944rad)
  Radius = 2.8
  SecondAngle = 0
FEATURE [Part::Cylinder] Cylinder177
  Angle = 360
  AttacherType = Attacher::AttachEngine3D
  FirstAngle = 0
  Height = 10
  Placement = pos=(77.75,-150,90) rot=(0,1,0;1.5708rad)
  Radius = 2.8
  SecondAngle = 0
FEATURE [Part::MultiFuse] Fusion124  label="refModule001Cut001"
  Shapes = -> [Cylinder174,Cylinder173]
FEATURE [Part::Cut] Cut090  label="refModuleHold003"
  Base = -> Cylinder172
  Tool = -> Fusion124
FEATURE [Part::MultiFuse] Fusion127  label="m4Cuts023"
  Shapes = -> [Cylinder176,Cylinder175]
FEATURE [Sketcher::SketchObject] Sketch144
  FullyConstrained = true
  sketch-geometry (16):
    g0: Circle CenterX=-67 CenterY=-167.5 CenterZ=0 NormalX=0 NormalY=0 NormalZ=1 AngleXU=0 Radius=1.625
    g1: Circle CenterX=-47 CenterY=-167.5 CenterZ=0 NormalX=0 NormalY=0 NormalZ=1 AngleXU=0 Radius=1.625
    g2: Circle CenterX=-67 CenterY=-132.5 CenterZ=0 NormalX=0 NormalY=0 NormalZ=1 AngleXU=0 Radius=1.625
    g3: Circle CenterX=-47 CenterY=-132.5 CenterZ=0 NormalX=0 NormalY=0 NormalZ=1 AngleXU=0 Radius=1.625
    g4: LineSegment StartX=-62 StartY=-129.75 StartZ=0 EndX=-72 EndY=-129.75 EndZ=0
    g5: LineSegment StartX=-52 StartY=-129.75 StartZ=0 EndX=-42 EndY=-129.75 EndZ=0
    g6: LineSegment StartX=-72 StartY=-129.75 StartZ=0 EndX=-72 EndY=-170.25 EndZ=0
    g7: LineSegment StartX=-72 StartY=-170.25 StartZ=0 EndX=-62 EndY=-170.25 EndZ=0
    g8: LineSegment StartX=-62 StartY=-170.25 StartZ=0 EndX=-62 EndY=-155 EndZ=0
    g9: LineSegment StartX=-52 StartY=-155 StartZ=0 EndX=-52 EndY=-170.25 EndZ=0
    g10: LineSegment StartX=-52 StartY=-170.25 StartZ=0 EndX=-42 EndY=-170.25 EndZ=0
    g11: LineSegment StartX=-42 StartY=-170.25 StartZ=0 EndX=-42 EndY=-129.75 EndZ=0
    g12: LineSegment StartX=-62 StartY=-155 StartZ=0 EndX=-52 EndY=-155 EndZ=0
    g13: LineSegment StartX=-62 StartY=-129.75 StartZ=0 EndX=-62 EndY=-145 EndZ=0
    g14: LineSegment StartX=-62 StartY=-145 StartZ=0 EndX=-52 EndY=-145 EndZ=0
    g15: LineSegment StartX=-52 StartY=-145 StartZ=0 EndX=-52 EndY=-129.75 EndZ=0
  constraints (48):
    c: DistanceY(g2,g3) = 0
    c: DistanceX(g0,g2) = 0
    c: DistanceX(g1,g3) = 0
    c: DistanceX(g1) = -47
    c: DistanceY(g1) = -167.5
    c: DistanceX(g0,g1) = 20
    c: Horizontal(g4)
    c: Horizontal(g5)
    c: Vertical(g6)
    c: Coincident(g7,g6)
    c: Horizontal(g7)
    c: Coincident(g8,g7)
    c: Vertical(g9)
    c: Coincident(g10,g9)
    c: Horizontal(g10)
    c: Coincident(g11,g10)
    c: Vertical(g8)
    c: DistanceX(g4,g4) = 10
    c: DistanceX(g5,g5) = 10
    c: DistanceX(g6,g7) = 10
    c: DistanceX(g9,g10) = 10
    c: Vertical(g11)
    c: DistanceY(g7,g9) = 0
    c: DistanceY(g4,g5) = 0
    c: DistanceX(g6,g0) = 5
    c: DistanceX(g9,g1) = 5
    c: DistanceY(g2,g4) = 2.75
    c: Coincident(g4,g6)
    c: Coincident(g12,g8)
    c: Horizontal(g12)
    c: Coincident(g9,g12)
    c: Coincident(g13,g4)
    c: Vertical(g13)
    c: Coincident(g14,g13)
    c: Horizontal(g14)
    c: Coincident(g15,g14)
    c: Coincident(g15,g5)
    c: Vertical(g15)
    c: Coincident(g5,g11)
    c: DistanceY(g8,g13) = 10
    c: DistanceY(g13) = -145
    c: DistanceY(g7,g0) = 2.75
    c: Equal(g1,g0)
    c: Equal(g1,g2)
    c: Equal(g1,g3)
    c: Diameter(g1) = 3.25
    c: DistanceY(g1,g0) = 0
    c: DistanceY(g2) = -132.5
FEATURE [Part::Extrusion] Extrude045  label="as7265Holder002"
  Base = -> Sketch144
  Dir = (0,0,1)
  DirMode = 2
  FaceMakerClass = Part::FaceMakerBullseye
  LengthFwd = 10
  LengthRev = 0
  Placement = pos=(0,0,100) rot=(0,0,1;0rad)
  Solid = true
  Symmetric = false
FEATURE [Part::MultiFuse] Fusion122  label="as7265Holder003"
  Shapes = -> [Box020,Extrude045]
FEATURE [Sketcher::SketchObject] Sketch145
  FullyConstrained = true
  sketch-geometry (6):
    g0: Circle CenterX=74 CenterY=-167 CenterZ=0 NormalX=0 NormalY=0 NormalZ=1 AngleXU=0 Radius=1.65
    g1: Circle CenterX=40 CenterY=-167 CenterZ=0 NormalX=0 NormalY=0 NormalZ=1 AngleXU=0 Radius=1.65
    g2: Circle CenterX=40 CenterY=-133 CenterZ=0 NormalX=0 NormalY=0 NormalZ=1 AngleXU=0 Radius=1.65
    g3: Circle CenterX=74 CenterY=-133 CenterZ=0 NormalX=0 NormalY=0 NormalZ=1 AngleXU=0 Radius=1.65
    g4: Circle CenterX=57 CenterY=-150 CenterZ=0 NormalX=0 NormalY=0 NormalZ=1 AngleXU=0 Radius=27.5
    g5: Circle CenterX=57 CenterY=-150 CenterZ=0 NormalX=0 NormalY=0 NormalZ=1 AngleXU=0 Radius=21
  constraints (17):
    c: Equal(g3,g0)
    c: Equal(g3,g1)
    c: Equal(g3,g2)
    c: Diameter(g3) = 3.3
    c: DistanceX(g1) = 40
    c: DistanceY(g1) = -167
    c: DistanceY(g1,g0) = 0
    c: DistanceX(g2,g1) = 0
    c: DistanceY(g1,g2) = 34
    c: DistanceY(g2,g3) = 0
    c: DistanceX(g2,g3) = 34
    c: DistanceX(g0,g3) = 0
    c: Coincident(g5,g4)
    c: DistanceX(g4) = 57
    c: DistanceY(g4) = -150
    c: Diameter(g5) = 42
    c: Diameter(g4) = 55
FEATURE [Part::Extrusion] Extrude046  label="cameraHolder001"
  Base = -> Sketch145
  Dir = (0,0,1)
  DirMode = 2
  FaceMakerClass = Part::FaceMakerBullseye
  LengthFwd = 8.25
  LengthRev = 0
  Placement = pos=(0,0,80) rot=(0,0,1;0rad)
  Solid = true
  Symmetric = false
FEATURE [Sketcher::SketchObject] Sketch146
  FullyConstrained = true
  sketch-geometry (11):
    g0: Circle CenterX=6.5 CenterY=-83 CenterZ=0 NormalX=0 NormalY=0 NormalZ=1 AngleXU=0 Radius=1.125
    g1: Circle CenterX=10.15 CenterY=-91.65 CenterZ=0 NormalX=0 NormalY=0 NormalZ=1 AngleXU=0 Radius=1.125
    g2: Circle CenterX=10.15 CenterY=-104.35 CenterZ=0 NormalX=0 NormalY=0 NormalZ=1 AngleXU=0 Radius=1.125
    g3: Circle CenterX=-10.15 CenterY=-104.35 CenterZ=0 NormalX=0 NormalY=0 NormalZ=1 AngleXU=0 Radius=1.125
    g4: Circle CenterX=-10.15 CenterY=-91.65 CenterZ=0 NormalX=0 NormalY=0 NormalZ=1 AngleXU=0 Radius=1.125
    g5: ArcOfCircle CenterX=-9.5 CenterY=-78 CenterZ=0 NormalX=0 NormalY=0 NormalZ=1 AngleXU=0 Radius=9.5 StartAngle=4.71239 EndAngle=6.28319
    g6: LineSegment StartX=-9.5 StartY=-87.5 StartZ=0 EndX=-15.15 EndY=-87.5 EndZ=0
    g7: LineSegment StartX=-15.15 StartY=-87.5 StartZ=0 EndX=-15.15 EndY=-109.35 EndZ=0
    g8: LineSegment StartX=-15.15 StartY=-109.35 StartZ=0 EndX=15.15 EndY=-109.35 EndZ=0
    g9: LineSegment StartX=15.15 StartY=-109.35 StartZ=0 EndX=15.15 EndY=-78 EndZ=0
    g10: LineSegment StartX=15.15 StartY=-78 StartZ=0 EndX=0 EndY=-78 EndZ=0
  constraints (34):
    c: DistanceX(g4,g3) = 0
    c: DistanceX(g2,g1) = 0
    c: Equal(g2,g3)
    c: Equal(g2,g4)
    c: Equal(g2,g1)
    c: Equal(g2,g0)
    c: Diameter(g2) = 2.25
    c: DistanceX(g2) = 10.15
    c: DistanceY(g2) = -104.35
    c: DistanceY(g2,g1) = 12.7
    c: DistanceY(g3,g2) = 0
    c: DistanceX(g3,g2) = 20.3
    c: DistanceY(g4,g1) = 0
    c: DistanceY(g0) = -83
    c: DistanceX(g0) = 6.5
    c: PointOnObject(g5,g-2)
    c: Coincident(g6,g5)
    c: Horizontal(g6)
    c: Coincident(g7,g6)
    c: Vertical(g7)
    c: Coincident(g8,g7)
    c: Horizontal(g8)
    c: Coincident(g9,g8)
    c: Vertical(g9)
    c: Coincident(g10,g9)
    c: Coincident(g10,g5)
    c: Horizontal(g10)
    c: DistanceY(g5) = -78
    c: DistanceY(g5,g5) = 0
    c: DistanceX(g5,g5) = 9.5
    c: DistanceX(g5,g5) = 0
    c: DistanceX(g1,g9) = 5
    c: DistanceX(g7,g3) = 5
    c: DistanceY(g7,g3) = 5
FEATURE [Part::Extrusion] Extrude047  label="uvHolder002"
  Base = -> Sketch146
  Dir = (0,0,1)
  DirMode = 2
  FaceMakerClass = Part::FaceMakerBullseye
  LengthFwd = 10
  LengthRev = 0
  Placement = pos=(0,0,100) rot=(0,0,1;0rad)
  Solid = true
  Symmetric = false
FEATURE [Part::MultiFuse] Fusion123  label="uvHolder003"
  Shapes = -> [Box021,Extrude047]
FEATURE [Sketcher::SketchObject] Sketch147  label="top024"
  FullyConstrained = true
  sketch-geometry (15):
    g0: Circle CenterX=0 CenterY=-150 CenterZ=0 NormalX=0 NormalY=0 NormalZ=1 AngleXU=0 Radius=85
    g1: Circle CenterX=-57 CenterY=-115 CenterZ=0 NormalX=0 NormalY=0 NormalZ=1 AngleXU=0 Radius=2.13
    g2: Circle CenterX=-22 CenterY=-150 CenterZ=0 NormalX=0 NormalY=0 NormalZ=1 AngleXU=0 Radius=4
    g3: Circle CenterX=-57 CenterY=-185 CenterZ=0 NormalX=0 NormalY=0 NormalZ=1 AngleXU=0 Radius=2.13
    g4: Circle CenterX=0 CenterY=-172 CenterZ=0 NormalX=0 NormalY=0 NormalZ=1 AngleXU=0 Radius=4
    g5: Circle CenterX=-35 CenterY=-207 CenterZ=0 NormalX=0 NormalY=0 NormalZ=1 AngleXU=0 Radius=2.13
    g6: Circle CenterX=35 CenterY=-207 CenterZ=0 NormalX=0 NormalY=0 NormalZ=1 AngleXU=0 Radius=2.13
    g7: Circle CenterX=57 CenterY=-185 CenterZ=0 NormalX=0 NormalY=0 NormalZ=1 AngleXU=0 Radius=2.13
    g8: Circle CenterX=22 CenterY=-150 CenterZ=0 NormalX=0 NormalY=0 NormalZ=1 AngleXU=0 Radius=4
    g9: Circle CenterX=57 CenterY=-115 CenterZ=0 NormalX=0 NormalY=0 NormalZ=1 AngleXU=0 Radius=2.13
    g10: Circle CenterX=0 CenterY=-207 CenterZ=0 NormalX=0 NormalY=0 NormalZ=1 AngleXU=0 Radius=4.5
    g11: Circle CenterX=57 CenterY=-150 CenterZ=0 NormalX=0 NormalY=0 NormalZ=1 AngleXU=0 Radius=21
    g12: Circle CenterX=-35 CenterY=-93 CenterZ=0 NormalX=0 NormalY=0 NormalZ=1 AngleXU=0 Radius=2.13
    g13: Circle CenterX=35 CenterY=-93 CenterZ=0 NormalX=0 NormalY=0 NormalZ=1 AngleXU=0 Radius=2.13
    g14: Circle CenterX=0 CenterY=-128 CenterZ=0 NormalX=0 NormalY=0 NormalZ=1 AngleXU=0 Radius=4
  constraints (45):
    c: Radius(g0) = 85
    c: DistanceY(g0) = -150
    c: DistanceY(g8,g0) = 0
    c: DistanceY(g0,g2) = 0
    c: Radius(g11) = 21
    c: DistanceX(g10,g0) = 0
    c: DistanceX(g0,g11) = 57
    c: DistanceY(g11,g0) = 0
    c: DistanceX(g0,g8) = 22
    c: DistanceX(g2,g0) = 22
    c: DistanceX(g5,g10) = 35
    c: DistanceX(g10,g6) = 35
    c: DistanceX(g7,g11) = 0
    c: DistanceX(g11,g9) = 0
    c: DistanceX(g1,g0) = 57
    c: DistanceY(g3,g0) = 35
    c: DistanceY(g0,g1) = 35
    c: DistanceY(g10,g4) = 35
    c: DistanceY(g6,g10) = 0
    c: DistanceY(g10,g5) = 0
    c: DistanceY(g7,g11) = 35
    c: DistanceY(g11,g9) = 35
    c: DistanceX(g3,g1) = 0
    c: DistanceY(g10,g0) = 57
    c: Diameter(g10) = 9
    c: DistanceX(g12) = -35
    c: DistanceX(g13) = 35
    c: DistanceY(g0,g14) = 22
    c: DistanceX(g0) = 0
    c: DistanceX(g4) = 0
    c: DistanceX(g14) = 0
    c: DistanceY(g0,g13) = 57
    c: DistanceY(g0,g12) = 57
    c: Equal(g5,g6)
    c: Equal(g5,g7)
    c: Equal(g5,g9)
    c: Equal(g5,g13)
    c: Equal(g5,g12)
    c: Equal(g5,g1)
    c: Equal(g5,g3)
    c: Radius(g5) = 2.13
    c: Equal(g4,g8)
    c: Equal(g4,g14)
    c: Equal(g4,g2)
    c: Diameter(g4) = 8
FEATURE [Part::Extrusion] Extrude048  label="level006"
  Base = -> Sketch147
  Dir = (0,0,1)
  DirMode = 2
  FaceMakerClass = Part::FaceMakerBullseye
  LengthFwd = 5
  LengthRev = 0
  Placement = pos=(0,0,75) rot=(0,0,1;0rad)
  Solid = true
  Symmetric = false
FEATURE [Sketcher::SketchObject] Sketch148
  FullyConstrained = true
  sketch-geometry (6):
    g0: Circle CenterX=0 CenterY=-150 CenterZ=0 NormalX=0 NormalY=0 NormalZ=1 AngleXU=0 Radius=17.5
    g1: Circle CenterX=-10.15 CenterY=-140.15 CenterZ=0 NormalX=0 NormalY=0 NormalZ=1 AngleXU=0 Radius=1.65
    g2: Circle CenterX=10.15 CenterY=-140.15 CenterZ=0 NormalX=0 NormalY=0 NormalZ=1 AngleXU=0 Radius=1.65
    g3: Circle CenterX=10.15 CenterY=-160.45 CenterZ=0 NormalX=0 NormalY=0 NormalZ=1 AngleXU=0 Radius=1.65
    g4: Circle CenterX=-10.15 CenterY=-160.45 CenterZ=0 NormalX=0 NormalY=0 NormalZ=1 AngleXU=0 Radius=1.65
    g5: Circle CenterX=0 CenterY=-150 CenterZ=0 NormalX=0 NormalY=0 NormalZ=1 AngleXU=0 Radius=11
  constraints (17):
    c: DistanceY(g0) = -150
    c: DistanceX(g0) = 0
    c: Radius(g0) = 17.5
    c: Equal(g4,g3)
    c: Equal(g4,g2)
    c: Equal(g4,g1)
    c: Diameter(g4) = 3.3
    c: DistanceX(g1,g4) = 0
    c: DistanceY(g2,g1) = 0
    c: DistanceY(g3,g4) = 0
    c: DistanceX(g2,g3) = 0
    c: DistanceY(g4,g0) = 10.45
    c: DistanceY(g0,g1) = 9.85
    c: DistanceX(g3) = 10.15
    c: DistanceX(g4) = -10.15
    c: Coincident(g5,g0)
    c: Diameter(g5) = 22
FEATURE [Part::Extrusion] Extrude049  label="gpsHolder001"
  Base = -> Sketch148
  Dir = (0,0,1)
  DirMode = 2
  FaceMakerClass = Part::FaceMakerBullseye
  LengthFwd = 15
  LengthRev = 0
  Placement = pos=(0,0,80) rot=(0,0,1;0rad)
  Solid = true
  Symmetric = false
FEATURE [Sketcher::SketchObject] Sketch149
  FullyConstrained = true
  Placement = pos=(0,0,0) rot=(1,0,0;1.5708rad)
  sketch-geometry (1):
    g0: Circle CenterX=0 CenterY=102.5 CenterZ=0 NormalX=0 NormalY=0 NormalZ=1 AngleXU=0 Radius=2
  constraints (3):
    c: PointOnObject(g0,g-2)
    c: DistanceY(g0) = 102.5
    c: Diameter(g0) = 4
FEATURE [Part::Extrusion] Extrude050  label="m3HeatSetInsertCut001"
  Base = -> Sketch149
  Dir = (0,-1,-3e-16)
  DirMode = 2
  FaceMakerClass = Part::FaceMakerBullseye
  LengthFwd = 50
  LengthRev = 0
  Placement = pos=(0,-183.25,0) rot=(0,0,1;0rad)
  Solid = true
  Symmetric = false
FEATURE [Part::Cut] Cut091  label="refSensorHoldLev002"
  Base = -> Cut090
  Tool = -> Extrude050
FEATURE [Part::MultiFuse] Fusion125  label="level1SensorHolds001"
  Shapes = -> [Fusion123,Cut091,Extrude049,Fusion122,Extrude046]
FEATURE [Part::MultiFuse] Fusion126  label="level001x001"
  Shapes = -> [Fusion125,Extrude048]
FEATURE [Sketcher::SketchObject] Sketch150
  FullyConstrained = true
  sketch-geometry (16):
    g0: ArcOfCircle CenterX=0 CenterY=-150 CenterZ=0 NormalX=0 NormalY=0 NormalZ=1 AngleXU=0 Radius=85 StartAngle=2.84306 EndAngle=3.44012
    g1: ArcOfCircle CenterX=0 CenterY=-150 CenterZ=0 NormalX=0 NormalY=0 NormalZ=1 AngleXU=0 Radius=85 StartAngle=1.27226 EndAngle=1.86933
    g2: ArcOfCircle CenterX=0 CenterY=-150 CenterZ=0 NormalX=0 NormalY=0 NormalZ=1 AngleXU=0 Radius=85 StartAngle=5.98465 EndAngle=6.58172
    g3: ArcOfCircle CenterX=0 CenterY=-150 CenterZ=0 NormalX=0 NormalY=0 NormalZ=1 AngleXU=0 Radius=85 StartAngle=4.41386 EndAngle=5.01092
    g4: ArcOfCircle CenterX=0 CenterY=-150 CenterZ=0 NormalX=0 NormalY=0 NormalZ=1 AngleXU=0 Radius=79 StartAngle=1.24881 EndAngle=1.89279
    g5: ArcOfCircle CenterX=0 CenterY=-150 CenterZ=0 NormalX=0 NormalY=0 NormalZ=1 AngleXU=0 Radius=79 StartAngle=5.96119 EndAngle=6.60518
    g6: ArcOfCircle CenterX=0 CenterY=-150 CenterZ=0 NormalX=0 NormalY=0 NormalZ=1 AngleXU=0 Radius=79 StartAngle=2.8196 EndAngle=3.46358
    g7: ArcOfCircle CenterX=0 CenterY=-150 CenterZ=0 NormalX=0 NormalY=0 NormalZ=1 AngleXU=0 Radius=79 StartAngle=4.3904 EndAngle=5.03438
    g8: LineSegment StartX=25 StartY=-68.7596 StartZ=0 EndX=25 EndY=-75.06 EndZ=0
    g9: LineSegment StartX=-25 StartY=-68.7596 StartZ=0 EndX=-25 EndY=-75.06 EndZ=0
    g10: LineSegment StartX=-81.2404 StartY=-125 StartZ=0 EndX=-74.94 EndY=-125 EndZ=0
    g11: LineSegment StartX=-81.2404 StartY=-175 StartZ=0 EndX=-74.94 EndY=-175 EndZ=0
    g12: LineSegment StartX=-25 StartY=-231.24 StartZ=0 EndX=-25 EndY=-224.94 EndZ=0
    g13: LineSegment StartX=25 StartY=-231.24 StartZ=0 EndX=25 EndY=-224.94 EndZ=0
    g14: LineSegment StartX=81.2404 StartY=-175 StartZ=0 EndX=74.94 EndY=-175 EndZ=0
    g15: LineSegment StartX=81.2404 StartY=-125 StartZ=0 EndX=74.94 EndY=-125 EndZ=0
  constraints (49):
    c: PointOnObject(g0,g-2)
    c: Coincident(g1,g0)
    c: Coincident(g2,g0)
    c: Coincident(g3,g0)
    c: DistanceY(g0) = -150
    c: Coincident(g4,g0)
    c: Coincident(g5,g0)
    c: Coincident(g6,g0)
    c: Coincident(g7,g0)
    c: DistanceX(g4,g0) = 25
    c: DistanceX(g1,g4) = 0
    c: DistanceX(g0,g4) = 25
    c: DistanceX(g4,g1) = 0
    c: DistanceY(g0,g5) = 25
    c: DistanceY(g5,g2) = 0
    c: DistanceY(g2,g0) = 25
    c: DistanceY(g2,g5) = 0
    c: DistanceY(g6,g0) = 25
    c: DistanceY(g0,g6) = 0
    c: DistanceY(g0,g6) = 25
    c: DistanceY(g6,g0) = 0
    c: Equal(g1,g2)
    c: Equal(g1,g3)
    c: Equal(g1,g0)
    c: Radius(g1) = 85  'outer'
    c: Equal(g6,g4)
    c: Equal(g6,g5)
    c: Equal(g6,g7)
    c: Radius(g6) = 79
    c: DistanceX(g0,g7) = 25
    c: DistanceX(g7,g3) = 0
    c: DistanceX(g3) = -25
    c: DistanceX(g3,g7) = 0
    c: Coincident(g8,g1)
    c: Coincident(g8,g4)
    c: Coincident(g9,g1)
    c: Coincident(g9,g4)
    c: Coincident(g10,g0)
    c: Coincident(g10,g6)
    c: Coincident(g11,g0)
    c: Coincident(g11,g6)
    c: Coincident(g12,g3)
    c: Coincident(g12,g7)
    c: Coincident(g13,g3)
    c: Coincident(g13,g7)
    c: Coincident(g14,g2)
    c: Coincident(g14,g5)
    c: Coincident(g15,g2)
    c: Coincident(g15,g5)
FEATURE [Part::Extrusion] Extrude051  label="srsHolds004"
  Base = -> Sketch150
  Dir = (0,0,1)
  DirMode = 2
  FaceMakerClass = Part::FaceMakerBullseye
  LengthFwd = 20
  LengthRev = 0
  Placement = pos=(0,0,75) rot=(0,0,1;0rad)
  Solid = true
  Symmetric = false
FEATURE [Part::Cut] Cut092  label="srsHold001"
  Base = -> Extrude051
  Tool = -> Fusion127
FEATURE [Part::MultiFuse] Fusion128  label="level007"
  Shapes = -> [Cut092,Fusion126]
FEATURE [Part::Fillet] Fillet019
  Base = -> Fusion128
  Edges = 7 edges r=2: [Edge91,Edge95,Edge103,Edge105,Edge106,Edge110,Edge111]
FEATURE [Part::Cut] Cut093  label="level1sOriginal"
  Base = -> Fillet019
  Tool = -> Cylinder177
FEATURE [Part::Cylinder] Cylinder178  label="levelOneCut"
  Angle = 360
  AttacherType = Attacher::AttachEngine3D
  FirstAngle = 0
  Height = 10
  Placement = pos=(77.75,-150,90) rot=(0,1,0;1.5708rad)
  Radius = 2.8
  SecondAngle = 0
FEATURE [Part::Feature] Feature002  label="PG7s"
  Placement = pos=(30,-120,70) rot=(0,0,1;0rad)
  shape: bbox 21.32 x 20.97 x 29.79 mm, 246 faces, 3 solids (baked)
FEATURE [Part::Feature] Feature003  label="PG7s001"
  Placement = pos=(-30,-120,70) rot=(0,0,1;0rad)
  shape: bbox 21.32 x 20.97 x 29.79 mm, 246 faces, 3 solids (baked)
FEATURE [Sketcher::SketchObject] Sketch151
  FullyConstrained = true
  Placement = pos=(0,0,78) rot=(0,0,1;0rad)
  sketch-geometry (14):
    g0: LineSegment StartX=-24.2265 StartY=-130 StartZ=0 EndX=-18.453 EndY=-120 EndZ=0
    g1: LineSegment StartX=-18.453 StartY=-120 StartZ=0 EndX=-24.2265 EndY=-110 EndZ=0
    g2: LineSegment StartX=-24.2265 StartY=-110 StartZ=0 EndX=-35.7735 EndY=-110 EndZ=0
    g3: LineSegment StartX=-35.7735 StartY=-110 StartZ=0 EndX=-41.547 EndY=-120 EndZ=0
    g4: LineSegment StartX=-41.547 StartY=-120 StartZ=0 EndX=-35.7735 EndY=-130 EndZ=0
    g5: LineSegment StartX=-35.7735 StartY=-130 StartZ=0 EndX=-24.2265 EndY=-130 EndZ=0
    g6: Circle CenterX=-30 CenterY=-120 CenterZ=0 NormalX=0 NormalY=0 NormalZ=1 AngleXU=0 Radius=11.547
    g7: LineSegment StartX=41.547 StartY=-120 StartZ=0 EndX=35.7735 EndY=-110 EndZ=0
    g8: LineSegment StartX=35.7735 StartY=-110 StartZ=0 EndX=24.2265 EndY=-110 EndZ=0
    g9: LineSegment StartX=24.2265 StartY=-110 StartZ=0 EndX=18.453 EndY=-120 EndZ=0
    g10: LineSegment StartX=18.453 StartY=-120 StartZ=0 EndX=24.2265 EndY=-130 EndZ=0
    g11: LineSegment StartX=24.2265 StartY=-130 StartZ=0 EndX=35.7735 EndY=-130 EndZ=0
    g12: LineSegment StartX=35.7735 StartY=-130 StartZ=0 EndX=41.547 EndY=-120 EndZ=0
    g13: Circle CenterX=30 CenterY=-120 CenterZ=0 NormalX=0 NormalY=0 NormalZ=1 AngleXU=0 Radius=11.547
  constraints (34):
    c: Coincident(g0,g1)
    c: Coincident(g1,g2)
    c: Coincident(g2,g3)
    c: Coincident(g3,g4)
    c: Coincident(g4,g5)
    c: Coincident(g5,g0)
    c: Equal(g0, g1-g5) x5
    c: PointOnObject(g0,g6)
    c: PointOnObject(g1,g6)
    c: PointOnObject(g2,g6)
    c: PointOnObject(g3,g6)
    c: PointOnObject(g4,g6)
    c: PointOnObject(g5,g6)
    c: Coincident(g7,g8)
    c: Coincident(g8,g9)
    c: Coincident(g9,g10)
    c: Coincident(g10,g11)
    c: Coincident(g11,g12)
    c: Coincident(g12,g7)
    c: Equal(g7, g8-g12) x5
    c: PointOnObject(g7,g13)
    c: PointOnObject(g8,g13)
    c: PointOnObject(g9,g13)
    c: PointOnObject(g10,g13)
    c: PointOnObject(g11,g13)
    c: PointOnObject(g12,g13)
    c: DistanceY(g6) = -120
    c: DistanceX(g6) = -30
    c: DistanceY(g4,g6) = 10
    c: DistanceX(g4,g2) = 0
    c: DistanceY(g13,g6) = 0
    c: DistanceX(g13) = 30
    c: DistanceX(g10,g8) = 0
    c: DistanceY(g10,g13) = 10
FEATURE [Part::Extrusion] Extrude052  label="pg7Cuts"
  Base = -> Sketch151
  Dir = (0,0,1)
  DirMode = 2
  FaceMakerClass = Part::FaceMakerBullseye
  LengthFwd = 3
  LengthRev = 0
  Solid = true
  Symmetric = false
FEATURE [Part::MultiFuse] Fusion129  label="level1Cuts"
  Shapes = -> [Extrude052,Cylinder178]
FEATURE [Part::Cut] Cut094  label="level01"
  Base = -> Fusion069
  Tool = -> Fusion129
FEATURE [Part::Fillet] Fillet020
  Base = -> Cut094
  Edges = 1 edges r=2: [Edge40]
FEATURE [Part::Fillet] Fillet021
  Base = -> Fillet020
  Edges = 10 edges r=2: [Edge42,Edge43,Edge44,Edge45,Edge46,Edge53,Edge54,Edge55,Edge56,Edge57]
FEATURE [Part::Fillet] Fillet022
  Base = -> Fillet021
  Edges = 11 edges: [Edge203 r=1,Edge204 r=2,Edge205 r=1,Edge248 r=2,Edge249 r=1,Edge250 r=2,Edge251 r=1,Edge252 r=2,Edge253 r=2,Edge254 r=1,Edge255 r=2]
FEATURE [Part::Fillet] Fillet023  label="level01s"
  Base = -> Fillet022
  Edges = 25 edges: [Edge155 r=2,Edge229 r=1,Edge230 r=1,Edge231 r=1,Edge237 r=1,Edge238 r=1,Edge239 r=1,Edge244 r=1,Edge245 r=1,Edge246 r=1,Edge251 r=1,Edge252 r=1,Edge253 r=1,Edge273 r=1,Edge274 r=1,Edge275 r=1,Edge276 r=1,Edge277 r=1,Edge278 r=1,Edge279 r=1,Edge280 r=1,Edge281 r=1,Edge286 r=1,Edge288 r=1,Edge290 r=1]
FEATURE [Part::Cylinder] Cylinder179
  Angle = 360
  AttacherType = Attacher::AttachEngine3D
  FirstAngle = 0
  Height = 300
  Placement = pos=(0,0,90) rot=(1,0,0;1.5708rad)
  Radius = 2.8
  SecondAngle = 0
FEATURE [Part::Cylinder] Cylinder180
  Angle = 360
  AttacherType = Attacher::AttachEngine3D
  FirstAngle = 0
  Height = 300
  Placement = pos=(-150,-150,90) rot=(0.57735,0.57735,0.57735;2.0944rad)
  Radius = 2.8
  SecondAngle = 0
FEATURE [Part::MultiFuse] Fusion131  label="m4HeatSetCuts004"
  Placement = pos=(0,0,-321) rot=(0,0,1;0rad)
  Shapes = -> [Cylinder180,Cylinder179]
FEATURE [Sketcher::SketchObject] Sketch152  label="top025"
  FullyConstrained = true
  sketch-geometry (9):
    g0: Circle CenterX=0 CenterY=-150 CenterZ=0 NormalX=0 NormalY=0 NormalZ=1 AngleXU=0 Radius=93
    g1: Circle CenterX=-57 CenterY=-150 CenterZ=0 NormalX=0 NormalY=0 NormalZ=1 AngleXU=0 Radius=11
    g2: Circle CenterX=57 CenterY=-150 CenterZ=0 NormalX=0 NormalY=0 NormalZ=1 AngleXU=0 Radius=15.1
    g3: Circle CenterX=35 CenterY=-200 CenterZ=0 NormalX=0 NormalY=0 NormalZ=1 AngleXU=0 Radius=15.1
    g4: Circle CenterX=-35 CenterY=-200 CenterZ=0 NormalX=0 NormalY=0 NormalZ=1 AngleXU=0 Radius=6.4
    g5: ArcOfCircle CenterX=0 CenterY=-220 CenterZ=0 NormalX=0 NormalY=0 NormalZ=1 AngleXU=0 Radius=5 StartAngle=2.26529 EndAngle=7.15948
    g6: ArcOfCircle CenterX=0 CenterY=-212.5 CenterZ=0 NormalX=0 NormalY=0 NormalZ=1 AngleXU=0 Radius=3.2 StartAngle=3e-15 EndAngle=3.14159
    g7: LineSegment StartX=-3.2 StartY=-212.5 StartZ=0 EndX=-3.2 EndY=-216.158 EndZ=0
    g8: LineSegment StartX=3.2 StartY=-216.158 StartZ=0 EndX=3.2 EndY=-212.5 EndZ=0
  constraints (29):
    c: PointOnObject(g0,g-2)
    c: Radius(g0) = 93
    c: DistanceY(g0) = -150
    c: Radius(g1) = 11
    c: DistanceX(g0,g1) = -57
    c: DistanceY(g1,g0) = 0
    c: DistanceY(g1,g2) = 0
    c: DistanceX(g0,g2) = 57
    c: DistanceX(g3) = 35
    c: DistanceY(g3,g0) = 50
    c: DistanceY(g3,g4) = 0
    c: DistanceX(g4,g0) = 35
    c: Radius(g4) = 6.4
    c: Equal(g2,g3)
    c: Radius(g2) = 15.1
    c: PointOnObject(g5,g-2)
    c: PointOnObject(g6,g-2)
    c: DistanceY(g5,g0) = 70
    c: DistanceX(g5,g6) = 0
    c: DistanceX(g6,g5) = 0
    c: Coincident(g7,g6)
    c: Coincident(g7,g5)
    c: Coincident(g8,g5)
    c: Coincident(g8,g6)
    c: DistanceX(g5,g5) = 6.4
    c: DistanceY(g5,g6) = 7.5
    c: DistanceY(g6,g6) = 0
    c: DistanceY(g6,g6) = 0
    c: Radius(g5) = 5
FEATURE [Part::Extrusion] Extrude053  label="level008"
  Base = -> Sketch152
  Dir = (0,0,1)
  DirMode = 2
  FaceMakerClass = Part::FaceMakerBullseye
  LengthFwd = 8
  LengthRev = 0
  Placement = pos=(0,0,-250) rot=(0,0,1;0rad)
  Solid = true
  Symmetric = false
FEATURE [Sketcher::SketchObject] Sketch153
  FullyConstrained = true
  sketch-geometry (4):
    g0: ArcOfCircle CenterX=0 CenterY=-220 CenterZ=0 NormalX=0 NormalY=0 NormalZ=1 AngleXU=0 Radius=5 StartAngle=3.14159 EndAngle=6.28319
    g1: ArcOfCircle CenterX=-1.2e-15 CenterY=-212.5 CenterZ=0 NormalX=0 NormalY=0 NormalZ=1 AngleXU=0 Radius=5 StartAngle=1.419e-13 EndAngle=3.14159
    g2: LineSegment StartX=5 StartY=-220 StartZ=0 EndX=5 EndY=-212.5 EndZ=0
    g3: LineSegment StartX=-5 StartY=-212.5 StartZ=0 EndX=-5 EndY=-220 EndZ=0
  constraints (10):
    c: Tangent(g0,g2) = -1.5708
    c: Tangent(g2,g1) = -1.5708
    c: Tangent(g1,g3) = -1.5708
    c: Tangent(g3,g0) = -1.5708
    c: Equal(g0,g1)
    c: Vertical(g2)
    c: DistanceX(g0) = 0
    c: DistanceY(g0) = -220
    c: Radius(g0) = 5
    c: DistanceY(g0,g1) = 7.5
FEATURE [Part::Extrusion] Extrude054  label="micCutLevel006"
  Base = -> Sketch153
  Dir = (0,0,1)
  DirMode = 2
  FaceMakerClass = Part::FaceMakerBullseye
  LengthFwd = 10
  LengthRev = 0
  Placement = pos=(0,0,-246.5) rot=(0,0,1;0rad)
  Solid = true
  Symmetric = false
FEATURE [Sketcher::SketchObject] Sketch154
  FullyConstrained = true
  sketch-geometry (16):
    g0: ArcOfCircle CenterX=0 CenterY=-150 CenterZ=0 NormalX=0 NormalY=0 NormalZ=1 AngleXU=0 Radius=93 StartAngle=2.86943 EndAngle=3.41376
    g1: ArcOfCircle CenterX=0 CenterY=-150 CenterZ=0 NormalX=0 NormalY=0 NormalZ=1 AngleXU=0 Radius=93 StartAngle=1.29863 EndAngle=1.84296
    g2: ArcOfCircle CenterX=0 CenterY=-150 CenterZ=0 NormalX=0 NormalY=0 NormalZ=1 AngleXU=0 Radius=93 StartAngle=6.01102 EndAngle=6.55535
    g3: ArcOfCircle CenterX=0 CenterY=-150 CenterZ=0 NormalX=0 NormalY=0 NormalZ=1 AngleXU=0 Radius=93 StartAngle=4.44022 EndAngle=4.98455
    g4: ArcOfCircle CenterX=0 CenterY=-150 CenterZ=0 NormalX=0 NormalY=0 NormalZ=1 AngleXU=0 Radius=86 StartAngle=1.27584 EndAngle=1.86575
    g5: ArcOfCircle CenterX=0 CenterY=-150 CenterZ=0 NormalX=0 NormalY=0 NormalZ=1 AngleXU=0 Radius=86 StartAngle=5.98823 EndAngle=6.57814
    g6: ArcOfCircle CenterX=0 CenterY=-150 CenterZ=0 NormalX=0 NormalY=0 NormalZ=1 AngleXU=0 Radius=86 StartAngle=2.84664 EndAngle=3.43655
    g7: ArcOfCircle CenterX=0 CenterY=-150 CenterZ=0 NormalX=0 NormalY=0 NormalZ=1 AngleXU=0 Radius=86 StartAngle=4.41743 EndAngle=5.00734
    g8: LineSegment StartX=25 StartY=-60.4232 StartZ=0 EndX=25 EndY=-67.7139 EndZ=0
    g9: LineSegment StartX=-25 StartY=-60.4232 StartZ=0 EndX=-25 EndY=-67.7139 EndZ=0
    g10: LineSegment StartX=-89.5768 StartY=-125 StartZ=0 EndX=-82.2861 EndY=-125 EndZ=0
    g11: LineSegment StartX=-89.5768 StartY=-175 StartZ=0 EndX=-82.2861 EndY=-175 EndZ=0
    g12: LineSegment StartX=-25 StartY=-239.577 StartZ=0 EndX=-25 EndY=-232.286 EndZ=0
    g13: LineSegment StartX=25 StartY=-239.577 StartZ=0 EndX=25 EndY=-232.286 EndZ=0
    g14: LineSegment StartX=89.5768 StartY=-175 StartZ=0 EndX=82.2861 EndY=-175 EndZ=0
    g15: LineSegment StartX=89.5768 StartY=-125 StartZ=0 EndX=82.2861 EndY=-125 EndZ=0
  constraints (49):
    c: PointOnObject(g0,g-2)
    c: Coincident(g1,g0)
    c: Coincident(g2,g0)
    c: Coincident(g3,g0)
    c: DistanceY(g0) = -150
    c: Coincident(g4,g0)
    c: Coincident(g5,g0)
    c: Coincident(g6,g0)
    c: Coincident(g7,g0)
    c: DistanceX(g4,g0) = 25
    c: DistanceX(g1,g4) = 0
    c: DistanceX(g0,g4) = 25
    c: DistanceX(g4,g1) = 0
    c: DistanceY(g0,g5) = 25
    c: DistanceY(g5,g2) = 0
    c: DistanceY(g2,g0) = 25
    c: DistanceY(g2,g5) = 0
    c: DistanceY(g6,g0) = 25
    c: DistanceY(g0,g6) = 0
    c: DistanceY(g0,g6) = 25
    c: DistanceY(g6,g0) = 0
    c: Equal(g1,g2)
    c: Equal(g1,g3)
    c: Equal(g1,g0)
    c: Radius(g1) = 93
    c: Equal(g6,g4)
    c: Equal(g6,g5)
    c: Equal(g6,g7)
    c: Radius(g6) = 86
    c: DistanceX(g0,g7) = 25
    c: DistanceX(g7,g3) = 0
    c: DistanceX(g3) = -25
    c: DistanceX(g3,g7) = 0
    c: Coincident(g8,g1)
    c: Coincident(g8,g4)
    c: Coincident(g9,g1)
    c: Coincident(g9,g4)
    c: Coincident(g10,g0)
    c: Coincident(g10,g6)
    c: Coincident(g11,g0)
    c: Coincident(g11,g6)
    c: Coincident(g12,g3)
    c: Coincident(g12,g7)
    c: Coincident(g13,g3)
    c: Coincident(g13,g7)
    c: Coincident(g14,g2)
    c: Coincident(g14,g5)
    c: Coincident(g15,g2)
    c: Coincident(g15,g5)
FEATURE [Part::Extrusion] Extrude055  label="srsHoldsLevel006"
  Base = -> Sketch154
  Dir = (0,0,1)
  DirMode = 2
  FaceMakerClass = Part::FaceMakerBullseye
  LengthFwd = 30
  LengthRev = 0
  Placement = pos=(0,0,-250) rot=(0,0,1;0rad)
  Solid = true
  Symmetric = false
FEATURE [Part::MultiFuse] Fusion130  label="level009"
  Shapes = -> [Extrude053,Extrude055]
FEATURE [Part::Cut] Cut095  label="level05s001"
  Base = -> Fusion130
  Tool = -> Fusion131
FEATURE [Part::Cut] Cut096  label="level5s009"
  Base = -> Cut095
  Tool = -> Extrude054
FEATURE [Sketcher::SketchObject] Sketch155
  FullyConstrained = true
  Placement = pos=(0,0,0) rot=(1,0,0;1.5708rad)
  sketch-geometry (8):
    g0: LineSegment StartX=-20.75 StartY=-250 StartZ=0 EndX=-12.75 EndY=-250 EndZ=0
    g1: LineSegment StartX=-12.75 StartY=-250 StartZ=0 EndX=-12.75 EndY=-275.75 EndZ=0
    g2: LineSegment StartX=-12.75 StartY=-275.75 StartZ=0 EndX=12.75 EndY=-275.75 EndZ=0
    g3: LineSegment StartX=12.75 StartY=-275.75 StartZ=0 EndX=12.75 EndY=-250 EndZ=0
    g4: LineSegment StartX=12.75 StartY=-250 StartZ=0 EndX=20.75 EndY=-250 EndZ=0
    g5: LineSegment StartX=20.75 StartY=-250 StartZ=0 EndX=20.75 EndY=-283.75 EndZ=0
    g6: LineSegment StartX=20.75 StartY=-283.75 StartZ=0 EndX=-20.75 EndY=-283.75 EndZ=0
    g7: LineSegment StartX=-20.75 StartY=-283.75 StartZ=0 EndX=-20.75 EndY=-250 EndZ=0
  constraints (24):
    c: Horizontal(g0)
    c: Vertical(g1)
    c: Coincident(g2,g1)
    c: Horizontal(g2)
    c: Vertical(g3)
    c: Coincident(g4,g3)
    c: Horizontal(g4)
    c: Coincident(g5,g4)
    c: Vertical(g5)
    c: Coincident(g6,g5)
    c: Horizontal(g6)
    c: Coincident(g7,g6)
    c: Coincident(g7,g0)
    c: Vertical(g7)
    c: Coincident(g0,g1)
    c: DistanceY(g0) = -250
    c: DistanceX(g0) = -12.75
    c: DistanceX(g3) = 12.75
    c: DistanceY(g1) = -275.75
    c: Coincident(g3,g2)
    c: DistanceY(g3,g0) = 0
    c: DistanceX(g0,g0) = 8
    c: DistanceX(g3,g4) = 8
    c: DistanceY(g5,g2) = 8
FEATURE [Part::Extrusion] Extrude056
  Base = -> Sketch155
  Dir = (0,-1,-3e-16)
  DirMode = 2
  FaceMakerClass = Part::FaceMakerBullseye
  LengthFwd = 100
  LengthRev = 0
  Placement = pos=(0,-70,0) rot=(0,0,1;0rad)
  Solid = true
  Symmetric = false
FEATURE [Part::Fillet] Fillet024
  Base = -> Extrude056
  Edges = 2 edges r=5: [Edge17,Edge20]
FEATURE [Part::Fillet] Fillet025  label="framingSupportsHolders001"
  Base = -> Fillet024
  Edges = 2 edges r=2: [Edge26,Edge28]
FEATURE [Part::MultiFuse] Fusion132
  Shapes = -> [Fillet025,Cut096]
FEATURE [Part::Fillet] Fillet026  label="level5s011"
  Base = -> Fusion132
  Edges = 2 edges r=5: [Edge40,Edge46]
FEATURE [Sketcher::SketchObject] Sketch156
  FullyConstrained = true
  sketch-geometry (2):
    g0: Circle CenterX=0 CenterY=-150 CenterZ=0 NormalX=0 NormalY=0 NormalZ=1 AngleXU=0 Radius=3.2
    g1: Circle CenterX=0 CenterY=-100 CenterZ=0 NormalX=0 NormalY=0 NormalZ=1 AngleXU=0 Radius=3.2
  constraints (6):
    c: PointOnObject(g0,g-2)
    c: PointOnObject(g1,g-2)
    c: DistanceY(g0) = -150
    c: DistanceY(g1) = -100
    c: Equal(g1,g0)
    c: Diameter(g1) = 6.4
FEATURE [Part::Extrusion] Extrude057
  Base = -> Sketch156
  Dir = (0,0,1)
  DirMode = 2
  FaceMakerClass = Part::FaceMakerBullseye
  LengthFwd = 50
  LengthRev = 0
  Placement = pos=(0,0,-290) rot=(0,0,1;0rad)
  Solid = true
  Symmetric = false
FEATURE [Part::Cut] Cut097  label="level5s010"
  Base = -> Fillet026
  Tool = -> Extrude057
FEATURE [Part::Fillet] Fillet027  label="level5sOriginal"
  Base = -> Cut097
  Edges = 4 edges r=2.5: [Edge111,Edge114,Edge117,Edge120]
FEATURE [Sketcher::SketchObject] Sketch157
  FullyConstrained = true
  sketch-geometry (27):
    g0: LineSegment StartX=38 StartY=-131 StartZ=0 EndX=76 EndY=-131 EndZ=0
    g1: LineSegment StartX=76 StartY=-131 StartZ=0 EndX=76 EndY=-169 EndZ=0
    g2: LineSegment StartX=76 StartY=-169 StartZ=0 EndX=38 EndY=-169 EndZ=0
    g3: LineSegment StartX=38 StartY=-169 StartZ=0 EndX=38 EndY=-131 EndZ=0
    g4: LineSegment StartX=-29 StartY=-210.392 StartZ=0 EndX=-23 EndY=-200 EndZ=0
    g5: LineSegment StartX=-23 StartY=-200 StartZ=0 EndX=-29 EndY=-189.608 EndZ=0
    g6: LineSegment StartX=-29 StartY=-189.608 StartZ=0 EndX=-41 EndY=-189.608 EndZ=0
    g7: LineSegment StartX=-41 StartY=-189.608 StartZ=0 EndX=-47 EndY=-200 EndZ=0
    g8: LineSegment StartX=-47 StartY=-200 StartZ=0 EndX=-41 EndY=-210.392 EndZ=0
    g9: LineSegment StartX=-41 StartY=-210.392 StartZ=0 EndX=-29 EndY=-210.392 EndZ=0
    g10: Circle CenterX=-35 CenterY=-200 CenterZ=0 NormalX=0 NormalY=0 NormalZ=1 AngleXU=0 Radius=12
    g11: LineSegment StartX=47 StartY=-220.785 StartZ=0 EndX=59 EndY=-200 EndZ=0
    g12: LineSegment StartX=59 StartY=-200 StartZ=0 EndX=47 EndY=-179.215 EndZ=0
    g13: LineSegment StartX=47 StartY=-179.215 StartZ=0 EndX=23 EndY=-179.215 EndZ=0
    g14: LineSegment StartX=23 StartY=-179.215 StartZ=0 EndX=11 EndY=-200 EndZ=0
    g15: LineSegment StartX=11 StartY=-200 StartZ=0 EndX=23 EndY=-220.785 EndZ=0
    g16: LineSegment StartX=23 StartY=-220.785 StartZ=0 EndX=47 EndY=-220.785 EndZ=0
    g17: Circle CenterX=35 CenterY=-200 CenterZ=0 NormalX=0 NormalY=0 NormalZ=1 AngleXU=0 Radius=24
    g18: LineSegment StartX=-50.3726 StartY=-166 StartZ=0 EndX=-41 EndY=-156.627 EndZ=0
    g19: LineSegment StartX=-41 StartY=-156.627 StartZ=0 EndX=-41 EndY=-143.373 EndZ=0
    g20: LineSegment StartX=-41 StartY=-143.373 StartZ=0 EndX=-50.3726 EndY=-134 EndZ=0
    g21: LineSegment StartX=-50.3726 StartY=-134 StartZ=0 EndX=-63.6274 EndY=-134 EndZ=0
    g22: LineSegment StartX=-63.6274 StartY=-134 StartZ=0 EndX=-73 EndY=-143.373 EndZ=0
    g23: LineSegment StartX=-73 StartY=-143.373 StartZ=0 EndX=-73 EndY=-156.627 EndZ=0
    g24: LineSegment StartX=-73 StartY=-156.627 StartZ=0 EndX=-63.6274 EndY=-166 EndZ=0
    g25: LineSegment StartX=-63.6274 StartY=-166 StartZ=0 EndX=-50.3726 EndY=-166 EndZ=0
    g26: Circle CenterX=-57 CenterY=-150 CenterZ=0 NormalX=0 NormalY=0 NormalZ=1 AngleXU=0 Radius=17.3183
  constraints (67):
    c: Coincident(g0,g1)
    c: Coincident(g1,g2)
    c: Coincident(g2,g3)
    c: Coincident(g3,g0)
    c: Horizontal(g0)
    c: Horizontal(g2)
    c: Vertical(g1)
    c: Vertical(g3)
    c: DistanceX(g2) = 38
    c: DistanceX(g2,g2) = 38
    c: DistanceY(g2,g0) = 38
    c: DistanceY(g2) = -169
    c: Coincident(g4,g5)
    c: Coincident(g5,g6)
    c: Coincident(g6,g7)
    c: Coincident(g7,g8)
    c: Coincident(g8,g9)
    c: Coincident(g9,g4)
    c: Equal(g4, g5-g9) x5
    c: PointOnObject(g4,g10)
    c: PointOnObject(g5,g10)
    c: PointOnObject(g6,g10)
    c: PointOnObject(g7,g10)
    c: PointOnObject(g8,g10)
    c: PointOnObject(g9,g10)
    c: Horizontal(g9)
    c: DistanceX(g10) = -35
    c: DistanceY(g10) = -200
    c: DistanceX(g9,g9) = 12
    c: Coincident(g11,g12)
    c: Coincident(g12,g13)
    c: Coincident(g13,g14)
    c: Coincident(g14,g15)
    c: Coincident(g15,g16)
    c: Coincident(g16,g11)
    c: Equal(g11, g12-g16) x5
    c: PointOnObject(g11,g17)
    c: PointOnObject(g12,g17)
    c: PointOnObject(g13,g17)
    c: PointOnObject(g14,g17)
    c: PointOnObject(g15,g17)
    c: PointOnObject(g16,g17)
    c: DistanceX(g17) = 35
    c: DistanceY(g17) = -200
    c: Horizontal(g16)
    c: DistanceX(g16,g16) = 24
    c: Coincident(g18,g19)
    c: Coincident(g19,g20)
    c: Coincident(g20,g21)
    c: Coincident(g21,g22)
    c: Coincident(g22,g23)
    c: Coincident(g23,g24)
    c: Coincident(g24,g25)
    c: Coincident(g25,g18)
    c: Equal(g18, g19-g25) x7
    c: PointOnObject(g18,g26)
    c: PointOnObject(g19,g26)
    c: PointOnObject(g20,g26)
    c: PointOnObject(g21,g26)
    c: PointOnObject(g22,g26)
    c: PointOnObject(g23,g26)
    c: PointOnObject(g24,g26)
    c: PointOnObject(g25,g26)
    c: Horizontal(g25)
    c: DistanceY(g26) = -150
    c: DistanceX(g26) = -57
    c: DistanceX(g23,g18) = 32
FEATURE [Part::Extrusion] Extrude058  label="level5Cuts"
  Base = -> Sketch157
  Dir = (0,0,1)
  DirMode = 2
  FaceMakerClass = Part::FaceMakerBullseye
  LengthFwd = 10
  LengthRev = 0
  Placement = pos=(0,0,-246) rot=(0,0,1;0rad)
  Solid = true
  Symmetric = false
FEATURE [Part::MultiFuse] Fusion133  label="level5Cuts001"
  Shapes = -> [Extrude058,Extrude044]
FEATURE [Part::MultiFuse] Fusion134  label="level5s013"
  Shapes = -> [Cut041,Extrude036]
FEATURE [Part::Feature] Part__Feature201  label="47065T139_T-Slotted Framing"
  Placement = pos=(0,-100,-244) rot=(1,0,0;1.5708rad)
  shape: bbox 25.4 x 11.25 x 17.44 mm, 56 faces, 2 solids (baked)
FEATURE [Sketcher::SketchObject] Sketch158
  FullyConstrained = true
  Placement = pos=(0,0,-244) rot=(0,0,1;0rad)
  sketch-geometry (2):
    g0: Circle CenterX=0 CenterY=-100 CenterZ=0 NormalX=0 NormalY=0 NormalZ=1 AngleXU=0 Radius=7
    g1: Circle CenterX=0 CenterY=-150 CenterZ=0 NormalX=0 NormalY=0 NormalZ=1 AngleXU=0 Radius=7
  constraints (6):
    c: PointOnObject(g0,g-2)
    c: DistanceY(g1) = -150
    c: DistanceX(g1) = 0
    c: DistanceY(g1,g0) = 50
    c: Equal(g0,g1)
    c: Diameter(g0) = 14
FEATURE [Part::Extrusion] Extrude059
  Base = -> Sketch158
  Dir = (0,0,1)
  DirMode = 2
  FaceMakerClass = Part::FaceMakerBullseye
  LengthFwd = 2
  LengthRev = 0
  Solid = true
  Symmetric = false
FEATURE [Sketcher::SketchObject] Sketch159
  FullyConstrained = true
  Placement = pos=(0,0,-244) rot=(0,0,1;0rad)
  sketch-geometry (2):
    g0: Circle CenterX=0 CenterY=-100 CenterZ=0 NormalX=0 NormalY=0 NormalZ=1 AngleXU=0 Radius=7
    g1: Circle CenterX=0 CenterY=-150 CenterZ=0 NormalX=0 NormalY=0 NormalZ=1 AngleXU=0 Radius=7
  constraints (6):
    c: PointOnObject(g0,g-2)
    c: DistanceY(g1) = -150
    c: DistanceX(g1) = 0
    c: DistanceY(g1,g0) = 50
    c: Equal(g0,g1)
    c: Diameter(g0) = 14
FEATURE [Part::Extrusion] Extrude060
  Base = -> Sketch159
  Dir = (0,0,1)
  DirMode = 2
  FaceMakerClass = Part::FaceMakerBullseye
  LengthFwd = 2
  LengthRev = 0
  Placement = pos=(0,0,-40) rot=(0,0,1;0rad)
  Solid = true
  Symmetric = false
FEATURE [Part::MultiFuse] Fusion135  label="tSlotCuts"
  Shapes = -> [Extrude059,Extrude060]
FEATURE [Part::MultiFuse] Fusion136  label="level5Cuts002"
  Shapes = -> [Fusion133,Fusion135]
FEATURE [Part::Cut] Cut098  label="level010"
  Base = -> Fusion134
  Tool = -> Fusion136
FEATURE [Part::Fillet] Fillet028
  Base = -> Cut098
  Edges = 4 edges r=2: [Edge44,Edge46,Edge146,Edge149]
FEATURE [Part::Fillet] Fillet029  label="level5s014"
  Base = -> Fillet028
  Edges = 4 edges r=5: [Edge5,Edge35,Edge51,Edge101]
FEATURE [Part::Fillet] Fillet030  label="level5s015"
  Base = -> Fillet029
  Edges = 4 edges r=2.5: [Edge131,Edge134,Edge137,Edge140]
